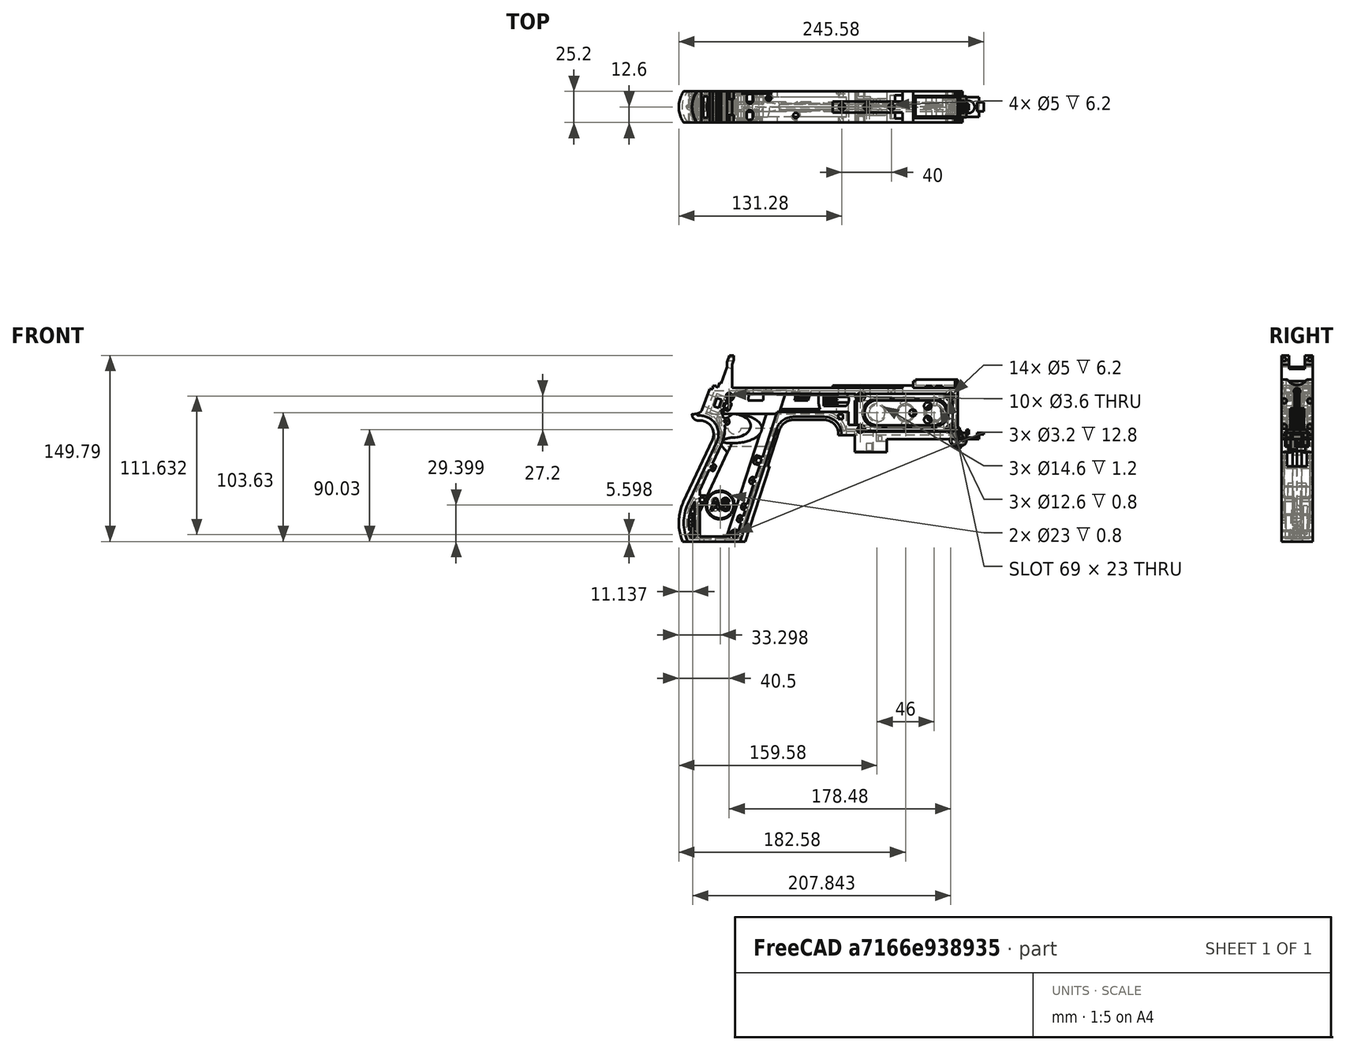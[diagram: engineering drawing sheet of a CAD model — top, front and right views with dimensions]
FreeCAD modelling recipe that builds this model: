
FCSTD DOCUMENT  (FreeCAD 1.0R39319 (Git))
Label: PICON-OF_ver_65
License: All rights reserved
LicenseURL: https://en.wikipedia.org/wiki/All_rights_reserved
objects: Sketcher::SketchObject×132, Part::Extrusion×66, Part::Cut×51, PartDesign::Pad×34, PartDesign::Pocket×21, PartDesign::Chamfer×15, PartDesign::Body×11, PartDesign::Fillet×6, Part::MultiFuse×5, Part::Part2DObjectPython×4, PartDesign::SubtractivePipe×4, PartDesign::SubtractiveLoft×4, PartDesign::Plane×3, PartDesign::SubShapeBinder×2, Part::Sweep×1, PartDesign::ShapeBinder×1, Mesh::Feature×1, PartDesign::Point×1, PartDesign::Groove×1
note: 664 computed .brp shape members not serialized (recipe doc carries the construction recipe); baked Part::Feature solids carry a one-line shape summary decoded from their .brp

FEATURE [Sketcher::SketchObject] Sketch  label="corpo principale"
  ArcFitTolerance = 1e-06
  AttacherType = Attacher::AttachEngine3D
  AttachmentSupport = -> [XZ_Plane]
  FullyConstrained = true
  MakeInternals = false
  MapMode = 5
  Placement = pos=(0,0,0) rot=(1,0,0;1.5708rad)
  sketch-geometry (65):
    g0: LineSegment StartX=0 StartY=0 StartZ=0 EndX=-57.2 EndY=0 EndZ=0
    g1: LineSegment StartX=-57.2 StartY=0 StartZ=0 EndX=-57.2 EndY=-10.4 EndZ=0
    g2: LineSegment StartX=-57.2 StartY=-10.4 StartZ=0 EndX=-82.8 EndY=-10.4 EndZ=0
    g3: LineSegment StartX=-82.8 StartY=-10.4 StartZ=0 EndX=-82.8 EndY=3.2 EndZ=0
    g4: LineSegment StartX=-82.8 StartY=3.2 StartZ=0 EndX=-93.6 EndY=3.2 EndZ=0
    g5: LineSegment StartX=-93.6 StartY=3.2 StartZ=0 EndX=-93.6 EndY=4 EndZ=0
    g6: LineSegment StartX=-107.6 StartY=18 StartZ=0 EndX=-132.428 EndY=18 EndZ=0
    g7: LineSegment StartX=-145.743 StartY=8.32624 StartZ=0 EndX=-175.232 EndY=-82.4316 EndZ=0
    g8: LineSegment StartX=-175.232 StartY=-82.4316 StartZ=0 EndX=-217.232 EndY=-82.4316 EndZ=0
    g9: LineSegment StartX=-217.232 StartY=-52.1862 StartZ=0 EndX=-193.988 EndY=-2.33927 EndZ=0
    g10: LineSegment StartX=-206.196 StartY=23.0857 StartZ=0 EndX=-199.861 EndY=40.4914 EndZ=0
    g11: LineSegment StartX=-199.861 StartY=40.4914 StartZ=0 EndX=-197.061 EndY=40.4914 EndZ=0
    g12: LineSegment StartX=-197.061 StartY=40.4914 StartZ=0 EndX=-197.061 EndY=42.8914 EndZ=0
    g13: LineSegment StartX=-197.061 StartY=42.8914 StartZ=0 EndX=-194.261 EndY=42.8914 EndZ=0
    g14: LineSegment StartX=-194.261 StartY=42.8914 StartZ=0 EndX=-194.535 EndY=42.1397 EndZ=0
    g15: LineSegment StartX=-194.535 StartY=42.1397 StartZ=0 EndX=-193.031 EndY=41.5924 EndZ=0
    g16: LineSegment StartX=-193.031 StartY=41.5924 StartZ=0 EndX=-191.663 EndY=45.3512 EndZ=0
    g17: LineSegment StartX=-191.663 StartY=45.3512 StartZ=0 EndX=-190.536 EndY=44.9408 EndZ=0
    g18: LineSegment StartX=-190.536 StartY=44.9408 StartZ=0 EndX=-185.747 EndY=58.0965 EndZ=0
    g19: LineSegment StartX=-185.747 StartY=58.0965 StartZ=0 EndX=-185.747 EndY=62.0965 EndZ=0
    g20: LineSegment StartX=-185.747 StartY=62.0965 StartZ=0 EndX=-183.832 EndY=67.3588 EndZ=0
    g21: LineSegment StartX=-183.832 StartY=67.3588 StartZ=0 EndX=-180.232 EndY=67.3588 EndZ=0
    g22: LineSegment StartX=-180.232 StartY=67.3588 StartZ=0 EndX=-180.232 EndY=63.7588 EndZ=0
    g23: LineSegment StartX=-180.232 StartY=63.7588 StartZ=0 EndX=-181.6 EndY=60 EndZ=0
    g24: LineSegment StartX=-181.6 StartY=60 StartZ=0 EndX=-181.6 EndY=41.2 EndZ=0
    g25: LineSegment StartX=-181.6 StartY=41.2 StartZ=0 EndX=-100.8 EndY=41.2 EndZ=0
    g26: LineSegment StartX=-36 StartY=43.2 StartZ=0 EndX=-36 EndY=41.2 EndZ=0
    g27: LineSegment StartX=0 StartY=48 StartZ=0 EndX=0 EndY=0 EndZ=0
    g28: LineSegment StartX=-209.901 StartY=19.85 StartZ=0 EndX=-209.901 EndY=20.1 EndZ=0
    g29: LineSegment StartX=-208.001 StartY=22 StartZ=0 EndX=-207.747 EndY=22 EndZ=0
    g30: LineSegment StartX=-207.583 StartY=19 StartZ=0 EndX=-209.051 EndY=19 EndZ=0
    g31: ArcOfCircle CenterX=-208.001 CenterY=20.1 CenterZ=0 NormalX=0 NormalY=0 NormalZ=1 AngleXU=0 Radius=1.9 StartAngle=1.5708 EndAngle=3.14159
    g32: GeomPoint [constr] X=-209.901 Y=22 Z=0
    g33: ArcOfCircle CenterX=-209.051 CenterY=19.85 CenterZ=0 NormalX=0 NormalY=0 NormalZ=1 AngleXU=0 Radius=0.85 StartAngle=3.14159 EndAngle=4.71239
    g34: GeomPoint [constr] X=-209.901 Y=19 Z=0
    g35: ArcOfCircle CenterX=-207.747 CenterY=23.65 CenterZ=0 NormalX=0 NormalY=0 NormalZ=1 AngleXU=0 Radius=1.65 StartAngle=4.71239 EndAngle=5.93412
    g36: GeomPoint [constr] X=-206.591 Y=22 Z=0
    g37: LineSegment StartX=-4 StartY=6 StartZ=0 EndX=-4 EndY=36.4 EndZ=0
    g38: LineSegment StartX=-4 StartY=36.4 StartZ=0 EndX=-185.2 EndY=36.4 EndZ=0
    g39: LineSegment StartX=-185.2 StartY=36.4 StartZ=0 EndX=-190.441 EndY=22 EndZ=0
    g40: LineSegment StartX=-214.575 StartY=-78.4316 StartZ=0 EndX=-178.142 EndY=-78.4316 EndZ=0
    g41: LineSegment StartX=-178.142 StartY=-78.4316 StartZ=0 EndX=-145.51 EndY=22 EndZ=0
    g42: LineSegment StartX=-145.51 StartY=22 StartZ=0 EndX=-87.91 EndY=22 EndZ=0
    g43: LineSegment StartX=-87.91 StartY=22 StartZ=0 EndX=-87.91 EndY=11.6 EndZ=0
    g44: LineSegment StartX=-87.91 StartY=11.6 StartZ=0 EndX=-80.11 EndY=11.6 EndZ=0
    g45: LineSegment StartX=-80.11 StartY=11.6 StartZ=0 EndX=-80.11 EndY=6 EndZ=0
    g46: LineSegment StartX=-80.11 StartY=6 StartZ=0 EndX=-4 EndY=6 EndZ=0
    g47: LineSegment StartX=-190.363 StartY=-4.02975 StartZ=0 EndX=-213.607 EndY=-53.8767 EndZ=0
    g48: ArcOfCircle CenterX=-132.428 CenterY=4 CenterZ=0 NormalX=0 NormalY=0 NormalZ=1 AngleXU=0 Radius=14 StartAngle=1.5708 EndAngle=2.82743
    g49: GeomPoint [constr] X=-142.6 Y=18 Z=0
    g50: ArcOfCircle CenterX=-107.6 CenterY=4 CenterZ=0 NormalX=0 NormalY=0 NormalZ=1 AngleXU=0 Radius=14 StartAngle=0 EndAngle=1.5708
    g51: GeomPoint [constr] X=-93.6 Y=18 Z=0
    g52: ArcOfCircle CenterX=-184.801 CenterY=-67.3089 CenterZ=0 NormalX=0 NormalY=0 NormalZ=1 AngleXU=0 Radius=35.7833 StartAngle=2.70526 EndAngle=3.57792
    g53: ArcOfCircle CenterX=-207.583 CenterY=4 CenterZ=0 NormalX=0 NormalY=0 NormalZ=1 AngleXU=0 Radius=15 StartAngle=5.84685 EndAngle=7.85398
    g54: LineSegment [constr] StartX=-213.607 StartY=-53.8767 StartZ=0 EndX=-217.232 EndY=-52.1862 EndZ=0
    g55: ArcOfCircle CenterX=-184.801 CenterY=-67.3089 CenterZ=0 NormalX=0 NormalY=0 NormalZ=1 AngleXU=0 Radius=31.7833 StartAngle=2.70526 EndAngle=3.49911
    g56: ArcOfCircle CenterX=-218.095 CenterY=8.90192 CenterZ=0 NormalX=0 NormalY=0 NormalZ=1 AngleXU=0 Radius=30.5989 StartAngle=5.84685 EndAngle=6.72553
    g57: LineSegment StartX=-44.6 StartY=43.2 StartZ=0 EndX=-36 EndY=43.2 EndZ=0
    g58: LineSegment StartX=-100.8 StartY=41.2 StartZ=0 EndX=-44.6 EndY=41.2 EndZ=0
    g59: LineSegment StartX=-44.6 StartY=41.2 StartZ=0 EndX=-44.6 EndY=43.2 EndZ=0
    g60: LineSegment StartX=-2.4 StartY=48 StartZ=0 EndX=0 EndY=48 EndZ=0
    g61: LineSegment StartX=-36 StartY=41.2 StartZ=0 EndX=-2.4 EndY=41.2 EndZ=0
    g62: LineSegment StartX=-2.4 StartY=41.2 StartZ=0 EndX=-2.4 EndY=48 EndZ=0
    g63: LineSegment [constr] StartX=-181.6 StartY=36.4 StartZ=0 EndX=-152.209 EndY=36.4 EndZ=0
    g64: LineSegment [constr] StartX=-181.6 StartY=36.4 StartZ=0 EndX=-130.41 EndY=36.4 EndZ=0
  constraints (183):
    c: Coincident(g-1,g0)
    c: PointOnObject(g0,g-1)
    c: Coincident(g0,g1)
    c: Vertical(g1)
    c: Coincident(g1,g2)
    c: Horizontal(g2)
    c: Coincident(g2,g3)
    c: Vertical(g3)
    c: Coincident(g3,g4)
    c: Coincident(g4,g5)
    c: Vertical(g5)
    c: Horizontal(g6)
    c: Coincident(g7,g8)
    c: Horizontal(g8)
    c: Coincident(g10,g11)
    c: Horizontal(g11)
    c: Coincident(g11,g12)
    c: Vertical(g12)
    c: Coincident(g12,g13)
    c: Horizontal(g13)
    c: Coincident(g13,g14)
    c: Coincident(g14,g15)
    c: Coincident(g15,g16)
    c: Coincident(g16,g17)
    c: Coincident(g17,g18)
    c: Coincident(g18,g19)
    c: Vertical(g19)
    c: Coincident(g19,g20)
    c: Coincident(g20,g21)
    c: Horizontal(g21)
    c: Coincident(g21,g22)
    c: Vertical(g22)
    c: Coincident(g22,g23)
    c: Coincident(g23,g24)
    c: Vertical(g24)
    c: Coincident(g24,g25)
    c: Horizontal(g25)
    c: Coincident(g57,g26)
    c: Vertical(g26)
    c: Coincident(g26,g61)
    c: PointOnObject(g60,g-2)
    c: Coincident(g60,g27)
    c: Coincident(g27,g0)
    c: DistanceY(g27,g27) = 48
    c: DistanceY(g1,g1) = 10.4
    c: DistanceX(g0,g0) = 57.2
    c: DistanceX(g2,g2) = 25.6
    c: Horizontal(g4)
    c: DistanceY(g3,g3) = 13.6
    c: DistanceX(g4,g4) = 10.8
    c: DistanceY(g5,g51) = 14.8
    c: DistanceX(g49,g51) = 49
    c: Distance(g7,g49) = 105.6
    c: DistanceX(g61,g60) = 36
    c: DistanceX(g25,g25) = 80.8
    c: DistanceY(g24,g24) = 18.8
    c: DistanceY(g22,g22) = 3.6
    c: Distance(g23) = 4
    c: Angle(g-1,g23) = 1.22173
    c: DistanceX(g21,g21) = 3.6
    c: Distance(g20) = 5.6
    c: Angle(g-1,g20) = 1.22173
    c: DistanceY(g19,g19) = 4
    c: Distance(g18) = 14
    c: Angle(g-1,g18) = 1.22173
    c: Distance(g17) = 1.2
    c: Distance(g16) = 4
    c: Angle(g16) = 1.22173
    c: Perpendicular(g18,g17)
    c: Distance(g15) = 1.6
    c: Perpendicular(g16,g15)
    c: Distance(g14) = 0.8
    c: DistanceX(g13,g13) = 2.8
    c: Perpendicular(g15,g14)
    c: DistanceY(g12,g12) = 2.4
    c: DistanceX(g11,g11) = 2.8
    c: Distance(g9) = 55
    c: Angle(g9,g-1) = 2.00713
    c: Horizontal(g29)
    c: Vertical(g28)
    c: Horizontal(g30)
    c: PointOnObject(g32,g29)
    c: PointOnObject(g32,g28)
    c: Tangent(g29,g31) = 1.5708
    c: Tangent(g28,g31) = 1.5708
    c: PointOnObject(g34,g28)
    c: PointOnObject(g34,g30)
    c: Tangent(g28,g33) = 1.5708
    c: Tangent(g30,g33) = 1.5708
    c: PointOnObject(g36,g29)
    c: PointOnObject(g36,g10)
    c: Tangent(g29,g35) = -1.5708
    c: Tangent(g10,g35) = -1.5708
    c: Angle(g-1,g10) = 1.22173
    c: Radius(g35) = 1.65
    c: Vertical(g37)
    c: Coincident(g37,g38)
    c: Horizontal(g38)
    c: Coincident(g38,g39)
    c: Horizontal(g40)
    c: Coincident(g40,g41)
    c: Coincident(g41,g42)
    c: Horizontal(g42)
    c: Coincident(g42,g43)
    c: Vertical(g43)
    c: Coincident(g43,g44)
    c: Horizontal(g44)
    c: Coincident(g44,g45)
    c: Vertical(g45)
    c: Coincident(g45,g46)
    c: Coincident(g46,g37)
    c: Horizontal(g46)
    c: DistanceY(g0,g37) = 6
    c: DistanceX(g37,g0) = 4
    c: DistanceY(g37,g25) = 4.8
    c: DistanceX(g38,g38) = 181.2
    c: DistanceX(g42,g42) = 57.6
    c: DistanceY(g49,g41) = 4
    c: DistanceX(g41,g49) = 2.91
    c: DistanceY(g43,g43) = 10.4
    c: DistanceX(g44,g44) = 7.8
    c: DistanceY(g7,g40) = 4
    c: Distance(g47) = 55
    c: Angle(g-1,g39) = 1.22173
    c: PointOnObject(g49,g7)
    c: PointOnObject(g49,g6)
    c: Tangent(g7,g48) = -1.5708
    c: Tangent(g6,g48) = -1.5708
    c: PointOnObject(g51,g5)
    c: PointOnObject(g51,g6)
    c: Tangent(g5,g50) = -1.5708
    c: Tangent(g6,g50) = -1.5708
    c: Radius(g50) = 14
    c: Radius(g48) = 14
    c: DistanceX(g8,g8) = 42
    c: Angle(g7,g-1) = 1.88496
    c: Parallel(g41,g7)
    c: Parallel(g47,g9)
    c: Coincident(g52,g8)
    c: Tangent(g52,g9) = 1.5708
    c: DistanceX(g9,g8) = 0
    c: Tangent(g53,g9) = -1.5708
    c: Tangent(g53,g30) = -1.5708
    c: Diameter(g53) = 30
    c: DistanceY(g53,g0) = -4
    c: Coincident(g54,g47)
    c: Distance(g54) = 4
    c: Coincident(g54,g9)
    c: Coincident(g55,g40)
    c: Tangent(g55,g47) = -1.5708
    c: Coincident(g52,g55)
    c: Coincident(g56,g39)
    c: Tangent(g56,g47) = 1.5708
    c: Horizontal(g57)
    c: DistanceX(g57,g57) = 8.6
    c: Coincident(g58,g25)
    c: Horizontal(g58)
    c: Coincident(g59,g58)
    c: Vertical(g59)
    c: DistanceY(g58,g57) = 2
    c: DistanceX(g58,g58) = 56.2
    c: Coincident(g59,g57)
    c: DistanceY(g41,g36) = 0
    c: DistanceY(g36,g39) = 0
    c: DistanceY(g28,g28) = 0.25
    c: DistanceX(g30,g36) = 2.46
    c: DistanceX(g28,g29) = 1.9
    c: Coincident(g62,g60)
    c: Horizontal(g60)
    c: DistanceX(g62,g27) = 2.4
    c: Coincident(g61,g62)
    c: DistanceY(g26,g26) = 2
    c: Vertical(g62)
    c: DistanceY(g61,g60) = 6.8
    c: Horizontal(g61)
    c: Distance(g63) = 29.391
    c: PointOnObject(g63,g38)
    c: PointOnObject(g63,g38)
    c: Distance(g64) = 51.19
    c: PointOnObject(g64,g38)
    c: PointOnObject(g64,g38)
    c: DistanceX(g24,g63) = 0
    c: DistanceX(g24,g64) = 0
FEATURE [Part::Extrusion] Extrude  label="Extrude corpo principale"
  Base = -> Sketch
  Dir = (0,-1,2e-16)
  DirMode = 2
  FaceMakerClass = Part::FaceMakerBullseye
  FaceMakerMode = 3
  LengthFwd = 25.2
  LengthRev = 12.6
  Solid = true
  Symmetric = true
FEATURE [Sketcher::SketchObject] Sketch002  label="scavo grilletto"
  ArcFitTolerance = 1e-06
  AttachmentSupport = -> [XZ_Plane]
  ExternalGeometry = -> [Sketch]
  FullyConstrained = true
  MakeInternals = false
  MapMode = 5
  Placement = pos=(0,0,0) rot=(1,0,0;1.5708rad)
  sketch-geometry (4):
    g0: LineSegment StartX=-89.51 StartY=22 StartZ=0 EndX=-152.71 EndY=22 EndZ=0
    g1: LineSegment StartX=-152.71 StartY=22 StartZ=0 EndX=-167.006 EndY=-22 EndZ=0
    g2: LineSegment StartX=-167.006 StartY=-22 StartZ=0 EndX=-89.51 EndY=-22 EndZ=0
    g3: LineSegment StartX=-89.51 StartY=-22 StartZ=0 EndX=-89.51 EndY=22 EndZ=0
  constraints (12):
    c: Horizontal(g0)
    c: Coincident(g0,g1)
    c: Coincident(g1,g2)
    c: Horizontal(g2)
    c: Coincident(g2,g3)
    c: Coincident(g3,g0)
    c: Vertical(g3)
    c: Angle(g1,g0) = 1.88496
    c: DistanceY(g3,g3) = 44
    c: DistanceX(g0,g0) = 63.2
    c: DistanceX(g0,g-3) = 1.6
    c: DistanceY(g-3,g0) = 0
FEATURE [Sketcher::SketchObject] Sketch004  label="traiettoria arrotondamento impugnatura anteriore"
  ArcFitTolerance = 1e-06
  AttachmentSupport = -> [XZ_Plane]
  ExternalGeometry = -> [Sketch]
  FullyConstrained = true
  MakeInternals = false
  MapMode = 5
  Placement = pos=(0,0,0) rot=(1,0,0;1.5708rad)
  sketch-geometry (13):
    g0: LineSegment StartX=-175.232 StartY=-82.4316 StartZ=0 EndX=-145.743 EndY=8.32624 EndZ=0
    g1: LineSegment StartX=-93.6 StartY=3.2 StartZ=0 EndX=-93.6 EndY=4 EndZ=0
    g2: LineSegment StartX=-132.428 StartY=18 StartZ=0 EndX=-107.6 EndY=18 EndZ=0
    g3: ArcOfCircle CenterX=-132.428 CenterY=4 CenterZ=0 NormalX=0 NormalY=0 NormalZ=1 AngleXU=0 Radius=14 StartAngle=1.5708 EndAngle=2.82743
    g4: ArcOfCircle CenterX=-107.6 CenterY=4 CenterZ=0 NormalX=0 NormalY=0 NormalZ=1 AngleXU=0 Radius=14 StartAngle=0 EndAngle=1.5708
    g5: LineSegment StartX=-175.232 StartY=-82.4316 StartZ=0 EndX=-217.232 EndY=-82.4316 EndZ=0
    g6: LineSegment StartX=-217.232 StartY=-52.1862 StartZ=0 EndX=-193.988 EndY=-2.33927 EndZ=0
    g7: LineSegment StartX=-209.051 StartY=19 StartZ=0 EndX=-207.583 EndY=19 EndZ=0
    g8: LineSegment StartX=-209.901 StartY=20.1 StartZ=0 EndX=-209.901 EndY=19.85 EndZ=0
    g9: ArcOfCircle CenterX=-184.801 CenterY=-67.3089 CenterZ=0 NormalX=0 NormalY=0 NormalZ=1 AngleXU=0 Radius=35.7833 StartAngle=2.70526 EndAngle=3.57792
    g10: ArcOfCircle CenterX=-207.583 CenterY=4 CenterZ=0 NormalX=0 NormalY=0 NormalZ=1 AngleXU=0 Radius=15 StartAngle=5.84685 EndAngle=7.85398
    g11: ArcOfCircle CenterX=-209.051 CenterY=19.85 CenterZ=0 NormalX=0 NormalY=0 NormalZ=1 AngleXU=0 Radius=0.85 StartAngle=3.14159 EndAngle=4.71239
    g12: ArcOfCircle CenterX=-208.001 CenterY=20.1 CenterZ=0 NormalX=0 NormalY=0 NormalZ=1 AngleXU=0 Radius=1.9 StartAngle=1.5708 EndAngle=3.14159
  constraints (26):
    c: Coincident(g0,g-3)
    c: Coincident(g0,g-6)
    c: Coincident(g1,g-8)
    c: Coincident(g1,g-7)
    c: Coincident(g2,g-5)
    c: Coincident(g2,g-4)
    c: Coincident(g3,g2)
    c: Tangent(g3,g0) = 1.5708
    c: Coincident(g4,g1)
    c: Tangent(g4,g2) = 1.5708
    c: Coincident(g5,g0)
    c: Coincident(g5,g-9)
    c: Coincident(g6,g-12)
    c: Coincident(g6,g-11)
    c: Coincident(g7,g-15)
    c: Coincident(g7,g-14)
    c: Coincident(g8,g-16)
    c: Coincident(g8,g-17)
    c: Tangent(g9,g6) = 1.5708
    c: Coincident(g9,g5)
    c: Coincident(g10,g7)
    c: Tangent(g10,g6) = -1.5708
    c: Tangent(g11,g7) = -1.5708
    c: Coincident(g11,g8)
    c: Tangent(g12,g8) = -1.5708
    c: Coincident(g12,g-17)
FEATURE [PartDesign::Plane] DatumPlane  label="Piano per disegno arrotondamento impugnatura"
  AttachmentSupport = -> [Sketch]
  Length = 73.6581
  MapMode = 7
  Placement = pos=(-145.743,1.8e-15,8.32624) rot=(0.154555,0.154555,0.97582;1.59527rad)
  ResizeMode = 0
  Width = 303.511
FEATURE [Sketcher::SketchObject] Sketch005  label="forma arrotondamento impugnatura anteriore"
  ArcFitTolerance = 1e-06
  AttachmentSupport = -> [DatumPlane]
  FullyConstrained = true
  MakeInternals = false
  MapMode = 5
  Placement = pos=(-145.743,1.8e-15,8.32624) rot=(0.154555,0.154555,0.97582;1.59527rad)
  sketch-geometry (5):
    g0: GeomPoint [constr] X=0 Y=-4 Z=0
    g1: GeomPoint [constr] X=-12.6 Y=7.1e-15 Z=0
    g2: GeomPoint [constr] X=12.6 Y=4.97e-14 Z=0
    g3: LineSegment StartX=-12.6 StartY=7.1e-15 StartZ=0 EndX=12.6 EndY=4.97e-14 EndZ=0
    g4: ArcOfCircle CenterX=-3.88e-14 CenterY=17.845 CenterZ=0 NormalX=0 NormalY=0 NormalZ=1 AngleXU=0 Radius=21.845 StartAngle=4.09759 EndAngle=5.32718
  constraints (11):
    c: DistanceY(g0,g-1) = 4
    c: DistanceX(g-1,g0) = 0
    c: DistanceX(g1,g-1) = 12.6
    c: DistanceX(g-1,g2) = 12.6
    c: DistanceY(g-1,g2) = 0
    c: DistanceY(g-1,g1) = 0
    c: Coincident(g3,g1)
    c: Coincident(g3,g2)
    c: Coincident(g4,g1)
    c: Coincident(g4,g2)
    c: PointOnObject(g0,g4)
FEATURE [Part::Sweep] Sweep  label="Sweep impugnatura"
  Frenet = true
  Sections = -> [Sketch005]
  Solid = true
  Spine = -> Sketch [Edge32,Edge33,Edge34,Edge35,Edge36,Edge37,Edge38,Edge39,Edge40,Edge41,Edge42,Edge43,Edge44]
  Transition = 1
FEATURE [Sketcher::SketchObject] Sketch008  label="buchi e pulizie varie"
  ArcFitTolerance = 1e-06
  AttachmentSupport = -> [XZ_Plane]
  ExternalGeometry = -> [Sketch]
  FullyConstrained = true
  MakeInternals = false
  MapMode = 5
  Placement = pos=(0,0,0) rot=(1,0,0;1.5708rad)
  sketch-geometry (26):
    g0: LineSegment StartX=-96.278 StartY=20.155 StartZ=0 EndX=-92.278 EndY=20.155 EndZ=0
    g1: LineSegment StartX=-92.278 StartY=20.155 StartZ=0 EndX=-92.278 EndY=16.155 EndZ=0
    g2: LineSegment StartX=-92.278 StartY=16.155 StartZ=0 EndX=-96.278 EndY=16.155 EndZ=0
    g3: LineSegment StartX=-96.278 StartY=16.155 StartZ=0 EndX=-96.278 EndY=20.155 EndZ=0
    g4: LineSegment StartX=-222.232 StartY=-82.4316 StartZ=0 EndX=-170.232 EndY=-82.4316 EndZ=0
    g5: LineSegment StartX=-170.232 StartY=-82.4316 StartZ=0 EndX=-170.232 EndY=-86.4316 EndZ=0
    g6: LineSegment StartX=-170.232 StartY=-86.4316 StartZ=0 EndX=-222.232 EndY=-86.4316 EndZ=0
    g7: LineSegment StartX=-222.232 StartY=-86.4316 StartZ=0 EndX=-222.232 EndY=-82.4316 EndZ=0
    g8: LineSegment StartX=-213.901 StartY=20.1 StartZ=0 EndX=-213.901 EndY=26 EndZ=0
    g9: LineSegment StartX=-213.901 StartY=26 StartZ=0 EndX=-206.196 EndY=26 EndZ=0
    g10: LineSegment StartX=-17.4 StartY=42.8 StartZ=0 EndX=-12.4 EndY=42.8 EndZ=0
    g11: LineSegment StartX=-12.4 StartY=42.8 StartZ=0 EndX=-12.4 EndY=41.2 EndZ=0
    g12: LineSegment StartX=-12.4 StartY=41.2 StartZ=0 EndX=-17.4 EndY=41.2 EndZ=0
    g13: LineSegment StartX=-17.4 StartY=41.2 StartZ=0 EndX=-17.4 EndY=42.8 EndZ=0
    g14: LineSegment StartX=-25.9 StartY=42.8 StartZ=0 EndX=-20.9 EndY=42.8 EndZ=0
    g15: LineSegment StartX=-20.9 StartY=42.8 StartZ=0 EndX=-20.9 EndY=41.2 EndZ=0
    g16: LineSegment StartX=-20.9 StartY=41.2 StartZ=0 EndX=-25.9 EndY=41.2 EndZ=0
    g17: LineSegment StartX=-25.9 StartY=41.2 StartZ=0 EndX=-25.9 EndY=42.8 EndZ=0
    g18: GeomPoint [constr] X=-206.196 Y=23.0857 Z=0
    g19: GeomPoint [constr] X=-213.901 Y=20.1 Z=0
    g20: BSplineCurve PolesCount=4 KnotsCount=2 Degree=3 IsPeriodic=0
    g21-g24: Circle [constr] x4 (B-spline internal-alignment scaffolding for g20; pole/knot coordinates omitted)
    g25: LineSegment StartX=-206.196 StartY=26 StartZ=0 EndX=-206.196 EndY=23.0857 EndZ=0
  constraints (73):
    c: Horizontal(g0)
    c: Coincident(g1,g0)
    c: Vertical(g1)
    c: Coincident(g2,g1)
    c: Horizontal(g2)
    c: Coincident(g3,g2)
    c: Coincident(g3,g0)
    c: Vertical(g3)
    c: DistanceX(g0,g-4) = 4.368
    c: DistanceY(g0,g-4) = 1.845
    c: DistanceY(g1,g1) = 4
    c: DistanceX(g2,g2) = 4
    c: Horizontal(g4)
    c: Coincident(g5,g4)
    c: Vertical(g5)
    c: Coincident(g6,g5)
    c: Horizontal(g6)
    c: Coincident(g7,g6)
    c: Coincident(g7,g4)
    c: Vertical(g7)
    c: DistanceY(g7,g7) = 4
    c: DistanceX(g4,g-5) = 5
    c: DistanceX(g-5,g4) = 5
    c: DistanceY(g4,g-5) = 0
    c: Coincident(g9,g8)
    c: Parallel(g9,g-6)
    c: DistanceX(g8,g-8) = 4
    c: Horizontal(g10)
    c: Coincident(g11,g10)
    c: Vertical(g11)
    c: Coincident(g12,g11)
    c: Horizontal(g12)
    c: Coincident(g13,g12)
    c: Coincident(g13,g10)
    c: Vertical(g13)
    c: Horizontal(g14)
    c: Coincident(g15,g14)
    c: Vertical(g15)
    c: Coincident(g16,g15)
    c: Horizontal(g16)
    c: Coincident(g17,g16)
    c: Coincident(g17,g14)
    c: Vertical(g17)
    c: DistanceY(g11,g10) = 1.6
    c: DistanceX(g10,g10) = 5
    c: DistanceY(g15,g14) = 1.6
    c: DistanceX(g14,g14) = 5
    c: DistanceX(g15,g12) = 3.5
    c: DistanceX(g11,g-9) = 10
    c: DistanceY(g-9,g11) = 0
    c: DistanceY(g-9,g15) = 0
    c: Perpendicular(g8,g9)
    c: DistanceY(g-7,g9) = 4
    c: DistanceY(g8,g-8) = 0
    c: InternalAlignment(g18,g20)
    c: InternalAlignment(g19,g20)
    c: InternalAlignment(g21,g20)
    c: Weight(g21) = 1
    c: InternalAlignment(g22,g20)
    c: Equal(g22,g21)
    c: InternalAlignment(g23,g20)
    c: Equal(g23,g21)
    c: InternalAlignment(g24,g20)
    c: Equal(g24,g21)
    c: Coincident(g18,g-12)
    c: Coincident(g19,g8)
    c: Coincident(g25,g9)
    c: Coincident(g25,g20)
    c: Vertical(g25)
    c: DistanceY(g20,g23) = 0
    c: DistanceY(g22,g18) = 2.26
    c: DistanceX(g22,g18) = 0.93
    c: DistanceX(g20,g23) = 2.9
FEATURE [Part::Extrusion] Extrude004  label="Extrude Buchi e pulizie varie"
  Base = -> Sketch008
  Dir = (0,-1,2e-16)
  DirMode = 2
  FaceMakerClass = Part::FaceMakerBullseye
  FaceMakerMode = 3
  LengthFwd = 25.2
  LengthRev = 0
  Solid = true
  Symmetric = true
FEATURE [Sketcher::SketchObject] Sketch009  label="rinforzi"
  ArcFitTolerance = 1e-06
  AttachmentSupport = -> [XZ_Plane]
  ExternalGeometry = -> [Sketch]
  FullyConstrained = true
  MakeInternals = false
  MapMode = 5
  Placement = pos=(0,0,0) rot=(1,0,0;1.5708rad)
  sketch-geometry (9):
    g0: LineSegment StartX=-87.91 StartY=22 StartZ=0 EndX=-87.91 EndY=36.4 EndZ=0
    g1: LineSegment StartX=-87.91 StartY=36.4 StartZ=0 EndX=-97.91 EndY=36.4 EndZ=0
    g2: LineSegment StartX=-97.91 StartY=36.4 StartZ=0 EndX=-97.91 EndY=22 EndZ=0
    g3: LineSegment StartX=-97.91 StartY=22 StartZ=0 EndX=-87.91 EndY=22 EndZ=0
    g4: LineSegment StartX=-149.713 StartY=9.06563 StartZ=0 EndX=-154.586 EndY=-5.93437 EndZ=0
    g5: LineSegment StartX=-154.586 StartY=-5.93437 StartZ=0 EndX=-191.863 EndY=-5.93437 EndZ=0
    g6: LineSegment StartX=-191.863 StartY=-5.93437 StartZ=0 EndX=-191.863 EndY=9.06563 EndZ=0
    g7: LineSegment StartX=-191.863 StartY=9.06563 StartZ=0 EndX=-149.713 EndY=9.06563 EndZ=0
    g8: LineSegment [constr] StartX=-145.51 StartY=22 StartZ=0 EndX=-149.713 EndY=9.06563 EndZ=0
  constraints (25):
    c: Vertical(g0)
    c: Coincident(g1,g0)
    c: Horizontal(g1)
    c: Coincident(g2,g1)
    c: Vertical(g2)
    c: Coincident(g3,g2)
    c: Coincident(g3,g0)
    c: Horizontal(g3)
    c: Coincident(g0,g-4)
    c: DistanceX(g3,g3) = 10
    c: DistanceY(g0,g-3) = 0
    c: Coincident(g5,g4)
    c: Horizontal(g5)
    c: Coincident(g6,g5)
    c: Vertical(g6)
    c: Coincident(g7,g6)
    c: Coincident(g7,g4)
    c: Horizontal(g7)
    c: Distance(g8) = 13.6
    c: Parallel(g-6,g8)
    c: Coincident(g-6,g8)
    c: Parallel(g4,g-6)
    c: DistanceY(g4,g4) = 15
    c: Coincident(g4,g8)
    c: DistanceX(g-5,g5) = -1.5
FEATURE [Part::Extrusion] Extrude001  label="Extrude scavo grilletto"
  Base = -> Sketch002
  Dir = (0,-1,2e-16)
  DirMode = 2
  FaceMakerClass = Part::FaceMakerBullseye
  FaceMakerMode = 3
  LengthFwd = 16
  LengthRev = 0
  Solid = true
  Symmetric = true
FEATURE [Part::Extrusion] Extrude005  label="Extrude Rinforzi"
  Base = -> Sketch009
  Dir = (0,-1,2e-16)
  DirMode = 2
  FaceMakerClass = Part::FaceMakerBullseye
  FaceMakerMode = 3
  LengthFwd = 2
  LengthRev = 0
  Placement = pos=(0,12.6,0) rot=(0,0,1;0rad)
  Solid = true
  Symmetric = false
FEATURE [PartDesign::ShapeBinder] CopyCut
  TraceSupport = false
FEATURE [PartDesign::Plane] DatumPlane001
  AttachmentSupport = -> [CopyCut]
  Length = 283.944
  MapMode = 5
  Placement = pos=(0,12.6,0) rot=(0,0.707107,0.707107;3.14159rad)
  ResizeMode = 0
  Width = 188.15
FEATURE [Sketcher::SketchObject] Sketch010  label="buco neopixel"
  ArcFitTolerance = 1e-06
  AttachmentSupport = -> [XZ_Plane]
  ExternalGeometry = -> [Sketch]
  FullyConstrained = true
  MakeInternals = false
  MapMode = 5
  Placement = pos=(0,0,0) rot=(1,0,0;1.5708rad)
  sketch-geometry (5):
    g0: LineSegment [constr] StartX=-199.861 StartY=40.4914 StartZ=0 EndX=-201.368 EndY=36.3521 EndZ=0
    g1: LineSegment StartX=-201.368 StartY=36.3521 StartZ=0 EndX=-204.932 EndY=26.5605 EndZ=0
    g2: LineSegment StartX=-201.368 StartY=36.3521 StartZ=0 EndX=-180.2 EndY=28.6477 EndZ=0
    g3: LineSegment StartX=-180.2 StartY=28.6477 StartZ=0 EndX=-183.764 EndY=18.8561 EndZ=0
    g4: LineSegment StartX=-183.764 StartY=18.8561 StartZ=0 EndX=-204.932 EndY=26.5605 EndZ=0
  constraints (14):
    c: Parallel(g0,g-3)
    c: Distance(g0) = 4.405
    c: Coincident(g0,g-3)
    c: Coincident(g2,g1)
    c: Coincident(g3,g2)
    c: Coincident(g4,g3)
    c: Coincident(g4,g1)
    c: Parallel(g1,g-3)
    c: Distance(g1) = 10.42
    c: Coincident(g1,g0)
    c: Parallel(g2,g4)
    c: Perpendicular(g1,g2)
    c: DistanceX(g-4,g2) = 5
    c: Parallel(g3,g1)
FEATURE [Part::Extrusion] Extrude006  label="Extrude buco neopixel"
  Base = -> Sketch010
  Dir = (0,-1,2e-16)
  DirMode = 2
  FaceMakerClass = Part::FaceMakerBullseye
  FaceMakerMode = 3
  LengthFwd = 17.2
  LengthRev = 0
  Solid = true
  Symmetric = true
FEATURE [Sketcher::SketchObject] Sketch011  label="fermo grilletto"
  ArcFitTolerance = 1e-06
  AttachmentSupport = -> [XZ_Plane]
  ExternalGeometry = -> [Sketch]
  FullyConstrained = true
  MakeInternals = false
  MapMode = 5
  Placement = pos=(0,0,0) rot=(1,0,0;1.5708rad)
  sketch-geometry (18):
    g0: LineSegment [constr] StartX=-145.51 StartY=22 StartZ=0 EndX=-157.347 EndY=-14.4293 EndZ=0
    g1: LineSegment [constr] StartX=-157.347 StartY=-14.4293 StartZ=0 EndX=-157.841 EndY=-15.951 EndZ=0
    g2: LineSegment StartX=-161.151 StartY=-13.1932 StartZ=0 EndX=-155.825 EndY=-14.9237 EndZ=0
    g3: LineSegment StartX=-163.167 StartY=-14.2205 StartZ=0 EndX=-164.403 EndY=-18.0247 EndZ=0
    g4: LineSegment StartX=-163.376 StartY=-20.0408 StartZ=0 EndX=-158.05 EndY=-21.7713 EndZ=0
    g5: LineSegment StartX=-158.05 StartY=-21.7713 StartZ=0 EndX=-155.825 EndY=-14.9237 EndZ=0
    g6: LineSegment StartX=-161.645 StartY=-14.7149 StartZ=0 EndX=-157.841 EndY=-15.951 EndZ=0
    g7: LineSegment StartX=-157.841 StartY=-15.951 StartZ=0 EndX=-159.077 EndY=-19.7552 EndZ=0
    g8: LineSegment StartX=-159.077 StartY=-19.7552 StartZ=0 EndX=-162.881 EndY=-18.5191 EndZ=0
    g9: LineSegment StartX=-162.881 StartY=-18.5191 StartZ=0 EndX=-161.645 EndY=-14.7149 EndZ=0
    g10: LineSegment [constr] StartX=-161.645 StartY=-14.7149 StartZ=0 EndX=-161.151 EndY=-13.1932 EndZ=0
    g11: LineSegment [constr] StartX=-159.077 StartY=-19.7552 StartZ=0 EndX=-157.555 EndY=-20.2496 EndZ=0
    g12: LineSegment [constr] StartX=-159.077 StartY=-19.7552 StartZ=0 EndX=-159.572 EndY=-21.2769 EndZ=0
    g13: LineSegment [constr] StartX=-161.645 StartY=-14.7149 StartZ=0 EndX=-163.167 EndY=-14.2205 EndZ=0
    g14: ArcOfCircle CenterX=-161.645 CenterY=-14.7149 CenterZ=0 NormalX=0 NormalY=0 NormalZ=1 AngleXU=0 Radius=1.6 StartAngle=1.25664 EndAngle=2.82743
    g15: GeomPoint [constr] X=-162.673 Y=-12.6988 Z=0
    g16: ArcOfCircle CenterX=-162.881 CenterY=-18.5191 CenterZ=0 NormalX=0 NormalY=0 NormalZ=1 AngleXU=0 Radius=1.6 StartAngle=2.82743 EndAngle=4.39823
    g17: GeomPoint [constr] X=-164.897 Y=-19.5464 Z=0
  constraints (48):
    c: Parallel(g0,g-3)
    c: Distance(g0) = 38.304
    c: Coincident(g0,g-3)
    c: Parallel(g1,g-3)
    c: Distance(g1) = 1.6
    c: Coincident(g1,g0)
    c: Coincident(g5,g4)
    c: Coincident(g5,g2)
    c: Coincident(g7,g6)
    c: Coincident(g8,g7)
    c: Coincident(g9,g8)
    c: Coincident(g9,g6)
    c: Parallel(g7,g-3)
    c: Parallel(g9,g7)
    c: Perpendicular(g6,g7)
    c: Parallel(g6,g8)
    c: Distance(g6) = 4
    c: Distance(g9) = 4
    c: Parallel(g5,g7)
    c: Parallel(g9,g3)
    c: Parallel(g2,g6)
    c: Parallel(g4,g8)
    c: Parallel(g13,g6)
    c: Parallel(g10,g9)
    c: Parallel(g11,g8)
    c: Parallel(g12,g7)
    c: Distance(g10) = 1.6
    c: Distance(g13) = 1.6
    c: Distance(g12) = 1.6
    c: Distance(g11) = 1.6
    c: Coincident(g10,g6)
    c: Coincident(g13,g6)
    c: Coincident(g12,g7)
    c: Coincident(g11,g7)
    c: Distance(g10,g15) = 1.6
    c: Distance(g15,g13) = 1.6
    c: Distance(g4,g12) = 1.6
    c: Distance(g4,g11) = 1.6
    c: PointOnObject(g15,g2)
    c: Tangent(g3,g14) = -1.5708
    c: Tangent(g2,g14) = 1.5708
    c: PointOnObject(g17,g4)
    c: PointOnObject(g17,g3)
    c: Tangent(g4,g16) = -1.5708
    c: Tangent(g3,g16) = -1.5708
    c: Equal(g16,g14)
    c: Coincident(g16,g8)
    c: Coincident(g6,g1)
FEATURE [Part::Extrusion] Extrude007  label="Extrude fermo grilletto"
  Base = -> Sketch011
  Dir = (0,-1,2e-16)
  DirMode = 2
  FaceMakerClass = Part::FaceMakerBullseye
  FaceMakerMode = 3
  LengthFwd = 25.2
  LengthRev = 0
  Solid = true
  Symmetric = true
FEATURE [Sketcher::SketchObject] Sketch012  label="buco oled"
  ArcFitTolerance = 1e-06
  AttachmentSupport = -> [XZ_Plane]
  ExternalGeometry = -> [Sketch]
  FullyConstrained = true
  MakeInternals = false
  MapMode = 5
  Placement = pos=(0,0,0) rot=(1,0,0;1.5708rad)
  sketch-geometry (4):
    g0: LineSegment StartX=-185.747 StartY=58.0965 StartZ=0 EndX=-180.232 EndY=56.0891 EndZ=0
    g1: LineSegment StartX=-185.747 StartY=58.0965 StartZ=0 EndX=-185.747 EndY=67.3588 EndZ=0
    g2: LineSegment StartX=-185.747 StartY=67.3588 StartZ=0 EndX=-180.232 EndY=67.3588 EndZ=0
    g3: LineSegment StartX=-180.232 StartY=67.3588 StartZ=0 EndX=-180.232 EndY=56.0891 EndZ=0
  constraints (10):
    c: Coincident(g1,g0)
    c: Coincident(g2,g1)
    c: Coincident(g3,g2)
    c: Coincident(g3,g0)
    c: Parallel(g1,g-5)
    c: Perpendicular(g-3,g0)
    c: Parallel(g2,g-6)
    c: Parallel(g3,g-4)
    c: Coincident(g0,g-5)
    c: Coincident(g2,g-6)
FEATURE [Part::Extrusion] Extrude008  label="Extrude buco oled"
  Base = -> Sketch012
  Dir = (0,-1,2e-16)
  DirMode = 2
  FaceMakerClass = Part::FaceMakerBullseye
  FaceMakerMode = 3
  LengthFwd = 12.8
  LengthRev = 0
  Solid = true
  Symmetric = true
FEATURE [Sketcher::SketchObject] Sketch013  label="buco pompa"
  ArcFitTolerance = 1e-06
  AttachmentSupport = -> [XZ_Plane]
  ExternalGeometry = -> [Sketch]
  FullyConstrained = true
  MakeInternals = false
  MapMode = 5
  Placement = pos=(0,0,0) rot=(1,0,0;1.5708rad)
  sketch-geometry (8):
    g0: LineSegment StartX=-82.8 StartY=-10.4 StartZ=0 EndX=-82.8 EndY=-9.6 EndZ=0
    g1: LineSegment StartX=-82.8 StartY=-9.6 StartZ=0 EndX=-67.9 EndY=-9.6 EndZ=0
    g2: LineSegment StartX=-67.9 StartY=-9.6 StartZ=0 EndX=-67.9 EndY=6 EndZ=0
    g3: LineSegment StartX=-67.9 StartY=6 StartZ=0 EndX=-65.9 EndY=6 EndZ=0
    g4: LineSegment StartX=-65.9 StartY=6 StartZ=0 EndX=-65.9 EndY=-1.7 EndZ=0
    g5: LineSegment StartX=-65.9 StartY=-1.7 StartZ=0 EndX=-57.2 EndY=-1.7 EndZ=0
    g6: LineSegment StartX=-57.2 StartY=-1.7 StartZ=0 EndX=-57.2 EndY=-10.4 EndZ=0
    g7: LineSegment StartX=-57.2 StartY=-10.4 StartZ=0 EndX=-82.8 EndY=-10.4 EndZ=0
  constraints (22):
    c: Vertical(g0)
    c: Coincident(g1,g0)
    c: Horizontal(g1)
    c: Coincident(g2,g1)
    c: Vertical(g2)
    c: Coincident(g3,g2)
    c: Horizontal(g3)
    c: Coincident(g4,g3)
    c: Vertical(g4)
    c: Coincident(g5,g4)
    c: Horizontal(g5)
    c: Coincident(g6,g5)
    c: Vertical(g6)
    c: Coincident(g7,g6)
    c: Coincident(g7,g0)
    c: DistanceY(g0,g0) = 0.8
    c: DistanceY(g6,g6) = 8.7
    c: DistanceX(g1,g1) = 14.9
    c: DistanceX(g3,g3) = 2
    c: Coincident(g0,g-4)
    c: DistanceY(g2,g-6) = 0
    c: Coincident(g6,g-5)
FEATURE [Part::Extrusion] Extrude009  label="Extrude buco pompa"
  Base = -> Sketch013
  Dir = (0,-1,2e-16)
  DirMode = 2
  FaceMakerClass = Part::FaceMakerBullseye
  FaceMakerMode = 3
  LengthFwd = 13.2
  LengthRev = 0
  Solid = true
  Symmetric = true
FEATURE [Sketcher::SketchObject] Sketch014  label="buco frontale"
  ArcFitTolerance = 1e-06
  AttachmentSupport = -> [XZ_Plane]
  ExternalGeometry = -> [Sketch]
  FullyConstrained = true
  MakeInternals = false
  MapMode = 5
  Placement = pos=(0,0,0) rot=(1,0,0;1.5708rad)
  sketch-geometry (10):
    g0: LineSegment StartX=0 StartY=0 StartZ=0 EndX=0 EndY=24.671 EndZ=0
    g1: LineSegment StartX=0 StartY=24.671 StartZ=0 EndX=-4 EndY=24.671 EndZ=0
    g2: LineSegment StartX=-4 StartY=24.671 StartZ=0 EndX=-4 EndY=16 EndZ=0
    g3: LineSegment StartX=-4 StartY=16 StartZ=0 EndX=-2.4 EndY=16 EndZ=0
    g4: LineSegment StartX=-2.4 StartY=16 StartZ=0 EndX=-2.4 EndY=10 EndZ=0
    g5: LineSegment StartX=-2.4 StartY=10 StartZ=0 EndX=-12 EndY=10 EndZ=0
    g6: LineSegment StartX=-12 StartY=10 StartZ=0 EndX=-12 EndY=6 EndZ=0
    g7: LineSegment StartX=-12 StartY=6 StartZ=0 EndX=-2.4 EndY=6 EndZ=0
    g8: LineSegment StartX=-2.4 StartY=6 StartZ=0 EndX=-2.4 EndY=0 EndZ=0
    g9: LineSegment StartX=-2.4 StartY=0 StartZ=0 EndX=0 EndY=0 EndZ=0
  constraints (29):
    c: Vertical(g0)
    c: Coincident(g1,g0)
    c: Horizontal(g1)
    c: Coincident(g2,g1)
    c: Vertical(g2)
    c: Coincident(g3,g2)
    c: Horizontal(g3)
    c: Coincident(g4,g3)
    c: Vertical(g4)
    c: Coincident(g5,g4)
    c: Horizontal(g5)
    c: Coincident(g6,g5)
    c: Vertical(g6)
    c: Coincident(g7,g6)
    c: Coincident(g8,g7)
    c: Vertical(g8)
    c: Coincident(g9,g8)
    c: Coincident(g9,g0)
    c: Horizontal(g9)
    c: DistanceY(g0,g0) = 24.671
    c: Horizontal(g7)
    c: DistanceY(g6,g6) = 4
    c: DistanceY(g4,g4) = 6
    c: DistanceX(g9,g9) = 2.4
    c: Coincident(g0,g-1)
    c: DistanceY(g-3,g7) = 0
    c: DistanceX(g8,g4) = 0
    c: DistanceX(g-3,g1) = 0
    c: DistanceX(g6,g-3) = 8
FEATURE [Part::Extrusion] Extrude010  label="Extrude buco frontale"
  Base = -> Sketch014
  Dir = (0,-1,2e-16)
  DirMode = 2
  FaceMakerClass = Part::FaceMakerBullseye
  FaceMakerMode = 3
  LengthFwd = 11.2
  LengthRev = 0
  Solid = true
  Symmetric = true
FEATURE [Sketcher::SketchObject] Sketch015  label="guida rail"
  ArcFitTolerance = 1e-06
  AttachmentSupport = -> [XZ_Plane]
  ExternalGeometry = -> [Sketch]
  FullyConstrained = true
  MakeInternals = false
  MapMode = 5
  Placement = pos=(0,0,0) rot=(1,0,0;1.5708rad)
  sketch-geometry (4):
    g0: LineSegment StartX=-100.8 StartY=43.2 StartZ=0 EndX=-44.6 EndY=43.2 EndZ=0
    g1: LineSegment StartX=-44.6 StartY=43.2 StartZ=0 EndX=-44.6 EndY=41.2 EndZ=0
    g2: LineSegment StartX=-44.6 StartY=41.2 StartZ=0 EndX=-100.8 EndY=41.2 EndZ=0
    g3: LineSegment StartX=-100.8 StartY=41.2 StartZ=0 EndX=-100.8 EndY=43.2 EndZ=0
  constraints (9):
    c: Horizontal(g0)
    c: Coincident(g1,g0)
    c: Coincident(g2,g1)
    c: Coincident(g3,g2)
    c: Coincident(g3,g0)
    c: Vertical(g3)
    c: Coincident(g2,g-3)
    c: Coincident(g1,g-3)
    c: Coincident(g0,g-4)
FEATURE [Part::Extrusion] Extrude011  label="Extrude guida rail"
  Base = -> Sketch015
  Dir = (0,-1,2e-16)
  DirMode = 2
  FaceMakerClass = Part::FaceMakerBullseye
  FaceMakerMode = 3
  LengthFwd = 9
  LengthRev = 0
  Solid = true
  Symmetric = true
FEATURE [Sketcher::SketchObject] Sketch016  label="guide per coperture laterali"
  ArcFitTolerance = 1e-06
  AttachmentSupport = -> [XZ_Plane]
  ExternalGeometry = -> [Sketch]
  FullyConstrained = true
  MakeInternals = false
  MapMode = 5
  Placement = pos=(0,0,0) rot=(1,0,0;1.5708rad)
  sketch-geometry (14):
    g0: Circle CenterX=-5.6 CenterY=7.6 CenterZ=0 NormalX=0 NormalY=0 NormalZ=1 AngleXU=0 Radius=1.6
    g1: Circle CenterX=-5.6 CenterY=7.6 CenterZ=0 NormalX=0 NormalY=0 NormalZ=1 AngleXU=0 Radius=4
    g2: Circle CenterX=-5.6 CenterY=34.8 CenterZ=0 NormalX=0 NormalY=0 NormalZ=1 AngleXU=0 Radius=1.6
    g3: Circle CenterX=-5.6 CenterY=34.8 CenterZ=0 NormalX=0 NormalY=0 NormalZ=1 AngleXU=0 Radius=4
    g4: Circle CenterX=-184.08 CenterY=34.8 CenterZ=0 NormalX=0 NormalY=0 NormalZ=1 AngleXU=0 Radius=1.6
    g5: Circle CenterX=-184.08 CenterY=34.8 CenterZ=0 NormalX=0 NormalY=0 NormalZ=1 AngleXU=0 Radius=4
    g6: Circle CenterX=-179.305 CenterY=-76.8316 CenterZ=0 NormalX=0 NormalY=0 NormalZ=1 AngleXU=0 Radius=1.6
    g7: Circle CenterX=-179.305 CenterY=-76.8316 CenterZ=0 NormalX=0 NormalY=0 NormalZ=1 AngleXU=0 Radius=4
    g8: Circle CenterX=-213.443 CenterY=-76.8316 CenterZ=0 NormalX=0 NormalY=0 NormalZ=1 AngleXU=0 Radius=1.6
    g9: Circle CenterX=-213.443 CenterY=-76.8316 CenterZ=0 NormalX=0 NormalY=0 NormalZ=1 AngleXU=0 Radius=4
    g10: Circle CenterX=-78.51 CenterY=7.6 CenterZ=0 NormalX=0 NormalY=0 NormalZ=1 AngleXU=0 Radius=1.6
    g11: Circle CenterX=-78.51 CenterY=7.6 CenterZ=0 NormalX=0 NormalY=0 NormalZ=1 AngleXU=0 Radius=4
    g12: Circle CenterX=-78.51 CenterY=34.8 CenterZ=0 NormalX=0 NormalY=0 NormalZ=1 AngleXU=0 Radius=1.6
    g13: Circle CenterX=-78.51 CenterY=34.8 CenterZ=0 NormalX=0 NormalY=0 NormalZ=1 AngleXU=0 Radius=4
  constraints (35):
    c: Diameter(g0) = 3.2
    c: Diameter(g1) = 8
    c: Coincident(g0,g1)
    c: Diameter(g2) = 3.2
    c: Diameter(g3) = 8
    c: Coincident(g3,g2)
    c: Tangent(g2,g-7)
    c: Diameter(g4) = 3.2
    c: Diameter(g5) = 8
    c: Coincident(g5,g4)
    c: Tangent(g4,g-7)
    c: Tangent(g4,g-8)
    c: Diameter(g6) = 3.2
    c: Diameter(g7) = 8
    c: Coincident(g7,g6)
    c: Tangent(g6,g-9)
    c: Tangent(g6,g-10)
    c: Diameter(g8) = 3.2
    c: Diameter(g9) = 8
    c: Coincident(g9,g8)
    c: Tangent(g8,g-10)
    c: Tangent(g8,g-11)
    c: Diameter(g10) = 3.2
    c: Diameter(g11) = 8
    c: Diameter(g12) = 3.2
    c: Diameter(g13) = 8
    c: Coincident(g12,g13)
    c: Coincident(g10,g11)
    c: Tangent(g12,g-7)
    c: DistanceX(g12,g10) = 0
    c: Tangent(g2,g-6)
    c: Tangent(g0,g-6)
    c: Tangent(g0,g-3)
    c: Tangent(g10,g-3)
    c: Tangent(g10,g-4)
FEATURE [Part::Extrusion] Extrude012  label="extrude guide per coperture laterali"
  Base = -> Sketch016
  Dir = (0,-1,2e-16)
  DirMode = 2
  FaceMakerClass = Part::FaceMakerBullseye
  FaceMakerMode = 3
  LengthFwd = 25.2
  LengthRev = 0
  Solid = true
  Symmetric = true
FEATURE [Sketcher::SketchObject] Sketch017  label="supporto CAM"
  ArcFitTolerance = 1e-06
  AttachmentSupport = -> [XZ_Plane]
  ExternalGeometry = -> [Sketch]
  FullyConstrained = true
  MakeInternals = false
  MapMode = 5
  Placement = pos=(0,0,0) rot=(1,0,0;1.5708rad)
  sketch-geometry (6):
    g0: LineSegment StartX=-2.4 StartY=48 StartZ=0 EndX=-2.4 EndY=41.2 EndZ=0
    g1: LineSegment StartX=-2.4 StartY=48 StartZ=0 EndX=-34 EndY=48 EndZ=0
    g2: LineSegment StartX=-34 StartY=48 StartZ=0 EndX=-34 EndY=46.72 EndZ=0
    g3: LineSegment StartX=-34 StartY=46.72 StartZ=0 EndX=-36 EndY=46.72 EndZ=0
    g4: LineSegment StartX=-36 StartY=46.72 StartZ=0 EndX=-36 EndY=41.2 EndZ=0
    g5: LineSegment StartX=-36 StartY=41.2 StartZ=0 EndX=-2.4 EndY=41.2 EndZ=0
  constraints (15):
    c: Coincident(g1,g0)
    c: Horizontal(g1)
    c: Coincident(g2,g1)
    c: Vertical(g2)
    c: Coincident(g3,g2)
    c: Horizontal(g3)
    c: Coincident(g4,g3)
    c: Coincident(g5,g4)
    c: DistanceX(g1,g0) = 31.6
    c: Coincident(g5,g0)
    c: Vertical(g4)
    c: DistanceY(g2,g1) = 1.28
    c: Coincident(g0,g-3)
    c: Coincident(g0,g-3)
    c: Coincident(g4,g-4)
FEATURE [Part::Extrusion] Extrude013  label="Extrude supporto CAM"
  Base = -> Sketch017
  Dir = (0,-1,2e-16)
  DirMode = 2
  FaceMakerClass = Part::FaceMakerBullseye
  FaceMakerMode = 3
  LengthFwd = 17.8
  LengthRev = 0
  Solid = true
  Symmetric = true
FEATURE [Sketcher::SketchObject] Sketch018  label="Scavo CAM"
  ArcFitTolerance = 1e-06
  AttachmentSupport = -> [YZ_Plane]
  ExternalGeometry = -> [Sketch]
  FullyConstrained = true
  MakeInternals = false
  MapMode = 5
  Placement = pos=(0,0,0) rot=(0.57735,0.57735,0.57735;2.0944rad)
  sketch-geometry (4):
    g0: LineSegment StartX=-7.73 StartY=48 StartZ=0 EndX=7.73 EndY=48 EndZ=0
    g1: LineSegment [constr] StartX=1.07e-14 StartY=48 StartZ=0 EndX=0 EndY=43.5155 EndZ=0
    g2: ArcOfCircle CenterX=9e-15 CenterY=52.42 CenterZ=0 NormalX=0 NormalY=0 NormalZ=1 AngleXU=0 Radius=8.90445 StartAngle=3.66102 EndAngle=5.76376
    g3: Circle [constr] CenterX=9e-15 CenterY=52.42 CenterZ=0 NormalX=0 NormalY=0 NormalZ=1 AngleXU=0 Radius=8.9
  constraints (13):
    c: Horizontal(g0)
    c: DistanceY(g-3,g0) = 0
    c: DistanceX(g0,g0) = 15.46
    c: DistanceX(g0,g-3) = 7.73
    c: DistanceX(g-3) = 0
    c: Coincident(g1,g-3)
    c: PointOnObject(g1,g-2)
    c: Coincident(g2,g0)
    c: Coincident(g2,g0)
    c: PointOnObject(g1,g2)
    c: Diameter(g3) = 17.8
    c: DistanceY(g1,g3) = 4.42
    c: Coincident(g2,g3)
FEATURE [Part::Extrusion] Extrude014  label="Extrude Scavo CAM"
  Base = -> Sketch018
  Dir = (1,0,0)
  DirMode = 2
  FaceMakerClass = Part::FaceMakerBullseye
  FaceMakerMode = 3
  LengthFwd = -34
  LengthRev = 0
  Solid = true
  Symmetric = false
FEATURE [Sketcher::SketchObject] Sketch019  label="scavo rumble"
  ArcFitTolerance = 1e-06
  AttachmentSupport = -> [XZ_Plane]
  ExternalGeometry = -> [Sketch]
  FullyConstrained = true
  MakeInternals = false
  MapMode = 5
  Placement = pos=(0,0,0) rot=(1,0,0;1.5708rad)
  sketch-geometry (6):
    g0: LineSegment StartX=-168.716 StartY=-37.1227 StartZ=0 EndX=-163.58 EndY=-38.7914 EndZ=0
    g1: LineSegment StartX=-163.58 StartY=-38.7914 StartZ=0 EndX=-170.687 EndY=-60.6657 EndZ=0
    g2: LineSegment StartX=-170.687 StartY=-60.6657 StartZ=0 EndX=-175.823 EndY=-58.997 EndZ=0
    g3: LineSegment StartX=-175.823 StartY=-58.997 StartZ=0 EndX=-168.716 EndY=-37.1227 EndZ=0
    g4: LineSegment [constr] StartX=-145.51 StartY=22 StartZ=0 EndX=-165.102 EndY=-38.297 EndZ=0
    g5: LineSegment [constr] StartX=-163.58 StartY=-38.7914 StartZ=0 EndX=-165.102 EndY=-38.297 EndZ=0
  constraints (17):
    c: Coincident(g1,g0)
    c: Coincident(g2,g1)
    c: Coincident(g3,g2)
    c: Coincident(g3,g0)
    c: Parallel(g3,g-3)
    c: Parallel(g3,g1)
    c: Perpendicular(g3,g0)
    c: Perpendicular(g2,g3)
    c: Distance(g2,g0) = 23
    c: Parallel(g4,g-3)
    c: Distance(g4) = 63.4
    c: Coincident(g4,g-3)
    c: Parallel(g5,g0)
    c: Coincident(g5,g0)
    c: Coincident(g5,g4)
    c: Distance(g4,g0) = 3.8
    c: Distance(g4,g0) = 1.6
FEATURE [Part::Extrusion] Extrude015  label="scavo rumble001"
  Base = -> Sketch019
  Dir = (0,-1,2e-16)
  DirMode = 2
  FaceMakerClass = Part::FaceMakerBullseye
  FaceMakerMode = 3
  LengthFwd = 21
  LengthRev = 0
  Solid = true
  Symmetric = true
FEATURE [Sketcher::SketchObject] Sketch020  label="fermo rumble"
  ArcFitTolerance = 1e-06
  AttachmentSupport = -> [XZ_Plane]
  ExternalGeometry = -> [Sketch019,Sketch]
  FullyConstrained = true
  MakeInternals = false
  MapMode = 5
  Placement = pos=(0,0,0) rot=(1,0,0;1.5708rad)
  sketch-geometry (16):
    g0: LineSegment [constr] StartX=-170.849 StartY=-55.9866 StartZ=0 EndX=-172.209 EndY=-60.1713 EndZ=0
    g1: LineSegment [constr] StartX=-172.209 StartY=-60.1713 StartZ=0 EndX=-170.687 EndY=-60.6657 EndZ=0
    g2: LineSegment StartX=-172.262 StartY=-53.2145 StartZ=0 EndX=-170.17 EndY=-53.8943 EndZ=0
    g3: LineSegment StartX=-170.17 StartY=-53.8943 StartZ=0 EndX=-170.849 EndY=-55.9866 EndZ=0
    g4: LineSegment StartX=-170.849 StartY=-55.9866 StartZ=0 EndX=-172.942 EndY=-55.3068 EndZ=0
    g5: LineSegment StartX=-172.942 StartY=-55.3068 StartZ=0 EndX=-172.262 EndY=-53.2145 EndZ=0
    g6: LineSegment StartX=-171.767 StartY=-51.6928 StartZ=0 EndX=-168.344 EndY=-52.8052 EndZ=0
    g7: LineSegment StartX=-168.344 StartY=-52.8052 StartZ=0 EndX=-169.951 EndY=-57.7507 EndZ=0
    g8: LineSegment StartX=-169.951 StartY=-57.7507 StartZ=0 EndX=-173.374 EndY=-56.6383 EndZ=0
    g9: LineSegment StartX=-174.402 StartY=-54.6222 StartZ=0 EndX=-173.784 EndY=-52.72 EndZ=0
    g10: LineSegment [constr] StartX=-173.784 StartY=-52.72 StartZ=0 EndX=-173.289 EndY=-51.1984 EndZ=0
    g11: LineSegment [constr] StartX=-173.289 StartY=-51.1984 StartZ=0 EndX=-171.767 EndY=-51.6928 EndZ=0
    g12: ArcOfCircle CenterX=-172.88 CenterY=-55.1166 CenterZ=0 NormalX=0 NormalY=0 NormalZ=1 AngleXU=0 Radius=1.6 StartAngle=2.82743 EndAngle=4.39823
    g13: GeomPoint [constr] X=-174.896 Y=-56.1438 Z=0
    g14: ArcOfCircle CenterX=-172.262 CenterY=-53.2145 CenterZ=0 NormalX=0 NormalY=0 NormalZ=1 AngleXU=0 Radius=1.6 StartAngle=1.25664 EndAngle=2.82743
    g15: GeomPoint [constr] X=-173.289 Y=-51.1984 Z=0
  constraints (42):
    c: Parallel(g0,g-4)
    c: Distance(g0) = 4.4
    c: Coincident(g1,g0)
    c: Perpendicular(g0,g1)
    c: Distance(g1) = 1.6
    c: Coincident(g1,g-5)
    c: Coincident(g3,g2)
    c: Coincident(g4,g3)
    c: Coincident(g5,g4)
    c: Coincident(g5,g2)
    c: Parallel(g3,g-4)
    c: Parallel(g3,g5)
    c: Perpendicular(g2,g3)
    c: Parallel(g4,g2)
    c: Distance(g2) = 2.2
    c: Distance(g3) = 2.2
    c: Coincident(g7,g6)
    c: Coincident(g8,g7)
    c: Parallel(g7,g-4)
    c: Parallel(g7,g9)
    c: Perpendicular(g6,g7)
    c: Parallel(g6,g8)
    c: Distance(g6,g15) = 5.2
    c: Distance(g7) = 5.2
    c: Coincident(g11,g10)
    c: Parallel(g10,g9)
    c: Parallel(g11,g6)
    c: Distance(g10) = 1.6
    c: Distance(g11) = 1.6
    c: Coincident(g10,g15)
    c: Distance(g11,g2) = 1.6
    c: Distance(g2,g10) = 1.6
    c: PointOnObject(g13,g8)
    c: PointOnObject(g13,g9)
    c: Tangent(g8,g12) = 1.5708
    c: Tangent(g9,g12) = 1.5708
    c: PointOnObject(g15,g9)
    c: Tangent(g6,g14) = 1.5708
    c: Tangent(g9,g14) = 1.5708
    c: Equal(g12,g14)
    c: Coincident(g6,g11)
    c: Coincident(g3,g0)
FEATURE [Part::Extrusion] Extrude016  label="Extrude fermo rumble"
  Base = -> Sketch020
  Dir = (0,-1,2e-16)
  DirMode = 2
  FaceMakerClass = Part::FaceMakerBullseye
  FaceMakerMode = 3
  LengthFwd = 25.2
  LengthRev = 0
  Solid = true
  Symmetric = true
FEATURE [Sketcher::SketchObject] Sketch021  label="perno fermo rumble001"
  ArcFitTolerance = 1e-06
  AttachmentSupport = -> [XZ_Plane001]
  FullyConstrained = true
  MakeInternals = false
  MapMode = 5
  Placement = pos=(0,0,0) rot=(1,0,0;1.5708rad)
  sketch-geometry (16):
    g0: LineSegment StartX=0 StartY=0.45 StartZ=0 EndX=0 EndY=1.55 EndZ=0
    g1: LineSegment StartX=0.45 StartY=2 StartZ=0 EndX=1.55 EndY=2 EndZ=0
    g2: LineSegment StartX=2 StartY=1.55 StartZ=0 EndX=2 EndY=0.45 EndZ=0
    g3: LineSegment StartX=1.55 StartY=0 StartZ=0 EndX=0.45 EndY=0 EndZ=0
    g4: ArcOfCircle [constr] CenterX=0.45 CenterY=1.55 CenterZ=0 NormalX=0 NormalY=0 NormalZ=1 AngleXU=0 Radius=0.45 StartAngle=1.5708 EndAngle=3.14159
    g5: GeomPoint [constr] X=0 Y=2 Z=0
    g6: LineSegment StartX=0.45 StartY=2 StartZ=0 EndX=0 EndY=1.55 EndZ=0
    g7: ArcOfCircle [constr] CenterX=1.55 CenterY=1.55 CenterZ=0 NormalX=0 NormalY=0 NormalZ=1 AngleXU=0 Radius=0.45 StartAngle=0 EndAngle=1.5708
    g8: GeomPoint [constr] X=2 Y=2 Z=0
    g9: LineSegment StartX=2 StartY=1.55 StartZ=0 EndX=1.55 EndY=2 EndZ=0
    g10: ArcOfCircle [constr] CenterX=1.55 CenterY=0.45 CenterZ=0 NormalX=0 NormalY=0 NormalZ=1 AngleXU=0 Radius=0.45 StartAngle=4.71239 EndAngle=6.28319
    g11: GeomPoint [constr] X=2 Y=0 Z=0
    g12: LineSegment StartX=1.55 StartY=0 StartZ=0 EndX=2 EndY=0.45 EndZ=0
    g13: ArcOfCircle [constr] CenterX=0.45 CenterY=0.45 CenterZ=0 NormalX=0 NormalY=0 NormalZ=1 AngleXU=0 Radius=0.45 StartAngle=3.14159 EndAngle=4.71239
    g14: GeomPoint [constr] X=0 Y=0 Z=0
    g15: LineSegment StartX=0 StartY=0.45 StartZ=0 EndX=0.45 EndY=0 EndZ=0
  constraints (35):
    c: Coincident(g14,g-1)
    c: PointOnObject(g5,g-2)
    c: Horizontal(g1)
    c: Vertical(g2)
    c: Horizontal(g3)
    c: DistanceX(g5,g8) = 2
    c: DistanceY(g11,g8) = 2
    c: PointOnObject(g5,g0)
    c: PointOnObject(g5,g1)
    c: Tangent(g0,g4) = 1.5708
    c: Tangent(g1,g4) = 1.5708
    c: Coincident(g6,g0)
    c: Coincident(g6,g1)
    c: PointOnObject(g8,g2)
    c: PointOnObject(g8,g1)
    c: Tangent(g2,g7) = 1.5708
    c: Tangent(g1,g7) = 1.5708
    c: Coincident(g9,g2)
    c: Coincident(g9,g1)
    c: PointOnObject(g11,g2)
    c: PointOnObject(g11,g3)
    c: Tangent(g2,g10) = 1.5708
    c: Tangent(g3,g10) = 1.5708
    c: Coincident(g12,g2)
    c: Coincident(g12,g3)
    c: PointOnObject(g14,g0)
    c: PointOnObject(g14,g3)
    c: Tangent(g0,g13) = 1.5708
    c: Tangent(g3,g13) = 1.5708
    c: Coincident(g15,g0)
    c: Coincident(g15,g3)
    c: Equal(g6,g9)
    c: Equal(g9,g12)
    c: Equal(g12,g15)
    c: DistanceX(g14,g3) = 0.45
FEATURE [Sketcher::SketchObject] Sketch022  label="fori per M3x5(OD)x6(L)"
  ArcFitTolerance = 1e-06
  AttachmentSupport = -> [XZ_Plane]
  ExternalGeometry = -> [Sketch016]
  FullyConstrained = true
  MakeInternals = false
  MapMode = 5
  Placement = pos=(0,0,0) rot=(1,0,0;1.5708rad)
  sketch-geometry (7):
    g0: Circle CenterX=-5.6 CenterY=34.8 CenterZ=0 NormalX=0 NormalY=0 NormalZ=1 AngleXU=0 Radius=2.5
    g1: Circle CenterX=-5.6 CenterY=7.6 CenterZ=0 NormalX=0 NormalY=0 NormalZ=1 AngleXU=0 Radius=2.5
    g2: Circle CenterX=-78.51 CenterY=34.8 CenterZ=0 NormalX=0 NormalY=0 NormalZ=1 AngleXU=0 Radius=2.5
    g3: Circle CenterX=-78.51 CenterY=7.6 CenterZ=0 NormalX=0 NormalY=0 NormalZ=1 AngleXU=0 Radius=2.5
    g4: Circle CenterX=-184.08 CenterY=34.8 CenterZ=0 NormalX=0 NormalY=0 NormalZ=1 AngleXU=0 Radius=2.5
    g5: Circle CenterX=-179.305 CenterY=-76.8316 CenterZ=0 NormalX=0 NormalY=0 NormalZ=1 AngleXU=0 Radius=2.5
    g6: Circle CenterX=-213.443 CenterY=-76.8316 CenterZ=0 NormalX=0 NormalY=0 NormalZ=1 AngleXU=0 Radius=2.5
  constraints (14):
    c: Diameter(g0) = 5
    c: Diameter(g1) = 5
    c: Diameter(g2) = 5
    c: Diameter(g3) = 5
    c: Diameter(g4) = 5
    c: Diameter(g5) = 5
    c: Diameter(g6) = 5
    c: Coincident(g0,g-8)
    c: Coincident(g1,g-9)
    c: Coincident(g2,g-6)
    c: Coincident(g3,g-7)
    c: Coincident(g4,g-5)
    c: Coincident(g5,g-4)
    c: Coincident(g6,g-3)
FEATURE [Part::Extrusion] Extrude018  label="Extrude fori M3x5x6 - dx"
  Base = -> Sketch022
  Dir = (0,-1,2e-16)
  DirMode = 2
  FaceMakerClass = Part::FaceMakerBullseye
  FaceMakerMode = 3
  LengthFwd = 6.2
  LengthRev = 0
  Placement = pos=(0,-9.5,0) rot=(0,0,1;0rad)
  Solid = true
  Symmetric = true
FEATURE [Part::Extrusion] Extrude019  label="Extrude fori M3x5x6 - sx"
  Base = -> Sketch022
  Dir = (0,-1,2e-16)
  DirMode = 2
  FaceMakerClass = Part::FaceMakerBullseye
  FaceMakerMode = 3
  LengthFwd = 6.2
  LengthRev = 0
  Placement = pos=(0,9.5,0) rot=(0,0,1;0rad)
  Solid = true
  Symmetric = true
FEATURE [Sketcher::SketchObject] Sketch023  label="foro anteriore M3x5x6"
  ArcFitTolerance = 1e-06
  AttachmentSupport = -> [YZ_Plane]
  FullyConstrained = true
  MakeInternals = false
  MapMode = 5
  Placement = pos=(0,0,0) rot=(0.57735,0.57735,0.57735;2.0944rad)
  sketch-geometry (2):
    g0: LineSegment [constr] StartX=0 StartY=0 StartZ=0 EndX=0 EndY=38.6 EndZ=0
    g1: Circle CenterX=0 CenterY=38.6 CenterZ=0 NormalX=0 NormalY=0 NormalZ=1 AngleXU=0 Radius=2.5
  constraints (5):
    c: Coincident(g0,g-1)
    c: PointOnObject(g0,g-2)
    c: DistanceY(g0,g0) = 38.6
    c: Diameter(g1) = 5
    c: Coincident(g1,g0)
FEATURE [Part::Extrusion] Extrude020  label="Extrude foro anteriore M3x5x6"
  Base = -> Sketch023
  Dir = (1,0,0)
  DirMode = 2
  FaceMakerClass = Part::FaceMakerBullseye
  FaceMakerMode = 3
  LengthFwd = -6.2
  LengthRev = 0
  Solid = true
  Symmetric = false
FEATURE [Sketcher::SketchObject] Sketch024  label="fori per viti frontale"
  ArcFitTolerance = 1e-06
  AttachmentSupport = -> [YZ_Plane]
  FullyConstrained = true
  MakeInternals = false
  MapMode = 5
  Placement = pos=(0,0,0) rot=(0.57735,0.57735,0.57735;2.0944rad)
  sketch-geometry (9):
    g0: LineSegment [constr] StartX=-10.3 StartY=30.721 StartZ=0 EndX=10.3 EndY=30.721 EndZ=0
    g1: LineSegment [constr] StartX=10.3 StartY=30.721 StartZ=0 EndX=10.3 EndY=10.121 EndZ=0
    g2: LineSegment [constr] StartX=10.3 StartY=10.121 StartZ=0 EndX=-10.3 EndY=10.121 EndZ=0
    g3: LineSegment [constr] StartX=-10.3 StartY=10.121 StartZ=0 EndX=-10.3 EndY=30.721 EndZ=0
    g4: LineSegment [constr] StartX=0 StartY=0 StartZ=0 EndX=0 EndY=10.121 EndZ=0
    g5: Circle CenterX=-10.3 CenterY=30.721 CenterZ=0 NormalX=0 NormalY=0 NormalZ=1 AngleXU=0 Radius=2
    g6: Circle CenterX=10.3 CenterY=30.721 CenterZ=0 NormalX=0 NormalY=0 NormalZ=1 AngleXU=0 Radius=2
    g7: Circle CenterX=-10.3 CenterY=10.121 CenterZ=0 NormalX=0 NormalY=0 NormalZ=1 AngleXU=0 Radius=2
    g8: Circle CenterX=10.3 CenterY=10.121 CenterZ=0 NormalX=0 NormalY=0 NormalZ=1 AngleXU=0 Radius=2
  constraints (22):
    c: Horizontal(g0)
    c: Coincident(g1,g0)
    c: Vertical(g1)
    c: Coincident(g2,g1)
    c: Horizontal(g2)
    c: Coincident(g3,g2)
    c: Coincident(g3,g0)
    c: Vertical(g3)
    c: DistanceX(g0,g0) = 20.6
    c: DistanceY(g3,g3) = 20.6
    c: Coincident(g4,g-1)
    c: PointOnObject(g4,g-2)
    c: DistanceY(g4,g4) = 10.121
    c: Symmetric(g2,g2,g4)
    c: Diameter(g5) = 4
    c: Diameter(g6) = 4
    c: Diameter(g7) = 4
    c: Diameter(g8) = 4
    c: Coincident(g5,g0)
    c: Coincident(g6,g0)
    c: Coincident(g7,g2)
    c: Coincident(g8,g1)
FEATURE [Part::Extrusion] Extrude021  label="Extrude fori per viti frontale"
  Base = -> Sketch024
  Dir = (1,0,0)
  DirMode = 2
  FaceMakerClass = Part::FaceMakerBullseye
  FaceMakerMode = 3
  LengthFwd = -2.4
  LengthRev = 0
  Solid = true
  Symmetric = false
FEATURE [Sketcher::SketchObject] Sketch025  label="foro per filo CAM"
  ArcFitTolerance = 1e-06
  AttachmentSupport = -> [XZ_Plane]
  ExternalGeometry = -> [Sketch]
  FullyConstrained = true
  MakeInternals = false
  MapMode = 5
  Placement = pos=(0,0,0) rot=(1,0,0;1.5708rad)
  sketch-geometry (4):
    g0: LineSegment StartX=-44.6 StartY=41.2 StartZ=0 EndX=-44.6 EndY=36.4 EndZ=0
    g1: LineSegment StartX=-44.6 StartY=36.4 StartZ=0 EndX=-54.6 EndY=36.4 EndZ=0
    g2: LineSegment StartX=-54.6 StartY=36.4 StartZ=0 EndX=-50.4 EndY=41.2 EndZ=0
    g3: LineSegment StartX=-50.4 StartY=41.2 StartZ=0 EndX=-44.6 EndY=41.2 EndZ=0
  constraints (11):
    c: Vertical(g0)
    c: Coincident(g1,g0)
    c: Horizontal(g1)
    c: Coincident(g2,g1)
    c: Coincident(g3,g2)
    c: Coincident(g3,g0)
    c: Horizontal(g3)
    c: Coincident(g0,g-3)
    c: DistanceY(g0,g-4) = 0
    c: DistanceX(g3,g3) = 5.8
    c: DistanceX(g1,g1) = 10
FEATURE [Part::Extrusion] Extrude022  label="Extrude foro per filo CAM dx"
  Base = -> Sketch025
  Dir = (0,-1,2e-16)
  DirMode = 2
  FaceMakerClass = Part::FaceMakerBullseye
  FaceMakerMode = 3
  LengthFwd = 4.9
  LengthRev = 0
  Placement = pos=(0,6.95,0) rot=(0,0,1;0rad)
  Solid = true
  Symmetric = true
FEATURE [Part::Extrusion] Extrude023  label="Extrude foro per filo CAM sx"
  Base = -> Sketch025
  Dir = (0,-1,2e-16)
  DirMode = 2
  FaceMakerClass = Part::FaceMakerBullseye
  FaceMakerMode = 3
  LengthFwd = 4.9
  LengthRev = 0
  Placement = pos=(0,-6.95,0) rot=(0,0,1;0rad)
  Solid = true
  Symmetric = true
FEATURE [Sketcher::SketchObject] Sketch026  label="foro sotto anteriore M3x5x6"
  ArcFitTolerance = 1e-06
  AttachmentSupport = -> [XY_Plane]
  FullyConstrained = true
  MakeInternals = false
  MapMode = 5
  sketch-geometry (2):
    g0: LineSegment [constr] StartX=0 StartY=0 StartZ=0 EndX=-16.5 EndY=0 EndZ=0
    g1: Circle CenterX=-16.5 CenterY=0 CenterZ=0 NormalX=0 NormalY=0 NormalZ=1 AngleXU=0 Radius=2.5
  constraints (5):
    c: Distance(g0) = 16.5
    c: Coincident(g0,g-1)
    c: PointOnObject(g0,g-1)
    c: Diameter(g1) = 5
    c: Coincident(g0,g1)
FEATURE [Sketcher::SketchObject] Sketch027  label="foro sotto posteriore M3x5x6"
  ArcFitTolerance = 1e-06
  AttachmentSupport = -> [XY_Plane]
  ExternalGeometry = -> [Sketch]
  FullyConstrained = true
  MakeInternals = false
  MapMode = 5
  sketch-geometry (2):
    g0: LineSegment [constr] StartX=-82.8 StartY=2e-16 StartZ=0 EndX=-71.3 EndY=2e-16 EndZ=0
    g1: Circle CenterX=-71.3 CenterY=2e-16 CenterZ=0 NormalX=0 NormalY=0 NormalZ=1 AngleXU=0 Radius=2.5
  constraints (5):
    c: Distance(g0) = 11.5
    c: Coincident(g0,g-3)
    c: PointOnObject(g0,g-3)
    c: Diameter(g1) = 5
    c: Coincident(g1,g0)
FEATURE [Sketcher::SketchObject] Sketch029  label="fori sotto impugnatura"
  ArcFitTolerance = 1e-06
  AttachmentSupport = -> [XY_Plane]
  ExternalGeometry = -> [Sketch]
  FullyConstrained = true
  MakeInternals = false
  MapMode = 5
  sketch-geometry (15):
    g0: LineSegment [constr] StartX=-175.232 StartY=-1.83e-14 StartZ=0 EndX=-191.232 EndY=0 EndZ=0
    g1: Circle CenterX=-191.232 CenterY=0 CenterZ=0 NormalX=0 NormalY=0 NormalZ=1 AngleXU=0 Radius=3.95
    g2: LineSegment [constr] StartX=-175.232 StartY=-1.83e-14 StartZ=0 EndX=-204.275 EndY=0 EndZ=0
    g3: LineSegment StartX=-204.275 StartY=3.525 StartZ=0 EndX=-204.275 EndY=-3.525 EndZ=0
    g4: LineSegment StartX=-205.4 StartY=-4.65 StartZ=0 EndX=-206.65 EndY=-4.65 EndZ=0
    g5: LineSegment StartX=-207.775 StartY=-3.525 StartZ=0 EndX=-207.775 EndY=3.525 EndZ=0
    g6: LineSegment StartX=-206.65 StartY=4.65 StartZ=0 EndX=-205.4 EndY=4.65 EndZ=0
    g7: ArcOfCircle CenterX=-206.65 CenterY=3.525 CenterZ=0 NormalX=0 NormalY=0 NormalZ=1 AngleXU=0 Radius=1.125 StartAngle=1.5708 EndAngle=3.14159
    g8: GeomPoint [constr] X=-207.775 Y=4.65 Z=0
    g9: ArcOfCircle CenterX=-205.4 CenterY=3.525 CenterZ=0 NormalX=0 NormalY=0 NormalZ=1 AngleXU=0 Radius=1.125 StartAngle=0 EndAngle=1.5708
    g10: GeomPoint [constr] X=-204.275 Y=4.65 Z=0
    g11: ArcOfCircle CenterX=-205.4 CenterY=-3.525 CenterZ=0 NormalX=0 NormalY=0 NormalZ=1 AngleXU=0 Radius=1.125 StartAngle=4.71239 EndAngle=6.28319
    g12: GeomPoint [constr] X=-204.275 Y=-4.65 Z=0
    g13: ArcOfCircle CenterX=-206.65 CenterY=-3.525 CenterZ=0 NormalX=0 NormalY=0 NormalZ=1 AngleXU=0 Radius=1.125 StartAngle=3.14159 EndAngle=4.71239
    g14: GeomPoint [constr] X=-207.775 Y=-4.65 Z=0
  constraints (35):
    c: Distance(g0) = 16
    c: Coincident(g0,g-3)
    c: PointOnObject(g0,g-1)
    c: Diameter(g1) = 7.9
    c: Coincident(g1,g0)
    c: Coincident(g2,g0)
    c: PointOnObject(g2,g-1)
    c: Vertical(g3)
    c: Horizontal(g4)
    c: Vertical(g5)
    c: Horizontal(g6)
    c: DistanceY(g12,g10) = 9.3
    c: DistanceX(g8,g10) = 3.5
    c: Symmetric(g10,g12,g2)
    c: PointOnObject(g8,g5)
    c: PointOnObject(g8,g6)
    c: Tangent(g5,g7) = 1.5708
    c: Tangent(g6,g7) = 1.5708
    c: PointOnObject(g10,g3)
    c: PointOnObject(g10,g6)
    c: Tangent(g3,g9) = 1.5708
    c: Tangent(g6,g9) = 1.5708
    c: PointOnObject(g12,g3)
    c: PointOnObject(g12,g4)
    c: Tangent(g3,g11) = 1.5708
    c: Tangent(g4,g11) = 1.5708
    c: PointOnObject(g14,g4)
    c: PointOnObject(g14,g5)
    c: Tangent(g4,g13) = 1.5708
    c: Tangent(g5,g13) = 1.5708
    c: Equal(g7,g9)
    c: Equal(g9,g11)
    c: Equal(g11,g13)
    c: DistanceX(g6,g6) = 1.25
    c: DistanceX(g-5,g5) = 6.8
FEATURE [Sketcher::SketchObject] Sketch030  label="fori superiori per solenoide e oled"
  ArcFitTolerance = 1e-06
  AttachmentSupport = -> [XY_Plane]
  ExternalGeometry = -> [Sketch]
  FullyConstrained = true
  MakeInternals = false
  MapMode = 5
  sketch-geometry (33):
    g0: LineSegment [constr] StartX=-181.6 StartY=1.12e-14 StartZ=0 EndX=-169.91 EndY=0 EndZ=0
    g1: LineSegment [constr] StartX=-169.91 StartY=0 StartZ=0 EndX=-169.91 EndY=-2.6 EndZ=0
    g2: LineSegment [constr] StartX=-169.91 StartY=0 StartZ=0 EndX=-169.91 EndY=2.6 EndZ=0
    g3: LineSegment StartX=-169.91 StartY=4.975 StartZ=0 EndX=-169.91 EndY=8.225 EndZ=0
    g4: LineSegment StartX=-167.535 StartY=10.6 StartZ=0 EndX=-167.285 EndY=10.6 EndZ=0
    g5: LineSegment StartX=-164.91 StartY=8.225 StartZ=0 EndX=-164.91 EndY=4.975 EndZ=0
    g6: LineSegment StartX=-167.285 StartY=2.6 StartZ=0 EndX=-167.535 EndY=2.6 EndZ=0
    g7: LineSegment StartX=-169.91 StartY=-4.975 StartZ=0 EndX=-169.91 EndY=-8.225 EndZ=0
    g8: LineSegment StartX=-167.535 StartY=-10.6 StartZ=0 EndX=-167.285 EndY=-10.6 EndZ=0
    g9: LineSegment StartX=-164.91 StartY=-8.225 StartZ=0 EndX=-164.91 EndY=-4.975 EndZ=0
    g10: LineSegment StartX=-167.285 StartY=-2.6 StartZ=0 EndX=-167.535 EndY=-2.6 EndZ=0
    g11: ArcOfCircle CenterX=-167.535 CenterY=8.225 CenterZ=0 NormalX=0 NormalY=0 NormalZ=1 AngleXU=0 Radius=2.375 StartAngle=1.5708 EndAngle=3.14159
    g12: GeomPoint [constr] X=-169.91 Y=10.6 Z=0
    g13: ArcOfCircle CenterX=-167.285 CenterY=8.225 CenterZ=0 NormalX=0 NormalY=0 NormalZ=1 AngleXU=0 Radius=2.375 StartAngle=0 EndAngle=1.5708
    g14: GeomPoint [constr] X=-164.91 Y=10.6 Z=0
    g15: ArcOfCircle CenterX=-167.285 CenterY=4.975 CenterZ=0 NormalX=0 NormalY=0 NormalZ=1 AngleXU=0 Radius=2.375 StartAngle=4.71239 EndAngle=6.28319
    g16: GeomPoint [constr] X=-164.91 Y=2.6 Z=0
    g17: ArcOfCircle CenterX=-167.535 CenterY=4.975 CenterZ=0 NormalX=0 NormalY=0 NormalZ=1 AngleXU=0 Radius=2.375 StartAngle=3.14159 EndAngle=4.71239
    g18: GeomPoint [constr] X=-169.91 Y=2.6 Z=0
    g19: ArcOfCircle CenterX=-167.535 CenterY=-4.975 CenterZ=0 NormalX=0 NormalY=0 NormalZ=1 AngleXU=0 Radius=2.375 StartAngle=1.5708 EndAngle=3.14159
    g20: GeomPoint [constr] X=-169.91 Y=-2.6 Z=0
    g21: ArcOfCircle CenterX=-167.285 CenterY=-4.975 CenterZ=0 NormalX=0 NormalY=0 NormalZ=1 AngleXU=0 Radius=2.375 StartAngle=0 EndAngle=1.5708
    g22: GeomPoint [constr] X=-164.91 Y=-2.6 Z=0
    g23: ArcOfCircle CenterX=-167.285 CenterY=-8.225 CenterZ=0 NormalX=0 NormalY=0 NormalZ=1 AngleXU=0 Radius=2.375 StartAngle=4.71239 EndAngle=6.28319
    g24: GeomPoint [constr] X=-164.91 Y=-10.6 Z=0
    g25: ArcOfCircle CenterX=-167.535 CenterY=-8.225 CenterZ=0 NormalX=0 NormalY=0 NormalZ=1 AngleXU=0 Radius=2.375 StartAngle=3.14159 EndAngle=4.71239
    g26: GeomPoint [constr] X=-169.91 Y=-10.6 Z=0
    g27: LineSegment [constr] StartX=-181.6 StartY=1.12e-14 StartZ=0 EndX=-152.209 EndY=0 EndZ=0
    g28: LineSegment [constr] StartX=-181.6 StartY=1.12e-14 StartZ=0 EndX=-130.41 EndY=0 EndZ=0
    g29: LineSegment [constr] StartX=-152.209 StartY=0 StartZ=0 EndX=-152.209 EndY=6.95 EndZ=0
    g30: LineSegment [constr] StartX=-130.41 StartY=0 StartZ=0 EndX=-130.41 EndY=-6.95 EndZ=0
    g31: Circle CenterX=-152.209 CenterY=6.95 CenterZ=0 NormalX=0 NormalY=0 NormalZ=1 AngleXU=0 Radius=2.1
    g32: Circle CenterX=-130.41 CenterY=-6.95 CenterZ=0 NormalX=0 NormalY=0 NormalZ=1 AngleXU=0 Radius=2.1
  constraints (79):
    c: Distance(g0) = 11.69
    c: PointOnObject(g0,g-1)
    c: Coincident(g-4,g0)
    c: Distance(g1) = 2.6
    c: Coincident(g1,g0)
    c: Vertical(g1)
    c: Distance(g2) = 2.6
    c: Coincident(g2,g0)
    c: Vertical(g2)
    c: Distance(g18,g12) = 8
    c: Coincident(g18,g2)
    c: Vertical(g3)
    c: Distance(g14,g12) = 5
    c: Horizontal(g4)
    c: Distance(g16,g14) = 8
    c: Vertical(g5)
    c: Distance(g26,g20) = 8
    c: Coincident(g20,g1)
    c: Vertical(g7)
    c: Distance(g26,g24) = 5
    c: Horizontal(g8)
    c: Distance(g24,g22) = 8
    c: Vertical(g9)
    c: PointOnObject(g12,g3)
    c: PointOnObject(g12,g4)
    c: Tangent(g3,g11) = 1.5708
    c: Tangent(g4,g11) = 1.5708
    c: PointOnObject(g14,g5)
    c: PointOnObject(g14,g4)
    c: Tangent(g5,g13) = 1.5708
    c: Tangent(g4,g13) = 1.5708
    c: PointOnObject(g16,g5)
    c: PointOnObject(g16,g6)
    c: Tangent(g5,g15) = 1.5708
    c: Tangent(g6,g15) = 1.5708
    c: PointOnObject(g18,g3)
    c: PointOnObject(g18,g6)
    c: Tangent(g3,g17) = 1.5708
    c: Tangent(g6,g17) = 1.5708
    c: Equal(g11,g13)
    c: Equal(g13,g15)
    c: Equal(g15,g17)
    c: DistanceX(g4,g4) = 0.25
    c: PointOnObject(g20,g7)
    c: PointOnObject(g20,g10)
    c: Tangent(g7,g19) = -1.5708
    c: Tangent(g10,g19) = -1.5708
    c: PointOnObject(g22,g9)
    c: PointOnObject(g22,g10)
    c: Tangent(g9,g21) = -1.5708
    c: Tangent(g10,g21) = -1.5708
    c: PointOnObject(g24,g9)
    c: PointOnObject(g24,g8)
    c: Tangent(g9,g23) = -1.5708
    c: Tangent(g8,g23) = -1.5708
    c: PointOnObject(g26,g8)
    c: PointOnObject(g26,g7)
    c: Tangent(g8,g25) = -1.5708
    c: Tangent(g7,g25) = -1.5708
    c: Equal(g19,g21)
    c: Equal(g21,g23)
    c: Equal(g23,g25)
    c: DistanceX(g10,g10) = 0.25
    c: Distance(g27) = 29.391
    c: Coincident(g27,g0)
    c: PointOnObject(g27,g-1)
    c: Distance(g28) = 51.19
    c: Coincident(g28,g0)
    c: PointOnObject(g28,g-1)
    c: Distance(g29) = 6.95
    c: Coincident(g29,g27)
    c: Vertical(g29)
    c: Distance(g30) = 6.95
    c: Coincident(g30,g28)
    c: Vertical(g30)
    c: Diameter(g31) = 4.2
    c: Diameter(g32) = 4.2
    c: Coincident(g32,g30)
    c: Coincident(g31,g29)
FEATURE [Sketcher::SketchObject] Sketch031  label="fori inferiori switch pompa"
  ArcFitTolerance = 1e-06
  AttachmentSupport = -> [XY_Plane]
  ExternalGeometry = -> [Sketch]
  FullyConstrained = true
  MakeInternals = false
  MapMode = 5
  sketch-geometry (4):
    g0: LineSegment [constr] StartX=-57.2 StartY=1.9e-15 StartZ=0 EndX=-62.45 EndY=1.9e-15 EndZ=0
    g1: LineSegment [constr] StartX=-62.45 StartY=3.25 StartZ=0 EndX=-62.45 EndY=-3.25 EndZ=0
    g2: Circle CenterX=-62.45 CenterY=3.25 CenterZ=0 NormalX=0 NormalY=0 NormalZ=1 AngleXU=0 Radius=1.6
    g3: Circle CenterX=-62.45 CenterY=-3.25 CenterZ=0 NormalX=0 NormalY=0 NormalZ=1 AngleXU=0 Radius=1.6
  constraints (10):
    c: Distance(g0) = 5.25
    c: Coincident(g0,g-3)
    c: PointOnObject(g0,g-3)
    c: Vertical(g1)
    c: DistanceY(g1,g1) = 6.5
    c: Symmetric(g1,g1,g0)
    c: Diameter(g2) = 3.2
    c: Diameter(g3) = 3.2
    c: Coincident(g2,g1)
    c: Coincident(g3,g1)
FEATURE [Sketcher::SketchObject] Sketch032  label="spazio per PILA 18650"
  ArcFitTolerance = 1e-06
  AttachmentSupport = -> [XY_Plane]
  ExternalGeometry = -> [Sketch]
  FullyConstrained = true
  MakeInternals = false
  MapMode = 5
  sketch-geometry (2):
    g0: LineSegment [constr] StartX=-178.142 StartY=-1.74e-14 StartZ=0 EndX=-191.142 EndY=-1.83e-14 EndZ=0
    g1: Circle CenterX=-191.142 CenterY=-1.83e-14 CenterZ=0 NormalX=0 NormalY=0 NormalZ=1 AngleXU=0 Radius=10.5
  constraints (5):
    c: Distance(g0) = 13
    c: Coincident(g0,g-3)
    c: PointOnObject(g0,g-4)
    c: Diameter(g1) = 21
    c: Coincident(g1,g0)
FEATURE [Part::Extrusion] Extrude030  label="Extrude spazio per PILA 18650"
  Base = -> Sketch032
  Dir = (0,0,1)
  DirLink = -> Sketch [Edge45]
  DirMode = 2
  FaceMakerClass = Part::FaceMakerBullseye
  FaceMakerMode = 3
  LengthFwd = 76
  LengthRev = 0
  Placement = pos=(6,0,-72) rot=(0,0,1;0rad)
  Solid = true
  Symmetric = false
FEATURE [Sketcher::SketchObject] Sketch033  label="fermo per scheda micro"
  ArcFitTolerance = 1e-06
  AttachmentSupport = -> [XZ_Plane]
  ExternalGeometry = -> [Sketch]
  FullyConstrained = true
  MakeInternals = false
  MapMode = 5
  Placement = pos=(0,0,0) rot=(1,0,0;1.5708rad)
  sketch-geometry (12):
    g0: LineSegment StartX=-11.6 StartY=6 StartZ=0 EndX=-4 EndY=6 EndZ=0
    g1: LineSegment StartX=-4 StartY=6 StartZ=0 EndX=-4 EndY=36.4 EndZ=0
    g2: LineSegment StartX=-4 StartY=36.4 StartZ=0 EndX=-11.6 EndY=36.4 EndZ=0
    g3: LineSegment StartX=-11.6 StartY=36.4 StartZ=0 EndX=-11.6 EndY=6 EndZ=0
    g4: LineSegment StartX=-80.11 StartY=11.6 StartZ=0 EndX=-70.51 EndY=11.6 EndZ=0
    g5: LineSegment StartX=-70.51 StartY=11.6 StartZ=0 EndX=-70.51 EndY=6 EndZ=0
    g6: LineSegment StartX=-70.51 StartY=6 StartZ=0 EndX=-80.11 EndY=6 EndZ=0
    g7: LineSegment StartX=-80.11 StartY=6 StartZ=0 EndX=-80.11 EndY=11.6 EndZ=0
    g8: LineSegment StartX=-78.51 StartY=36.4 StartZ=0 EndX=-70.51 EndY=36.4 EndZ=0
    g9: LineSegment StartX=-70.51 StartY=36.4 StartZ=0 EndX=-70.51 EndY=30.8 EndZ=0
    g10: LineSegment StartX=-70.51 StartY=30.8 StartZ=0 EndX=-78.51 EndY=30.8 EndZ=0
    g11: LineSegment StartX=-78.51 StartY=30.8 StartZ=0 EndX=-78.51 EndY=36.4 EndZ=0
  constraints (33):
    c: Horizontal(g0)
    c: Coincident(g1,g0)
    c: Coincident(g2,g1)
    c: Horizontal(g2)
    c: Coincident(g3,g2)
    c: Coincident(g3,g0)
    c: Vertical(g3)
    c: DistanceX(g2,g2) = 7.6
    c: Coincident(g1,g-3)
    c: Coincident(g0,g-3)
    c: Horizontal(g4)
    c: Coincident(g5,g4)
    c: Vertical(g5)
    c: Coincident(g6,g5)
    c: Horizontal(g6)
    c: Coincident(g7,g6)
    c: Coincident(g7,g4)
    c: Vertical(g7)
    c: DistanceY(g5,g5) = 5.6
    c: DistanceX(g4,g4) = 9.6
    c: Coincident(g9,g8)
    c: Vertical(g9)
    c: Coincident(g10,g9)
    c: Horizontal(g10)
    c: Coincident(g11,g10)
    c: Coincident(g11,g8)
    c: Vertical(g11)
    c: DistanceY(g9,g9) = 5.6
    c: DistanceX(g10,g10) = 8
    c: Coincident(g4,g-4)
    c: DistanceX(g4,g10) = 1.6
    c: Horizontal(g8)
    c: DistanceY(g8,g1) = 0
FEATURE [Sketcher::SketchObject] Sketch034  label="buchi guida rail"
  ArcFitTolerance = 1e-06
  AttachmentSupport = -> [XY_Plane]
  ExternalGeometry = -> [Sketch]
  FullyConstrained = true
  MakeInternals = false
  MapMode = 5
  sketch-geometry (6):
    g0: LineSegment [constr] StartX=-100.8 StartY=9.1e-15 StartZ=0 EndX=-93.3 EndY=0 EndZ=0
    g1: LineSegment [constr] StartX=-93.3 StartY=0 StartZ=0 EndX=-73.3 EndY=0 EndZ=0
    g2: LineSegment [constr] StartX=-73.3 StartY=0 StartZ=0 EndX=-53.3 EndY=0 EndZ=0
    g3: Circle CenterX=-93.3 CenterY=0 CenterZ=0 NormalX=0 NormalY=0 NormalZ=1 AngleXU=0 Radius=2.5
    g4: Circle CenterX=-73.3 CenterY=0 CenterZ=0 NormalX=0 NormalY=0 NormalZ=1 AngleXU=0 Radius=2.5
    g5: Circle CenterX=-53.3 CenterY=0 CenterZ=0 NormalX=0 NormalY=0 NormalZ=1 AngleXU=0 Radius=2.5
  constraints (15):
    c: Distance(g0) = 7.5
    c: Coincident(g0,g-3)
    c: PointOnObject(g0,g-1)
    c: Distance(g1) = 20
    c: Coincident(g1,g0)
    c: PointOnObject(g1,g-1)
    c: Distance(g2) = 20
    c: Coincident(g2,g1)
    c: PointOnObject(g2,g-1)
    c: Diameter(g3) = 5
    c: Diameter(g4) = 5
    c: Diameter(g5) = 5
    c: Coincident(g3,g0)
    c: Coincident(g4,g1)
    c: Coincident(g5,g2)
FEATURE [Part::Extrusion] Extrude032  label="Extrude buchi guida rail"
  Base = -> Sketch034
  Dir = (0,0,1)
  DirMode = 2
  FaceMakerClass = Part::FaceMakerBullseye
  FaceMakerMode = 3
  LengthFwd = -6.2
  LengthRev = 0
  Placement = pos=(0,0,43.2) rot=(0,0,1;0rad)
  Solid = true
  Symmetric = false
FEATURE [Part::Extrusion] Extrude033  label="Extrude fori superiori per solenoide e oled001"
  Base = -> Sketch030
  Dir = (0,0,1)
  DirMode = 2
  FaceMakerClass = Part::FaceMakerBullseye
  FaceMakerMode = 3
  LengthFwd = -4.8
  LengthRev = 0
  Placement = pos=(0,0,41.2) rot=(0,0,1;0rad)
  Solid = true
  Symmetric = false
FEATURE [Part::Extrusion] Extrude034  label="Extrude fori sotto impugnatura001"
  Base = -> Sketch029
  Dir = (0,0,1)
  DirMode = 2
  FaceMakerClass = Part::FaceMakerBullseye
  FaceMakerMode = 3
  LengthFwd = 5
  LengthRev = 0
  Placement = pos=(0,0,-83) rot=(0,0,1;0rad)
  Solid = true
  Symmetric = false
FEATURE [Part::Extrusion] Extrude035  label="Extrude fori inferiori switch pompa001"
  Base = -> Sketch031
  Dir = (0,0,1)
  DirMode = 2
  FaceMakerClass = Part::FaceMakerBullseye
  FaceMakerMode = 3
  LengthFwd = 4
  LengthRev = 0
  Placement = pos=(0,0,-1.7) rot=(0,0,1;0rad)
  Solid = true
  Symmetric = false
FEATURE [Part::Extrusion] Extrude036  label="Extrude foro sotto posteriore M3x5x007"
  Base = -> Sketch027
  Dir = (0,0,1)
  DirMode = 2
  FaceMakerClass = Part::FaceMakerBullseye
  FaceMakerMode = 3
  LengthFwd = 6.2
  LengthRev = 0
  Placement = pos=(0,0,-9.6) rot=(0,0,1;0rad)
  Solid = true
  Symmetric = false
FEATURE [Part::Extrusion] Extrude037  label="Extrude foro sotto anteriore M3x5x007"
  Base = -> Sketch026
  Dir = (0,0,1)
  DirMode = 2
  FaceMakerClass = Part::FaceMakerBullseye
  FaceMakerMode = 3
  LengthFwd = 6.2
  LengthRev = 0
  Solid = true
  Symmetric = false
FEATURE [Sketcher::SketchObject] Sketch035  label="foro per fissaggio micro"
  ArcFitTolerance = 1e-06
  AttachmentSupport = -> [XZ_Plane]
  ExternalGeometry = -> [Sketch,Sketch033]
  FullyConstrained = true
  MakeInternals = false
  MapMode = 5
  Placement = pos=(0,0,0) rot=(1,0,0;1.5708rad)
  sketch-geometry (3):
    g0: Circle CenterX=-7.8 CenterY=21.2 CenterZ=0 NormalX=0 NormalY=0 NormalZ=1 AngleXU=0 Radius=1.6
    g1: GeomPoint [constr] X=-4 Y=21.2 Z=0
    g2: LineSegment [constr] StartX=-4 StartY=21.2 StartZ=0 EndX=-11.6 EndY=21.2 EndZ=0
  constraints (6):
    c: Diameter(g0) = 3.2
    c: Symmetric(g-3,g-3,g1)
    c: Coincident(g2,g1)
    c: Horizontal(g2)
    c: DistanceX(g-4,g2) = 0
    c: Symmetric(g2,g1,g0)
FEATURE [Part::Extrusion] Extrude038  label="Extrude foro per fissaggio micro"
  Base = -> Sketch035
  Dir = (0,-1,2e-16)
  DirMode = 2
  FaceMakerClass = Part::FaceMakerBullseye
  FaceMakerMode = 3
  LengthFwd = 3
  LengthRev = 0
  Placement = pos=(0,8.6,0) rot=(0,0,1;0rad)
  Solid = true
  Symmetric = false
FEATURE [Sketcher::SketchObject] Sketch036  label="supporto per alimentatore"
  ArcFitTolerance = 1e-06
  AttachmentSupport = -> [XZ_Plane]
  ExternalGeometry = -> [Sketch,Sketch016,Sketch022]
  FullyConstrained = true
  MakeInternals = false
  MapMode = 5
  Placement = pos=(0,0,0) rot=(1,0,0;1.5708rad)
  sketch-geometry (5):
    g0: LineSegment StartX=-211.843 StartY=-50.0944 StartZ=0 EndX=-211.843 EndY=-80.4316 EndZ=0
    g1: LineSegment StartX=-211.843 StartY=-50.0944 StartZ=0 EndX=-207.775 EndY=-41.3701 EndZ=0
    g2: LineSegment [constr] StartX=-209.443 StartY=-50.0944 StartZ=0 EndX=-209.443 EndY=-80.4316 EndZ=0
    g3: LineSegment StartX=-207.775 StartY=-41.3701 StartZ=0 EndX=-207.775 EndY=-80.4316 EndZ=0
    g4: LineSegment StartX=-211.843 StartY=-80.4316 StartZ=0 EndX=-207.775 EndY=-80.4316 EndZ=0
  constraints (15):
    c: Vertical(g0)
    c: Coincident(g1,g0)
    c: Vertical(g2)
    c: Tangent(g2,g-5)
    c: Coincident(g3,g1)
    c: Vertical(g3)
    c: DistanceY(g-3,g3) = -2
    c: Tangent(g1,g-8)
    c: DistanceY(g-3,g0) = -2
    c: Coincident(g4,g0)
    c: Coincident(g4,g3)
    c: Tangent(g0,g-6)
    c: DistanceY(g-3,g2) = -2
    c: DistanceY(g2,g0) = 0
    c: DistanceX(g-3,g3) = 6.8
FEATURE [Part::Extrusion] Extrude039  label="Extrude039 supporto alimentatore"
  Base = -> Sketch036
  Dir = (0,-1,2e-16)
  DirMode = 2
  FaceMakerClass = Part::FaceMakerBullseye
  FaceMakerMode = 3
  LengthFwd = 25.2
  LengthRev = 0
  Solid = true
  Symmetric = true
FEATURE [Sketcher::SketchObject] Sketch037  label="scavo per alimentatore"
  ArcFitTolerance = 1e-06
  AttachmentSupport = -> [XZ_Plane]
  ExternalGeometry = -> [Sketch036]
  FullyConstrained = true
  MakeInternals = false
  MapMode = 5
  Placement = pos=(0,0,0) rot=(1,0,0;1.5708rad)
  sketch-geometry (4):
    g0: LineSegment StartX=-209.575 StartY=-50.4316 StartZ=0 EndX=-209.575 EndY=-80.4316 EndZ=0
    g1: LineSegment StartX=-209.575 StartY=-50.4316 StartZ=0 EndX=-207.775 EndY=-50.4316 EndZ=0
    g2: LineSegment StartX=-207.775 StartY=-50.4316 StartZ=0 EndX=-207.775 EndY=-80.4316 EndZ=0
    g3: LineSegment StartX=-207.775 StartY=-80.4316 StartZ=0 EndX=-209.575 EndY=-80.4316 EndZ=0
  constraints (11):
    c: Vertical(g0)
    c: Coincident(g1,g0)
    c: Horizontal(g1)
    c: Coincident(g2,g1)
    c: Vertical(g2)
    c: Coincident(g3,g2)
    c: Coincident(g3,g0)
    c: Horizontal(g3)
    c: DistanceX(g1,g1) = 1.8
    c: Coincident(g2,g-3)
    c: DistanceY(g2,g2) = 30
FEATURE [Part::Extrusion] Extrude040  label="Extrude040 scavo alimentatore"
  Base = -> Sketch037
  Dir = (0,-1,2e-16)
  DirMode = 2
  FaceMakerClass = Part::FaceMakerBullseye
  FaceMakerMode = 3
  LengthFwd = 19.5
  LengthRev = 0
  Solid = true
  Symmetric = true
FEATURE [Part::Extrusion] Extrude031  label="Extrude fermo per scheda micro"
  Base = -> Sketch033
  Dir = (0,-1,2e-16)
  DirMode = 2
  FaceMakerClass = Part::FaceMakerBullseye
  FaceMakerMode = 3
  LengthFwd = 3
  LengthRev = 0
  Placement = pos=(0,8.6,0) rot=(0,0,1;0rad)
  Solid = true
  Symmetric = false
FEATURE [Sketcher::SketchObject] Sketch038  label="scavo driver solenoide"
  ArcFitTolerance = 1e-06
  AttachmentSupport = -> [XZ_Plane]
  ExternalGeometry = -> [Sketch,Sketch036]
  FullyConstrained = true
  MakeInternals = false
  MapMode = 5
  Placement = pos=(0,0,0) rot=(1,0,0;1.5708rad)
  sketch-geometry (8):
    g0: LineSegment StartX=-193.575 StartY=-10.9177 StartZ=0 EndX=-196.838 EndY=-9.39626 EndZ=0
    g1: LineSegment StartX=-196.838 StartY=-9.39626 StartZ=0 EndX=-214.165 EndY=-46.5549 EndZ=0
    g2: LineSegment StartX=-193.575 StartY=-10.9177 StartZ=0 EndX=-190.131 EndY=-12.5236 EndZ=0
    g3: LineSegment StartX=-190.131 StartY=-12.5236 StartZ=0 EndX=-206.38 EndY=-47.3701 EndZ=0
    g4: LineSegment [constr] StartX=-214.165 StartY=-46.5549 StartZ=0 EndX=-210.902 EndY=-48.0763 EndZ=0
    g5: LineSegment StartX=-214.165 StartY=-46.5549 StartZ=0 EndX=-210.902 EndY=-48.0763 EndZ=0
    g6: LineSegment StartX=-206.38 StartY=-47.3701 StartZ=0 EndX=-207.775 EndY=-47.3701 EndZ=0
    g7: LineSegment StartX=-207.775 StartY=-47.3701 StartZ=0 EndX=-210.902 EndY=-48.0763 EndZ=0
  constraints (23):
    c: Coincident(g1,g0)
    c: Coincident(g3,g2)
    c: Distance(g2) = 3.8
    c: Distance(g1) = 41
    c: Coincident(g4,g1)
    c: Distance(g4) = 3.6
    c: Perpendicular(g4,g-3)
    c: Parallel(g1,g-3)
    c: Perpendicular(g1,g0)
    c: Distance(g0) = 3.6
    c: Coincident(g5,g1)
    c: Parallel(g3,g-3)
    c: Perpendicular(g2,g3)
    c: Coincident(g2,g0)
    c: PointOnObject(g4,g-3)
    c: Distance(g-3,g4) = 6.4
    c: Coincident(g6,g3)
    c: Horizontal(g6)
    c: PointOnObject(g6,g-4)
    c: Coincident(g7,g6)
    c: Coincident(g7,g5)
    c: DistanceY(g6,g-4) = 6
    c: Coincident(g5,g4)
FEATURE [Part::Extrusion] Extrude041  label="Extrude scavo driver solenoide"
  Base = -> Sketch038
  Dir = (0,-1,2e-16)
  DirMode = 2
  FaceMakerClass = Part::FaceMakerBullseye
  FaceMakerMode = 3
  LengthFwd = 20.6
  LengthRev = 0
  Solid = true
  Symmetric = true
FEATURE [Sketcher::SketchObject] Sketch039  label="scavo per cavo usb per micro"
  ArcFitTolerance = 1e-06
  AttachmentSupport = -> [XZ_Plane]
  ExternalGeometry = -> [Sketch,Sketch016]
  FullyConstrained = true
  MakeInternals = false
  MapMode = 5
  Placement = pos=(0,0,0) rot=(1,0,0;1.5708rad)
  sketch-geometry (4):
    g0: LineSegment StartX=-82.51 StartY=36.4 StartZ=0 EndX=-74.51 EndY=36.4 EndZ=0
    g1: LineSegment StartX=-74.51 StartY=36.4 StartZ=0 EndX=-74.51 EndY=30.8 EndZ=0
    g2: LineSegment StartX=-74.51 StartY=30.8 StartZ=0 EndX=-82.51 EndY=30.8 EndZ=0
    g3: LineSegment StartX=-82.51 StartY=30.8 StartZ=0 EndX=-82.51 EndY=36.4 EndZ=0
  constraints (11):
    c: Coincident(g1,g0)
    c: Vertical(g1)
    c: Coincident(g2,g1)
    c: Horizontal(g2)
    c: Coincident(g3,g2)
    c: Coincident(g3,g0)
    c: Vertical(g3)
    c: Tangent(g0,g-3)
    c: Tangent(g2,g-4)
    c: Tangent(g3,g-4)
    c: Tangent(g1,g-4)
FEATURE [Part::Extrusion] Extrude042  label="Extrude scavo per cavo usb per micro"
  Base = -> Sketch039
  Dir = (0,-1,2e-16)
  DirMode = 2
  FaceMakerClass = Part::FaceMakerBullseye
  FaceMakerMode = 3
  LengthFwd = 13.2
  LengthRev = 0
  Placement = pos=(0,5.6,0) rot=(0,0,1;0rad)
  Solid = true
  Symmetric = false
FEATURE [Sketcher::SketchObject] Sketch040  label="scavo saldature alimentatore connettore 5v"
  ArcFitTolerance = 1e-06
  AttachmentSupport = -> [XZ_Plane]
  ExternalGeometry = -> [Sketch037]
  FullyConstrained = true
  MakeInternals = false
  MapMode = 5
  Placement = pos=(0,0,0) rot=(1,0,0;1.5708rad)
  sketch-geometry (4):
    g0: LineSegment StartX=-211.175 StartY=-52.4316 StartZ=0 EndX=-211.175 EndY=-56.4316 EndZ=0
    g1: LineSegment StartX=-211.175 StartY=-52.4316 StartZ=0 EndX=-209.575 EndY=-52.4316 EndZ=0
    g2: LineSegment StartX=-209.575 StartY=-52.4316 StartZ=0 EndX=-209.575 EndY=-56.4316 EndZ=0
    g3: LineSegment StartX=-209.575 StartY=-56.4316 StartZ=0 EndX=-211.175 EndY=-56.4316 EndZ=0
  constraints (11):
    c: Vertical(g0)
    c: Coincident(g1,g0)
    c: Horizontal(g1)
    c: Coincident(g2,g1)
    c: Coincident(g3,g2)
    c: Coincident(g3,g0)
    c: Horizontal(g3)
    c: DistanceX(g1,g1) = 1.6
    c: DistanceY(g2,g2) = 4
    c: Tangent(g2,g-3)
    c: DistanceY(g1,g-3) = 2
FEATURE [Part::Extrusion] Extrude043  label="Extrude scavo saldature alimentatore connettore 5v"
  Base = -> Sketch040
  Dir = (0,-1,2e-16)
  DirMode = 2
  FaceMakerClass = Part::FaceMakerBullseye
  FaceMakerMode = 3
  LengthFwd = 8
  LengthRev = 0
  Solid = true
  Symmetric = true
FEATURE [Sketcher::SketchObject] Sketch041  label="scavo saldature alimentatore connettore 5v verticali"
  ArcFitTolerance = 1e-06
  AttachmentSupport = -> [XZ_Plane]
  ExternalGeometry = -> [Sketch037]
  FullyConstrained = true
  MakeInternals = false
  MapMode = 5
  Placement = pos=(0,0,0) rot=(1,0,0;1.5708rad)
  sketch-geometry (4):
    g0: LineSegment StartX=-211.175 StartY=-53.6316 StartZ=0 EndX=-209.575 EndY=-53.6316 EndZ=0
    g1: LineSegment StartX=-209.575 StartY=-53.6316 StartZ=0 EndX=-209.575 EndY=-76.6316 EndZ=0
    g2: LineSegment StartX=-209.575 StartY=-76.6316 StartZ=0 EndX=-211.175 EndY=-76.6316 EndZ=0
    g3: LineSegment StartX=-211.175 StartY=-76.6316 StartZ=0 EndX=-211.175 EndY=-53.6316 EndZ=0
  constraints (11):
    c: Horizontal(g0)
    c: Coincident(g1,g0)
    c: Coincident(g2,g1)
    c: Horizontal(g2)
    c: Coincident(g3,g2)
    c: Coincident(g3,g0)
    c: Vertical(g3)
    c: DistanceY(g3,g3) = 23
    c: DistanceX(g0,g0) = 1.6
    c: Tangent(g1,g-3)
    c: DistanceY(g0,g-3) = 3.2
FEATURE [Part::Extrusion] Extrude044  label="Extrude scavo saldature alimentatore connettore 5v verticali"
  Base = -> Sketch041
  Dir = (0,-1,2e-16)
  DirMode = 2
  FaceMakerClass = Part::FaceMakerBullseye
  FaceMakerMode = 3
  LengthFwd = 3.2
  LengthRev = 0
  Placement = pos=(0,8.3,0) rot=(0,0,1;0rad)
  Solid = true
  Symmetric = false
FEATURE [Sketcher::SketchObject] Sketch042  label="fermi per driver solenoide e alimentatore"
  ArcFitTolerance = 1e-06
  AttachmentSupport = -> [XZ_Plane]
  ExternalGeometry = -> [Sketch036,Sketch037,Sketch,Sketch038]
  FullyConstrained = true
  MakeInternals = false
  MapMode = 5
  Placement = pos=(0,0,0) rot=(1,0,0;1.5708rad)
  sketch-geometry (27):
    g0: LineSegment StartX=-198.308 StartY=-21.0683 StartZ=0 EndX=-199.238 EndY=-23.0622 EndZ=0
    g1: LineSegment StartX=-199.238 StartY=-23.0622 StartZ=0 EndX=-197.244 EndY=-23.992 EndZ=0
    g2: LineSegment StartX=-197.244 StartY=-23.992 StartZ=0 EndX=-196.314 EndY=-21.9981 EndZ=0
    g3: LineSegment StartX=-196.314 StartY=-21.9981 StartZ=0 EndX=-198.308 EndY=-21.0683 EndZ=0
    g4: LineSegment StartX=-199.082 StartY=-18.9421 StartZ=0 EndX=-201.364 EndY=-23.8361 EndZ=0
    g5: LineSegment StartX=-201.364 StartY=-23.8361 StartZ=0 EndX=-197.92 EndY=-25.4421 EndZ=0
    g6: LineSegment StartX=-195.794 StartY=-24.6682 StartZ=0 EndX=-194.864 EndY=-22.6743 EndZ=0
    g7: LineSegment StartX=-195.638 StartY=-20.548 StartZ=0 EndX=-199.082 EndY=-18.9421 EndZ=0
    g8: LineSegment [constr] StartX=-196.47 StartY=-26.1183 StartZ=0 EndX=-195.794 EndY=-24.6682 EndZ=0
    g9: LineSegment [constr] StartX=-196.47 StartY=-26.1183 StartZ=0 EndX=-197.92 EndY=-25.4421 EndZ=0
    g10: ArcOfCircle CenterX=-196.314 CenterY=-21.9981 CenterZ=0 NormalX=0 NormalY=0 NormalZ=1 AngleXU=0 Radius=1.6 StartAngle=5.84685 EndAngle=7.41765
    g11: GeomPoint [constr] X=-194.188 Y=-21.2242 Z=0
    g12: ArcOfCircle CenterX=-197.244 CenterY=-23.992 CenterZ=0 NormalX=0 NormalY=0 NormalZ=1 AngleXU=0 Radius=1.6 StartAngle=4.27606 EndAngle=5.84685
    g13: GeomPoint [constr] X=-196.47 Y=-26.1183 Z=0
    g14: LineSegment StartX=-207.775 StartY=-46.8316 StartZ=0 EndX=-207.775 EndY=-50.8316 EndZ=0
    g15: LineSegment StartX=-207.775 StartY=-46.8316 StartZ=0 EndX=-203.775 EndY=-46.8316 EndZ=0
    g16: LineSegment StartX=-203.775 StartY=-46.8316 StartZ=0 EndX=-203.775 EndY=-50.8316 EndZ=0
    g17: LineSegment StartX=-207.775 StartY=-50.8316 StartZ=0 EndX=-203.775 EndY=-50.8316 EndZ=0
    g18: LineSegment StartX=-209.375 StartY=-52.4316 StartZ=0 EndX=-203.775 EndY=-52.4316 EndZ=0
    g19: LineSegment StartX=-202.175 StartY=-50.8316 StartZ=0 EndX=-202.175 EndY=-46.8316 EndZ=0
    g20: LineSegment StartX=-203.775 StartY=-45.2316 StartZ=0 EndX=-209.375 EndY=-45.2316 EndZ=0
    g21: LineSegment StartX=-209.375 StartY=-45.2316 StartZ=0 EndX=-209.375 EndY=-52.4316 EndZ=0
    g22: ArcOfCircle CenterX=-203.775 CenterY=-46.8316 CenterZ=0 NormalX=0 NormalY=0 NormalZ=1 AngleXU=0 Radius=1.6 StartAngle=1.8e-15 EndAngle=1.5708
    g23: GeomPoint [constr] X=-202.175 Y=-45.2316 Z=0
    g24: ArcOfCircle CenterX=-203.775 CenterY=-50.8316 CenterZ=0 NormalX=0 NormalY=0 NormalZ=1 AngleXU=0 Radius=1.6 StartAngle=4.71239 EndAngle=6.28319
    g25: GeomPoint [constr] X=-202.175 Y=-52.4316 Z=0
    g26: LineSegment [constr] StartX=-207.775 StartY=-50.4316 StartZ=0 EndX=-207.775 EndY=-50.8316 EndZ=0
  constraints (69):
    c: Coincident(g1,g0)
    c: Coincident(g2,g1)
    c: Coincident(g3,g2)
    c: Coincident(g3,g0)
    c: Parallel(g0,g2)
    c: Perpendicular(g3,g0)
    c: Perpendicular(g1,g0)
    c: Coincident(g5,g4)
    c: Coincident(g7,g4)
    c: Distance(g3) = 2.2
    c: Distance(g2) = 2.2
    c: Parallel(g6,g2)
    c: Parallel(g6,g4)
    c: Perpendicular(g5,g6)
    c: Perpendicular(g7,g6)
    c: Distance(g13,g11) = 5.4
    c: Distance(g5,g13) = 5.4
    c: Coincident(g9,g8)
    c: Distance(g8) = 1.6
    c: Distance(g9) = 1.6
    c: Perpendicular(g9,g8)
    c: Parallel(g8,g6)
    c: Coincident(g8,g13)
    c: Distance(g8,g1) = 1.6
    c: Distance(g9,g1) = 1.6
    c: Tangent(g0,g-5)
    c: Distance(g0,g-6) = 27.6
    c: PointOnObject(g11,g7)
    c: PointOnObject(g11,g6)
    c: Tangent(g7,g10) = -1.5708
    c: Tangent(g6,g10) = -1.5708
    c: PointOnObject(g13,g5)
    c: Tangent(g5,g12) = -1.5708
    c: Tangent(g6,g12) = -1.5708
    c: Equal(g10,g12)
    c: Coincident(g10,g2)
    c: Vertical(g14)
    c: Coincident(g15,g14)
    c: Horizontal(g15)
    c: Coincident(g16,g15)
    c: Vertical(g16)
    c: Coincident(g17,g14)
    c: Coincident(g17,g16)
    c: Horizontal(g17)
    c: Distance(g16) = 4
    c: Distance(g15) = 4
    c: Horizontal(g18)
    c: Vertical(g19)
    c: Horizontal(g20)
    c: Coincident(g21,g20)
    c: Coincident(g21,g18)
    c: Vertical(g21)
    c: Distance(g20,g23) = 7.2
    c: Distance(g25,g23) = 7.2
    c: DistanceY(g18,g14) = 1.6
    c: DistanceX(g18,g14) = 1.6
    c: PointOnObject(g23,g20)
    c: PointOnObject(g23,g19)
    c: Tangent(g20,g22) = -1.5708
    c: Tangent(g19,g22) = -1.5708
    c: PointOnObject(g25,g19)
    c: Tangent(g18,g24) = -1.5708
    c: Tangent(g19,g24) = -1.5708
    c: Equal(g22,g24)
    c: Coincident(g22,g15)
    c: Vertical(g26)
    c: Distance(g26) = 0.4
    c: Coincident(g26,g-4)
    c: Coincident(g14,g26)
FEATURE [Part::Extrusion] Extrude045  label="Extrude fermi per driver solenoide e alimentatore"
  Base = -> Sketch042
  Dir = (0,-1,2e-16)
  DirMode = 2
  FaceMakerClass = Part::FaceMakerBullseye
  FaceMakerMode = 3
  LengthFwd = 25.2
  LengthRev = 0
  Solid = true
  Symmetric = true
FEATURE [Sketcher::SketchObject] Sketch043  label="scavo pulizia fermo alimentatore"
  ArcFitTolerance = 1e-06
  AttachmentSupport = -> [XZ_Plane]
  ExternalGeometry = -> [Sketch042,Sketch036,Sketch037]
  FullyConstrained = true
  MakeInternals = false
  MapMode = 5
  Placement = pos=(0,0,0) rot=(1,0,0;1.5708rad)
  sketch-geometry (6):
    g0: LineSegment StartX=-209.375 StartY=-52.4316 StartZ=0 EndX=-209.375 EndY=-50.4316 EndZ=0
    g1: LineSegment StartX=-209.375 StartY=-50.4316 StartZ=0 EndX=-207.775 EndY=-50.4316 EndZ=0
    g2: LineSegment StartX=-207.775 StartY=-50.4316 StartZ=0 EndX=-207.775 EndY=-45.2316 EndZ=0
    g3: LineSegment StartX=-207.775 StartY=-45.2316 StartZ=0 EndX=-202.175 EndY=-45.2316 EndZ=0
    g4: LineSegment StartX=-202.175 StartY=-45.2316 StartZ=0 EndX=-202.175 EndY=-52.4316 EndZ=0
    g5: LineSegment StartX=-202.175 StartY=-52.4316 StartZ=0 EndX=-209.375 EndY=-52.4316 EndZ=0
  constraints (13):
    c: Vertical(g0)
    c: Coincident(g1,g0)
    c: Coincident(g2,g1)
    c: Coincident(g3,g2)
    c: Coincident(g4,g3)
    c: Coincident(g5,g4)
    c: Coincident(g5,g0)
    c: Horizontal(g5)
    c: Coincident(g0,g-6)
    c: Tangent(g1,g-8)
    c: Tangent(g2,g-4)
    c: Tangent(g3,g-7)
    c: Tangent(g4,g-3)
FEATURE [Part::Extrusion] Extrude046  label="Extrude scavo pulizia fermo alimentatore"
  Base = -> Sketch043
  Dir = (0,-1,2e-16)
  DirMode = 2
  FaceMakerClass = Part::FaceMakerBullseye
  FaceMakerMode = 3
  LengthFwd = 19.5
  LengthRev = 0
  Solid = true
  Symmetric = true
FEATURE [Sketcher::SketchObject] Sketch044  label="buchini per fissaggio oled"
  ArcFitTolerance = 1e-06
  AttachmentSupport = -> [YZ_Plane]
  ExternalGeometry = -> [Sketch]
  FullyConstrained = true
  MakeInternals = false
  MapMode = 5
  Placement = pos=(0,0,0) rot=(0.57735,0.57735,0.57735;2.0944rad)
  sketch-geometry (5):
    g0: LineSegment [constr] StartX=1.5e-14 StartY=67.3588 StartZ=0 EndX=0 EndY=64.3588 EndZ=0
    g1: LineSegment [constr] StartX=0 StartY=64.3588 StartZ=0 EndX=10.4 EndY=64.3588 EndZ=0
    g2: LineSegment [constr] StartX=0 StartY=64.3588 StartZ=0 EndX=-10.4 EndY=64.3588 EndZ=0
    g3: Circle CenterX=10.4 CenterY=64.3588 CenterZ=0 NormalX=0 NormalY=0 NormalZ=1 AngleXU=0 Radius=1.5
    g4: Circle CenterX=-10.4 CenterY=64.3588 CenterZ=0 NormalX=0 NormalY=0 NormalZ=1 AngleXU=0 Radius=1.5
  constraints (13):
    c: Distance(g0) = 3
    c: PointOnObject(g0,g-2)
    c: Coincident(g1,g0)
    c: Horizontal(g1)
    c: Coincident(g2,g0)
    c: Horizontal(g2)
    c: DistanceX(g1,g1) = 10.4
    c: Coincident(g3,g1)
    c: Diameter(g4) = 3
    c: Coincident(g4,g2)
    c: Coincident(g0,g-7)
    c: Equal(g1,g2)
    c: Equal(g4,g3)
FEATURE [Part::Extrusion] Extrude047  label="Extrude buchini per fissaggio oled"
  Base = -> Sketch044
  Dir = (1,0,0)
  DirMode = 2
  FaceMakerClass = Part::FaceMakerBullseye
  FaceMakerMode = 3
  LengthFwd = 10
  LengthRev = 0
  Placement = pos=(-186,0,0) rot=(0,0,1;0rad)
  Solid = true
  Symmetric = false
FEATURE [Sketcher::SketchObject] Sketch046  label="scavo 5x5 neopixel"
  ArcFitTolerance = 1e-06
  AttachmentSupport = -> [YZ_Plane002]
  FullyConstrained = true
  MakeInternals = false
  MapMode = 5
  Placement = pos=(0,0,0) rot=(0.57735,0.57735,0.57735;2.0944rad)
  sketch-geometry (4):
    g0: LineSegment StartX=-2.7 StartY=2.7 StartZ=0 EndX=2.7 EndY=2.7 EndZ=0
    g1: LineSegment StartX=2.7 StartY=2.7 StartZ=0 EndX=2.7 EndY=-2.7 EndZ=0
    g2: LineSegment StartX=2.7 StartY=-2.7 StartZ=0 EndX=-2.7 EndY=-2.7 EndZ=0
    g3: LineSegment StartX=-2.7 StartY=-2.7 StartZ=0 EndX=-2.7 EndY=2.7 EndZ=0
  constraints (11):
    c: Horizontal(g0)
    c: Coincident(g1,g0)
    c: Vertical(g1)
    c: Coincident(g2,g1)
    c: Horizontal(g2)
    c: Coincident(g3,g2)
    c: Coincident(g3,g0)
    c: Vertical(g3)
    c: DistanceX(g0,g0) = 5.4
    c: DistanceY(g1,g1) = 5.4
    c: Symmetric(g0,g1,g-1)
FEATURE [Sketcher::SketchObject] Sketch047  label="scavo 10x10 neopixel corpo"
  ArcFitTolerance = 1e-06
  AttachmentOffset = pos=(0,0,1) rot=(0,0,1;0rad)
  AttachmentSupport = -> [YZ_Plane002]
  FullyConstrained = true
  MakeInternals = false
  MapMode = 5
  Placement = pos=(1,0,0) rot=(0.57735,0.57735,0.57735;2.0944rad)
  sketch-geometry (4):
    g0: LineSegment StartX=-5 StartY=5.1 StartZ=0 EndX=5 EndY=5.1 EndZ=0
    g1: LineSegment StartX=5 StartY=5.1 StartZ=0 EndX=5 EndY=-5.1 EndZ=0
    g2: LineSegment StartX=5 StartY=-5.1 StartZ=0 EndX=-5 EndY=-5.1 EndZ=0
    g3: LineSegment StartX=-5 StartY=-5.1 StartZ=0 EndX=-5 EndY=5.1 EndZ=0
  constraints (11):
    c: Horizontal(g0)
    c: Coincident(g1,g0)
    c: Vertical(g1)
    c: Coincident(g2,g1)
    c: Horizontal(g2)
    c: Coincident(g3,g2)
    c: Coincident(g3,g0)
    c: Vertical(g3)
    c: DistanceX(g0,g0) = 10
    c: DistanceY(g1,g1) = 10.2
    c: Symmetric(g0,g2,g-1)
FEATURE [Sketcher::SketchObject] Sketch048  label="buco per perno blocco neopixel"
  ArcFitTolerance = 1e-06
  AttachmentSupport = -> [XZ_Plane002]
  FullyConstrained = true
  MakeInternals = false
  MapMode = 5
  Placement = pos=(0,0,0) rot=(1,0,0;1.5708rad)
  sketch-geometry (4):
    g0: LineSegment StartX=3 StartY=1.2 StartZ=0 EndX=3 EndY=-1.2 EndZ=0
    g1: LineSegment StartX=3 StartY=-1.2 StartZ=0 EndX=5.4 EndY=-1.2 EndZ=0
    g2: LineSegment StartX=5.4 StartY=-1.2 StartZ=0 EndX=5.4 EndY=1.2 EndZ=0
    g3: LineSegment StartX=5.4 StartY=1.2 StartZ=0 EndX=3 EndY=1.2 EndZ=0
  constraints (11):
    c: Coincident(g1,g0)
    c: Horizontal(g1)
    c: Coincident(g2,g1)
    c: Vertical(g2)
    c: Coincident(g3,g2)
    c: Coincident(g3,g0)
    c: Horizontal(g3)
    c: DistanceX(g1,g1) = 2.4
    c: DistanceY(g2,g2) = 2.4
    c: Symmetric(g0,g0,g-1)
    c: DistanceX(g-1,g0) = 3
FEATURE [Sketcher::SketchObject] Sketch045  label="blocco principale per neopixel"
  ArcFitTolerance = 1e-06
  AttachmentSupport = -> [XZ_Plane002]
  ExternalGeometry = -> [Sketch048]
  FullyConstrained = true
  MakeInternals = false
  MapMode = 5
  Placement = pos=(0,0,0) rot=(1,0,0;1.5708rad)
  sketch-geometry (6):
    g0: LineSegment StartX=0 StartY=5.1 StartZ=0 EndX=0 EndY=-5.1 EndZ=0
    g1: LineSegment StartX=0 StartY=-5.1 StartZ=0 EndX=3 EndY=-5.1 EndZ=0
    g2: LineSegment StartX=7 StartY=-1.1 StartZ=0 EndX=7 EndY=5.1 EndZ=0
    g3: LineSegment StartX=7 StartY=5.1 StartZ=0 EndX=0 EndY=5.1 EndZ=0
    g4: ArcOfCircle CenterX=3 CenterY=-1.1 CenterZ=0 NormalX=0 NormalY=0 NormalZ=1 AngleXU=0 Radius=4 StartAngle=4.71239 EndAngle=6.28319
    g5: GeomPoint [constr] X=7 Y=-5.1 Z=0
  constraints (15):
    c: Vertical(g0)
    c: Coincident(g1,g0)
    c: Horizontal(g1)
    c: Vertical(g2)
    c: Coincident(g3,g2)
    c: Coincident(g3,g0)
    c: Horizontal(g3)
    c: DistanceY(g0,g0) = 10.2
    c: Symmetric(g0,g0,g-1)
    c: DistanceX(g3,g3) = 7
    c: PointOnObject(g5,g2)
    c: PointOnObject(g5,g1)
    c: Tangent(g2,g4) = -1.5708
    c: Tangent(g1,g4) = -1.5708
    c: DistanceX(g-3,g1) = 0
FEATURE [Sketcher::SketchObject] Sketch049  label="rinforzi esterni per corpo neopoixel"
  ArcFitTolerance = 1e-06
  AttachmentSupport = -> [XZ_Plane002]
  ExternalGeometry = -> [Sketch045]
  FullyConstrained = true
  MakeInternals = false
  MapMode = 5
  Placement = pos=(0,0,0) rot=(1,0,0;1.5708rad)
  sketch-geometry (8):
    g0: LineSegment StartX=1 StartY=-4.1 StartZ=0 EndX=2 EndY=-4.1 EndZ=0
    g1: LineSegment StartX=2 StartY=-4.1 StartZ=0 EndX=2 EndY=-5.1 EndZ=0
    g2: LineSegment StartX=2 StartY=-5.1 StartZ=0 EndX=1 EndY=-5.1 EndZ=0
    g3: LineSegment StartX=1 StartY=-5.1 StartZ=0 EndX=1 EndY=-4.1 EndZ=0
    g4: LineSegment StartX=1 StartY=5.1 StartZ=0 EndX=2 EndY=5.1 EndZ=0
    g5: LineSegment StartX=2 StartY=5.1 StartZ=0 EndX=2 EndY=4.1 EndZ=0
    g6: LineSegment StartX=2 StartY=4.1 StartZ=0 EndX=1 EndY=4.1 EndZ=0
    g7: LineSegment StartX=1 StartY=4.1 StartZ=0 EndX=1 EndY=5.1 EndZ=0
  constraints (24):
    c: Horizontal(g0)
    c: Coincident(g1,g0)
    c: Vertical(g1)
    c: Coincident(g2,g1)
    c: Horizontal(g2)
    c: Coincident(g3,g2)
    c: Coincident(g3,g0)
    c: Vertical(g3)
    c: Horizontal(g4)
    c: Coincident(g5,g4)
    c: Vertical(g5)
    c: Coincident(g6,g5)
    c: Horizontal(g6)
    c: Coincident(g7,g6)
    c: Coincident(g7,g4)
    c: Vertical(g7)
    c: DistanceX(g4,g4) = 1
    c: DistanceY(g5,g5) = 1
    c: DistanceX(g0,g0) = 1
    c: DistanceY(g1,g1) = 1
    c: DistanceX(g-3,g4) = 1
    c: DistanceY(g-3,g4) = 0
    c: DistanceX(g-4,g2) = 1
    c: DistanceY(g2,g-4) = 0
FEATURE [Sketcher::SketchObject] Sketch052  label="scavo saldature driver solenoide"
  ArcFitTolerance = 1e-06
  AttachmentSupport = -> [XZ_Plane]
  ExternalGeometry = -> [Sketch038]
  FullyConstrained = true
  MakeInternals = false
  MapMode = 5
  Placement = pos=(0,0,0) rot=(1,0,0;1.5708rad)
  sketch-geometry (4):
    g0: LineSegment StartX=-197.2 StartY=-9.22721 StartZ=0 EndX=-198.891 EndY=-12.8524 EndZ=0
    g1: LineSegment StartX=-198.891 StartY=-12.8524 StartZ=0 EndX=-198.528 EndY=-13.0215 EndZ=0
    g2: LineSegment StartX=-198.528 StartY=-13.0215 StartZ=0 EndX=-196.838 EndY=-9.39626 EndZ=0
    g3: LineSegment StartX=-196.838 StartY=-9.39626 StartZ=0 EndX=-197.2 EndY=-9.22721 EndZ=0
  constraints (11):
    c: Coincident(g1,g0)
    c: Coincident(g2,g1)
    c: Coincident(g3,g2)
    c: Coincident(g3,g0)
    c: Parallel(g2,g0)
    c: Perpendicular(g2,g3)
    c: Perpendicular(g1,g2,g1) = 1.5708
    c: Parallel(g2,g-3)
    c: Distance(g2) = 4
    c: Distance(g3) = 0.4
    c: Coincident(g2,g-3)
FEATURE [Part::Extrusion] Extrude055  label="Extrude scavo saldature driver solenoide"
  Base = -> Sketch052
  Dir = (0,-1,2e-16)
  DirMode = 2
  FaceMakerClass = Part::FaceMakerBullseye
  FaceMakerMode = 3
  LengthFwd = 6
  LengthRev = 0
  Solid = true
  Symmetric = true
FEATURE [Sketcher::SketchObject] Sketch053  label="scavo saldature rumble"
  ArcFitTolerance = 1e-06
  AttachmentSupport = -> [XZ_Plane]
  ExternalGeometry = -> [Sketch019]
  FullyConstrained = true
  MakeInternals = false
  MapMode = 5
  Placement = pos=(0,0,0) rot=(1,0,0;1.5708rad)
  sketch-geometry (4):
    g0: LineSegment StartX=-169.451 StartY=-56.8615 StartZ=0 EndX=-170.687 EndY=-60.6657 EndZ=0
    g1: LineSegment StartX=-170.687 StartY=-60.6657 StartZ=0 EndX=-169.546 EndY=-61.0365 EndZ=0
    g2: LineSegment StartX=-169.546 StartY=-61.0365 StartZ=0 EndX=-168.31 EndY=-57.2323 EndZ=0
    g3: LineSegment StartX=-168.31 StartY=-57.2323 StartZ=0 EndX=-169.451 EndY=-56.8615 EndZ=0
  constraints (11):
    c: Coincident(g1,g0)
    c: Coincident(g2,g1)
    c: Coincident(g3,g2)
    c: Coincident(g3,g0)
    c: Parallel(g0,g2)
    c: Perpendicular(g3,g0)
    c: Perpendicular(g1,g0)
    c: Parallel(g0,g-3)
    c: Distance(g0) = 4
    c: Coincident(g0,g-3)
    c: Distance(g1) = 1.2
FEATURE [Part::Extrusion] Extrude056  label="Extrude scavo saldature rumble"
  Base = -> Sketch053
  Dir = (0,-1,2e-16)
  DirMode = 2
  FaceMakerClass = Part::FaceMakerBullseye
  FaceMakerMode = 3
  LengthFwd = 8.4
  LengthRev = 0
  Solid = true
  Symmetric = true
FEATURE [Sketcher::SketchObject] Sketch054  label="scavo saldature alimentatore connettore USB"
  ArcFitTolerance = 1e-06
  AttachmentSupport = -> [XZ_Plane]
  ExternalGeometry = -> [Sketch037]
  FullyConstrained = true
  MakeInternals = false
  MapMode = 5
  Placement = pos=(0,0,0) rot=(1,0,0;1.5708rad)
  sketch-geometry (4):
    g0: LineSegment StartX=-209.575 StartY=-80.4316 StartZ=0 EndX=-210.375 EndY=-80.4316 EndZ=0
    g1: LineSegment StartX=-210.375 StartY=-80.4316 StartZ=0 EndX=-210.375 EndY=-72.4316 EndZ=0
    g2: LineSegment StartX=-210.375 StartY=-72.4316 StartZ=0 EndX=-209.575 EndY=-72.4316 EndZ=0
    g3: LineSegment StartX=-209.575 StartY=-72.4316 StartZ=0 EndX=-209.575 EndY=-80.4316 EndZ=0
  constraints (11):
    c: Horizontal(g0)
    c: Coincident(g1,g0)
    c: Vertical(g1)
    c: Coincident(g2,g1)
    c: Horizontal(g2)
    c: Coincident(g3,g2)
    c: Coincident(g3,g0)
    c: Vertical(g3)
    c: DistanceX(g0,g0) = 0.8
    c: DistanceY(g3,g3) = 8
    c: Coincident(g0,g-4)
FEATURE [Part::Extrusion] Extrude057  label="Extrude scavo saldature alimentatore connettore USB"
  Base = -> Sketch054
  Dir = (0,-1,2e-16)
  DirMode = 2
  FaceMakerClass = Part::FaceMakerBullseye
  FaceMakerMode = 3
  LengthFwd = 11
  LengthRev = 0
  Solid = true
  Symmetric = true
FEATURE [Sketcher::SketchObject] Sketch055  label="buco interno per micro switch"
  ArcFitTolerance = 1e-06
  AttachmentSupport = -> [XZ_Plane]
  ExternalGeometry = -> [Sketch]
  FullyConstrained = true
  MakeInternals = false
  MapMode = 5
  Placement = pos=(0,0,0) rot=(1,0,0;1.5708rad)
  sketch-geometry (11):
    g0: LineSegment [constr] StartX=-194.483 StartY=34.2854 StartZ=0 EndX=-196.022 EndY=30.0568 EndZ=0
    g1: LineSegment [constr] StartX=-196.022 StartY=30.0568 StartZ=0 EndX=-197.561 EndY=25.8282 EndZ=0
    g2: LineSegment [constr] StartX=-196.022 StartY=30.0568 StartZ=0 EndX=-194.143 EndY=29.3727 EndZ=0
    g3: LineSegment [constr] StartX=-196.022 StartY=30.0568 StartZ=0 EndX=-197.902 EndY=30.7408 EndZ=0
    g4: LineSegment StartX=-196.362 StartY=34.9694 StartZ=0 EndX=-192.604 EndY=33.6014 EndZ=0
    g5: LineSegment StartX=-199.441 StartY=26.5122 StartZ=0 EndX=-195.682 EndY=25.1441 EndZ=0
    g6: LineSegment StartX=-192.604 StartY=33.6014 StartZ=0 EndX=-195.682 EndY=25.1441 EndZ=0
    g7: LineSegment StartX=-196.362 StartY=34.9694 StartZ=0 EndX=-199.441 EndY=26.5122 EndZ=0
    g8: GeomPoint [constr] X=-187.821 Y=29.2 Z=0
    g9: LineSegment [constr] StartX=-188.505 StartY=27.3206 StartZ=0 EndX=-196.022 EndY=30.0568 EndZ=0
    g10: LineSegment [constr] StartX=-187.821 StartY=29.2 StartZ=0 EndX=-188.505 EndY=27.3206 EndZ=0
  constraints (27):
    c: Coincident(g2,g0)
    c: Parallel(g0,g-3)
    c: Tangent(g1,g0) = -1.5708
    c: Perpendicular(g0,g2)
    c: Tangent(g2,g3)
    c: Distance(g0,g1) = 9
    c: Equal(g0,g1)
    c: Distance(g3,g2) = 4
    c: Equal(g2,g3)
    c: Parallel(g3,g4)
    c: Symmetric(g4,g4,g0)
    c: Parallel(g6,g1)
    c: Parallel(g7,g1)
    c: Symmetric(g6,g6,g2)
    c: Symmetric(g5,g5,g1)
    c: Symmetric(g7,g7,g3)
    c: Coincident(g7,g4)
    c: Coincident(g6,g4)
    c: Coincident(g5,g6)
    c: Symmetric(g-3,g-3,g8)
    c: Perpendicular(g-3,g9)
    c: Distance(g9) = 8
    c: Coincident(g3,g9)
    c: Coincident(g10,g8)
    c: Parallel(g10,g-3)
    c: Distance(g10) = 2
    c: Coincident(g10,g9)
FEATURE [Sketcher::SketchObject] Sketch056  label="buco esterno per micro switch"
  ArcFitTolerance = 1e-06
  AttachmentSupport = -> [XZ_Plane]
  ExternalGeometry = -> [Sketch055]
  FullyConstrained = true
  MakeInternals = false
  MapMode = 5
  Placement = pos=(0,0,0) rot=(1,0,0;1.5708rad)
  sketch-geometry (17):
    g0: GeomPoint [constr] X=-194.143 Y=29.3727 Z=0
    g1: GeomPoint [constr] X=-194.483 Y=34.2854 Z=0
    g2: GeomPoint [constr] X=-197.902 Y=30.7408 Z=0
    g3: GeomPoint [constr] X=-197.561 Y=25.8282 Z=0
    g4: GeomPoint [constr] X=-196.022 Y=30.0568 Z=0
    g5: LineSegment [constr] StartX=-194.483 StartY=34.2854 StartZ=0 EndX=-196.022 EndY=30.0568 EndZ=0
    g6: LineSegment [constr] StartX=-196.022 StartY=30.0568 StartZ=0 EndX=-197.561 EndY=25.8282 EndZ=0
    g7: LineSegment [constr] StartX=-197.902 StartY=30.7408 StartZ=0 EndX=-196.022 EndY=30.0568 EndZ=0
    g8: LineSegment [constr] StartX=-196.022 StartY=30.0568 StartZ=0 EndX=-194.143 EndY=29.3727 EndZ=0
    g9: LineSegment [constr] StartX=-195.338 StartY=31.9362 StartZ=0 EndX=-196.022 EndY=30.0568 EndZ=0
    g10: LineSegment [constr] StartX=-196.022 StartY=30.0568 StartZ=0 EndX=-196.706 EndY=28.1774 EndZ=0
    g11: LineSegment [constr] StartX=-196.022 StartY=30.0568 StartZ=0 EndX=-196.821 EndY=30.3475 EndZ=0
    g12: LineSegment [constr] StartX=-196.022 StartY=30.0568 StartZ=0 EndX=-195.223 EndY=29.7661 EndZ=0
    g13: LineSegment StartX=-194.539 StartY=31.6454 StartZ=0 EndX=-195.907 EndY=27.8867 EndZ=0
    g14: LineSegment StartX=-196.137 StartY=32.2269 StartZ=0 EndX=-197.505 EndY=28.4681 EndZ=0
    g15: LineSegment StartX=-196.137 StartY=32.2269 StartZ=0 EndX=-194.539 EndY=31.6454 EndZ=0
    g16: LineSegment StartX=-197.505 StartY=28.4681 StartZ=0 EndX=-195.907 EndY=27.8867 EndZ=0
  constraints (34):
    c: Symmetric(g-5,g-5,g1)
    c: Symmetric(g-5,g-6,g0)
    c: Symmetric(g-6,g-6,g3)
    c: Symmetric(g-5,g-6,g2)
    c: Coincident(g5,g1)
    c: Coincident(g5,g4)
    c: Coincident(g6,g4)
    c: Coincident(g6,g3)
    c: Equal(g5,g6)
    c: Coincident(g7,g2)
    c: Coincident(g7,g4)
    c: Coincident(g8,g4)
    c: Coincident(g8,g0)
    c: Equal(g7,g8)
    c: Coincident(g11,g9)
    c: Coincident(g12,g9)
    c: Tangent(g10,g9) = -1.5708
    c: Perpendicular(g11,g9)
    c: Parallel(g9,g-4)
    c: Equal(g9,g10)
    c: Parallel(g12,g11)
    c: Equal(g11,g12)
    c: Distance(g11,g12) = 1.7
    c: Distance(g9,g10) = 4
    c: Symmetric(g13,g13,g12)
    c: Parallel(g13,g9)
    c: Symmetric(g14,g14,g11)
    c: Symmetric(g15,g15,g9)
    c: Parallel(g15,g11)
    c: Symmetric(g16,g16,g10)
    c: Coincident(g16,g14)
    c: Coincident(g15,g14)
    c: Coincident(g13,g15)
    c: Coincident(g9,g4)
FEATURE [Sketcher::SketchObject] Sketch057  label="buco interno per SWITCH"
  ArcFitTolerance = 1e-06
  AttachmentSupport = -> [XZ_Plane]
  ExternalGeometry = -> [Sketch]
  FullyConstrained = true
  MakeInternals = false
  MapMode = 5
  Placement = pos=(0,0,0) rot=(1,0,0;1.5708rad)
  sketch-geometry (10):
    g0: GeomPoint [constr] X=-187.821 Y=29.2 Z=0
    g1: LineSegment [constr] StartX=-188.505 StartY=27.3206 StartZ=0 EndX=-193.203 EndY=29.0307 EndZ=0
    g2: LineSegment [constr] StartX=-190.809 StartY=35.6086 StartZ=0 EndX=-195.597 EndY=22.4529 EndZ=0
    g3: GeomPoint [constr] X=-193.203 Y=29.0307 Z=0
    g4: LineSegment [constr] StartX=-196.492 StartY=30.2278 StartZ=0 EndX=-189.914 EndY=27.8336 EndZ=0
    g5: LineSegment StartX=-194.098 StartY=36.8056 StartZ=0 EndX=-187.52 EndY=34.4115 EndZ=0
    g6: LineSegment StartX=-194.098 StartY=36.8056 StartZ=0 EndX=-198.886 EndY=23.6499 EndZ=0
    g7: LineSegment StartX=-187.52 StartY=34.4115 StartZ=0 EndX=-192.308 EndY=21.2558 EndZ=0
    g8: LineSegment StartX=-198.886 StartY=23.6499 StartZ=0 EndX=-192.308 EndY=21.2558 EndZ=0
    g9: LineSegment [constr] StartX=-187.821 StartY=29.2 StartZ=0 EndX=-188.505 EndY=27.3206 EndZ=0
  constraints (23):
    c: Symmetric(g-3,g-3,g0)
    c: Perpendicular(g1,g-3)
    c: Parallel(g2,g-3)
    c: Symmetric(g2,g2,g3)
    c: Perpendicular(g2,g4)
    c: Symmetric(g4,g4,g3)
    c: Distance(g2) = 14
    c: Distance(g4) = 7
    c: Distance(g1) = 5
    c: Parallel(g5,g4)
    c: Parallel(g7,g2)
    c: Symmetric(g5,g5,g2)
    c: Symmetric(g6,g6,g4)
    c: Symmetric(g7,g7,g4)
    c: Symmetric(g8,g8,g2)
    c: Coincident(g6,g5)
    c: Coincident(g7,g5)
    c: Coincident(g8,g7)
    c: Coincident(g3,g1)
    c: Coincident(g9,g0)
    c: Parallel(g9,g-3)
    c: Distance(g9) = 2
    c: Coincident(g1,g9)
FEATURE [Sketcher::SketchObject] Sketch058  label="buco esterno per SWITCH"
  ArcFitTolerance = 1e-06
  AttachmentSupport = -> [XZ_Plane]
  ExternalGeometry = -> [Sketch057]
  FullyConstrained = true
  MakeInternals = false
  MapMode = 5
  Placement = pos=(0,0,0) rot=(1,0,0;1.5708rad)
  sketch-geometry (12):
    g0: GeomPoint [constr] X=-190.809 Y=35.6086 Z=0
    g1: GeomPoint [constr] X=-196.492 Y=30.2278 Z=0
    g2: GeomPoint [constr] X=-189.914 Y=27.8336 Z=0
    g3: GeomPoint [constr] X=-195.597 Y=22.4529 Z=0
    g4: GeomPoint [constr] X=-193.203 Y=29.0307 Z=0
    g5: LineSegment [constr] StartX=-192.006 StartY=32.3196 StartZ=0 EndX=-194.4 EndY=25.7418 EndZ=0
    g6: GeomPoint [constr] X=-193.203 Y=29.0307 Z=0
    g7: LineSegment [constr] StartX=-195.082 StartY=29.7148 StartZ=0 EndX=-191.324 EndY=28.3467 EndZ=0
    g8: LineSegment StartX=-193.885 StartY=33.0037 StartZ=0 EndX=-190.127 EndY=31.6356 EndZ=0
    g9: LineSegment StartX=-190.127 StartY=31.6356 StartZ=0 EndX=-192.521 EndY=25.0578 EndZ=0
    g10: LineSegment StartX=-196.28 StartY=26.4258 StartZ=0 EndX=-192.521 EndY=25.0578 EndZ=0
    g11: LineSegment StartX=-193.885 StartY=33.0037 StartZ=0 EndX=-196.28 EndY=26.4258 EndZ=0
  constraints (21):
    c: Symmetric(g-6,g-6,g3)
    c: Symmetric(g-4,g-6,g2)
    c: Symmetric(g-5,g-4,g0)
    c: Symmetric(g-5,g-6,g1)
    c: Symmetric(g1,g2,g4)
    c: Parallel(g5,g-4)
    c: Symmetric(g5,g5,g6)
    c: Perpendicular(g7,g5)
    c: Symmetric(g7,g7,g6)
    c: Distance(g5) = 7
    c: Distance(g7) = 4
    c: Parallel(g8,g7)
    c: Parallel(g11,g5)
    c: Symmetric(g8,g8,g5)
    c: Symmetric(g9,g9,g7)
    c: Symmetric(g10,g10,g5)
    c: Symmetric(g11,g11,g7)
    c: Coincident(g11,g8)
    c: Coincident(g9,g8)
    c: Coincident(g9,g10)
    c: Coincident(g6,g4)
FEATURE [Part::Extrusion] Extrude060  label="Extrude buco interno per SWITCH destro"
  Base = -> Sketch057
  Dir = (0,-1,2e-16)
  DirMode = 2
  FaceMakerClass = Part::FaceMakerBullseye
  FaceMakerMode = 3
  LengthFwd = 13.2
  LengthRev = 0
  Placement = pos=(0,2.6,0) rot=(0,0,1;0rad)
  Solid = true
  Symmetric = false
FEATURE [Part::Extrusion] Extrude061  label="Extrude buco esterno per SWITCH destro"
  Base = -> Sketch058
  Dir = (0,-1,2e-16)
  DirMode = 2
  FaceMakerClass = Part::FaceMakerBullseye
  FaceMakerMode = 3
  LengthFwd = 2
  LengthRev = 0
  Placement = pos=(0,-10.6,0) rot=(0,0,1;0rad)
  Solid = true
  Symmetric = false
FEATURE [Sketcher::SketchObject] Sketch059  label="buco per spazio introduzione SWITCH"
  ArcFitTolerance = 1e-06
  AttachmentSupport = -> [XZ_Plane]
  ExternalGeometry = -> [Sketch057,Sketch010]
  FullyConstrained = true
  MakeInternals = false
  MapMode = 5
  Placement = pos=(0,0,0) rot=(1,0,0;1.5708rad)
  sketch-geometry (8):
    g0: LineSegment [constr] StartX=-201.368 StartY=36.3521 StartZ=0 EndX=-195.094 EndY=34.0687 EndZ=0
    g1: LineSegment [constr] StartX=-194.098 StartY=36.8056 StartZ=0 EndX=-195.094 EndY=34.0687 EndZ=0
    g2: LineSegment StartX=-198.658 StartY=24.2771 StartZ=0 EndX=-199.654 EndY=21.5401 EndZ=0
    g3: LineSegment StartX=-199.654 StartY=21.5401 StartZ=0 EndX=-181.196 EndY=14.822 EndZ=0
    g4: LineSegment StartX=-181.196 StartY=14.822 StartZ=0 EndX=-180.2 EndY=17.559 EndZ=0
    g5: LineSegment StartX=-180.2 StartY=17.559 StartZ=0 EndX=-198.658 EndY=24.2771 EndZ=0
    g6: LineSegment [constr] StartX=-204.932 StartY=26.5605 StartZ=0 EndX=-198.658 EndY=24.2771 EndZ=0
    g7: LineSegment [constr] StartX=-198.658 StartY=24.2771 StartZ=0 EndX=-199.654 EndY=21.5401 EndZ=0
  constraints (20):
    c: Parallel(g1,g-3)
    c: Parallel(g0,g-4)
    c: Coincident(g0,g-4)
    c: Coincident(g1,g-3)
    c: Coincident(g0,g1)
    c: Coincident(g3,g2)
    c: Coincident(g4,g3)
    c: Coincident(g5,g4)
    c: Coincident(g5,g2)
    c: Parallel(g5,g-5)
    c: Parallel(g3,g-5)
    c: Parallel(g4,g-6)
    c: DistanceX(g-6,g4) = 0
    c: Coincident(g6,g-5)
    c: Equal(g6,g0)
    c: Coincident(g7,g6)
    c: Equal(g7,g1)
    c: Tangent(g7,g-3)
    c: Coincident(g2,g6)
    c: Coincident(g2,g7)
FEATURE [Part::Extrusion] Extrude062  label="Extrude buco per spazio introduzione SWITCH"
  Base = -> Sketch059
  Dir = (0,-1,2e-16)
  DirMode = 2
  FaceMakerClass = Part::FaceMakerBullseye
  FaceMakerMode = 3
  LengthFwd = 13.2
  LengthRev = 0
  Solid = true
  Symmetric = true
FEATURE [Part::Extrusion] Extrude063  label="Extrude buco interno per SWITCH sinistro"
  Base = -> Sketch057
  Dir = (0,-1,2e-16)
  DirMode = 2
  FaceMakerClass = Part::FaceMakerBullseye
  FaceMakerMode = 3
  LengthFwd = 13.2
  LengthRev = 0
  Placement = pos=(0,10.6,0) rot=(0,0,1;0rad)
  Solid = true
  Symmetric = false
FEATURE [Part::Extrusion] Extrude064  label="Extrude buco esterno per SWITCH sinistro"
  Base = -> Sketch058
  Dir = (0,-1,2e-16)
  DirMode = 2
  FaceMakerClass = Part::FaceMakerBullseye
  FaceMakerMode = 3
  LengthFwd = 2
  LengthRev = 0
  Placement = pos=(0,12.6,0) rot=(0,0,1;0rad)
  Solid = true
  Symmetric = false
FEATURE [Sketcher::SketchObject] Sketch061  label="struttura esterna blocco switch"
  ArcFitTolerance = 1e-06
  AttachmentSupport = -> [XZ_Plane003]
  FullyConstrained = true
  MakeInternals = false
  MapMode = 5
  Placement = pos=(0,0,0) rot=(1,0,0;1.5708rad)
  sketch-geometry (5):
    g0: LineSegment StartX=-1 StartY=-5.1 StartZ=0 EndX=1 EndY=-5.1 EndZ=0
    g1: LineSegment StartX=1 StartY=-5.1 StartZ=0 EndX=1 EndY=5.1 EndZ=0
    g2: LineSegment StartX=1 StartY=5.1 StartZ=0 EndX=-1 EndY=5.1 EndZ=0
    g3: LineSegment StartX=-1 StartY=5.1 StartZ=0 EndX=-1 EndY=-5.1 EndZ=0
    g4: GeomPoint [constr] X=0 Y=0 Z=0
  constraints (12):
    c: Coincident(g0,g1)
    c: Coincident(g1,g2)
    c: Coincident(g2,g3)
    c: Coincident(g3,g0)
    c: Horizontal(g0)
    c: Horizontal(g2)
    c: Vertical(g1)
    c: Vertical(g3)
    c: Symmetric(g2,g0,g4)
    c: Distance(g1,g3) = 2
    c: Distance(g0,g2) = 10.2
    c: Coincident(g4,g-1)
FEATURE [Sketcher::SketchObject] Sketch062  label="struttura interna blocco switch"
  ArcFitTolerance = 1e-06
  AttachmentSupport = -> [XZ_Plane003]
  ExternalGeometry = -> [Sketch061]
  FullyConstrained = true
  MakeInternals = false
  MapMode = 5
  Placement = pos=(0,0,0) rot=(1,0,0;1.5708rad)
  sketch-geometry (5):
    g0: LineSegment StartX=-1 StartY=3.1 StartZ=0 EndX=-1 EndY=-3.1 EndZ=0
    g1: LineSegment StartX=-1 StartY=-3.1 StartZ=0 EndX=1 EndY=-3.1 EndZ=0
    g2: LineSegment StartX=1 StartY=-3.1 StartZ=0 EndX=1 EndY=3.1 EndZ=0
    g3: LineSegment StartX=1 StartY=3.1 StartZ=0 EndX=-1 EndY=3.1 EndZ=0
    g4: GeomPoint [constr] X=0 Y=0 Z=0
  constraints (12):
    c: Coincident(g0,g1)
    c: Coincident(g1,g2)
    c: Coincident(g2,g3)
    c: Coincident(g3,g0)
    c: Vertical(g0)
    c: Vertical(g2)
    c: Horizontal(g1)
    c: Horizontal(g3)
    c: Symmetric(g2,g0,g4)
    c: Coincident(g4,g-1)
    c: Distance(g0) = 6.2
    c: Equal(g3,g-3)
FEATURE [Sketcher::SketchObject] Sketch063  label="blocchi tra switch"
  ArcFitTolerance = 1e-06
  AttachmentSupport = -> [XZ_Plane003]
  ExternalGeometry = -> [Sketch061,Sketch062]
  FullyConstrained = true
  MakeInternals = false
  MapMode = 5
  Placement = pos=(0,0,0) rot=(1,0,0;1.5708rad)
  sketch-geometry (8):
    g0: LineSegment StartX=-3 StartY=5.1 StartZ=0 EndX=-1 EndY=5.1 EndZ=0
    g1: LineSegment StartX=-1 StartY=5.1 StartZ=0 EndX=-1 EndY=3.1 EndZ=0
    g2: LineSegment StartX=-1 StartY=3.1 StartZ=0 EndX=-3 EndY=3.1 EndZ=0
    g3: LineSegment StartX=-3 StartY=3.1 StartZ=0 EndX=-3 EndY=5.1 EndZ=0
    g4: LineSegment StartX=-3 StartY=-3.1 StartZ=0 EndX=-1 EndY=-3.1 EndZ=0
    g5: LineSegment StartX=-1 StartY=-3.1 StartZ=0 EndX=-1 EndY=-5.1 EndZ=0
    g6: LineSegment StartX=-1 StartY=-5.1 StartZ=0 EndX=-3 EndY=-5.1 EndZ=0
    g7: LineSegment StartX=-3 StartY=-5.1 StartZ=0 EndX=-3 EndY=-3.1 EndZ=0
  constraints (20):
    c: Horizontal(g0)
    c: Coincident(g1,g0)
    c: Coincident(g2,g1)
    c: Horizontal(g2)
    c: Coincident(g3,g2)
    c: Coincident(g3,g0)
    c: Vertical(g3)
    c: Horizontal(g4)
    c: Coincident(g5,g4)
    c: Coincident(g6,g5)
    c: Horizontal(g6)
    c: Coincident(g7,g6)
    c: Coincident(g7,g4)
    c: Vertical(g7)
    c: Coincident(g0,g-4)
    c: Coincident(g1,g-5)
    c: Coincident(g4,g-6)
    c: Coincident(g5,g-7)
    c: Distance(g0) = 2
    c: Distance(g4) = 2
FEATURE [Sketcher::SketchObject] Sketch066  label="piano per rampino"
  ArcFitTolerance = 1e-06
  AttachmentSupport = -> [XZ_Plane002]
  ExternalGeometry = -> [Sketch045]
  FullyConstrained = true
  MakeInternals = false
  MapMode = 5
  Placement = pos=(0,0,0) rot=(1,0,0;1.5708rad)
  sketch-geometry (4):
    g0: LineSegment StartX=5.4 StartY=5.1 StartZ=0 EndX=5.4 EndY=3.9 EndZ=0
    g1: LineSegment StartX=5.4 StartY=3.9 StartZ=0 EndX=7 EndY=3.9 EndZ=0
    g2: LineSegment StartX=7 StartY=3.9 StartZ=0 EndX=7 EndY=5.1 EndZ=0
    g3: LineSegment StartX=7 StartY=5.1 StartZ=0 EndX=5.4 EndY=5.1 EndZ=0
  constraints (11):
    c: Coincident(g0,g1)
    c: Coincident(g1,g2)
    c: Coincident(g2,g3)
    c: Coincident(g3,g0)
    c: Vertical(g0)
    c: Vertical(g2)
    c: Horizontal(g1)
    c: Horizontal(g3)
    c: Distance(g0,g2) = 1.6
    c: Distance(g1,g3) = 1.2
    c: Coincident(g2,g-3)
FEATURE [Sketcher::SketchObject] Sketch064  label="rampini_per_serraggio_struttura"
  ArcFitTolerance = 1e-06
  AttachmentSupport = -> [XZ_Plane002]
  ExternalGeometry = -> [Sketch066,Sketch045]
  FullyConstrained = true
  MakeInternals = false
  MapMode = 5
  Placement = pos=(0,0,0) rot=(1,0,0;1.5708rad)
  sketch-geometry (7):
    g0: LineSegment StartX=7 StartY=5.1 StartZ=0 EndX=7 EndY=3.9 EndZ=0
    g1: LineSegment StartX=7 StartY=3.9 StartZ=0 EndX=9 EndY=3.9 EndZ=0
    g2: LineSegment StartX=7 StartY=5.1 StartZ=0 EndX=7 EndY=5.1 EndZ=0
    g3: LineSegment StartX=7 StartY=5.1 StartZ=0 EndX=7 EndY=7.5 EndZ=0
    g4: LineSegment StartX=9 StartY=5.1 StartZ=0 EndX=9 EndY=3.9 EndZ=0
    g5: LineSegment StartX=7 StartY=7.5 StartZ=0 EndX=9 EndY=7.5 EndZ=0
    g6: LineSegment StartX=9 StartY=7.5 StartZ=0 EndX=9 EndY=5.1 EndZ=0
  constraints (20):
    c: Vertical(g0)
    c: Coincident(g1,g0)
    c: Horizontal(g1)
    c: Coincident(g2,g0)
    c: Horizontal(g2)
    c: Coincident(g3,g2)
    c: Vertical(g3)
    c: Coincident(g5,g3)
    c: Coincident(g4,g6)
    c: Coincident(g4,g1)
    c: Vertical(g4)
    c: Coincident(g0,g-3)
    c: DistanceY(g-4,g3) = 2.4
    c: DistanceX(g1,g1) = 2
    c: DistanceY(g2,g6) = 0
    c: DistanceX(g2,g2) = 0
    c: DistanceY(g0,g0) = 1.2
    c: Coincident(g5,g6)
    c: Horizontal(g5)
    c: Vertical(g6)
FEATURE [Sketcher::SketchObject] Sketch067  label="perno per blocco switch"
  ArcFitTolerance = 1e-06
  AttachmentSupport = -> [XZ_Plane]
  ExternalGeometry = -> [Sketch,Sketch010]
  FullyConstrained = true
  MakeInternals = false
  MapMode = 5
  Placement = pos=(0,0,0) rot=(1,0,0;1.5708rad)
  sketch-geometry (14):
    g0: LineSegment StartX=-191.073 StartY=24.9429 StartZ=0 EndX=-185.81 EndY=23.0276 EndZ=0
    g1: LineSegment StartX=-183.76 StartY=23.9839 StartZ=0 EndX=-182.392 EndY=27.7427 EndZ=0
    g2: LineSegment StartX=-183.348 StartY=29.7934 StartZ=0 EndX=-188.61 EndY=31.7087 EndZ=0
    g3: LineSegment StartX=-188.61 StartY=31.7087 StartZ=0 EndX=-191.073 EndY=24.9429 EndZ=0
    g4: GeomPoint [constr] X=-186.459 Y=27.0946 Z=0
    g5: LineSegment StartX=-189.022 StartY=25.8992 StartZ=0 EndX=-185.263 EndY=24.5311 EndZ=0
    g6: LineSegment StartX=-185.263 StartY=24.5311 StartZ=0 EndX=-183.895 EndY=28.2899 EndZ=0
    g7: LineSegment StartX=-183.895 StartY=28.2899 StartZ=0 EndX=-187.654 EndY=29.658 EndZ=0
    g8: LineSegment StartX=-187.654 StartY=29.658 StartZ=0 EndX=-189.022 EndY=25.8992 EndZ=0
    g9: GeomPoint [constr] X=-186.459 Y=27.0946 Z=0
    g10: ArcOfCircle CenterX=-185.263 CenterY=24.5311 CenterZ=0 NormalX=0 NormalY=0 NormalZ=1 AngleXU=0 Radius=1.6 StartAngle=4.36332 EndAngle=5.93412
    g11: GeomPoint [constr] X=-184.307 Y=22.4804 Z=0
    g12: ArcOfCircle CenterX=-183.895 CenterY=28.2899 CenterZ=0 NormalX=0 NormalY=0 NormalZ=1 AngleXU=0 Radius=1.6 StartAngle=5.93412 EndAngle=7.50492
    g13: GeomPoint [constr] X=-181.844 Y=29.2462 Z=0
  constraints (30):
    c: Coincident(g2,g3)
    c: Coincident(g3,g0)
    c: Symmetric(g13,g0,g4)
    c: Distance(g11,g3) = 7.2
    c: Distance(g0,g2) = 7.2
    c: Parallel(g3,g1)
    c: Parallel(g2,g0)
    c: Perpendicular(g2,g3)
    c: Coincident(g5,g6)
    c: Coincident(g6,g7)
    c: Coincident(g7,g8)
    c: Coincident(g8,g5)
    c: Symmetric(g7,g5,g9)
    c: Distance(g6,g8) = 4
    c: Distance(g5,g7) = 4
    c: Coincident(g9,g4)
    c: Parallel(g8,g6)
    c: Parallel(g7,g5)
    c: Perpendicular(g7,g8)
    c: Tangent(g8,g-3)
    c: Tangent(g2,g-4)
    c: PointOnObject(g11,g1)
    c: PointOnObject(g11,g0)
    c: Tangent(g1,g10) = -1.5708
    c: Tangent(g0,g10) = -1.5708
    c: PointOnObject(g13,g1)
    c: Tangent(g1,g12) = -1.5708
    c: Tangent(g2,g12) = -1.5708
    c: Equal(g10,g12)
    c: Coincident(g10,g5)
FEATURE [Part::Extrusion] Extrude072  label="Extrude perno per blocco switch"
  Base = -> Sketch067
  Dir = (0,-1,2e-16)
  DirMode = 2
  FaceMakerClass = Part::FaceMakerBullseye
  FaceMakerMode = 3
  LengthFwd = 25.2
  LengthRev = 0
  Solid = true
  Symmetric = true
FEATURE [Part::MultiFuse] Fusion
  Refine = true
  Shapes = -> [Extrude,Sweep,Extrude007,Extrude011,Extrude005,Extrude012,Extrude013,Extrude016,Extrude031,Extrude039,Extrude045,Extrude072]
FEATURE [Part::Cut] Cut
  Base = -> Fusion
  Refine = true
  Tool = -> Extrude001
FEATURE [Part::Cut] Cut001
  Base = -> Cut
  Refine = true
  Tool = -> Extrude004
FEATURE [Part::Cut] Cut002
  Base = -> Cut001
  Refine = true
  Tool = -> Extrude006
FEATURE [Part::Cut] Cut003
  Base = -> Cut002
  Refine = true
  Tool = -> Extrude008
FEATURE [Part::Cut] Cut004
  Base = -> Cut003
  Refine = true
  Tool = -> Extrude009
FEATURE [Part::Cut] Cut005
  Base = -> Cut004
  Refine = true
  Tool = -> Extrude010
FEATURE [Part::Cut] Cut006
  Base = -> Cut005
  Refine = true
  Tool = -> Extrude014
FEATURE [Part::Cut] Cut007
  Base = -> Cut006
  Refine = true
  Tool = -> Extrude015
FEATURE [Part::Cut] Cut008
  Base = -> Cut007
  Refine = true
  Tool = -> Extrude018
FEATURE [Part::Cut] Cut009
  Base = -> Cut008
  Refine = true
  Tool = -> Extrude019
FEATURE [Part::Cut] Cut010
  Base = -> Cut009
  Refine = true
  Tool = -> Extrude020
FEATURE [Part::Cut] Cut011
  Base = -> Cut010
  Refine = true
  Tool = -> Extrude021
FEATURE [Part::Cut] Cut012
  Base = -> Cut011
  Refine = true
  Tool = -> Extrude022
FEATURE [Part::Cut] Cut013
  Base = -> Cut012
  Refine = true
  Tool = -> Extrude023
FEATURE [Part::Cut] Cut014
  Base = -> Cut013
  Refine = true
  Tool = -> Extrude032
FEATURE [Part::Cut] Cut015
  Base = -> Cut014
  Refine = true
  Tool = -> Extrude033
FEATURE [Part::Cut] Cut016
  Base = -> Cut015
  Refine = true
  Tool = -> Extrude034
FEATURE [Part::Cut] Cut017
  Base = -> Cut016
  Refine = true
  Tool = -> Extrude035
FEATURE [Part::Cut] Cut018
  Base = -> Cut017
  Refine = true
  Tool = -> Extrude036
FEATURE [Part::Cut] Cut019
  Base = -> Cut018
  Refine = true
  Tool = -> Extrude037
FEATURE [Part::Cut] Cut020
  Base = -> Cut019
  Refine = true
  Tool = -> Extrude030
FEATURE [Part::Cut] Cut022
  Base = -> Cut020
  Refine = true
  Tool = -> Extrude038
FEATURE [Part::Cut] Cut023
  Base = -> Cut022
  Refine = true
  Tool = -> Extrude041
FEATURE [Part::Cut] Cut024
  Base = -> Cut023
  Refine = true
  Tool = -> Extrude040
FEATURE [Part::Cut] Cut025
  Base = -> Cut024
  Refine = true
  Tool = -> Extrude042
FEATURE [Part::Cut] Cut026
  Base = -> Cut025
  Refine = true
  Tool = -> Extrude043
FEATURE [Part::Cut] Cut027
  Base = -> Cut026
  Refine = true
  Tool = -> Extrude044
FEATURE [Part::Cut] Cut028
  Base = -> Cut027
  Refine = true
  Tool = -> Extrude046
FEATURE [Part::Cut] Cut029
  Base = -> Cut028
  Refine = true
  Tool = -> Extrude047
FEATURE [Part::Cut] Cut033
  Base = -> Cut029
  Refine = true
  Tool = -> Extrude055
FEATURE [Part::Cut] Cut034
  Base = -> Cut033
  Refine = true
  Tool = -> Extrude056
FEATURE [Part::Cut] Cut035
  Base = -> Cut034
  Refine = true
  Tool = -> Extrude057
FEATURE [Part::Cut] Cut037
  Base = -> Cut035
  Refine = true
  Tool = -> Extrude060
FEATURE [Part::Cut] Cut038
  Base = -> Cut037
  Refine = true
  Tool = -> Extrude061
FEATURE [Part::Cut] Cut039
  Base = -> Cut038
  Refine = true
  Tool = -> Extrude063
FEATURE [Part::Cut] Cut040
  Base = -> Cut039
  Refine = true
  Tool = -> Extrude064
FEATURE [Part::Cut] Cut041
  Base = -> Cut040
  Refine = true
  Tool = -> Extrude062
FEATURE [Sketcher::SketchObject] Sketch068  label="base con smusso sopra neopixel"
  ArcFitTolerance = 1e-06
  AttachmentSupport = -> [YZ_Plane002]
  FullyConstrained = true
  MakeInternals = false
  MapMode = 5
  Placement = pos=(0,0,0) rot=(0.57735,0.57735,0.57735;2.0944rad)
  sketch-geometry (5):
    g0: LineSegment StartX=-9.5 StartY=-6.1 StartZ=0 EndX=9.5 EndY=-6.1 EndZ=0
    g1: LineSegment StartX=9.5 StartY=-6.1 StartZ=0 EndX=9.5 EndY=6.1 EndZ=0
    g2: LineSegment StartX=9.5 StartY=6.1 StartZ=0 EndX=-9.5 EndY=6.1 EndZ=0
    g3: LineSegment StartX=-9.5 StartY=6.1 StartZ=0 EndX=-9.5 EndY=-6.1 EndZ=0
    g4: GeomPoint [constr] X=0 Y=0 Z=0
  constraints (12):
    c: Coincident(g0,g1)
    c: Coincident(g1,g2)
    c: Coincident(g2,g3)
    c: Coincident(g3,g0)
    c: Horizontal(g0)
    c: Horizontal(g2)
    c: Vertical(g1)
    c: Vertical(g3)
    c: Symmetric(g2,g0,g4)
    c: Distance(g1,g3) = 19
    c: Distance(g0,g2) = 12.2
    c: Coincident(g4,g-1)
FEATURE [Sketcher::SketchObject] Sketch069  label="cilindro minore"
  ArcFitTolerance = 1e-06
  AttachmentSupport = -> [XZ_Plane004]
  FullyConstrained = true
  MakeInternals = false
  MapMode = 5
  Placement = pos=(0,0,0) rot=(1,0,0;1.5708rad)
  sketch-geometry (1):
    g0: Circle CenterX=0 CenterY=0 CenterZ=0 NormalX=0 NormalY=0 NormalZ=1 AngleXU=0 Radius=5.8
  constraints (2):
    c: Diameter(g0) = 11.6
    c: Coincident(g0,g-1)
FEATURE [Sketcher::SketchObject] Sketch070  label="cilindro maggiore"
  ArcFitTolerance = 1e-06
  AttachmentSupport = -> [XZ_Plane004]
  ExternalGeometry = -> [Sketch069]
  FullyConstrained = true
  MakeInternals = false
  MapMode = 5
  Placement = pos=(0,0,0) rot=(1,0,0;1.5708rad)
  sketch-geometry (1):
    g0: Circle CenterX=0 CenterY=0 CenterZ=0 NormalX=0 NormalY=0 NormalZ=1 AngleXU=0 Radius=6.5
  constraints (2):
    c: Coincident(g0,g-1)
    c: Diameter(g0) = 13
FEATURE [Sketcher::SketchObject] Sketch071  label="buco interno"
  ArcFitTolerance = 1e-06
  AttachmentSupport = -> [XZ_Plane004]
  ExternalGeometry = -> [Sketch069]
  FullyConstrained = true
  MakeInternals = false
  MapMode = 5
  Placement = pos=(0,0,0) rot=(1,0,0;1.5708rad)
  sketch-geometry (1):
    g0: Circle CenterX=0 CenterY=0 CenterZ=0 NormalX=0 NormalY=0 NormalZ=1 AngleXU=0 Radius=5
  constraints (2):
    c: Coincident(g0,g-1)
    c: Diameter(g0) = 10
FEATURE [PartDesign::Pad] Pad
  Direction = (0,-1,2e-16)
  Length = 1.2
  Length2 = 10
  Placement = pos=(0,0,0) rot=(1,0,0;1.5708rad)
  Profile = -> Sketch070
  ReferenceAxis = -> Sketch070 [N_Axis]
  Refine = true
  Suppressed = false
  Type = 0
FEATURE [PartDesign::Pad] Pad001
  BaseFeature = -> Pad
  Direction = (0,-1,2e-16)
  Length = 5.6
  Length2 = 10
  Placement = pos=(0,0,0) rot=(1,0,0;1.5708rad)
  Profile = -> Sketch069
  ReferenceAxis = -> Sketch069 [N_Axis]
  Refine = true
  Suppressed = false
  Type = 0
FEATURE [PartDesign::Pocket] Pocket
  BaseFeature = -> Pad001
  Direction = (0,1,-2e-16)
  Length = 7
  Length2 = 5
  Midplane = true
  Placement = pos=(0,0,0) rot=(1,0,0;1.5708rad)
  Profile = -> Sketch071
  ReferenceAxis = -> Sketch071 [N_Axis]
  Refine = true
  Suppressed = false
  Type = 0
FEATURE [PartDesign::Fillet] Fillet
  Base = -> Pocket [Face7]
  BaseFeature = -> Pocket
  Placement = pos=(0,0,0) rot=(1,0,0;1.5708rad)
  Radius = 1
  Refine = true
  SupportTransform = false
  Suppressed = false
  UseAllEdges = false
FEATURE [PartDesign::Body] Body004  label="pulsanti lato sinistro"
  AllowCompound = false
  Group = -> [Sketch069,Sketch070,Sketch071,Pad,Pad001,Pocket,Fillet]
  Origin = -> Origin004
  Tip = -> Fillet
FEATURE [Sketcher::SketchObject] Sketch072  label="buco per saldature e diodo driver solenoide"
  ArcFitTolerance = 1e-06
  AttachmentSupport = -> [XZ_Plane]
  ExternalGeometry = -> [Sketch038]
  FullyConstrained = true
  MakeInternals = false
  MapMode = 5
  Placement = pos=(0,0,0) rot=(1,0,0;1.5708rad)
  sketch-geometry (4):
    g0: LineSegment StartX=-214.165 StartY=-46.5549 StartZ=0 EndX=-209.093 EndY=-35.6792 EndZ=0
    g1: LineSegment StartX=-209.093 StartY=-35.6792 StartZ=0 EndX=-209.456 EndY=-35.5101 EndZ=0
    g2: LineSegment StartX=-209.456 StartY=-35.5101 StartZ=0 EndX=-214.527 EndY=-46.3858 EndZ=0
    g3: LineSegment StartX=-214.527 StartY=-46.3858 StartZ=0 EndX=-214.165 EndY=-46.5549 EndZ=0
  constraints (11):
    c: Coincident(g1,g0)
    c: Coincident(g2,g1)
    c: Coincident(g3,g2)
    c: Coincident(g3,g0)
    c: Parallel(g-3,g0)
    c: Parallel(g0,g2)
    c: Perpendicular(g0,g3)
    c: Perpendicular(g1,g0)
    c: Distance(g3) = 0.4
    c: Distance(g2) = 12
    c: Coincident(g0,g-3)
FEATURE [Part::Extrusion] Extrude074  label="Extrude buco per saldature e diodo driver solenoide"
  Base = -> Sketch072
  Dir = (0,-1,2e-16)
  DirMode = 2
  FaceMakerClass = Part::FaceMakerBullseye
  FaceMakerMode = 3
  LengthFwd = 14.6
  LengthRev = 0
  Solid = true
  Symmetric = true
FEATURE [Part::Cut] Cut042
  Base = -> Cut041
  Refine = true
  Tool = -> Extrude074
FEATURE [Sketcher::SketchObject] Sketch073  label="fori slargati blocco solenoide"
  ArcFitTolerance = 1e-06
  AttachmentSupport = -> [XY_Plane]
  ExternalGeometry = -> [Sketch030]
  FullyConstrained = true
  MakeInternals = false
  MapMode = 5
  sketch-geometry (2):
    g0: Circle CenterX=-152.209 CenterY=6.95 CenterZ=0 NormalX=0 NormalY=0 NormalZ=1 AngleXU=0 Radius=3.7
    g1: Circle CenterX=-130.41 CenterY=-6.95 CenterZ=0 NormalX=0 NormalY=0 NormalZ=1 AngleXU=0 Radius=3.7
  constraints (4):
    c: Diameter(g0) = 7.4
    c: Coincident(g0,g-3)
    c: Diameter(g1) = 7.4
    c: Coincident(g1,g-4)
FEATURE [Part::Extrusion] Extrude075  label="Extrude fori slargati blocco solenoide"
  Base = -> Sketch073
  Dir = (0,0,1)
  DirMode = 2
  FaceMakerClass = Part::FaceMakerBullseye
  FaceMakerMode = 3
  LengthFwd = 1.5
  LengthRev = 0
  Placement = pos=(0,0,36.4) rot=(0,0,1;0rad)
  Solid = true
  Symmetric = false
FEATURE [Part::Cut] Cut043
  Base = -> Cut042
  Refine = true
  Tool = -> Extrude075
FEATURE [Sketcher::SketchObject] Sketch074  label="lato sx pistola"
  ArcFitTolerance = 1e-06
  AttachmentSupport = -> [XZ_Plane]
  ExternalGeometry = -> [Sketch016,Sketch,Sketch058]
  FullyConstrained = true
  MakeInternals = false
  MapMode = 5
  Placement = pos=(0,0,0) rot=(1,0,0;1.5708rad)
  sketch-geometry (37):
    g0: LineSegment StartX=-82.8 StartY=3.2 StartZ=0 EndX=0 EndY=3.2 EndZ=0
    g1: LineSegment StartX=-82.8 StartY=3.2 StartZ=0 EndX=-82.8 EndY=6.2 EndZ=0
    g2: LineSegment [constr] StartX=-107.6 StartY=18 StartZ=0 EndX=-107.6 EndY=20 EndZ=0
    g3: LineSegment [constr] StartX=-132.428 StartY=18 StartZ=0 EndX=-132.428 EndY=20 EndZ=0
    g4: LineSegment StartX=-132.428 StartY=20 StartZ=0 EndX=-107.6 EndY=20 EndZ=0
    g5: ArcOfCircle CenterX=-107.6 CenterY=4 CenterZ=0 NormalX=0 NormalY=0 NormalZ=1 AngleXU=0 Radius=16 StartAngle=0.137937 EndAngle=1.5708
    g6: LineSegment StartX=-82.8 StartY=6.2 StartZ=0 EndX=-91.752 EndY=6.2 EndZ=0
    g7: LineSegment [constr] StartX=-145.743 StartY=8.32624 StartZ=0 EndX=-147.645 EndY=8.94427 EndZ=0
    g8: ArcOfCircle CenterX=-132.428 CenterY=4 CenterZ=0 NormalX=0 NormalY=0 NormalZ=1 AngleXU=0 Radius=16 StartAngle=1.5708 EndAngle=2.82743
    g9: LineSegment StartX=-215.932 StartY=-80.4316 StartZ=0 EndX=-176.685 EndY=-80.4316 EndZ=0
    g10: LineSegment StartX=-147.645 StartY=8.94427 StartZ=0 EndX=-176.685 EndY=-80.4316 EndZ=0
    g11: LineSegment [constr] StartX=-193.988 StartY=-2.33927 StartZ=0 EndX=-192.176 EndY=-3.18451 EndZ=0
    g12: LineSegment [constr] StartX=-217.232 StartY=-52.1862 StartZ=0 EndX=-215.42 EndY=-53.0314 EndZ=0
    g13: LineSegment StartX=-192.176 StartY=-3.18451 StartZ=0 EndX=-215.42 EndY=-53.0314 EndZ=0
    g14: ArcOfCircle CenterX=-184.801 CenterY=-67.3089 CenterZ=0 NormalX=0 NormalY=0 NormalZ=1 AngleXU=0 Radius=33.7833 StartAngle=2.70526 EndAngle=3.54053
    g15: ArcOfCircle CenterX=-207.583 CenterY=4 CenterZ=0 NormalX=0 NormalY=0 NormalZ=1 AngleXU=0 Radius=17 StartAngle=5.84685 EndAngle=7.56663
    g16: LineSegment StartX=-202.765 StartY=20.303 StartZ=0 EndX=-195.887 EndY=39.2 EndZ=0
    g17: LineSegment [constr] StartX=-193.885 StartY=33.0037 StartZ=0 EndX=-197.644 EndY=34.3718 EndZ=0
    g18: LineSegment StartX=-195.887 StartY=39.2 StartZ=0 EndX=0 EndY=39.2 EndZ=0
    g19: LineSegment StartX=0 StartY=3.2 StartZ=0 EndX=0 EndY=39.2 EndZ=0
    g20: LineSegment StartX=-189.939 StartY=31.5672 StartZ=0 EndX=-192.333 EndY=24.9893 EndZ=0
    g21: LineSegment StartX=-196.467 StartY=26.4942 StartZ=0 EndX=-194.073 EndY=33.0721 EndZ=0
    g22: Circle CenterX=-213.443 CenterY=-76.8316 CenterZ=0 NormalX=0 NormalY=0 NormalZ=1 AngleXU=0 Radius=1.8
    g23: Circle CenterX=-179.305 CenterY=-76.8316 CenterZ=0 NormalX=0 NormalY=0 NormalZ=1 AngleXU=0 Radius=1.8
    g24: Circle CenterX=-184.08 CenterY=34.8 CenterZ=0 NormalX=0 NormalY=0 NormalZ=1 AngleXU=0 Radius=1.8
    g25: Circle CenterX=-78.51 CenterY=34.8 CenterZ=0 NormalX=0 NormalY=0 NormalZ=1 AngleXU=0 Radius=1.8
    g26: Circle CenterX=-78.51 CenterY=7.6 CenterZ=0 NormalX=0 NormalY=0 NormalZ=1 AngleXU=0 Radius=1.8
    g27: Circle CenterX=-5.6 CenterY=34.8 CenterZ=0 NormalX=0 NormalY=0 NormalZ=1 AngleXU=0 Radius=1.8
    g28: Circle CenterX=-5.6 CenterY=7.6 CenterZ=0 NormalX=0 NormalY=0 NormalZ=1 AngleXU=0 Radius=1.8
    g29: LineSegment StartX=-190.127 StartY=31.6356 StartZ=0 EndX=-189.939 EndY=31.5672 EndZ=0
    g30: LineSegment StartX=-194.073 StartY=33.0721 StartZ=0 EndX=-193.885 EndY=33.0037 EndZ=0
    g31: LineSegment StartX=-193.885 StartY=33.0037 StartZ=0 EndX=-190.127 EndY=31.6356 EndZ=0
    g32: LineSegment StartX=-196.467 StartY=26.4942 StartZ=0 EndX=-192.333 EndY=24.9893 EndZ=0
    g33: Circle CenterX=-19 CenterY=21.2 CenterZ=0 NormalX=0 NormalY=0 NormalZ=1 AngleXU=0 Radius=6.3
    g34: Circle CenterX=-42 CenterY=21.2 CenterZ=0 NormalX=0 NormalY=0 NormalZ=1 AngleXU=0 Radius=6.3
    g35: Circle CenterX=-65 CenterY=21.2 CenterZ=0 NormalX=0 NormalY=0 NormalZ=1 AngleXU=0 Radius=6.3
    g36: LineSegment [constr] StartX=-4 StartY=21.2 StartZ=0 EndX=-65 EndY=21.2 EndZ=0
  constraints (96):
    c: Coincident(g0,g-41)
    c: Horizontal(g0)
    c: PointOnObject(g0,g-39)
    c: Coincident(g1,g0)
    c: Vertical(g1)
    c: DistanceY(g1,g1) = 3
    c: Coincident(g2,g-17)
    c: Vertical(g2)
    c: Coincident(g3,g-16)
    c: Vertical(g3)
    c: DistanceY(g2,g2) = 2
    c: DistanceY(g3,g3) = 2
    c: Coincident(g4,g3)
    c: Coincident(g4,g2)
    c: Coincident(g5,g-17)
    c: Coincident(g5,g2)
    c: Coincident(g6,g1)
    c: Horizontal(g6)
    c: Coincident(g6,g5)
    c: Coincident(g7,g-15)
    c: Coincident(g8,g7)
    c: Coincident(g8,g3)
    c: Coincident(g8,g-15)
    c: Horizontal(g9)
    c: DistanceY(g-13,g9) = 2
    c: Coincident(g10,g7)
    c: Parallel(g10,g-14)
    c: Coincident(g9,g10)
    c: Distance(g11) = 2
    c: Coincident(g11,g-11)
    c: Perpendicular(g-11,g11)
    c: Distance(g12) = 2
    c: Coincident(g12,g-12)
    c: Perpendicular(g-11,g12)
    c: Coincident(g13,g11)
    c: Coincident(g13,g12)
    c: Coincident(g14,g-32)
    c: Coincident(g14,g12)
    c: Coincident(g14,g9)
    c: Coincident(g15,g-10)
    c: Coincident(g15,g11)
    c: Parallel(g16,g-22)
    c: Distance(g17) = 4
    c: PointOnObject(g17,g16)
    c: Coincident(g15,g16)
    c: Horizontal(g18)
    c: Coincident(g18,g16)
    c: Coincident(g19,g0)
    c: PointOnObject(g19,g-39)
    c: DistanceY(g19,g-36) = 2
    c: Coincident(g18,g19)
    c: Diameter(g22) = 3.6
    c: Coincident(g22,g-9)
    c: Diameter(g23) = 3.6
    c: Coincident(g23,g-8)
    c: Diameter(g24) = 3.6
    c: Diameter(g25) = 3.6
    c: Diameter(g26) = 3.6
    c: Diameter(g27) = 3.6
    c: Diameter(g28) = 3.6
    c: Coincident(g27,g-4)
    c: Coincident(g28,g-3)
    c: Coincident(g25,g-6)
    c: Coincident(g26,g-5)
    c: Coincident(g24,g-7)
    c: Parallel(g20,g-21)
    c: Equal(g20,g-21)
    c: Parallel(g21,g-19)
    c: Equal(g21,g-19)
    c: Distance(g29) = 0.2
    c: Distance(g30) = 0.2
    c: Parallel(g29,g-20)
    c: Parallel(g31,g-20)
    c: Equal(g31,g-20)
    c: Coincident(g30,g31)
    c: Coincident(g31,g29)
    c: Coincident(g29,g-21)
    c: Parallel(g30,g31)
    c: Coincident(g17,g30)
    c: Coincident(g20,g29)
    c: Coincident(g21,g30)
    c: Perpendicular(g16,g17)
    c: Coincident(g32,g21)
    c: Coincident(g32,g20)
    c: Perpendicular(g10,g7)
    c: Diameter(g33) = 12.6
    c: Diameter(g34) = 12.6
    c: Diameter(g35) = 12.6
    c: Horizontal(g36)
    c: PointOnObject(g33,g36)
    c: PointOnObject(g34,g36)
    c: DistanceX(g34,g33) = 23
    c: DistanceX(g35,g34) = 23
    c: DistanceX(g33,g36) = 15
    c: Symmetric(g-24,g-24,g36)
    c: Coincident(g36,g35)
FEATURE [Sketcher::SketchObject] Sketch075  label="lato dx pistola"
  ArcFitTolerance = 1e-06
  AttachmentSupport = -> [XZ_Plane]
  ExternalGeometry = -> [Sketch016,Sketch,Sketch058,Sketch074]
  FullyConstrained = true
  MakeInternals = false
  MapMode = 5
  Placement = pos=(0,0,0) rot=(1,0,0;1.5708rad)
  sketch-geometry (61):
    g0: LineSegment StartX=-82.8 StartY=3.2 StartZ=0 EndX=0 EndY=3.2 EndZ=0
    g1: LineSegment StartX=-82.8 StartY=3.2 StartZ=0 EndX=-82.8 EndY=6.2 EndZ=0
    g2: LineSegment [constr] StartX=-107.6 StartY=18 StartZ=0 EndX=-107.6 EndY=20 EndZ=0
    g3: LineSegment [constr] StartX=-132.428 StartY=18 StartZ=0 EndX=-132.428 EndY=20 EndZ=0
    g4: LineSegment StartX=-132.428 StartY=20 StartZ=0 EndX=-107.6 EndY=20 EndZ=0
    g5: ArcOfCircle CenterX=-107.6 CenterY=4 CenterZ=0 NormalX=0 NormalY=0 NormalZ=1 AngleXU=0 Radius=16 StartAngle=0.137937 EndAngle=1.5708
    g6: LineSegment StartX=-82.8 StartY=6.2 StartZ=0 EndX=-91.752 EndY=6.2 EndZ=0
    g7: LineSegment [constr] StartX=-145.743 StartY=8.32624 StartZ=0 EndX=-147.645 EndY=8.94427 EndZ=0
    g8: ArcOfCircle CenterX=-132.428 CenterY=4 CenterZ=0 NormalX=0 NormalY=0 NormalZ=1 AngleXU=0 Radius=16 StartAngle=1.5708 EndAngle=2.82743
    g9: LineSegment StartX=-215.932 StartY=-80.4316 StartZ=0 EndX=-176.685 EndY=-80.4316 EndZ=0
    g10: LineSegment StartX=-147.645 StartY=8.94427 StartZ=0 EndX=-176.685 EndY=-80.4316 EndZ=0
    g11: LineSegment [constr] StartX=-193.988 StartY=-2.33927 StartZ=0 EndX=-192.176 EndY=-3.18451 EndZ=0
    g12: LineSegment [constr] StartX=-217.232 StartY=-52.1862 StartZ=0 EndX=-215.42 EndY=-53.0314 EndZ=0
    g13: LineSegment StartX=-192.176 StartY=-3.18451 StartZ=0 EndX=-215.42 EndY=-53.0314 EndZ=0
    g14: ArcOfCircle CenterX=-184.801 CenterY=-67.3089 CenterZ=0 NormalX=0 NormalY=0 NormalZ=1 AngleXU=0 Radius=33.7833 StartAngle=2.70526 EndAngle=3.54053
    g15: ArcOfCircle CenterX=-207.583 CenterY=4 CenterZ=0 NormalX=0 NormalY=0 NormalZ=1 AngleXU=0 Radius=17 StartAngle=5.84685 EndAngle=7.56663
    g16: LineSegment StartX=-202.765 StartY=20.303 StartZ=0 EndX=-195.887 EndY=39.2 EndZ=0
    g17: LineSegment [constr] StartX=-193.885 StartY=33.0037 StartZ=0 EndX=-197.644 EndY=34.3718 EndZ=0
    g18: LineSegment StartX=-195.887 StartY=39.2 StartZ=0 EndX=0 EndY=39.2 EndZ=0
    g19: LineSegment StartX=0 StartY=3.2 StartZ=0 EndX=0 EndY=39.2 EndZ=0
    g20: LineSegment StartX=-189.939 StartY=31.5672 StartZ=0 EndX=-192.333 EndY=24.9893 EndZ=0
    g21: LineSegment StartX=-196.467 StartY=26.4942 StartZ=0 EndX=-194.073 EndY=33.0721 EndZ=0
    g22: Circle CenterX=-213.443 CenterY=-76.8316 CenterZ=0 NormalX=0 NormalY=0 NormalZ=1 AngleXU=0 Radius=1.8
    g23: Circle CenterX=-179.305 CenterY=-76.8316 CenterZ=0 NormalX=0 NormalY=0 NormalZ=1 AngleXU=0 Radius=1.8
    g24: Circle CenterX=-184.08 CenterY=34.8 CenterZ=0 NormalX=0 NormalY=0 NormalZ=1 AngleXU=0 Radius=1.8
    g25: Circle CenterX=-78.51 CenterY=34.8 CenterZ=0 NormalX=0 NormalY=0 NormalZ=1 AngleXU=0 Radius=1.8
    g26: Circle CenterX=-78.51 CenterY=7.6 CenterZ=0 NormalX=0 NormalY=0 NormalZ=1 AngleXU=0 Radius=1.8
    g27: Circle CenterX=-5.6 CenterY=34.8 CenterZ=0 NormalX=0 NormalY=0 NormalZ=1 AngleXU=0 Radius=1.8
    g28: Circle CenterX=-5.6 CenterY=7.6 CenterZ=0 NormalX=0 NormalY=0 NormalZ=1 AngleXU=0 Radius=1.8
    g29: LineSegment StartX=-190.127 StartY=31.6356 StartZ=0 EndX=-189.939 EndY=31.5672 EndZ=0
    g30: LineSegment StartX=-194.073 StartY=33.0721 StartZ=0 EndX=-193.885 EndY=33.0037 EndZ=0
    g31: LineSegment StartX=-193.885 StartY=33.0037 StartZ=0 EndX=-190.127 EndY=31.6356 EndZ=0
    g32: LineSegment StartX=-196.467 StartY=26.4942 StartZ=0 EndX=-192.333 EndY=24.9893 EndZ=0
    g33: LineSegment [constr] StartX=-4 StartY=21.2 StartZ=0 EndX=-87.91 EndY=21.2 EndZ=0
    g34: GeomPoint [constr] X=-4 Y=21.2 Z=0
    g35: LineSegment [constr] StartX=-15.2 StartY=33.7 StartZ=0 EndX=-15.2 EndY=8.7 EndZ=0
    g36: LineSegment [constr] StartX=-15.2 StartY=33.7 StartZ=0 EndX=-56.2 EndY=33.7 EndZ=0
    g37: LineSegment [constr] StartX=-15.2 StartY=8.7 StartZ=0 EndX=-56.2 EndY=8.7 EndZ=0
    g38: LineSegment [constr] StartX=-56.2 StartY=33.7 StartZ=0 EndX=-56.2 EndY=8.7 EndZ=0
    g39: Circle CenterX=-18.6 CenterY=30.3 CenterZ=0 NormalX=0 NormalY=0 NormalZ=1 AngleXU=0 Radius=3.4
    g40: Circle CenterX=-18.6 CenterY=12.1 CenterZ=0 NormalX=0 NormalY=0 NormalZ=1 AngleXU=0 Radius=3.4
    g41: Circle CenterX=-43.2 CenterY=30.3 CenterZ=0 NormalX=0 NormalY=0 NormalZ=1 AngleXU=0 Radius=3.4
    g42: Circle CenterX=-43.2 CenterY=12.1 CenterZ=0 NormalX=0 NormalY=0 NormalZ=1 AngleXU=0 Radius=3.4
    g43: LineSegment [constr] StartX=-4 StartY=21.2 StartZ=0 EndX=-15.2 EndY=21.2 EndZ=0
    g44: LineSegment [constr] StartX=-15.2 StartY=21.2 StartZ=0 EndX=-36.2 EndY=21.2 EndZ=0
    g45: LineSegment [constr] StartX=-41.5 StartY=16.2 StartZ=0 EndX=-30.9 EndY=16.2 EndZ=0
    g46: LineSegment [constr] StartX=-30.9 StartY=16.2 StartZ=0 EndX=-30.9 EndY=26.2 EndZ=0
    g47: LineSegment [constr] StartX=-30.9 StartY=26.2 StartZ=0 EndX=-41.5 EndY=26.2 EndZ=0
    g48: LineSegment [constr] StartX=-41.5 StartY=26.2 StartZ=0 EndX=-41.5 EndY=16.2 EndZ=0
    g49: GeomPoint [constr] X=-36.2 Y=21.2 Z=0
    g50: Circle CenterX=-36.2 CenterY=21.2 CenterZ=0 NormalX=0 NormalY=0 NormalZ=1 AngleXU=0 Radius=2.8
    g51: LineSegment [constr] StartX=-24.2 StartY=26.7 StartZ=0 EndX=-24.2 EndY=15.7 EndZ=0
    g52: Circle CenterX=-24.2 CenterY=26.7 CenterZ=0 NormalX=0 NormalY=0 NormalZ=1 AngleXU=0 Radius=3
    g53: Circle CenterX=-24.2 CenterY=15.7 CenterZ=0 NormalX=0 NormalY=0 NormalZ=1 AngleXU=0 Radius=3
    g54: GeomPoint X=-18.6 Y=30.3 Z=0
    g55: GeomPoint X=-18.6 Y=12.1 Z=0
    g56: GeomPoint X=-43.2 Y=12.1 Z=0
    g57: GeomPoint X=-43.2 Y=30.3 Z=0
    g58: Circle CenterX=-65 CenterY=21.2 CenterZ=0 NormalX=0 NormalY=0 NormalZ=1 AngleXU=0 Radius=1.5
    g59: Circle CenterX=-42 CenterY=21.2 CenterZ=0 NormalX=0 NormalY=0 NormalZ=1 AngleXU=0 Radius=1.5
    g60: Circle CenterX=-19 CenterY=21.2 CenterZ=0 NormalX=0 NormalY=0 NormalZ=1 AngleXU=0 Radius=1.5
  constraints (149):
    c: Coincident(g0,g-41)
    c: Horizontal(g0)
    c: PointOnObject(g0,g-39)
    c: Coincident(g1,g0)
    c: Vertical(g1)
    c: DistanceY(g1,g1) = 3
    c: Coincident(g2,g-17)
    c: Vertical(g2)
    c: Coincident(g3,g-16)
    c: Vertical(g3)
    c: DistanceY(g2,g2) = 2
    c: DistanceY(g3,g3) = 2
    c: Coincident(g4,g3)
    c: Coincident(g4,g2)
    c: Coincident(g5,g-17)
    c: Coincident(g5,g2)
    c: Coincident(g6,g1)
    c: Horizontal(g6)
    c: Coincident(g6,g5)
    c: Coincident(g7,g-15)
    c: Coincident(g8,g7)
    c: Coincident(g8,g3)
    c: Coincident(g8,g-15)
    c: Horizontal(g9)
    c: DistanceY(g-13,g9) = 2
    c: Coincident(g10,g7)
    c: Parallel(g10,g-14)
    c: Coincident(g9,g10)
    c: Distance(g11) = 2
    c: Coincident(g11,g-11)
    c: Perpendicular(g-11,g11)
    c: Distance(g12) = 2
    c: Coincident(g12,g-12)
    c: Perpendicular(g-11,g12)
    c: Coincident(g13,g11)
    c: Coincident(g13,g12)
    c: Coincident(g14,g-32)
    c: Coincident(g14,g12)
    c: Coincident(g14,g9)
    c: Coincident(g15,g-10)
    c: Coincident(g15,g11)
    c: Parallel(g16,g-22)
    c: Distance(g17) = 4
    c: PointOnObject(g17,g16)
    c: Coincident(g15,g16)
    c: Horizontal(g18)
    c: Coincident(g18,g16)
    c: Coincident(g19,g0)
    c: PointOnObject(g19,g-39)
    c: DistanceY(g19,g-36) = 2
    c: Coincident(g18,g19)
    c: Diameter(g22) = 3.6
    c: Coincident(g22,g-9)
    c: Diameter(g23) = 3.6
    c: Coincident(g23,g-8)
    c: Diameter(g24) = 3.6
    c: Diameter(g25) = 3.6
    c: Diameter(g26) = 3.6
    c: Diameter(g27) = 3.6
    c: Diameter(g28) = 3.6
    c: Coincident(g27,g-4)
    c: Coincident(g28,g-3)
    c: Coincident(g25,g-6)
    c: Coincident(g26,g-5)
    c: Coincident(g24,g-7)
    c: Parallel(g20,g-21)
    c: Equal(g20,g-21)
    c: Parallel(g21,g-19)
    c: Equal(g21,g-19)
    c: Distance(g29) = 0.2
    c: Distance(g30) = 0.2
    c: Parallel(g29,g-20)
    c: Parallel(g31,g-20)
    c: Equal(g31,g-20)
    c: Coincident(g30,g31)
    c: Coincident(g31,g29)
    c: Coincident(g29,g-21)
    c: Parallel(g30,g31)
    c: Coincident(g17,g30)
    c: Coincident(g20,g29)
    c: Coincident(g21,g30)
    c: Perpendicular(g16,g17)
    c: Coincident(g32,g21)
    c: Coincident(g32,g20)
    c: Perpendicular(g10,g7)
    c: Horizontal(g33)
    c: Symmetric(g-24,g-24,g33)
    c: PointOnObject(g33,g-28)
    c: Symmetric(g-24,g-24,g34)
    c: DistanceY(g35,g35) = 25
    c: Symmetric(g35,g35,g33)
    c: Distance(g36) = 41
    c: Coincident(g36,g35)
    c: Horizontal(g36)
    c: Coincident(g37,g35)
    c: Horizontal(g37)
    c: Coincident(g38,g36)
    c: Vertical(g38)
    c: Coincident(g37,g38)
    c: Diameter(g39) = 6.8
    c: Diameter(g40) = 6.8
    c: Tangent(g39,g36)
    c: Tangent(g40,g37)
    c: Tangent(g39,g35)
    c: Tangent(g40,g35)
    c: Diameter(g41) = 6.8
    c: Diameter(g42) = 6.8
    c: Tangent(g41,g36)
    c: Tangent(g42,g37)
    c: DistanceX(g41,g39) = 24.6
    c: DistanceX(g42,g40) = 24.6
    c: Distance(g43) = 11.2
    c: Coincident(g43,g33)
    c: PointOnObject(g43,g33)
    c: PointOnObject(g43,g35)
    c: Distance(g44) = 21
    c: Coincident(g44,g43)
    c: PointOnObject(g44,g33)
    c: Coincident(g45,g46)
    c: Coincident(g46,g47)
    c: Coincident(g47,g48)
    c: Coincident(g48,g45)
    c: Horizontal(g45)
    c: Horizontal(g47)
    c: Vertical(g46)
    c: Vertical(g48)
    c: Symmetric(g47,g45,g49)
    c: Distance(g46,g48) = 10.6
    c: Distance(g45,g47) = 10
    c: Coincident(g49,g44)
    c: Diameter(g50) = 5.6
    c: Coincident(g50,g44)
    c: Distance(g51) = 11
    c: Symmetric(g51,g51,g33)
    c: DistanceX(g51,g43) = 9
    c: Diameter(g52) = 6
    c: Coincident(g52,g51)
    c: Diameter(g53) = 6
    c: Coincident(g53,g51)
    c: Coincident(g40,g55)
    c: Coincident(g39,g54)
    c: Coincident(g41,g57)
    c: Coincident(g42,g56)
    c: Diameter(g58) = 3
    c: Diameter(g59) = 3
    c: Diameter(g60) = 3
    c: Coincident(g58,g-44)
    c: Coincident(g59,g-46)
    c: Coincident(g60,g-45)
FEATURE [Sketcher::SketchObject] Sketch078
  ArcFitTolerance = 1e-06
  AttachmentSupport = -> [XZ_Plane005]
  FullyConstrained = true
  MakeInternals = false
  MapMode = 5
  Placement = pos=(0,0,0) rot=(1,0,0;1.5708rad)
  sketch-geometry (5):
    g0: LineSegment [constr] StartX=0 StartY=5.5 StartZ=0 EndX=0 EndY=-5.5 EndZ=0
    g1: ArcOfCircle CenterX=0 CenterY=5.5 CenterZ=0 NormalX=0 NormalY=0 NormalZ=1 AngleXU=0 Radius=2.7 StartAngle=0 EndAngle=3.14159
    g2: ArcOfCircle CenterX=0 CenterY=-5.5 CenterZ=0 NormalX=0 NormalY=0 NormalZ=1 AngleXU=0 Radius=2.7 StartAngle=3.1416 EndAngle=6.28318
    g3: LineSegment StartX=-2.7 StartY=5.5 StartZ=0 EndX=-2.7 EndY=-5.50001 EndZ=0
    g4: LineSegment StartX=2.7 StartY=5.5 StartZ=0 EndX=2.7 EndY=-5.50001 EndZ=0
  constraints (13):
    c: Distance(g0) = 11
    c: Vertical(g0)
    c: Symmetric(g0,g0,g-1)
    c: Radius(g1) = 2.7
    c: Coincident(g1,g0)
    c: Radius(g2) = 2.7
    c: Coincident(g2,g0)
    c: Vertical(g3)
    c: Vertical(g4)
    c: Coincident(g2,g4)
    c: Coincident(g2,g3)
    c: Tangent(g3,g1) = -1.5708
    c: Tangent(g4,g1) = 1.5708
FEATURE [PartDesign::Pad] Pad002
  Direction = (0,-1,2e-16)
  Length = 0.8
  Length2 = 10
  Placement = pos=(0,0,0) rot=(1,0,0;1.5708rad)
  Profile = -> Sketch078
  ReferenceAxis = -> Sketch078 [N_Axis]
  Refine = true
  Suppressed = false
  Type = 0
FEATURE [Sketcher::SketchObject] Sketch079
  ArcFitTolerance = 1e-06
  AttachmentSupport = -> [XZ_Plane005]
  ExternalGeometry = -> [Sketch078]
  FullyConstrained = true
  MakeInternals = false
  MapMode = 5
  Placement = pos=(0,0,0) rot=(1,0,0;1.5708rad)
  sketch-geometry (2):
    g0: Circle CenterX=-1e-16 CenterY=5.5 CenterZ=0 NormalX=0 NormalY=0 NormalZ=1 AngleXU=0 Radius=2.7
    g1: Circle CenterX=0 CenterY=-5.5 CenterZ=0 NormalX=0 NormalY=0 NormalZ=1 AngleXU=0 Radius=2.7
  constraints (4):
    c: Coincident(g0,g-3)
    c: PointOnObject(g-3,g0)
    c: Coincident(g1,g-4)
    c: Equal(g1,g-4)
FEATURE [PartDesign::Pad] Pad003
  BaseFeature = -> Pad002
  Direction = (0,-1,2e-16)
  Length = 5
  Length2 = 10
  Placement = pos=(0,0,0) rot=(1,0,0;1.5708rad)
  Profile = -> Sketch079
  ReferenceAxis = -> Sketch079 [N_Axis]
  Refine = true
  Suppressed = false
  Type = 0
FEATURE [PartDesign::Fillet] Fillet001
  Base = -> Pad003 [Edge16,Edge14]
  BaseFeature = -> Pad003
  Placement = pos=(0,0,0) rot=(1,0,0;1.5708rad)
  Radius = 0.4
  Refine = true
  SupportTransform = false
  Suppressed = false
  UseAllEdges = false
FEATURE [PartDesign::Body] Body005  label="pulsanti lato destro"
  AllowCompound = false
  Group = -> [Sketch078,Pad002,Sketch079,Pad003,Fillet001]
  Origin = -> Origin005
  Tip = -> Fillet001
FEATURE [PartDesign::SubShapeBinder] Binder
  BindCopyOnChange = 0
  BindMode = 0
  ClaimChildren = false
  Context = -> Body006 [Binder.]
  Fuse = false
  MakeFace = true
  OffsetFill = false
  OffsetIntersection = false
  OffsetJoinType = 0
  OffsetOpenResult = false
  PartialLoad = false
  Refine = true
  Relative = true
  Support = -> [Body[Sketch074.]]
  _Version = 2
FEATURE [PartDesign::SubShapeBinder] Binder001
  BindCopyOnChange = 0
  BindMode = 0
  ClaimChildren = false
  Context = -> Body007 [Binder001.]
  Fuse = false
  MakeFace = true
  OffsetFill = false
  OffsetIntersection = false
  OffsetJoinType = 0
  OffsetOpenResult = false
  PartialLoad = false
  Refine = true
  Relative = true
  Support = -> [Body[Sketch075.]]
  _Version = 2
FEATURE [Mesh::Feature] logo_per_PCB_definitivo_positivo
  Placement = pos=(-191,17,-66) rot=(0,1,1;0rad)
FEATURE [Sketcher::SketchObject] Sketch114  label="Sketch114 - base lato DX"
  ArcFitTolerance = 1e-06
  AttachmentSupport = -> [Binder001]
  ExternalGeometry = -> [Binder001]
  FullyConstrained = true
  MakeInternals = false
  MapMode = 5
  Placement = pos=(0,1e-15,0) rot=(0,0.707107,0.707107;3.14159rad)
  sketch-geometry (30):
    g0: Circle CenterX=5.6 CenterY=34.8 CenterZ=0 NormalX=0 NormalY=0 NormalZ=1 AngleXU=0 Radius=1.8
    g1: Circle CenterX=5.6 CenterY=7.6 CenterZ=0 NormalX=0 NormalY=0 NormalZ=1 AngleXU=0 Radius=1.8
    g2: Circle CenterX=24.2 CenterY=26.7 CenterZ=0 NormalX=0 NormalY=0 NormalZ=1 AngleXU=0 Radius=3
    g3: Circle CenterX=24.2 CenterY=15.7 CenterZ=0 NormalX=0 NormalY=0 NormalZ=1 AngleXU=0 Radius=3
    g4: Circle CenterX=36.2 CenterY=21.2 CenterZ=0 NormalX=0 NormalY=0 NormalZ=1 AngleXU=0 Radius=2.8
    g5: Circle CenterX=78.51 CenterY=34.8 CenterZ=0 NormalX=0 NormalY=0 NormalZ=1 AngleXU=0 Radius=1.8
    g6: Circle CenterX=78.51 CenterY=7.6 CenterZ=0 NormalX=0 NormalY=0 NormalZ=1 AngleXU=0 Radius=1.8
    g7: Circle CenterX=184.08 CenterY=34.8 CenterZ=0 NormalX=0 NormalY=0 NormalZ=1 AngleXU=0 Radius=1.8
    g8: Circle CenterX=213.443 CenterY=-76.8316 CenterZ=0 NormalX=0 NormalY=0 NormalZ=1 AngleXU=0 Radius=1.8
    g9: Circle CenterX=179.305 CenterY=-76.8316 CenterZ=0 NormalX=0 NormalY=0 NormalZ=1 AngleXU=0 Radius=1.8
    g10: ArcOfCircle [constr] CenterX=132.428 CenterY=4 CenterZ=0 NormalX=0 NormalY=0 NormalZ=1 AngleXU=0 Radius=16 StartAngle=0.314159 EndAngle=1.5708
    g11: ArcOfCircle CenterX=107.6 CenterY=4 CenterZ=0 NormalX=0 NormalY=0 NormalZ=1 AngleXU=0 Radius=16 StartAngle=1.5708 EndAngle=3.00366
    g12: ArcOfCircle CenterX=207.583 CenterY=4 CenterZ=0 NormalX=0 NormalY=0 NormalZ=1 AngleXU=0 Radius=17 StartAngle=1.85815 EndAngle=3.57792
    g13: ArcOfCircle CenterX=184.801 CenterY=-67.3089 CenterZ=0 NormalX=0 NormalY=0 NormalZ=1 AngleXU=0 Radius=33.7833 StartAngle=5.88425 EndAngle=6.71952
    g14: LineSegment StartX=0 StartY=39.2 StartZ=0 EndX=0 EndY=3.2 EndZ=0
    g15: LineSegment StartX=0 StartY=3.2 StartZ=0 EndX=82.8 EndY=3.2 EndZ=0
    g16: LineSegment StartX=82.8 StartY=3.2 StartZ=0 EndX=82.8 EndY=6.2 EndZ=0
    g17: LineSegment StartX=82.8 StartY=6.2 StartZ=0 EndX=91.752 EndY=6.2 EndZ=0
    g18: LineSegment StartX=107.6 StartY=20 StartZ=0 EndX=132.428 EndY=20 EndZ=0
    g19: LineSegment StartX=147.645 StartY=8.94427 StartZ=0 EndX=176.685 EndY=-80.4316 EndZ=0
    g20: LineSegment StartX=176.685 StartY=-80.4316 StartZ=0 EndX=215.932 EndY=-80.4316 EndZ=0
    g21: LineSegment StartX=215.42 StartY=-53.0314 StartZ=0 EndX=192.176 EndY=-3.18451 EndZ=0
    g22: LineSegment StartX=202.765 StartY=20.303 StartZ=0 EndX=195.887 EndY=39.2 EndZ=0
    g23: LineSegment StartX=195.887 StartY=39.2 StartZ=0 EndX=0 EndY=39.2 EndZ=0
    g24: LineSegment StartX=196.467 StartY=26.4942 StartZ=0 EndX=194.073 EndY=33.0721 EndZ=0
    g25: LineSegment StartX=194.073 StartY=33.0721 StartZ=0 EndX=189.939 EndY=31.5672 EndZ=0
    g26: LineSegment StartX=189.939 StartY=31.5672 StartZ=0 EndX=192.333 EndY=24.9893 EndZ=0
    g27: LineSegment StartX=192.333 StartY=24.9893 StartZ=0 EndX=196.467 EndY=26.4942 EndZ=0
    g28: LineSegment StartX=132.428 StartY=20 StartZ=0 EndX=144.053 EndY=20 EndZ=0
    g29: LineSegment StartX=144.053 StartY=20 StartZ=0 EndX=147.645 EndY=8.94427 EndZ=0
  constraints (65):
    c: Equal(g0,g-25)
    c: Equal(g2,g-29)
    c: Equal(g3,g-30)
    c: Equal(g4,g-28)
    c: Equal(g1,g-26)
    c: Coincident(g0,g-25)
    c: Coincident(g1,g-26)
    c: Coincident(g2,g-29)
    c: Coincident(g3,g-30)
    c: Coincident(g4,g-28)
    c: Equal(g5,g-23)
    c: Equal(g6,g-24)
    c: Coincident(g5,g-23)
    c: Coincident(g6,g-24)
    c: Equal(g7,g-20)
    c: Coincident(g7,g-20)
    c: Equal(g9,g-22)
    c: Coincident(g9,g-22)
    c: Equal(g8,g-21)
    c: Coincident(g8,g-21)
    c: Equal(g13,g-12)
    c: Equal(g12,g-14)
    c: Equal(g10,g-9)
    c: Equal(g11,g-7)
    c: Coincident(g14,g-27)
    c: Coincident(g14,g-27)
    c: Coincident(g15,g14)
    c: Coincident(g15,g-5)
    c: Coincident(g16,g15)
    c: Coincident(g16,g-6)
    c: Coincident(g17,g16)
    c: Coincident(g17,g-7)
    c: Coincident(g11,g17)
    c: Coincident(g11,g-8)
    c: Coincident(g18,g11)
    c: Coincident(g18,g-9)
    c: Coincident(g10,g18)
    c: Coincident(g10,g-10)
    c: Coincident(g19,g10)
    c: Coincident(g19,g-11)
    c: Coincident(g20,g19)
    c: Coincident(g20,g-12)
    c: Coincident(g13,g20)
    c: Coincident(g13,g-13)
    c: Coincident(g21,g13)
    c: Coincident(g21,g-14)
    c: Coincident(g12,g21)
    c: Coincident(g12,g-15)
    c: Coincident(g22,g12)
    c: Coincident(g22,g-15)
    c: Coincident(g23,g22)
    c: Coincident(g23,g14)
    c: Coincident(g24,g-18)
    c: Coincident(g24,g-16)
    c: Coincident(g25,g24)
    c: Coincident(g25,g-19)
    c: Coincident(g26,g25)
    c: Coincident(g26,g-19)
    c: Coincident(g27,g26)
    c: Coincident(g27,g24)
    c: Coincident(g29,g10)
    c: Coincident(g28,g10)
    c: Coincident(g29,g28)
    c: Parallel(g28,g18)
    c: Parallel(g29,g19)
FEATURE [PartDesign::Pad] Pad011
  Direction = (0,1,-2e-16)
  Length = 2
  Length2 = 10
  Profile = -> Sketch114
  ReferenceAxis = -> Sketch114 [N_Axis]
  Refine = true
  Reversed = true
  Suppressed = false
  Type = 0
FEATURE [Sketcher::SketchObject] Sketch115
  ArcFitTolerance = 1e-06
  AttachmentSupport = -> [Pad011]
  ExternalGeometry = -> [Binder001]
  FullyConstrained = true
  MakeInternals = false
  MapMode = 5
  Placement = pos=(0,1.7e-15,0) rot=(0,0.707107,0.707107;3.14159rad)
  sketch-geometry (4):
    g0: ArcOfCircle CenterX=24.2 CenterY=26.7 CenterZ=0 NormalX=0 NormalY=0 NormalZ=1 AngleXU=0 Radius=3 StartAngle=4.48384e-08 EndAngle=3.14159
    g1: ArcOfCircle CenterX=24.2 CenterY=15.7 CenterZ=0 NormalX=0 NormalY=0 NormalZ=1 AngleXU=0 Radius=3 StartAngle=3.14159 EndAngle=6.28318
    g2: LineSegment StartX=21.2 StartY=26.7 StartZ=0 EndX=21.2 EndY=15.7 EndZ=0
    g3: LineSegment StartX=27.2 StartY=26.7 StartZ=0 EndX=27.2 EndY=15.7 EndZ=0
  constraints (12):
    c: Equal(g1,g-4)
    c: Equal(g0,g-3)
    c: Coincident(g0,g-3)
    c: Coincident(g1,g-4)
    c: Vertical(g2)
    c: Vertical(g3)
    c: Tangent(g3,g-3)
    c: Tangent(g2,g-3)
    c: Coincident(g0,g2)
    c: Coincident(g0,g3)
    c: Coincident(g1,g2)
    c: Coincident(g3,g1)
FEATURE [Sketcher::SketchObject] Sketch117  label="Sketch117 - fori per inserto M3 x 3 x 4.5"
  ArcFitTolerance = 1e-06
  AttachmentSupport = -> [Pad011]
  ExternalGeometry = -> [Binder001]
  FullyConstrained = true
  MakeInternals = false
  MapMode = 5
  Placement = pos=(0,1.7e-15,0) rot=(0,0.707107,0.707107;3.14159rad)
  sketch-geometry (4):
    g0: Circle CenterX=43.2 CenterY=30.3 CenterZ=0 NormalX=0 NormalY=0 NormalZ=1 AngleXU=0 Radius=2.25
    g1: Circle CenterX=43.2 CenterY=12.1 CenterZ=0 NormalX=0 NormalY=0 NormalZ=1 AngleXU=0 Radius=2.25
    g2: Circle CenterX=18.6 CenterY=30.3 CenterZ=0 NormalX=0 NormalY=0 NormalZ=1 AngleXU=0 Radius=2.25
    g3: Circle CenterX=18.6 CenterY=12.1 CenterZ=0 NormalX=0 NormalY=0 NormalZ=1 AngleXU=0 Radius=2.25
  constraints (8):
    c: Diameter(g0) = 4.5
    c: Diameter(g1) = 4.5
    c: Diameter(g2) = 4.5
    c: Diameter(g3) = 4.5
    c: Coincident(g2,g-3)
    c: Coincident(g3,g-6)
    c: Coincident(g0,g-4)
    c: Coincident(g1,g-5)
FEATURE [Sketcher::SketchObject] Sketch118
  ArcFitTolerance = 1e-06
  AttachmentSupport = -> [Pad011]
  ExternalGeometry = -> [Binder001]
  FullyConstrained = true
  MakeInternals = false
  MapMode = 5
  Placement = pos=(0,-2,0) rot=(1,0,0;1.5708rad)
  sketch-geometry (12):
    g0: Circle CenterX=-78.51 CenterY=34.8 CenterZ=0 NormalX=0 NormalY=0 NormalZ=1 AngleXU=0 Radius=1.8
    g1: Circle CenterX=-78.51 CenterY=7.6 CenterZ=0 NormalX=0 NormalY=0 NormalZ=1 AngleXU=0 Radius=1.8
    g2: Circle CenterX=-5.6 CenterY=34.8 CenterZ=0 NormalX=0 NormalY=0 NormalZ=1 AngleXU=0 Radius=1.8
    g3: Circle CenterX=-5.6 CenterY=7.6 CenterZ=0 NormalX=0 NormalY=0 NormalZ=1 AngleXU=0 Radius=1.8
    g4: LineSegment StartX=0 StartY=39.2 StartZ=0 EndX=0 EndY=3.2 EndZ=0
    g5: LineSegment StartX=0 StartY=3.2 StartZ=0 EndX=-82.8 EndY=3.2 EndZ=0
    g6: LineSegment StartX=-82.8 StartY=3.2 StartZ=0 EndX=-82.8 EndY=39.2 EndZ=0
    g7: LineSegment StartX=-82.8 StartY=39.2 StartZ=0 EndX=0 EndY=39.2 EndZ=0
    g8: ArcOfCircle CenterX=-65 CenterY=21.2 CenterZ=0 NormalX=0 NormalY=0 NormalZ=1 AngleXU=0 Radius=10 StartAngle=1.5708 EndAngle=4.71239
    g9: ArcOfCircle CenterX=-19 CenterY=21.2 CenterZ=0 NormalX=0 NormalY=0 NormalZ=1 AngleXU=0 Radius=10 StartAngle=4.71239 EndAngle=7.85398
    g10: LineSegment StartX=-65 StartY=31.2 StartZ=0 EndX=-19 EndY=31.2 EndZ=0
    g11: LineSegment StartX=-65 StartY=11.2 StartZ=0 EndX=-19 EndY=11.2 EndZ=0
  constraints (25):
    c: Equal(g2,g-5)
    c: Equal(g3,g-7)
    c: Equal(g1,g-6)
    c: Equal(g0,g-4)
    c: Coincident(g0,g-4)
    c: Coincident(g1,g-6)
    c: Coincident(g3,g-7)
    c: Coincident(g2,g-5)
    c: Coincident(g4,g-8)
    c: Coincident(g4,g-9)
    c: Coincident(g5,g4)
    c: Coincident(g5,g-10)
    c: Coincident(g6,g5)
    c: PointOnObject(g6,g-3)
    c: Vertical(g6)
    c: Coincident(g7,g6)
    c: Coincident(g7,g4)
    c: Tangent(g8,g10) = 1.5708
    c: Tangent(g8,g11) = -1.5708
    c: Tangent(g9,g10) = 1.5708
    c: Tangent(g9,g11) = -1.5708
    c: Equal(g8,g9)
    c: Radius(g8) = 10
    c: Coincident(g8,g-11)
    c: Coincident(g9,g-12)
FEATURE [Sketcher::SketchObject] Sketch120
  ArcFitTolerance = 1e-06
  AttachmentSupport = -> [Pad011]
  ExternalGeometry = -> [Binder001]
  FullyConstrained = true
  MakeInternals = false
  MapMode = 5
  Placement = pos=(0,-2,0) rot=(1,0,0;1.5708rad)
  sketch-geometry (4):
    g0: LineSegment StartX=-137.815 StartY=39.2 StartZ=0 EndX=-142.655 EndY=24.303 EndZ=0
    g1: LineSegment StartX=-137.815 StartY=39.2 StartZ=0 EndX=-110.815 EndY=39.2 EndZ=0
    g2: LineSegment StartX=-142.655 StartY=24.303 StartZ=0 EndX=-110.815 EndY=24.303 EndZ=0
    g3: ArcOfCircle CenterX=-92.2534 CenterY=31.7515 CenterZ=0 NormalX=0 NormalY=0 NormalZ=1 AngleXU=0 Radius=20 StartAngle=2.75997 EndAngle=3.52321
  constraints (12):
    c: PointOnObject(g0,g-3)
    c: Coincident(g1,g0)
    c: PointOnObject(g1,g-3)
    c: Coincident(g2,g0)
    c: Horizontal(g2)
    c: Tangent(g0,g-4)
    c: Vertical(g2,g1)
    c: DistanceX(g1,g1) = 27
    c: DistanceY(g-6,g0) = 4
    c: Radius(g3) = 20
    c: Coincident(g3,g1)
    c: Coincident(g3,g2)
FEATURE [Sketcher::SketchObject] Sketch121
  ArcFitTolerance = 1e-06
  AttachmentSupport = -> [Pad011]
  ExternalGeometry = -> [Binder001]
  FullyConstrained = true
  MakeInternals = false
  MapMode = 5
  Placement = pos=(0,-2,0) rot=(1,0,0;1.5708rad)
  sketch-geometry (15):
    g0: LineSegment StartX=-137.815 StartY=39.2 StartZ=0 EndX=-143.955 EndY=20.303 EndZ=0
    g1: LineSegment StartX=-143.955 StartY=20.303 StartZ=0 EndX=-190.141 EndY=20.303 EndZ=0
    g2: LineSegment StartX=-190.141 StartY=20.303 StartZ=0 EndX=-186.139 EndY=31.3 EndZ=0
    g3: LineSegment StartX=-178.754 StartY=39.2 StartZ=0 EndX=-180.791 EndY=33.6029 EndZ=0
    g4: ArcOfCircle CenterX=-184.08 CenterY=34.8 CenterZ=0 NormalX=0 NormalY=0 NormalZ=1 AngleXU=0 Radius=3.5 StartAngle=4.71239 EndAngle=5.93412
    g5: LineSegment StartX=-184.08 StartY=31.3 StartZ=0 EndX=-186.139 EndY=31.3 EndZ=0
    g6: LineSegment StartX=-137.815 StartY=39.2 StartZ=0 EndX=-156.815 EndY=39.2 EndZ=0
    g7: LineSegment StartX=-168.815 StartY=39.2 StartZ=0 EndX=-178.754 EndY=39.2 EndZ=0
    g8: LineSegment StartX=-157.815 StartY=39.2 StartZ=0 EndX=-167.815 EndY=39.2 EndZ=0
    g9: LineSegment StartX=-168.815 StartY=31.2 StartZ=0 EndX=-156.815 EndY=31.2 EndZ=0
    g10: LineSegment StartX=-167.436 StartY=36.2 StartZ=0 EndX=-157.436 EndY=36.2 EndZ=0
    g11: ArcOfCircle CenterX=-176.411 CenterY=35.2 CenterZ=0 NormalX=0 NormalY=0 NormalZ=1 AngleXU=0 Radius=20 StartAngle=6.08183 EndAngle=6.48454
    g12: ArcOfCircle CenterX=-188.411 CenterY=35.2 CenterZ=0 NormalX=0 NormalY=0 NormalZ=1 AngleXU=0 Radius=20 StartAngle=6.08183 EndAngle=6.48454
    g13: ArcOfCircle CenterX=-177.411 CenterY=35.2 CenterZ=0 NormalX=0 NormalY=0 NormalZ=1 AngleXU=0 Radius=20 StartAngle=0.0500209 EndAngle=0.201358
    g14: ArcOfCircle CenterX=-187.411 CenterY=35.2 CenterZ=0 NormalX=0 NormalY=0 NormalZ=1 AngleXU=0 Radius=20 StartAngle=0.0500209 EndAngle=0.201358
  constraints (46):
    c: PointOnObject(g0,g-3)
    c: Tangent(g0,g-5)
    c: Coincident(g1,g0)
    c: Horizontal(g1)
    c: Coincident(g2,g1)
    c: PointOnObject(g3,g-3)
    c: Parallel(g3,g-6)
    c: Parallel(g2,g-6)
    c: Radius(g4) = 3.5
    c: Coincident(g4,g-7)
    c: Tangent(g3,g4) = 1.5708
    c: Horizontal(g5)
    c: Tangent(g5,g4) = 1.5708
    c: DistanceX(g-8,g5) = 3.8
    c: Coincident(g2,g5)
    c: Coincident(g6,g0)
    c: PointOnObject(g6,g-3)
    c: DistanceX(g6,g6) = 19
    c: PointOnObject(g7,g-3)
    c: DistanceX(g7,g6) = 12
    c: Coincident(g7,g3)
    c: PointOnObject(g8,g-3)
    c: PointOnObject(g8,g-3)
    c: DistanceX(g8,g8) = 10
    c: DistanceX(g8,g6) = 1
    c: Horizontal(g9)
    c: Vertical(g7,g9)
    c: Vertical(g6,g9)
    c: DistanceY(g9,g7) = 8
    c: Horizontal(g10)
    c: Equal(g8,g10)
    c: DistanceY(g10,g8) = 3
    c: Radius(g11) = 20
    c: Coincident(g11,g6)
    c: Coincident(g11,g9)
    c: Radius(g12) = 20
    c: Coincident(g12,g7)
    c: Coincident(g12,g9)
    c: Equal(g13,g11)
    c: Coincident(g13,g8)
    c: Coincident(g13,g10)
    c: Horizontal(g13,g11)
    c: Equal(g14,g12)
    c: Coincident(g14,g8)
    c: Coincident(g14,g10)
    c: Horizontal(g1,g-6)
FEATURE [Sketcher::SketchObject] Sketch122
  ArcFitTolerance = 1e-06
  AttachmentSupport = -> [Pad011]
  ExternalGeometry = -> [Binder001]
  FullyConstrained = true
  MakeInternals = false
  MapMode = 5
  Placement = pos=(0,-2,0) rot=(1,0,0;1.5708rad)
  sketch-geometry (8):
    g0: ArcOfCircle CenterX=-184.801 CenterY=-67.3089 CenterZ=0 NormalX=0 NormalY=0 NormalZ=1 AngleXU=0 Radius=33.7833 StartAngle=2.70526 EndAngle=3.54053
    g1: LineSegment StartX=-176.685 StartY=-80.4316 StartZ=0 EndX=-215.932 EndY=-80.4316 EndZ=0
    g2: LineSegment StartX=-215.42 StartY=-53.0314 StartZ=0 EndX=-192.176 EndY=-3.18454 EndZ=0
    g3: ArcOfCircle CenterX=-207.583 CenterY=4 CenterZ=0 NormalX=0 NormalY=0 NormalZ=1 AngleXU=0 Radius=17 StartAngle=5.84685 EndAngle=7.56663
    g4: Circle CenterX=-213.443 CenterY=-76.8316 CenterZ=0 NormalX=0 NormalY=0 NormalZ=1 AngleXU=0 Radius=3
    g5: Circle CenterX=-179.305 CenterY=-76.8316 CenterZ=0 NormalX=0 NormalY=0 NormalZ=1 AngleXU=0 Radius=3
    g6: LineSegment StartX=-143.955 StartY=20.303 StartZ=0 EndX=-176.685 EndY=-80.4316 EndZ=0
    g7: LineSegment StartX=-202.765 StartY=20.303 StartZ=0 EndX=-143.955 EndY=20.303 EndZ=0
  constraints (18):
    c: Coincident(g0,g-7)
    c: Coincident(g0,g-8)
    c: Coincident(g1,g0)
    c: Tangent(g2,g-5)
    c: Coincident(g3,g-6)
    c: Coincident(g2,g3)
    c: Coincident(g0,g2)
    c: Diameter(g4) = 6
    c: Diameter(g5) = 6
    c: Coincident(g4,g-9)
    c: Coincident(g5,g-10)
    c: Horizontal(g1)
    c: Coincident(g6,g1)
    c: Tangent(g6,g-4)
    c: Coincident(g3,g-6)
    c: Coincident(g7,g3)
    c: Horizontal(g7)
    c: Coincident(g7,g6)
FEATURE [Sketcher::SketchObject] Sketch123
  ArcFitTolerance = 1e-06
  AttachmentSupport = -> [Pad011]
  ExternalGeometry = -> [Binder001]
  FullyConstrained = true
  MakeInternals = false
  MapMode = 5
  Placement = pos=(0,-2,0) rot=(1,0,0;1.5708rad)
  sketch-geometry (4):
    g0: LineSegment StartX=-108 StartY=36.8 StartZ=0 EndX=-90 EndY=36.8 EndZ=0
    g1: LineSegment StartX=-108 StartY=36.8 StartZ=0 EndX=-108 EndY=26.8 EndZ=0
    g2: LineSegment StartX=-108 StartY=26.8 StartZ=0 EndX=-90 EndY=26.8 EndZ=0
    g3: ArcOfCircle CenterX=-94 CenterY=31.8 CenterZ=0 NormalX=0 NormalY=0 NormalZ=1 AngleXU=0 Radius=6.40312 StartAngle=5.38713 EndAngle=7.17924
  constraints (13):
    c: Horizontal(g0)
    c: Coincident(g1,g0)
    c: Vertical(g1)
    c: Coincident(g2,g1)
    c: Horizontal(g2)
    c: DistanceX(g0,g0) = 18
    c: DistanceY(g1,g1) = 10
    c: Equal(g0,g2)
    c: DistanceX(g0,g-3) = 90
    c: DistanceY(g0,g-3) = 2.4
    c: Coincident(g3,g0)
    c: Coincident(g3,g2)
    c: DistanceX(g3,g0) = 4
FEATURE [PartDesign::Chamfer] Chamfer014
  Angle = 45
  Base = -> Pad011 [Edge80,Edge4,Edge7]
  BaseFeature = -> Pad011
  ChamferType = 0
  FlipDirection = false
  Refine = true
  Size = 1.9
  Size2 = 1
  SupportTransform = false
  Suppressed = false
  UseAllEdges = false
FEATURE [PartDesign::Pocket] Pocket006
  BaseFeature = -> Chamfer014
  Direction = (0,-1,2e-16)
  Length = 1.2
  Length2 = 5
  Profile = -> Sketch115
  ReferenceAxis = -> Sketch115 [N_Axis]
  Refine = true
  Suppressed = false
  Type = 0
FEATURE [Sketcher::SketchObject] Sketch116  label="Sketch116 - pieno per inserto M3 x 3 x 4,5"
  ArcFitTolerance = 1e-06
  AttachmentSupport = -> [Pocket006]
  ExternalGeometry = -> [Binder001]
  FullyConstrained = true
  MakeInternals = false
  MapMode = 5
  Placement = pos=(0,1.7e-15,0) rot=(0,0.707107,0.707107;3.14159rad)
  sketch-geometry (4):
    g0: Circle CenterX=43.2 CenterY=30.3 CenterZ=0 NormalX=0 NormalY=0 NormalZ=1 AngleXU=0 Radius=3.4
    g1: Circle CenterX=43.2 CenterY=12.1 CenterZ=0 NormalX=0 NormalY=0 NormalZ=1 AngleXU=0 Radius=3.4
    g2: Circle CenterX=18.6 CenterY=30.3 CenterZ=0 NormalX=0 NormalY=0 NormalZ=1 AngleXU=0 Radius=3.4
    g3: Circle CenterX=18.6 CenterY=12.1 CenterZ=0 NormalX=0 NormalY=0 NormalZ=1 AngleXU=0 Radius=3.4
  constraints (8):
    c: Diameter(g0) = 6.8
    c: Diameter(g1) = 6.8
    c: Diameter(g2) = 6.8
    c: Diameter(g3) = 6.8
    c: Coincident(g2,g-3)
    c: Coincident(g0,g-4)
    c: Coincident(g3,g-6)
    c: Coincident(g1,g-5)
FEATURE [PartDesign::Pad] Pad012
  BaseFeature = -> Pocket006
  Direction = (0,1,-2e-16)
  Length = 2.4
  Length2 = 10
  Profile = -> Sketch116
  ReferenceAxis = -> Sketch116 [N_Axis]
  Refine = true
  Suppressed = false
  Type = 0
FEATURE [PartDesign::Pocket] Pocket007
  BaseFeature = -> Pad012
  Direction = (0,-1,2e-16)
  Length = 0.6
  Length2 = 2.4
  Profile = -> Sketch117
  ReferenceAxis = -> Sketch117 [N_Axis]
  Refine = true
  Suppressed = false
  Type = 4
FEATURE [PartDesign::Pad] Pad013
  BaseFeature = -> Pocket007
  Direction = (0,-1,2e-16)
  Length = 1.6
  Length2 = 10
  Profile = -> Sketch118
  ReferenceAxis = -> Sketch118 [N_Axis]
  Refine = true
  Suppressed = false
  Type = 0
FEATURE [Sketcher::SketchObject] Sketch119
  ArcFitTolerance = 1e-06
  AttachmentSupport = -> [Pad013]
  ExternalGeometry = -> [Binder001]
  FullyConstrained = true
  MakeInternals = false
  MapMode = 5
  Placement = pos=(0,-3.6,0) rot=(1,0,0;1.5708rad)
  sketch-geometry (21):
    g0: LineSegment [constr] StartX=-82.8 StartY=3.2 StartZ=0 EndX=-82.8 EndY=39.2 EndZ=0
    g1: ArcOfCircle CenterX=-78.51 CenterY=34.8 CenterZ=0 NormalX=0 NormalY=0 NormalZ=1 AngleXU=0 Radius=3.5 StartAngle=4.71239 EndAngle=6.28319
    g2: ArcOfCircle CenterX=-78.51 CenterY=7.6 CenterZ=0 NormalX=0 NormalY=0 NormalZ=1 AngleXU=0 Radius=3.5 StartAngle=0 EndAngle=1.5708
    g3: ArcOfCircle CenterX=-5.6 CenterY=34.8 CenterZ=0 NormalX=0 NormalY=0 NormalZ=1 AngleXU=0 Radius=3.5 StartAngle=3.14159 EndAngle=4.71239
    g4: ArcOfCircle CenterX=-5.6 CenterY=7.6 CenterZ=0 NormalX=0 NormalY=0 NormalZ=1 AngleXU=0 Radius=3.5 StartAngle=1.5708 EndAngle=3.14159
    g5: LineSegment StartX=0 StartY=39.2 StartZ=0 EndX=0 EndY=31.3 EndZ=0
    g6: LineSegment StartX=0 StartY=39.2 StartZ=0 EndX=-9.1 EndY=39.2 EndZ=0
    g7: LineSegment StartX=0 StartY=3.2 StartZ=0 EndX=0 EndY=11.1 EndZ=0
    g8: LineSegment StartX=0 StartY=3.2 StartZ=0 EndX=-9.1 EndY=3.2 EndZ=0
    g9: LineSegment StartX=-82.8 StartY=3.2 StartZ=0 EndX=-75.01 EndY=3.2 EndZ=0
    g10: LineSegment StartX=-82.8 StartY=3.2 StartZ=0 EndX=-82.8 EndY=11.1 EndZ=0
    g11: LineSegment StartX=-82.8 StartY=39.2 StartZ=0 EndX=-82.8 EndY=31.3 EndZ=0
    g12: LineSegment StartX=-82.8 StartY=39.2 StartZ=0 EndX=-75.01 EndY=39.2 EndZ=0
    g13: LineSegment StartX=-82.8 StartY=31.3 StartZ=0 EndX=-78.51 EndY=31.3 EndZ=0
    g14: LineSegment StartX=-75.01 StartY=39.2 StartZ=0 EndX=-75.01 EndY=34.8 EndZ=0
    g15: LineSegment StartX=-82.8 StartY=11.1 StartZ=0 EndX=-78.51 EndY=11.1 EndZ=0
    g16: LineSegment StartX=-75.01 StartY=3.2 StartZ=0 EndX=-75.01 EndY=7.6 EndZ=0
    g17: LineSegment StartX=-9.1 StartY=39.2 StartZ=0 EndX=-9.1 EndY=34.8 EndZ=0
    g18: LineSegment StartX=0 StartY=31.3 StartZ=0 EndX=-5.6 EndY=31.3 EndZ=0
    g19: LineSegment StartX=0 StartY=11.1 StartZ=0 EndX=-5.6 EndY=11.1 EndZ=0
    g20: LineSegment StartX=-9.1 StartY=3.2 StartZ=0 EndX=-9.1 EndY=7.6 EndZ=0
  constraints (51):
    c: Coincident(g0,g-10)
    c: PointOnObject(g0,g-8)
    c: Vertical(g0)
    c: Coincident(g1,g-3)
    c: Coincident(g2,g-4)
    c: Coincident(g3,g-5)
    c: Coincident(g4,g-6)
    c: Radius(g4) = 3.5
    c: Radius(g3) = 3.5
    c: Radius(g1) = 3.5
    c: Radius(g2) = 3.5
    c: Coincident(g5,g-9)
    c: PointOnObject(g5,g-9)
    c: Coincident(g6,g5)
    c: PointOnObject(g6,g-8)
    c: Coincident(g7,g-9)
    c: PointOnObject(g7,g-9)
    c: Coincident(g8,g7)
    c: PointOnObject(g8,g-7)
    c: Coincident(g9,g0)
    c: PointOnObject(g9,g-7)
    c: Coincident(g10,g0)
    c: PointOnObject(g10,g0)
    c: Coincident(g11,g0)
    c: PointOnObject(g11,g0)
    c: Coincident(g12,g0)
    c: PointOnObject(g12,g-8)
    c: Coincident(g13,g11)
    c: Horizontal(g13)
    c: Coincident(g14,g12)
    c: Vertical(g14)
    c: Coincident(g15,g10)
    c: Horizontal(g15)
    c: Coincident(g16,g9)
    c: Vertical(g16)
    c: Coincident(g17,g6)
    c: Vertical(g17)
    c: Coincident(g18,g5)
    c: Horizontal(g18)
    c: Coincident(g19,g7)
    c: Horizontal(g19)
    c: Coincident(g20,g8)
    c: Vertical(g20)
    c: Tangent(g20,g4) = 1.5708
    c: Tangent(g4,g19) = -1.5708
    c: Tangent(g18,g3) = 1.5708
    c: Tangent(g3,g17) = -1.5708
    c: Tangent(g13,g1) = -1.5708
    c: Tangent(g1,g14) = 1.5708
    c: Tangent(g16,g2) = -1.5708
    c: Tangent(g2,g15) = 1.5708
FEATURE [PartDesign::Pocket] Pocket008
  BaseFeature = -> Pad013
  Direction = (0,1,-2e-16)
  Length = 1.6
  Length2 = 5
  Profile = -> Sketch119
  ReferenceAxis = -> Sketch119 [N_Axis]
  Refine = true
  Suppressed = false
  Type = 0
FEATURE [PartDesign::Pad] Pad017
  BaseFeature = -> Pocket008
  Direction = (0,-1,2e-16)
  Length = 1.6
  Length2 = 10
  Profile = -> Sketch123
  ReferenceAxis = -> Sketch123 [N_Axis]
  Refine = true
  Suppressed = false
  Type = 0
FEATURE [Sketcher::SketchObject] Sketch125
  ArcFitTolerance = 1e-06
  AttachmentSupport = -> [Pad017]
  ExternalGeometry = -> [Pad017]
  FullyConstrained = true
  MakeInternals = false
  MapMode = 5
  Placement = pos=(0,-3.6,8e-16) rot=(1,0,0;1.5708rad)
  sketch-geometry (20):
    g0: LineSegment StartX=-108 StartY=35.8 StartZ=0 EndX=-108 EndY=35 EndZ=0
    g1: LineSegment StartX=-108 StartY=35 StartZ=0 EndX=-97 EndY=35 EndZ=0
    g2: LineSegment StartX=-97 StartY=35 StartZ=0 EndX=-97 EndY=35.8 EndZ=0
    g3: LineSegment StartX=-97 StartY=35.8 StartZ=0 EndX=-108 EndY=35.8 EndZ=0
    g4: LineSegment StartX=-108 StartY=28.6 StartZ=0 EndX=-108 EndY=27.8 EndZ=0
    g5: LineSegment StartX=-108 StartY=27.8 StartZ=0 EndX=-97 EndY=27.8 EndZ=0
    g6: LineSegment StartX=-97 StartY=27.8 StartZ=0 EndX=-97 EndY=28.6 EndZ=0
    g7: LineSegment StartX=-97 StartY=28.6 StartZ=0 EndX=-108 EndY=28.6 EndZ=0
    g8: LineSegment StartX=-108 StartY=30.4 StartZ=0 EndX=-108 EndY=29.6 EndZ=0
    g9: LineSegment StartX=-108 StartY=29.6 StartZ=0 EndX=-97 EndY=29.6 EndZ=0
    g10: LineSegment StartX=-97 StartY=29.6 StartZ=0 EndX=-97 EndY=30.4 EndZ=0
    g11: LineSegment StartX=-97 StartY=30.4 StartZ=0 EndX=-108 EndY=30.4 EndZ=0
    g12: LineSegment StartX=-108 StartY=32.2 StartZ=0 EndX=-108 EndY=31.4 EndZ=0
    g13: LineSegment StartX=-108 StartY=31.4 StartZ=0 EndX=-97 EndY=31.4 EndZ=0
    g14: LineSegment StartX=-97 StartY=31.4 StartZ=0 EndX=-97 EndY=32.2 EndZ=0
    g15: LineSegment StartX=-97 StartY=32.2 StartZ=0 EndX=-108 EndY=32.2 EndZ=0
    g16: LineSegment StartX=-108 StartY=34 StartZ=0 EndX=-108 EndY=33.2 EndZ=0
    g17: LineSegment StartX=-108 StartY=33.2 StartZ=0 EndX=-97 EndY=33.2 EndZ=0
    g18: LineSegment StartX=-97 StartY=33.2 StartZ=0 EndX=-97 EndY=34 EndZ=0
    g19: LineSegment StartX=-97 StartY=34 StartZ=0 EndX=-108 EndY=34 EndZ=0
  constraints (55):
    c: Coincident(g1,g0)
    c: Horizontal(g1)
    c: Coincident(g2,g1)
    c: Vertical(g2)
    c: Coincident(g3,g2)
    c: Horizontal(g3)
    c: Coincident(g3,g0)
    c: DistanceX(g1,g1) = 11
    c: DistanceY(g2,g2) = 0.8
    c: Coincident(g5,g4)
    c: Horizontal(g5)
    c: Coincident(g6,g5)
    c: Vertical(g6)
    c: Coincident(g7,g6)
    c: Horizontal(g7)
    c: Coincident(g7,g4)
    c: Coincident(g9,g8)
    c: Horizontal(g9)
    c: Coincident(g10,g9)
    c: Vertical(g10)
    c: Coincident(g11,g10)
    c: Horizontal(g11)
    c: Coincident(g11,g8)
    c: Coincident(g13,g12)
    c: Horizontal(g13)
    c: Coincident(g14,g13)
    c: Vertical(g14)
    c: Coincident(g15,g14)
    c: Horizontal(g15)
    c: Coincident(g15,g12)
    c: Coincident(g17,g16)
    c: Horizontal(g17)
    c: Coincident(g18,g17)
    c: Vertical(g18)
    c: Coincident(g19,g18)
    c: Horizontal(g19)
    c: Coincident(g19,g16)
    c: Equal(g3,g19)
    c: Equal(g3,g15)
    c: Equal(g3,g11)
    c: Equal(g3,g7)
    c: Equal(g2,g18)
    c: Equal(g2,g14)
    c: Equal(g2,g10)
    c: Equal(g2,g6)
    c: DistanceY(g-4,g4) = 1
    c: DistanceY(g4,g8) = 1
    c: DistanceY(g8,g12) = 1
    c: DistanceY(g12,g16) = 1
    c: DistanceY(g16,g0) = 1
    c: Tangent(g0,g-5)
    c: Tangent(g16,g-5)
    c: Tangent(g12,g-5)
    c: Tangent(g8,g-5)
    c: Tangent(g4,g-5)
FEATURE [PartDesign::Chamfer] Chamfer009
  Angle = 45
  Base = -> Pad017 [Edge151,Edge154]
  BaseFeature = -> Pad017
  ChamferType = 1
  FlipDirection = false
  Refine = true
  Size = 1.5
  Size2 = 2.8
  SupportTransform = false
  Suppressed = false
  UseAllEdges = false
FEATURE [PartDesign::Pocket] Pocket009
  BaseFeature = -> Chamfer009
  Direction = (0,1,-2e-16)
  Length = 1
  Length2 = 5
  Profile = -> Sketch125
  ReferenceAxis = -> Sketch125 [N_Axis]
  Refine = true
  Suppressed = false
  Type = 0
FEATURE [PartDesign::Pad] Pad014
  BaseFeature = -> Pocket009
  Direction = (0,-1,2e-16)
  Length = 0.8
  Length2 = 10
  Profile = -> Sketch120
  ReferenceAxis = -> Sketch120 [N_Axis]
  Refine = true
  Suppressed = false
  Type = 0
FEATURE [Sketcher::SketchObject] Sketch124
  ArcFitTolerance = 1e-06
  AttachmentSupport = -> [Pad014]
  ExternalGeometry = -> [Binder001]
  FullyConstrained = true
  MakeInternals = false
  MapMode = 5
  Placement = pos=(0,-2.8,6e-16) rot=(1,0,0;1.5708rad)
  sketch-geometry (4):
    g0: LineSegment StartX=-129 StartY=39.2 StartZ=0 EndX=-131.599 EndY=31.2 EndZ=0
    g1: LineSegment StartX=-118 StartY=39.2 StartZ=0 EndX=-120.599 EndY=31.2 EndZ=0
    g2: LineSegment StartX=-129 StartY=39.2 StartZ=0 EndX=-118 EndY=39.2 EndZ=0
    g3: LineSegment StartX=-120.599 StartY=31.2 StartZ=0 EndX=-131.599 EndY=31.2 EndZ=0
  constraints (12):
    c: PointOnObject(g0,g-3)
    c: PointOnObject(g1,g-3)
    c: Parallel(g-4,g0)
    c: Parallel(g-4,g1)
    c: Coincident(g2,g0)
    c: Coincident(g2,g1)
    c: DistanceX(g2,g2) = 11
    c: DistanceY(g1,g1) = 8
    c: Coincident(g3,g1)
    c: Horizontal(g3)
    c: Coincident(g3,g0)
    c: DistanceX(g1,g-3) = 118
FEATURE [PartDesign::Pad] Pad018
  BaseFeature = -> Pad014
  Direction = (0,-1,2e-16)
  Length = 1.2
  Length2 = 10
  Profile = -> Sketch124
  ReferenceAxis = -> Sketch124 [N_Axis]
  Refine = true
  Suppressed = false
  Type = 0
FEATURE [Sketcher::SketchObject] Sketch126
  ArcFitTolerance = 1e-06
  AttachmentSupport = -> [Pad018]
  ExternalGeometry = -> [Pad018]
  FullyConstrained = true
  MakeInternals = false
  MapMode = 5
  Placement = pos=(0,-4,0) rot=(1,0,0;1.5708rad)
  sketch-geometry (8):
    g0: LineSegment StartX=-129.877 StartY=36.5 StartZ=0 EndX=-130.137 EndY=35.7 EndZ=0
    g1: LineSegment StartX=-130.69 StartY=34 StartZ=0 EndX=-130.95 EndY=33.2 EndZ=0
    g2: LineSegment StartX=-129.877 StartY=36.5 StartZ=0 EndX=-118.877 EndY=36.5 EndZ=0
    g3: LineSegment StartX=-130.137 StartY=35.7 StartZ=0 EndX=-119.137 EndY=35.7 EndZ=0
    g4: LineSegment StartX=-130.69 StartY=34 StartZ=0 EndX=-119.69 EndY=34 EndZ=0
    g5: LineSegment StartX=-130.95 StartY=33.2 StartZ=0 EndX=-119.95 EndY=33.2 EndZ=0
    g6: LineSegment StartX=-118.877 StartY=36.5 StartZ=0 EndX=-119.137 EndY=35.7 EndZ=0
    g7: LineSegment StartX=-119.69 StartY=34 StartZ=0 EndX=-119.95 EndY=33.2 EndZ=0
  constraints (20):
    c: Coincident(g2,g0)
    c: Horizontal(g2)
    c: Coincident(g3,g0)
    c: Horizontal(g3)
    c: Coincident(g4,g1)
    c: Horizontal(g4)
    c: Coincident(g5,g1)
    c: Horizontal(g5)
    c: Coincident(g6,g2)
    c: Coincident(g6,g3)
    c: Coincident(g7,g4)
    c: Coincident(g7,g5)
    c: Tangent(g0,g-4)
    c: Tangent(g6,g-5)
    c: Tangent(g1,g-4)
    c: Tangent(g7,g-5)
    c: DistanceY(g3,g2) = 0.8
    c: DistanceY(g5,g4) = 0.8
    c: DistanceY(g-6,g1) = 2
    c: DistanceY(g-6,g0) = 4.5
FEATURE [PartDesign::Chamfer] Chamfer008
  Angle = 45
  Base = -> Pad018 [Edge257]
  BaseFeature = -> Pad018
  ChamferType = 1
  FlipDirection = false
  Refine = true
  Size = 1
  Size2 = 6
  SupportTransform = false
  Suppressed = false
  UseAllEdges = false
FEATURE [PartDesign::Pocket] Pocket010
  BaseFeature = -> Chamfer008
  Direction = (0,1,-2e-16)
  Length = 1
  Length2 = 5
  Profile = -> Sketch126
  ReferenceAxis = -> Sketch126 [N_Axis]
  Refine = true
  Suppressed = false
  Type = 0
FEATURE [PartDesign::Pad] Pad015
  BaseFeature = -> Pocket010
  Direction = (0,-1,2e-16)
  Length = 2
  Length2 = 10
  Profile = -> Sketch121
  ReferenceAxis = -> Sketch121 [N_Axis]
  Refine = true
  Suppressed = false
  Type = 0
FEATURE [PartDesign::Pad] Pad016
  BaseFeature = -> Pad015
  Direction = (0,-1,2e-16)
  Length = 1.6
  Length2 = 10
  Profile = -> Sketch122
  ReferenceAxis = -> Sketch122 [N_Axis]
  Refine = true
  Suppressed = false
  Type = 0
FEATURE [Sketcher::SketchObject] Sketch129
  ArcFitTolerance = 1e-06
  AttachmentSupport = -> [Pad016]
  ExternalGeometry = -> [Binder001]
  FullyConstrained = true
  MakeInternals = false
  MapMode = 5
  Placement = pos=(0,-3.6,0) rot=(1,0,0;1.5708rad)
  sketch-geometry (12):
    g0: LineSegment [constr] StartX=-192.176 StartY=-3.18451 StartZ=0 EndX=-181.223 EndY=20.303 EndZ=0
    g1: LineSegment [constr] StartX=-202.765 StartY=20.303 StartZ=0 EndX=-181.223 EndY=20.303 EndZ=0
    g2: LineSegment StartX=-202.765 StartY=20.303 StartZ=0 EndX=-181.223 EndY=20.303 EndZ=0
    g3: LineSegment StartX=-192.176 StartY=-3.18451 StartZ=0 EndX=-196.804 EndY=-13.1107 EndZ=0
    g4: ArcOfCircle CenterX=-207.583 CenterY=4 CenterZ=0 NormalX=0 NormalY=0 NormalZ=1 AngleXU=0 Radius=17 StartAngle=5.84685 EndAngle=7.56663
    g5: ArcOfEllipse CenterX=-181.223 CenterY=8.55923 CenterZ=0 NormalX=0 NormalY=0 NormalZ=1 MajorRadius=23.4779 MinorRadius=11.7437 AngleXU=2e-16 StartAngle=4.71239 EndAngle=7.85398
    g6: LineSegment [constr] StartX=-157.745 StartY=8.55923 StartZ=0 EndX=-204.701 EndY=8.55923 EndZ=0
    g7: LineSegment [constr] StartX=-181.223 StartY=20.303 StartZ=0 EndX=-181.223 EndY=-3.18451 EndZ=0
    g8: GeomPoint [constr] X=-160.894 Y=8.55923 Z=0
    g9: GeomPoint [constr] X=-201.553 Y=8.55923 Z=0
    g10: ArcOfCircle CenterX=-181.223 CenterY=-20.3763 CenterZ=0 NormalX=0 NormalY=0 NormalZ=1 AngleXU=0 Radius=17.1918 StartAngle=1.57079 EndAngle=2.70526
    g11: GeomPoint [constr] X=-181.223 Y=-3.18451 Z=0
  constraints (23):
    c: Coincident(g0,g-5)
    c: Coincident(g1,g-6)
    c: Horizontal(g1)
    c: Coincident(g1,g0)
    c: Parallel(g0,g-4)
    c: Coincident(g2,g1)
    c: Coincident(g2,g0)
    c: Coincident(g3,g0)
    c: Equal(g4,g-5)
    c: Coincident(g4,g1)
    c: Coincident(g4,g0)
    c: InternalAlignment(g6-g9 -> g5) x4
    c: Vertical(g5,g0)
    c: Horizontal(g6)
    c: Coincident(g5,g0)
    c: DistanceX(g6,g-3) = 10.1
    c: Tangent(g10,g3) = -1.5708
    c: PointOnObject(g11,g10)
    c: Tangent(g5,g10,g11) = 1.5708
    c: Coincident(g10,g5)
    c: Coincident(g11,g7)
    c: Parallel(g3,g-4)
    c: Horizontal(g5,g0)
FEATURE [Sketcher::SketchObject] Sketch130
  ArcFitTolerance = 1e-06
  AttachmentOffset = pos=(0,0,-1.6) rot=(0,0,1;0rad)
  AttachmentSupport = -> [Pad016]
  ExternalGeometry = -> [Binder001]
  FullyConstrained = true
  MakeInternals = false
  MapMode = 5
  Placement = pos=(0,-2,-4e-16) rot=(1,0,0;1.5708rad)
  sketch-geometry (12):
    g0: LineSegment [constr] StartX=-192.176 StartY=-3.18451 StartZ=0 EndX=-181.223 EndY=20.303 EndZ=0
    g1: LineSegment [constr] StartX=-202.765 StartY=20.303 StartZ=0 EndX=-181.223 EndY=20.303 EndZ=0
    g2: LineSegment StartX=-202.765 StartY=20.303 StartZ=0 EndX=-181.223 EndY=20.303 EndZ=0
    g3: LineSegment StartX=-192.176 StartY=-3.18451 StartZ=0 EndX=-193.827 EndY=-6.72678 EndZ=0
    g4: ArcOfCircle CenterX=-207.583 CenterY=4 CenterZ=0 NormalX=0 NormalY=0 NormalZ=1 AngleXU=0 Radius=17 StartAngle=5.84685 EndAngle=7.56663
    g5: ArcOfEllipse CenterX=-181.223 CenterY=10.803 CenterZ=0 NormalX=0 NormalY=0 NormalZ=1 MajorRadius=14.4779 MinorRadius=9.5 AngleXU=0 StartAngle=4.71239 EndAngle=7.85398
    g6: LineSegment [constr] StartX=-166.745 StartY=10.803 StartZ=0 EndX=-195.701 EndY=10.803 EndZ=0
    g7: LineSegment [constr] StartX=-181.223 StartY=20.303 StartZ=0 EndX=-181.223 EndY=1.30297 EndZ=0
    g8: GeomPoint [constr] X=-170.298 Y=10.803 Z=0
    g9: GeomPoint [constr] X=-192.148 Y=10.803 Z=0
    g10: ArcOfCircle CenterX=-181.223 CenterY=-12.6042 CenterZ=0 NormalX=0 NormalY=0 NormalZ=1 AngleXU=0 Radius=13.9072 StartAngle=1.5708 EndAngle=2.70526
    g11: GeomPoint [constr] X=-181.223 Y=1.30297 Z=0
  constraints (23):
    c: Coincident(g0,g-5)
    c: Coincident(g1,g-6)
    c: Horizontal(g1)
    c: Coincident(g1,g0)
    c: Parallel(g0,g-4)
    c: Coincident(g2,g1)
    c: Coincident(g2,g0)
    c: Coincident(g3,g0)
    c: Equal(g4,g-5)
    c: Coincident(g4,g1)
    c: Coincident(g4,g0)
    c: InternalAlignment(g6-g9 -> g5) x4
    c: Vertical(g5,g0)
    c: Horizontal(g6)
    c: Coincident(g5,g0)
    c: DistanceX(g6,g-3) = 19.1
    c: Tangent(g10,g3) = -1.5708
    c: PointOnObject(g11,g10)
    c: Tangent(g5,g10,g11) = 1.5708
    c: Coincident(g10,g5)
    c: Coincident(g11,g7)
    c: Parallel(g3,g-4)
    c: DistanceY(g5,g0) = 19
FEATURE [Part::Part2DObjectPython] Clone2D001  label="Sketch130 (2D)"  # Draft 2D object (typed FeaturePython)
  Fuse = false
  Objects = -> [Sketch130]
  Placement = pos=(0,-2,-4e-16) rot=(1,0,0;1.5708rad)
  Scale = (1,1,1)
FEATURE [Sketcher::SketchObject] Sketch131
  ArcFitTolerance = 1e-06
  AttachmentOffset = pos=(0,0,-3.5) rot=(0,0,1;0rad)
  AttachmentSupport = -> [Pad016]
  ExternalGeometry = -> [Binder001]
  FullyConstrained = true
  MakeInternals = false
  MapMode = 5
  Placement = pos=(0,-0.1,-8e-16) rot=(1,0,0;1.5708rad)
  sketch-geometry (1):
    g0: GeomPoint X=-197.47 Y=8.55923 Z=0
  constraints (1):
    c: Symmetric(g-6,g-4,g0)
FEATURE [Sketcher::SketchObject] Sketch132
  ArcFitTolerance = 1e-06
  AttachmentSupport = -> [Pad016]
  ExternalGeometry = -> [Binder001]
  FullyConstrained = true
  MakeInternals = false
  MapMode = 5
  Placement = pos=(0,-3.6,0) rot=(1,0,0;1.5708rad)
  sketch-geometry (3):
    g0: LineSegment [constr] StartX=-215.42 StartY=-53.0314 StartZ=0 EndX=-167.782 EndY=-53.0314 EndZ=0
    g1: Circle CenterX=-191.282 CenterY=-53.0314 CenterZ=0 NormalX=0 NormalY=0 NormalZ=1 AngleXU=0 Radius=11.5
    g2: Circle CenterX=-191.282 CenterY=-53.0314 CenterZ=0 NormalX=0 NormalY=0 NormalZ=1 AngleXU=0 Radius=10.7
  constraints (8):
    c: Coincident(g0,g-3)
    c: PointOnObject(g0,g-4)
    c: Horizontal(g0)
    c: Diameter(g1) = 23
    c: PointOnObject(g1,g0)
    c: DistanceX(g1,g0) = 23.5
    c: Diameter(g2) = 21.4
    c: Coincident(g2,g1)
FEATURE [Part::Part2DObjectPython] ShapeString  # Draft 2D object (typed FeaturePython)
  FontFile = <path>
  Fuse = false
  Justification = 6
  JustificationReference = 0
  KeepLeftMargin = false
  MakeFace = true
  ObliqueAngle = 0
  Placement = pos=(-199,-3.6,-57.5) rot=(1,0,0;1.5708rad)
  ScaleToSize = true
  Size = 10
  String = AS
  Tracking = 0
FEATURE [Sketcher::SketchObject] Sketch133
  ArcFitTolerance = 1e-06
  AttachmentSupport = -> [Binder]
  ExternalGeometry = -> [Binder]
  FullyConstrained = true
  MakeInternals = false
  MapMode = 5
  Placement = pos=(0,9e-16,0) rot=(0,0.707107,0.707107;3.14159rad)
  sketch-geometry (30):
    g0: LineSegment StartX=0 StartY=39.2 StartZ=0 EndX=0 EndY=3.2 EndZ=0
    g1: LineSegment StartX=0 StartY=3.2 StartZ=0 EndX=82.8 EndY=3.2 EndZ=0
    g2: LineSegment StartX=82.8 StartY=3.2 StartZ=0 EndX=82.8 EndY=6.2 EndZ=0
    g3: LineSegment StartX=82.8 StartY=6.2 StartZ=0 EndX=91.752 EndY=6.2 EndZ=0
    g4: LineSegment StartX=0 StartY=39.2 StartZ=0 EndX=195.887 EndY=39.2 EndZ=0
    g5: LineSegment StartX=195.887 StartY=39.2 StartZ=0 EndX=202.765 EndY=20.303 EndZ=0
    g6: LineSegment StartX=192.333 StartY=24.9893 StartZ=0 EndX=196.467 EndY=26.4942 EndZ=0
    g7: LineSegment StartX=196.467 StartY=26.4942 StartZ=0 EndX=194.073 EndY=33.0721 EndZ=0
    g8: LineSegment StartX=194.073 StartY=33.0721 StartZ=0 EndX=189.939 EndY=31.5672 EndZ=0
    g9: LineSegment StartX=189.939 StartY=31.5672 StartZ=0 EndX=192.333 EndY=24.9893 EndZ=0
    g10: ArcOfCircle CenterX=107.6 CenterY=4 CenterZ=0 NormalX=0 NormalY=0 NormalZ=1 AngleXU=0 Radius=16 StartAngle=1.5708 EndAngle=3.00366
    g11: LineSegment StartX=107.6 StartY=20 StartZ=0 EndX=132.428 EndY=20 EndZ=0
    g12: ArcOfCircle [constr] CenterX=132.428 CenterY=4 CenterZ=0 NormalX=0 NormalY=0 NormalZ=1 AngleXU=0 Radius=16 StartAngle=0.314159 EndAngle=1.5708
    g13: LineSegment StartX=147.645 StartY=8.94427 StartZ=0 EndX=176.685 EndY=-80.4316 EndZ=0
    g14: LineSegment StartX=176.685 StartY=-80.4316 StartZ=0 EndX=215.932 EndY=-80.4316 EndZ=0
    g15: ArcOfCircle CenterX=207.583 CenterY=4 CenterZ=0 NormalX=0 NormalY=0 NormalZ=1 AngleXU=0 Radius=17 StartAngle=1.85815 EndAngle=3.57792
    g16: ArcOfCircle CenterX=184.801 CenterY=-67.3089 CenterZ=0 NormalX=0 NormalY=0 NormalZ=1 AngleXU=0 Radius=33.7833 StartAngle=5.88425 EndAngle=6.71952
    g17: LineSegment StartX=192.176 StartY=-3.18451 StartZ=0 EndX=215.42 EndY=-53.0314 EndZ=0
    g18: Circle CenterX=5.6 CenterY=34.8 CenterZ=0 NormalX=0 NormalY=0 NormalZ=1 AngleXU=0 Radius=1.8
    g19: Circle CenterX=5.6 CenterY=7.6 CenterZ=0 NormalX=0 NormalY=0 NormalZ=1 AngleXU=0 Radius=1.8
    g20: Circle CenterX=78.51 CenterY=34.8 CenterZ=0 NormalX=0 NormalY=0 NormalZ=1 AngleXU=0 Radius=1.8
    g21: Circle CenterX=78.51 CenterY=7.6 CenterZ=0 NormalX=0 NormalY=0 NormalZ=1 AngleXU=0 Radius=1.8
    g22: Circle CenterX=184.08 CenterY=34.8 CenterZ=0 NormalX=0 NormalY=0 NormalZ=1 AngleXU=0 Radius=1.8
    g23: Circle CenterX=179.305 CenterY=-76.8316 CenterZ=0 NormalX=0 NormalY=0 NormalZ=1 AngleXU=0 Radius=1.8
    g24: Circle CenterX=213.443 CenterY=-76.8316 CenterZ=0 NormalX=0 NormalY=0 NormalZ=1 AngleXU=0 Radius=1.8
    g25: Circle CenterX=19 CenterY=21.2 CenterZ=0 NormalX=0 NormalY=0 NormalZ=1 AngleXU=0 Radius=6.3
    g26: Circle CenterX=42 CenterY=21.2 CenterZ=0 NormalX=0 NormalY=0 NormalZ=1 AngleXU=0 Radius=6.3
    g27: Circle CenterX=65 CenterY=21.2 CenterZ=0 NormalX=0 NormalY=0 NormalZ=1 AngleXU=0 Radius=6.3
    g28: LineSegment StartX=132.428 StartY=20 StartZ=0 EndX=144.053 EndY=20 EndZ=0
    g29: LineSegment StartX=147.645 StartY=8.94427 StartZ=0 EndX=144.053 EndY=20 EndZ=0
  constraints (65):
    c: Coincident(g0,g-4)
    c: Coincident(g0,g-5)
    c: Coincident(g1,g0)
    c: Coincident(g1,g-6)
    c: Coincident(g2,g1)
    c: Coincident(g2,g-7)
    c: Coincident(g3,g2)
    c: Coincident(g3,g-8)
    c: Coincident(g4,g0)
    c: Coincident(g4,g-16)
    c: Coincident(g5,g4)
    c: Coincident(g5,g-16)
    c: Coincident(g6,g-20)
    c: Coincident(g6,g-21)
    c: Coincident(g7,g6)
    c: Coincident(g7,g-23)
    c: Coincident(g8,g7)
    c: Coincident(g8,g-22)
    c: Coincident(g9,g8)
    c: Coincident(g9,g6)
    c: Equal(g10,g-8)
    c: Coincident(g10,g3)
    c: Coincident(g10,g-9)
    c: Coincident(g11,g10)
    c: Coincident(g11,g-10)
    c: Equal(g12,g-10)
    c: Coincident(g12,g11)
    c: Coincident(g12,g-11)
    c: Coincident(g13,g12)
    c: Coincident(g13,g-12)
    c: Coincident(g14,g13)
    c: Coincident(g14,g-13)
    c: Equal(g15,g-15)
    c: Coincident(g15,g5)
    c: Coincident(g15,g-15)
    c: Equal(g16,g-13)
    c: Coincident(g16,g14)
    c: Coincident(g16,g-14)
    c: Coincident(g17,g15)
    c: Coincident(g17,g16)
    c: Equal(g18,g-28)
    c: Equal(g19,g-29)
    c: Equal(g20,g-26)
    c: Equal(g21,g-27)
    c: Equal(g22,g-17)
    c: Equal(g24,g-25)
    c: Equal(g23,g-24)
    c: Coincident(g23,g-24)
    c: Coincident(g24,g-25)
    c: Coincident(g22,g-17)
    c: Coincident(g20,g-26)
    c: Coincident(g21,g-27)
    c: Coincident(g18,g-28)
    c: Coincident(g19,g-29)
    c: Equal(g25,g-30)
    c: Equal(g26,g-31)
    c: Equal(g27,g-32)
    c: Coincident(g25,g-30)
    c: Coincident(g26,g-31)
    c: Coincident(g27,g-32)
    c: Parallel(g28,g11)
    c: Parallel(g29,g13)
    c: Coincident(g28,g11)
    c: Coincident(g29,g12)
    c: Coincident(g29,g28)
FEATURE [PartDesign::Pad] Pad019
  Direction = (0,1,-2e-16)
  Length = 2
  Length2 = 10
  Profile = -> Sketch133
  ReferenceAxis = -> Sketch133 [N_Axis]
  Refine = true
  Suppressed = false
  Type = 0
FEATURE [Sketcher::SketchObject] Sketch091  label="Sketch091 - forma anteriore"
  ArcFitTolerance = 1e-06
  AttachmentSupport = -> [Pad019]
  ExternalGeometry = -> [Binder]
  FullyConstrained = true
  MakeInternals = false
  MapMode = 5
  Placement = pos=(0,2,0) rot=(0,0.707107,0.707107;3.14159rad)
  sketch-geometry (12):
    g0: Circle CenterX=5.6 CenterY=34.8 CenterZ=0 NormalX=0 NormalY=0 NormalZ=1 AngleXU=0 Radius=1.8
    g1: Circle CenterX=5.6 CenterY=7.6 CenterZ=0 NormalX=0 NormalY=0 NormalZ=1 AngleXU=0 Radius=1.8
    g2: Circle CenterX=78.51 CenterY=34.8 CenterZ=0 NormalX=0 NormalY=0 NormalZ=1 AngleXU=0 Radius=1.8
    g3: Circle CenterX=78.51 CenterY=7.6 CenterZ=0 NormalX=0 NormalY=0 NormalZ=1 AngleXU=0 Radius=1.8
    g4: LineSegment StartX=0 StartY=39.2 StartZ=0 EndX=0 EndY=3.2 EndZ=0
    g5: LineSegment StartX=0 StartY=3.2 StartZ=0 EndX=82.8 EndY=3.2 EndZ=0
    g6: LineSegment StartX=82.8 StartY=3.2 StartZ=0 EndX=82.8 EndY=39.2 EndZ=0
    g7: LineSegment StartX=82.8 StartY=39.2 StartZ=0 EndX=0 EndY=39.2 EndZ=0
    g8: ArcOfCircle CenterX=19 CenterY=21.2 CenterZ=0 NormalX=0 NormalY=0 NormalZ=1 AngleXU=0 Radius=10 StartAngle=1.5708 EndAngle=4.71239
    g9: ArcOfCircle CenterX=65 CenterY=21.2 CenterZ=0 NormalX=0 NormalY=0 NormalZ=1 AngleXU=0 Radius=10 StartAngle=4.71239 EndAngle=7.85398
    g10: LineSegment StartX=19 StartY=31.2 StartZ=0 EndX=65 EndY=31.2 EndZ=0
    g11: LineSegment StartX=19 StartY=11.2 StartZ=0 EndX=65 EndY=11.2 EndZ=0
  constraints (25):
    c: Equal(g2,g-7)
    c: Equal(g3,g-8)
    c: Equal(g1,g-13)
    c: Equal(g0,g-12)
    c: Coincident(g0,g-12)
    c: Coincident(g1,g-13)
    c: Coincident(g3,g-8)
    c: Coincident(g2,g-7)
    c: Coincident(g4,g-4)
    c: Coincident(g4,g-5)
    c: Coincident(g5,g4)
    c: Coincident(g5,g-6)
    c: Coincident(g6,g5)
    c: PointOnObject(g6,g-3)
    c: Vertical(g6)
    c: Coincident(g7,g6)
    c: Coincident(g7,g4)
    c: Tangent(g8,g10) = 1.5708
    c: Tangent(g8,g11) = -1.5708
    c: Tangent(g9,g10) = 1.5708
    c: Tangent(g9,g11) = -1.5708
    c: Equal(g8,g9)
    c: Radius(g8) = 10
    c: Coincident(g8,g-11)
    c: Coincident(g9,g-9)
FEATURE [Sketcher::SketchObject] Sketch093  label="Sketch093 - scavi interni pulsanti"
  ArcFitTolerance = 1e-06
  AttachmentSupport = -> [Pad019]
  ExternalGeometry = -> [Binder]
  FullyConstrained = true
  MakeInternals = false
  MapMode = 5
  Placement = pos=(0,1.8e-15,0) rot=(1,0,0;1.5708rad)
  sketch-geometry (3):
    g0: Circle CenterX=-65 CenterY=21.2 CenterZ=0 NormalX=0 NormalY=0 NormalZ=1 AngleXU=0 Radius=7.3
    g1: Circle CenterX=-42 CenterY=21.2 CenterZ=0 NormalX=0 NormalY=0 NormalZ=1 AngleXU=0 Radius=7.3
    g2: Circle CenterX=-19 CenterY=21.2 CenterZ=0 NormalX=0 NormalY=0 NormalZ=1 AngleXU=0 Radius=7.3
  constraints (6):
    c: Coincident(g0,g-3)
    c: Coincident(g1,g-4)
    c: Coincident(g2,g-5)
    c: Diameter(g0) = 14.6
    c: Diameter(g1) = 14.6
    c: Diameter(g2) = 14.6
FEATURE [Sketcher::SketchObject] Sketch094  label="Sketch094 - forma centrale"
  ArcFitTolerance = 1e-06
  AttachmentSupport = -> [Pad019]
  ExternalGeometry = -> [Binder]
  FullyConstrained = true
  MakeInternals = false
  MapMode = 5
  Placement = pos=(0,2,0) rot=(0,0.707107,0.707107;3.14159rad)
  sketch-geometry (4):
    g0: LineSegment StartX=137.815 StartY=39.2 StartZ=0 EndX=142.655 EndY=24.303 EndZ=0
    g1: LineSegment StartX=110.815 StartY=24.303 StartZ=0 EndX=142.655 EndY=24.303 EndZ=0
    g2: LineSegment StartX=137.815 StartY=39.2 StartZ=0 EndX=110.815 EndY=39.2 EndZ=0
    g3: ArcOfCircle CenterX=92.2534 CenterY=31.7515 CenterZ=0 NormalX=0 NormalY=0 NormalZ=1 AngleXU=0 Radius=20 StartAngle=5.90156 EndAngle=6.66481
  constraints (12):
    c: PointOnObject(g0,g-3)
    c: Tangent(g0,g-5)
    c: Horizontal(g1)
    c: Coincident(g1,g0)
    c: Coincident(g2,g0)
    c: PointOnObject(g2,g-3)
    c: DistanceX(g2,g2) = 27
    c: Vertical(g1,g2)
    c: Coincident(g3,g2)
    c: Radius(g3) = 20
    c: Coincident(g3,g1)
    c: DistanceY(g-6,g0) = 4
FEATURE [Sketcher::SketchObject] Sketch095  label="Sketch095 - forma posteriore"
  ArcFitTolerance = 1e-06
  AttachmentSupport = -> [Pad019]
  ExternalGeometry = -> [Binder]
  FullyConstrained = true
  MakeInternals = false
  MapMode = 5
  Placement = pos=(0,2,0) rot=(0,0.707107,0.707107;3.14159rad)
  sketch-geometry (15):
    g0: LineSegment StartX=137.815 StartY=39.2 StartZ=0 EndX=143.955 EndY=20.303 EndZ=0
    g1: LineSegment StartX=143.955 StartY=20.303 StartZ=0 EndX=190.141 EndY=20.303 EndZ=0
    g2: ArcOfCircle CenterX=184.08 CenterY=34.8 CenterZ=0 NormalX=0 NormalY=0 NormalZ=1 AngleXU=0 Radius=3.5 StartAngle=3.49066 EndAngle=4.71239
    g3: LineSegment StartX=180.791 StartY=33.6029 StartZ=0 EndX=178.754 EndY=39.2 EndZ=0
    g4: LineSegment StartX=184.08 StartY=31.3 StartZ=0 EndX=186.139 EndY=31.3 EndZ=0
    g5: LineSegment StartX=190.141 StartY=20.303 StartZ=0 EndX=186.139 EndY=31.3 EndZ=0
    g6: LineSegment StartX=137.815 StartY=39.2 StartZ=0 EndX=156.815 EndY=39.2 EndZ=0
    g7: LineSegment StartX=178.754 StartY=39.2 StartZ=0 EndX=168.815 EndY=39.2 EndZ=0
    g8: LineSegment StartX=156.815 StartY=31.2 StartZ=0 EndX=168.815 EndY=31.2 EndZ=0
    g9: ArcOfCircle CenterX=176.411 CenterY=35.2 CenterZ=0 NormalX=0 NormalY=0 NormalZ=1 AngleXU=0 Radius=20 StartAngle=2.94023 EndAngle=3.34295
    g10: ArcOfCircle CenterX=188.411 CenterY=35.2 CenterZ=0 NormalX=0 NormalY=0 NormalZ=1 AngleXU=0 Radius=20 StartAngle=2.94023 EndAngle=3.34295
    g11: LineSegment StartX=157.815 StartY=39.2 StartZ=0 EndX=167.815 EndY=39.2 EndZ=0
    g12: LineSegment StartX=157.436 StartY=36.2 StartZ=0 EndX=167.436 EndY=36.2 EndZ=0
    g13: ArcOfCircle CenterX=177.411 CenterY=35.2 CenterZ=0 NormalX=0 NormalY=0 NormalZ=1 AngleXU=0 Radius=20 StartAngle=2.94023 EndAngle=3.09157
    g14: ArcOfCircle CenterX=187.411 CenterY=35.2 CenterZ=0 NormalX=0 NormalY=0 NormalZ=1 AngleXU=0 Radius=20 StartAngle=2.94023 EndAngle=3.09157
  constraints (46):
    c: PointOnObject(g0,g-3)
    c: Tangent(g0,g-6)
    c: Coincident(g1,g0)
    c: Horizontal(g1)
    c: Radius(g2) = 3.5
    c: Coincident(g2,g-5)
    c: PointOnObject(g3,g-3)
    c: Parallel(g3,g-4)
    c: Tangent(g3,g2) = 1.5708
    c: Horizontal(g4)
    c: Tangent(g4,g2) = -1.5708
    c: Coincident(g5,g1)
    c: Parallel(g5,g-4)
    c: Coincident(g5,g4)
    c: DistanceX(g4,g-8) = 3.8
    c: Coincident(g6,g0)
    c: PointOnObject(g6,g-3)
    c: Coincident(g7,g3)
    c: PointOnObject(g7,g-3)
    c: Horizontal(g8)
    c: DistanceX(g6,g7) = 12
    c: Vertical(g8,g6)
    c: Vertical(g7,g8)
    c: DistanceY(g8,g6) = 8
    c: Coincident(g9,g8)
    c: Coincident(g9,g6)
    c: Coincident(g10,g7)
    c: Coincident(g10,g8)
    c: Radius(g9) = 20
    c: Radius(g10) = 20
    c: PointOnObject(g11,g-3)
    c: PointOnObject(g11,g-3)
    c: DistanceX(g11,g11) = 10
    c: DistanceX(g6,g11) = 1
    c: Horizontal(g12)
    c: Equal(g12,g11)
    c: DistanceY(g12,g11) = 3
    c: Coincident(g13,g11)
    c: Coincident(g13,g12)
    c: Radius(g13) = 20
    c: Coincident(g14,g11)
    c: Coincident(g14,g12)
    c: Radius(g14) = 20
    c: DistanceX(g0,g6) = 19
    c: Horizontal(g9,g13)
    c: Horizontal(g0,g-4)
FEATURE [Sketcher::SketchObject] Sketch096  label="Sketch096 - forma impugnatura"
  ArcFitTolerance = 1e-06
  AttachmentSupport = -> [Pad019]
  ExternalGeometry = -> [Binder]
  FullyConstrained = true
  MakeInternals = false
  MapMode = 5
  Placement = pos=(0,2,0) rot=(0,0.707107,0.707107;3.14159rad)
  sketch-geometry (8):
    g0: LineSegment StartX=176.685 StartY=-80.4316 StartZ=0 EndX=143.955 EndY=20.303 EndZ=0
    g1: LineSegment StartX=176.685 StartY=-80.4316 StartZ=0 EndX=215.932 EndY=-80.4316 EndZ=0
    g2: Circle CenterX=179.305 CenterY=-76.8316 CenterZ=0 NormalX=0 NormalY=0 NormalZ=1 AngleXU=0 Radius=3
    g3: Circle CenterX=213.443 CenterY=-76.8316 CenterZ=0 NormalX=0 NormalY=0 NormalZ=1 AngleXU=0 Radius=3
    g4: LineSegment StartX=143.955 StartY=20.303 StartZ=0 EndX=202.765 EndY=20.303 EndZ=0
    g5: LineSegment StartX=215.42 StartY=-53.0314 StartZ=0 EndX=192.176 EndY=-3.18451 EndZ=0
    g6: ArcOfCircle CenterX=184.801 CenterY=-67.3089 CenterZ=0 NormalX=0 NormalY=0 NormalZ=1 AngleXU=0 Radius=33.7833 StartAngle=5.88425 EndAngle=6.71952
    g7: ArcOfCircle CenterX=207.583 CenterY=4 CenterZ=0 NormalX=0 NormalY=0 NormalZ=1 AngleXU=0 Radius=17 StartAngle=1.85815 EndAngle=3.57792
  constraints (19):
    c: Coincident(g0,g-4)
    c: PointOnObject(g0,g-3)
    c: Horizontal(g0,g-7)
    c: Coincident(g1,g0)
    c: Coincident(g1,g-5)
    c: Diameter(g2) = 6
    c: Diameter(g3) = 6
    c: Coincident(g2,g-9)
    c: Coincident(g3,g-10)
    c: Coincident(g4,g0)
    c: Coincident(g5,g-6)
    c: Coincident(g6,g1)
    c: Coincident(g6,g5)
    c: Equal(g-5,g6)
    c: Coincident(g5,g-7)
    c: Coincident(g4,g-7)
    c: Tangent(g7,g-7)
    c: Coincident(g7,g4)
    c: Coincident(g7,g5)
FEATURE [Sketcher::SketchObject] Sketch097
  ArcFitTolerance = 1e-06
  AttachmentSupport = -> [Pad019]
  ExternalGeometry = -> [Binder]
  FullyConstrained = true
  MakeInternals = false
  MapMode = 5
  Placement = pos=(0,2,0) rot=(0,0.707107,0.707107;3.14159rad)
  sketch-geometry (4):
    g0: LineSegment StartX=90 StartY=36.8 StartZ=0 EndX=108 EndY=36.8 EndZ=0
    g1: LineSegment StartX=108 StartY=36.8 StartZ=0 EndX=108 EndY=26.8 EndZ=0
    g2: LineSegment StartX=108 StartY=26.8 StartZ=0 EndX=90 EndY=26.8 EndZ=0
    g3: ArcOfCircle CenterX=94 CenterY=31.8 CenterZ=0 NormalX=0 NormalY=0 NormalZ=1 AngleXU=0 Radius=6.40312 StartAngle=2.24554 EndAngle=4.03765
  constraints (13):
    c: Horizontal(g0)
    c: Coincident(g1,g0)
    c: Vertical(g1)
    c: DistanceX(g0,g0) = 18
    c: DistanceY(g1,g1) = 10
    c: Coincident(g2,g1)
    c: Horizontal(g2)
    c: Equal(g2,g0)
    c: DistanceY(g0,g-3) = 2.4
    c: Coincident(g3,g0)
    c: Coincident(g3,g2)
    c: DistanceX(g2,g3) = 4
    c: DistanceX(g-3,g0) = 90
FEATURE [PartDesign::Chamfer] Chamfer015
  Angle = 45
  Base = -> Pad019 [Edge19,Edge22,Edge79]
  BaseFeature = -> Pad019
  ChamferType = 0
  FlipDirection = false
  Refine = true
  Size = 1.9
  Size2 = 1
  SupportTransform = false
  Suppressed = false
  UseAllEdges = false
FEATURE [PartDesign::Pocket] Pocket002
  BaseFeature = -> Chamfer015
  Direction = (0,1,-2e-16)
  Length = 1.2
  Length2 = 5
  Profile = -> Sketch093
  ReferenceAxis = -> Sketch093 [N_Axis]
  Refine = true
  Suppressed = false
  Type = 0
FEATURE [PartDesign::Pad] Pad005
  BaseFeature = -> Pocket002
  Direction = (0,1,-2e-16)
  Length = 1.6
  Length2 = 10
  Profile = -> Sketch091
  ReferenceAxis = -> Sketch091 [N_Axis]
  Refine = true
  Suppressed = false
  Type = 0
FEATURE [Sketcher::SketchObject] Sketch092  label="Sketch092 - scavi per viti anteriori"
  ArcFitTolerance = 1e-06
  AttachmentSupport = -> [Pad005]
  ExternalGeometry = -> [Binder]
  FullyConstrained = true
  MakeInternals = false
  MapMode = 5
  Placement = pos=(0,3.6,0) rot=(0,0.707107,0.707107;3.14159rad)
  sketch-geometry (20):
    g0: ArcOfCircle CenterX=5.6 CenterY=7.6 CenterZ=0 NormalX=0 NormalY=0 NormalZ=1 AngleXU=0 Radius=3.5 StartAngle=0 EndAngle=1.5708
    g1: ArcOfCircle CenterX=5.6 CenterY=34.8 CenterZ=0 NormalX=0 NormalY=0 NormalZ=1 AngleXU=0 Radius=3.5 StartAngle=4.71239 EndAngle=6.28319
    g2: ArcOfCircle CenterX=78.51 CenterY=34.8 CenterZ=0 NormalX=0 NormalY=0 NormalZ=1 AngleXU=0 Radius=3.5 StartAngle=3.14159 EndAngle=4.71239
    g3: ArcOfCircle CenterX=78.51 CenterY=7.6 CenterZ=0 NormalX=0 NormalY=0 NormalZ=1 AngleXU=0 Radius=3.5 StartAngle=1.5708 EndAngle=3.14159
    g4: LineSegment StartX=0 StartY=3.2 StartZ=0 EndX=0 EndY=11.1 EndZ=0
    g5: LineSegment StartX=0 StartY=11.1 StartZ=0 EndX=5.6 EndY=11.1 EndZ=0
    g6: LineSegment StartX=0 StartY=3.2 StartZ=0 EndX=9.1 EndY=3.2 EndZ=0
    g7: LineSegment StartX=9.1 StartY=3.2 StartZ=0 EndX=9.1 EndY=7.6 EndZ=0
    g8: LineSegment StartX=0 StartY=39.2 StartZ=0 EndX=0 EndY=31.3 EndZ=0
    g9: LineSegment StartX=0 StartY=31.3 StartZ=0 EndX=5.6 EndY=31.3 EndZ=0
    g10: LineSegment StartX=0 StartY=39.2 StartZ=0 EndX=9.1 EndY=39.2 EndZ=0
    g11: LineSegment StartX=9.1 StartY=39.2 StartZ=0 EndX=9.1 EndY=34.8 EndZ=0
    g12: LineSegment StartX=82.8 StartY=39.2 StartZ=0 EndX=75.01 EndY=39.2 EndZ=0
    g13: LineSegment StartX=82.8 StartY=39.2 StartZ=0 EndX=82.8 EndY=31.3 EndZ=0
    g14: LineSegment StartX=82.8 StartY=31.3 StartZ=0 EndX=78.51 EndY=31.3 EndZ=0
    g15: LineSegment StartX=82.8 StartY=3.2 StartZ=0 EndX=75.01 EndY=3.2 EndZ=0
    g16: LineSegment StartX=75.01 StartY=3.2 StartZ=0 EndX=75.01 EndY=7.6 EndZ=0
    g17: LineSegment StartX=82.8 StartY=3.2 StartZ=0 EndX=82.8 EndY=11.1 EndZ=0
    g18: LineSegment StartX=82.8 StartY=11.1 StartZ=0 EndX=78.51 EndY=11.1 EndZ=0
    g19: LineSegment StartX=75.01 StartY=39.2 StartZ=0 EndX=75.01 EndY=34.8 EndZ=0
  constraints (48):
    c: Radius(g0) = 3.5
    c: Coincident(g0,g-10)
    c: Radius(g1) = 3.5
    c: Coincident(g1,g-9)
    c: Radius(g2) = 3.5
    c: Coincident(g2,g-8)
    c: Radius(g3) = 3.5
    c: Coincident(g3,g-7)
    c: Coincident(g4,g-5)
    c: PointOnObject(g4,g-4)
    c: Coincident(g5,g4)
    c: Horizontal(g5)
    c: Coincident(g6,g4)
    c: PointOnObject(g6,g-5)
    c: Coincident(g7,g6)
    c: Vertical(g7)
    c: Coincident(g8,g-4)
    c: PointOnObject(g8,g-4)
    c: Coincident(g9,g8)
    c: Horizontal(g9)
    c: Coincident(g10,g8)
    c: PointOnObject(g10,g-3)
    c: Coincident(g11,g10)
    c: Vertical(g11)
    c: PointOnObject(g12,g-3)
    c: PointOnObject(g12,g-3)
    c: Coincident(g13,g12)
    c: Vertical(g13)
    c: Coincident(g14,g13)
    c: Horizontal(g14)
    c: Coincident(g15,g-6)
    c: PointOnObject(g15,g-5)
    c: Coincident(g16,g15)
    c: Vertical(g16)
    c: Coincident(g17,g15)
    c: Coincident(g18,g17)
    c: Horizontal(g18)
    c: Tangent(g3,g18) = -1.5708
    c: Tangent(g16,g3) = 1.5708
    c: Coincident(g19,g12)
    c: Vertical(g19)
    c: Tangent(g2,g19) = -1.5708
    c: Tangent(g2,g14) = 1.5708
    c: Tangent(g0,g7) = -1.5708
    c: Tangent(g0,g5) = 1.5708
    c: Tangent(g9,g1) = -1.5708
    c: Tangent(g1,g11) = 1.5708
    c: Tangent(g17,g13)
FEATURE [PartDesign::Pocket] Pocket001
  BaseFeature = -> Pad005
  Direction = (0,-1,2e-16)
  Length = 1.6
  Length2 = 5
  Profile = -> Sketch092
  ReferenceAxis = -> Sketch092 [N_Axis]
  Refine = true
  Suppressed = false
  Type = 0
FEATURE [PartDesign::Pad] Pad006
  BaseFeature = -> Pocket001
  Direction = (0,1,-2e-16)
  Length = 0.8
  Length2 = 10
  Profile = -> Sketch094
  ReferenceAxis = -> Sketch094 [N_Axis]
  Refine = true
  Suppressed = false
  Type = 0
FEATURE [PartDesign::Pad] Pad007
  BaseFeature = -> Pad006
  Direction = (0,1,-2e-16)
  Length = 2
  Length2 = 10
  Profile = -> Sketch095
  ReferenceAxis = -> Sketch095 [N_Axis]
  Refine = true
  Suppressed = false
  Type = 0
FEATURE [PartDesign::Pad] Pad008  label="Pad008 - forma impugnatura"
  BaseFeature = -> Pad007
  Direction = (0,1,-2e-16)
  Length = 1.6
  Length2 = 10
  Profile = -> Sketch096
  ReferenceAxis = -> Sketch096 [N_Axis]
  Refine = true
  Suppressed = false
  Type = 0
FEATURE [PartDesign::Pad] Pad009
  BaseFeature = -> Pad008
  Direction = (0,1,-2e-16)
  Length = 1.6
  Length2 = 10
  Profile = -> Sketch097
  ReferenceAxis = -> Sketch097 [N_Axis]
  Refine = true
  Suppressed = false
  Type = 0
FEATURE [Sketcher::SketchObject] Sketch098
  ArcFitTolerance = 1e-06
  AttachmentSupport = -> [Pad006]
  ExternalGeometry = -> [Binder]
  FullyConstrained = true
  MakeInternals = false
  MapMode = 5
  Placement = pos=(0,2.8,-7e-16) rot=(0,0.707107,0.707107;3.14159rad)
  sketch-geometry (4):
    g0: LineSegment StartX=118 StartY=39.2 StartZ=0 EndX=129 EndY=39.2 EndZ=0
    g1: LineSegment StartX=120.599 StartY=31.2 StartZ=0 EndX=131.599 EndY=31.2 EndZ=0
    g2: LineSegment StartX=129 StartY=39.2 StartZ=0 EndX=131.599 EndY=31.2 EndZ=0
    g3: LineSegment StartX=118 StartY=39.2 StartZ=0 EndX=120.599 EndY=31.2 EndZ=0
  constraints (12):
    c: PointOnObject(g0,g-3)
    c: PointOnObject(g0,g-3)
    c: DistanceX(g0,g0) = 11
    c: Horizontal(g1)
    c: Equal(g1,g0)
    c: Coincident(g2,g0)
    c: Coincident(g3,g0)
    c: Parallel(g-4,g2)
    c: Coincident(g1,g2)
    c: Coincident(g1,g3)
    c: DistanceY(g1,g0) = 8
    c: DistanceX(g-3,g0) = 118
FEATURE [Sketcher::SketchObject] Sketch099
  ArcFitTolerance = 1e-06
  AttachmentSupport = -> [Pad008]
  ExternalGeometry = -> [Binder]
  FullyConstrained = true
  MakeInternals = false
  MapMode = 5
  Placement = pos=(0,3.6,0) rot=(0,0.707107,0.707107;3.14159rad)
  sketch-geometry (13):
    g0: LineSegment StartX=192.176 StartY=-3.18451 StartZ=0 EndX=196.804 EndY=-13.1108 EndZ=0
    g1: LineSegment [constr] StartX=202.765 StartY=20.303 StartZ=0 EndX=181.223 EndY=20.303 EndZ=0
    g2: LineSegment [constr] StartX=181.223 StartY=20.303 StartZ=0 EndX=181.223 EndY=-3.18451 EndZ=0
    g3: ArcOfCircle CenterX=181.223 CenterY=-20.3764 CenterZ=0 NormalX=0 NormalY=0 NormalZ=1 AngleXU=0 Radius=17.1918 StartAngle=0.436332 EndAngle=1.57079
    g4: ArcOfEllipse CenterX=181.223 CenterY=8.55923 CenterZ=0 NormalX=0 NormalY=0 NormalZ=1 MajorRadius=23.4779 MinorRadius=11.7437 AngleXU=0 StartAngle=1.5708 EndAngle=4.71239
    g5: LineSegment [constr] StartX=204.701 StartY=8.55923 StartZ=0 EndX=157.745 EndY=8.55923 EndZ=0
    g6: LineSegment [constr] StartX=181.223 StartY=20.303 StartZ=0 EndX=181.223 EndY=-3.18451 EndZ=0
    g7: GeomPoint [constr] X=201.553 Y=8.55923 Z=0
    g8: GeomPoint [constr] X=160.894 Y=8.55923 Z=0
    g9: GeomPoint [constr] X=181.223 Y=-3.18451 Z=0
    g10: LineSegment StartX=181.223 StartY=20.303 StartZ=0 EndX=202.765 EndY=20.303 EndZ=0
    g11: ArcOfCircle CenterX=207.583 CenterY=4 CenterZ=0 NormalX=0 NormalY=0 NormalZ=1 AngleXU=0 Radius=17 StartAngle=1.85815 EndAngle=3.57792
    g12: LineSegment [constr] StartX=172.411 StartY=39.2 StartZ=0 EndX=192.176 EndY=-3.18451 EndZ=0
  constraints (27):
    c: Coincident(g1,g-7)
    c: Horizontal(g1)
    c: Coincident(g2,g1)
    c: Vertical(g2)
    c: Horizontal(g2,g0)
    c: Coincident(g3,g0)
    c: Coincident(g3,g2)
    c: InternalAlignment(g5-g8 -> g4) x4
    c: Horizontal(g5)
    c: PointOnObject(g4,g2)
    c: Coincident(g4,g1)
    c: DistanceX(g-3,g5) = 10.1
    c: Coincident(g4,g2)
    c: Tangent(g3,g-5)
    c: PointOnObject(g9,g4)
    c: PointOnObject(g9,g3)
    c: Tangent(g4,g3,g9) = 1.5708
    c: Coincident(g10,g1)
    c: Coincident(g10,g1)
    c: Equal(g11,g-4)
    c: Coincident(g11,g1)
    c: Coincident(g11,g0)
    c: PointOnObject(g12,g-6)
    c: PointOnObject(g1,g12)
    c: Tangent(g12,g-5) = -1.5708
    c: Tangent(g0,g-5) = -1.5708
    c: Horizontal(g9,g12)
FEATURE [Sketcher::SketchObject] Sketch106  label="Sketch106 - smusso impuniatura interno"
  ArcFitTolerance = 1e-06
  AttachmentSupport = -> [Pad008]
  ExternalGeometry = -> [Pad008]
  FullyConstrained = true
  MakeInternals = false
  MapMode = 5
  Placement = pos=(0,-1.585e-13,-80.4316) rot=(1,0,0;3.14159rad)
  sketch-geometry (9):
    g0: LineSegment StartX=-176.685 StartY=-3.6 StartZ=0 EndX=-176.685 EndY=-2.14526e-11 EndZ=0
    g1: LineSegment [constr] StartX=-176.685 StartY=-1.416e-13 StartZ=0 EndX=-176.685 EndY=-2.14524e-11 EndZ=0
    g2: LineSegment [constr] StartX=-186.685 StartY=-3.6 StartZ=0 EndX=-186.685 EndY=-2.14526e-11 EndZ=0
    g3: ArcOfEllipse CenterX=-186.685 CenterY=-2.14524e-11 CenterZ=0 NormalX=0 NormalY=0 NormalZ=1 MajorRadius=10 MinorRadius=3.6 AngleXU=3.14159 StartAngle=1.5708 EndAngle=3.14159
    g4: LineSegment [constr] StartX=-196.685 StartY=-1.416e-13 StartZ=0 EndX=-176.685 EndY=-1.416e-13 EndZ=0
    g5: LineSegment [constr] StartX=-186.685 StartY=-3.6 StartZ=0 EndX=-186.685 EndY=3.6 EndZ=0
    g6: GeomPoint [constr] X=-196.015 Y=-1.389e-13 Z=0
    g7: GeomPoint [constr] X=-177.356 Y=-1.416e-13 Z=0
    g8: LineSegment StartX=-176.685 StartY=-3.6 StartZ=0 EndX=-186.685 EndY=-3.6 EndZ=0
  constraints (15):
    c: PointOnObject(g2,g-3)
    c: Coincident(g1,g-5)
    c: DistanceY(g1,g1) = 0
    c: Coincident(g0,g1)
    c: DistanceX(g2,g-5) = 10
    c: Vertical(g2)
    c: Horizontal(g2,g0)
    c: InternalAlignment(g4-g7 -> g3) x4
    c: Coincident(g3,g2)
    c: Horizontal(g4)
    c: Coincident(g3,g0)
    c: Tangent(g0,g-5) = 1.5708
    c: Coincident(g3,g2)
    c: Coincident(g8,g0)
    c: Coincident(g8,g2)
FEATURE [Sketcher::SketchObject] Sketch107  label="Sketch107 - smusso impugnatura esterno"
  ArcFitTolerance = 1e-06
  AttachmentSupport = -> [Pad008]
  ExternalGeometry = -> [Pad008]
  FullyConstrained = true
  MakeInternals = false
  MapMode = 5
  Placement = pos=(0,-1.585e-13,-80.4316) rot=(1,0,0;3.14159rad)
  sketch-geometry (9):
    g0: LineSegment [constr] StartX=-215.932 StartY=-1.416e-13 StartZ=0 EndX=-215.932 EndY=-6.75e-14 EndZ=0
    g1: LineSegment StartX=-215.932 StartY=-3.6 StartZ=0 EndX=-215.932 EndY=-6.75e-14 EndZ=0
    g2: LineSegment StartX=-215.932 StartY=-3.6 StartZ=0 EndX=-205.932 EndY=-3.6 EndZ=0
    g3: LineSegment [constr] StartX=-205.932 StartY=-3.6 StartZ=0 EndX=-205.932 EndY=-6.75e-14 EndZ=0
    g4: ArcOfEllipse CenterX=-205.932 CenterY=-6.75e-14 CenterZ=0 NormalX=0 NormalY=0 NormalZ=1 MajorRadius=10 MinorRadius=3.6 AngleXU=-3.14159 StartAngle=-2.66e-14 EndAngle=1.5708
    g5: LineSegment [constr] StartX=-215.932 StartY=-1.416e-13 StartZ=0 EndX=-195.932 EndY=-1.416e-13 EndZ=0
    g6: LineSegment [constr] StartX=-205.932 StartY=-3.6 StartZ=0 EndX=-205.932 EndY=3.6 EndZ=0
    g7: GeomPoint [constr] X=-215.262 Y=-1.568e-13 Z=0
    g8: GeomPoint [constr] X=-196.602 Y=-1.551e-13 Z=0
  constraints (16):
    c: Coincident(g0,g-6)
    c: PointOnObject(g0,g-6)
    c: DistanceY(g0,g0) = 0
    c: Coincident(g1,g-6)
    c: Coincident(g1,g0)
    c: Tangent(g2,g-3)
    c: DistanceX(g2,g2) = 10
    c: Coincident(g3,g2)
    c: Vertical(g3)
    c: Horizontal(g3,g0)
    c: InternalAlignment(g5-g8 -> g4) x4
    c: Coincident(g4,g3)
    c: Horizontal(g5)
    c: Coincident(g4,g0)
    c: Coincident(g4,g2)
    c: PointOnObject(g2,g1)
FEATURE [Sketcher::SketchObject] Sketch108
  ArcFitTolerance = 1e-06
  AttachmentOffset = pos=(0,0,-1.6) rot=(0,0,1;0rad)
  AttachmentSupport = -> [Pad008]
  ExternalGeometry = -> [Binder]
  FullyConstrained = true
  MakeInternals = false
  MapMode = 5
  Placement = pos=(0,2,4e-16) rot=(0,0.707107,0.707107;3.14159rad)
  sketch-geometry (14):
    g0: LineSegment StartX=192.176 StartY=-3.18451 StartZ=0 EndX=193.827 EndY=-6.72678 EndZ=0
    g1: LineSegment [constr] StartX=202.765 StartY=20.303 StartZ=0 EndX=181.223 EndY=20.303 EndZ=0
    g2: LineSegment [constr] StartX=181.223 StartY=20.303 StartZ=0 EndX=181.223 EndY=1.30297 EndZ=0
    g3: ArcOfCircle CenterX=181.223 CenterY=-12.6042 CenterZ=0 NormalX=0 NormalY=0 NormalZ=1 AngleXU=0 Radius=13.9072 StartAngle=0.436332 EndAngle=1.5708
    g4: ArcOfEllipse CenterX=181.223 CenterY=10.803 CenterZ=0 NormalX=0 NormalY=0 NormalZ=1 MajorRadius=14.4779 MinorRadius=9.5 AngleXU=0 StartAngle=1.5708 EndAngle=4.71239
    g5: LineSegment [constr] StartX=195.701 StartY=10.803 StartZ=0 EndX=166.745 EndY=10.803 EndZ=0
    g6: LineSegment [constr] StartX=181.223 StartY=20.303 StartZ=0 EndX=181.223 EndY=1.30297 EndZ=0
    g7: GeomPoint [constr] X=192.148 Y=10.803 Z=0
    g8: GeomPoint [constr] X=170.298 Y=10.803 Z=0
    g9: LineSegment StartX=181.223 StartY=20.303 StartZ=0 EndX=202.765 EndY=20.303 EndZ=0
    g10: ArcOfCircle CenterX=207.583 CenterY=4 CenterZ=0 NormalX=0 NormalY=0 NormalZ=1 AngleXU=0 Radius=17 StartAngle=1.85815 EndAngle=3.57792
    g11: LineSegment [constr] StartX=172.411 StartY=39.2 StartZ=0 EndX=192.176 EndY=-3.18451 EndZ=0
    g12: GeomPoint [constr] X=181.223 Y=1.30297 Z=0
    g13: GeomPoint [constr] X=181.223 Y=1.30297 Z=0
  constraints (28):
    c: Coincident(g1,g-7)
    c: Horizontal(g1)
    c: Coincident(g2,g1)
    c: Vertical(g2)
    c: Coincident(g3,g2)
    c: InternalAlignment(g5-g8 -> g4) x4
    c: Horizontal(g5)
    c: PointOnObject(g4,g2)
    c: Coincident(g4,g1)
    c: DistanceX(g-3,g5) = 19.1
    c: Coincident(g4,g2)
    c: Coincident(g9,g1)
    c: Coincident(g9,g1)
    c: Coincident(g10,g1)
    c: Coincident(g10,g0)
    c: PointOnObject(g11,g-6)
    c: PointOnObject(g1,g11)
    c: DistanceY(g2,g1) = 19
    c: Coincident(g10,g-4)
    c: PointOnObject(g12,g4)
    c: PointOnObject(g12,g3)
    c: Tangent(g11,g-5) = -1.5708
    c: Tangent(g0,g-5) = -1.5708
    c: Tangent(g3,g0) = 1.5708
    c: PointOnObject(g13,g4)
    c: PointOnObject(g13,g3)
    c: Tangent(g4,g3,g13) = 1.5708
    c: Horizontal(g11,g0)
FEATURE [Part::Part2DObjectPython] Clone2D  label="Sketch108 (2D)"  # Draft 2D object (typed FeaturePython)
  Fuse = false
  Objects = -> [Sketch108]
  Placement = pos=(0,2,4e-16) rot=(0,0.707107,0.707107;3.14159rad)
  Scale = (1,1,1)
FEATURE [Sketcher::SketchObject] Sketch109
  ArcFitTolerance = 1e-06
  AttachmentOffset = pos=(0,0,-3.5) rot=(0,0,1;0rad)
  AttachmentSupport = -> [Pad008]
  ExternalGeometry = -> [Binder]
  FullyConstrained = true
  MakeInternals = false
  MapMode = 5
  Placement = pos=(0,0.1,8e-16) rot=(0,0.707107,0.707107;3.14159rad)
  sketch-geometry (1):
    g0: GeomPoint X=197.47 Y=8.55923 Z=0
  constraints (1):
    c: Symmetric(g-7,g-5,g0)
FEATURE [PartDesign::Chamfer] Chamfer005
  Angle = 45
  Base = -> Pad009 [Edge215,Edge212]
  BaseFeature = -> Pad009
  ChamferType = 1
  FlipDirection = false
  Refine = true
  Size = 1.5
  Size2 = 2.8
  SupportTransform = false
  Suppressed = false
  UseAllEdges = false
FEATURE [Sketcher::SketchObject] Sketch111
  ArcFitTolerance = 1e-06
  AttachmentSupport = -> [Pad009]
  ExternalGeometry = -> [Pad009]
  FullyConstrained = true
  MakeInternals = false
  MapMode = 5
  Placement = pos=(0,3.6,-8e-16) rot=(0,0.707107,0.707107;3.14159rad)
  sketch-geometry (21):
    g0: LineSegment [constr] StartX=97 StartY=36.8 StartZ=0 EndX=97 EndY=26.8 EndZ=0
    g1: LineSegment StartX=97 StartY=28.6 StartZ=0 EndX=97 EndY=27.8 EndZ=0
    g2: LineSegment StartX=97 StartY=27.8 StartZ=0 EndX=108 EndY=27.8 EndZ=0
    g3: LineSegment StartX=108 StartY=27.8 StartZ=0 EndX=108 EndY=28.6 EndZ=0
    g4: LineSegment StartX=108 StartY=28.6 StartZ=0 EndX=97 EndY=28.6 EndZ=0
    g5: LineSegment StartX=97 StartY=35.8 StartZ=0 EndX=97 EndY=35 EndZ=0
    g6: LineSegment StartX=97 StartY=35 StartZ=0 EndX=108 EndY=35 EndZ=0
    g7: LineSegment StartX=108 StartY=35 StartZ=0 EndX=108 EndY=35.8 EndZ=0
    g8: LineSegment StartX=108 StartY=35.8 StartZ=0 EndX=97 EndY=35.8 EndZ=0
    g9: LineSegment StartX=97 StartY=30.4 StartZ=0 EndX=97 EndY=29.6 EndZ=0
    g10: LineSegment StartX=97 StartY=29.6 StartZ=0 EndX=108 EndY=29.6 EndZ=0
    g11: LineSegment StartX=108 StartY=29.6 StartZ=0 EndX=108 EndY=30.4 EndZ=0
    g12: LineSegment StartX=108 StartY=30.4 StartZ=0 EndX=97 EndY=30.4 EndZ=0
    g13: LineSegment StartX=97 StartY=34 StartZ=0 EndX=97 EndY=33.2 EndZ=0
    g14: LineSegment StartX=97 StartY=33.2 StartZ=0 EndX=108 EndY=33.2 EndZ=0
    g15: LineSegment StartX=108 StartY=33.2 StartZ=0 EndX=108 EndY=34 EndZ=0
    g16: LineSegment StartX=108 StartY=34 StartZ=0 EndX=97 EndY=34 EndZ=0
    g17: LineSegment StartX=97 StartY=32.2 StartZ=0 EndX=97 EndY=31.4 EndZ=0
    g18: LineSegment StartX=97 StartY=31.4 StartZ=0 EndX=108 EndY=31.4 EndZ=0
    g19: LineSegment StartX=108 StartY=31.4 StartZ=0 EndX=108 EndY=32.2 EndZ=0
    g20: LineSegment StartX=108 StartY=32.2 StartZ=0 EndX=97 EndY=32.2 EndZ=0
  constraints (54):
    c: Vertical(g0)
    c: PointOnObject(g0,g-3)
    c: PointOnObject(g0,g-4)
    c: DistanceX(g0,g-5) = 11
    c: Coincident(g1,g2)
    c: Coincident(g2,g3)
    c: Coincident(g3,g4)
    c: Coincident(g4,g1)
    c: Horizontal(g2)
    c: Horizontal(g4)
    c: Tangent(g1,g0)
    c: Tangent(g3,g-5)
    c: DistanceY(g2,g3) = 0.8
    c: Coincident(g5,g6)
    c: Coincident(g6,g7)
    c: Coincident(g7,g8)
    c: Coincident(g8,g5)
    c: Horizontal(g6)
    c: Horizontal(g8)
    c: DistanceY(g6,g7) = 0.8
    c: Coincident(g9,g10)
    c: Coincident(g10,g11)
    c: Coincident(g11,g12)
    c: Coincident(g12,g9)
    c: Horizontal(g10)
    c: Horizontal(g12)
    c: DistanceY(g10,g11) = 0.8
    c: Tangent(g5,g0)
    c: Tangent(g7,g-5)
    c: Tangent(g9,g0)
    c: Tangent(g11,g-5)
    c: Coincident(g13,g14)
    c: Coincident(g14,g15)
    c: Coincident(g15,g16)
    c: Coincident(g16,g13)
    c: Horizontal(g14)
    c: Horizontal(g16)
    c: DistanceY(g14,g15) = 0.8
    c: Tangent(g13,g0)
    c: Tangent(g15,g-5)
    c: Coincident(g17,g18)
    c: Coincident(g18,g19)
    c: Coincident(g19,g20)
    c: Coincident(g20,g17)
    c: Horizontal(g18)
    c: Horizontal(g20)
    c: DistanceY(g18,g19) = 0.8
    c: Tangent(g17,g0)
    c: Tangent(g19,g-5)
    c: DistanceY(g1,g9) = 1
    c: DistanceY(g9,g17) = 1
    c: DistanceY(g17,g13) = 1
    c: DistanceY(g13,g5) = 1
    c: DistanceY(g0,g1) = 1
FEATURE [PartDesign::Pocket] Pocket004
  BaseFeature = -> Chamfer005
  Direction = (0,-1,2e-16)
  Length = 1
  Length2 = 5
  Profile = -> Sketch111
  ReferenceAxis = -> Sketch111 [N_Axis]
  Refine = true
  Suppressed = false
  Type = 0
FEATURE [PartDesign::Pad] Pad010
  BaseFeature = -> Pocket004
  Direction = (0,1,-2e-16)
  Length = 1.2
  Length2 = 10
  Profile = -> Sketch098
  ReferenceAxis = -> Sketch098 [N_Axis]
  Refine = true
  Suppressed = false
  Type = 0
FEATURE [PartDesign::Chamfer] Chamfer006
  Angle = 45
  Base = -> Pad010 [Edge291]
  BaseFeature = -> Pad010
  ChamferType = 1
  FlipDirection = false
  Refine = true
  Size = 1
  Size2 = 6
  SupportTransform = false
  Suppressed = false
  UseAllEdges = false
FEATURE [Sketcher::SketchObject] Sketch110
  ArcFitTolerance = 1e-06
  AttachmentSupport = -> [Pad010]
  ExternalGeometry = -> [Sketch098]
  FullyConstrained = true
  MakeInternals = false
  MapMode = 5
  Placement = pos=(0,4,-9e-16) rot=(0,0.707107,0.707107;3.14159rad)
  sketch-geometry (8):
    g0: LineSegment StartX=119.69 StartY=34 StartZ=0 EndX=130.69 EndY=34 EndZ=0
    g1: LineSegment StartX=119.95 StartY=33.2 StartZ=0 EndX=130.95 EndY=33.2 EndZ=0
    g2: LineSegment StartX=119.137 StartY=35.7 StartZ=0 EndX=130.137 EndY=35.7 EndZ=0
    g3: LineSegment StartX=118.877 StartY=36.5 StartZ=0 EndX=129.877 EndY=36.5 EndZ=0
    g4: LineSegment StartX=118.877 StartY=36.5 StartZ=0 EndX=119.137 EndY=35.7 EndZ=0
    g5: LineSegment StartX=129.877 StartY=36.5 StartZ=0 EndX=130.137 EndY=35.7 EndZ=0
    g6: LineSegment StartX=119.69 StartY=34 StartZ=0 EndX=119.95 EndY=33.2 EndZ=0
    g7: LineSegment StartX=130.69 StartY=34 StartZ=0 EndX=130.95 EndY=33.2 EndZ=0
  constraints (24):
    c: Horizontal(g0)
    c: Horizontal(g1)
    c: Horizontal(g2)
    c: Horizontal(g3)
    c: Equal(g1,g-5)
    c: Equal(g0,g-5)
    c: Equal(g2,g-5)
    c: Equal(g3,g-5)
    c: PointOnObject(g0,g-3)
    c: PointOnObject(g1,g-3)
    c: PointOnObject(g2,g-3)
    c: PointOnObject(g3,g-3)
    c: Coincident(g4,g3)
    c: Coincident(g4,g2)
    c: Coincident(g5,g3)
    c: Coincident(g5,g2)
    c: Coincident(g6,g0)
    c: Coincident(g6,g1)
    c: Coincident(g7,g0)
    c: Coincident(g7,g1)
    c: DistanceY(g1,g0) = 0.8
    c: DistanceY(g2,g3) = 0.8
    c: DistanceY(g-5,g1) = 2
    c: DistanceY(g-5,g2) = 4.5
FEATURE [PartDesign::Pocket] Pocket003
  BaseFeature = -> Chamfer006
  Direction = (0,-1,2e-16)
  Length = 1
  Length2 = 5
  Profile = -> Sketch110
  ReferenceAxis = -> Sketch110 [N_Axis]
  Refine = true
  Suppressed = false
  Type = 0
FEATURE [PartDesign::SubtractivePipe] SubtractivePipe
  AuxilleryCurvelinear = true
  AuxillerySpineTangent = false
  BaseFeature = -> Pocket003
  Binormal = (0,0,0)
  Mode = 0
  Profile = -> Sketch106
  Refine = true
  Spine = -> Pad008 [Edge215]
  SpineTangent = false
  Suppressed = false
  Transformation = 0
  Transition = 0
FEATURE [PartDesign::SubtractivePipe] SubtractivePipe001
  AuxilleryCurvelinear = true
  AuxillerySpineTangent = false
  BaseFeature = -> SubtractivePipe
  Binormal = (0,0,0)
  Mode = 0
  Profile = -> Sketch107
  Refine = true
  Spine = -> Pad008 [Edge213,Edge216,Edge210]
  SpineTangent = false
  Suppressed = false
  Transformation = 0
  Transition = 0
FEATURE [PartDesign::SubtractiveLoft] SubtractiveLoft
  BaseFeature = -> SubtractivePipe001
  Closed = false
  Profile = -> Sketch099
  Refine = true
  Ruled = false
  Sections = -> [Sketch108]
  Suppressed = false
FEATURE [PartDesign::SubtractiveLoft] SubtractiveLoft001
  BaseFeature = -> SubtractiveLoft
  Closed = false
  Profile = -> Clone2D
  Refine = true
  Ruled = false
  Sections = -> [Sketch109]
  Suppressed = false
FEATURE [Sketcher::SketchObject] Sketch112
  ArcFitTolerance = 1e-06
  AttachmentSupport = -> [Pad008]
  ExternalGeometry = -> [Binder]
  FullyConstrained = true
  MakeInternals = false
  MapMode = 5
  Placement = pos=(0,3.6,0) rot=(0,0.707107,0.707107;3.14159rad)
  sketch-geometry (4):
    g0: LineSegment [constr] StartX=167.782 StartY=-53.0314 StartZ=0 EndX=215.42 EndY=-53.0314 EndZ=0
    g1: GeomPoint [constr] X=191.282 Y=-53.0314 Z=0
    g2: Circle CenterX=191.282 CenterY=-53.0314 CenterZ=0 NormalX=0 NormalY=0 NormalZ=1 AngleXU=0 Radius=11.5
    g3: Circle CenterX=191.282 CenterY=-53.0314 CenterZ=0 NormalX=0 NormalY=0 NormalZ=1 AngleXU=0 Radius=10.7
  constraints (9):
    c: Horizontal(g0)
    c: PointOnObject(g0,g-3)
    c: Diameter(g2) = 23
    c: Coincident(g2,g1)
    c: Diameter(g3) = 21.4
    c: Coincident(g3,g1)
    c: DistanceX(g0,g1) = 23.5
    c: PointOnObject(g1,g0)
    c: Coincident(g0,g-4)
FEATURE [PartDesign::Chamfer] Chamfer016
  Angle = 45
  Base = -> SubtractiveLoft001 [Edge118,Edge117,Edge119,Edge120,Edge109]
  BaseFeature = -> SubtractiveLoft001
  ChamferType = 0
  FlipDirection = false
  Refine = true
  Size = 1.5
  Size2 = 1
  SupportTransform = false
  Suppressed = false
  UseAllEdges = false
FEATURE [PartDesign::Chamfer] Chamfer017
  Angle = 45
  Base = -> Chamfer016 [Edge15]
  BaseFeature = -> Chamfer016
  ChamferType = 0
  FlipDirection = false
  Refine = true
  Size = 1.6
  Size2 = 1
  SupportTransform = false
  Suppressed = false
  UseAllEdges = false
FEATURE [PartDesign::Chamfer] Chamfer018
  Angle = 45
  Base = -> Chamfer017 [Edge10]
  BaseFeature = -> Chamfer017
  ChamferType = 0
  FlipDirection = false
  Refine = true
  Size = 3.5
  Size2 = 1
  SupportTransform = false
  Suppressed = false
  UseAllEdges = false
FEATURE [PartDesign::Chamfer] Chamfer019
  Angle = 45
  Base = -> Chamfer018 [Edge94]
  BaseFeature = -> Chamfer018
  ChamferType = 0
  FlipDirection = false
  Refine = true
  Size = 1.9
  Size2 = 1
  SupportTransform = false
  Suppressed = false
  UseAllEdges = false
FEATURE [PartDesign::Fillet] Fillet009
  Base = -> Chamfer019 [Edge83]
  BaseFeature = -> Chamfer019
  Radius = 1.1
  Refine = true
  SupportTransform = false
  Suppressed = false
  UseAllEdges = false
FEATURE [PartDesign::Fillet] Fillet010
  Base = -> Fillet009 [Edge74]
  BaseFeature = -> Fillet009
  Radius = 1.9
  Refine = true
  SupportTransform = false
  Suppressed = false
  UseAllEdges = false
FEATURE [PartDesign::Pocket] Pocket005
  BaseFeature = -> Fillet010
  Direction = (0,-1,2e-16)
  Length = 0.8
  Length2 = 5
  Profile = -> Sketch112
  ReferenceAxis = -> Sketch112 [N_Axis]
  Refine = true
  Suppressed = false
  Type = 0
FEATURE [Part::Part2DObjectPython] ShapeString001  # Draft 2D object (typed FeaturePython)
  FontFile = <path>
  Fuse = false
  Justification = 6
  JustificationReference = 0
  KeepLeftMargin = false
  MakeFace = true
  ObliqueAngle = 0
  Placement = pos=(-183.5,3.6,-57.5) rot=(0,0.707107,0.707107;3.14159rad)
  ScaleToSize = true
  Size = 10
  String = AS
  Tracking = 0
FEATURE [PartDesign::Pocket] Pocket013
  BaseFeature = -> Pocket005
  Direction = (-1e-16,-1,2e-16)
  Length = 1
  Length2 = 5
  Profile = -> ShapeString001
  ReferenceAxis = -> ShapeString001 [N_Axis]
  Refine = true
  Suppressed = false
  Type = 0
FEATURE [PartDesign::Pad] Pad020
  Direction = (0,-1,2e-16)
  Length = 25.2
  Length2 = 10
  Midplane = true
  Placement = pos=(0,0,0) rot=(1,0,0;1.5708rad)
  Profile = -> Sketch021
  ReferenceAxis = -> Sketch021 [N_Axis]
  Refine = true
  Suppressed = false
  Type = 0
FEATURE [PartDesign::Body] Body001  label="perno fermo rumble e driver solenoide"
  AllowCompound = false
  Group = -> [Sketch021,Pad020]
  Origin = -> Origin001
  Tip = -> Pad020
FEATURE [PartDesign::Pad] Pad021
  Direction = (0,-1,2e-16)
  Length = 16.8
  Length2 = 10
  Midplane = true
  Placement = pos=(0,0,0) rot=(1,0,0;1.5708rad)
  Profile = -> Sketch061
  ReferenceAxis = -> Sketch061 [N_Axis]
  Refine = true
  Suppressed = false
  Type = 0
FEATURE [PartDesign::Pocket] Pocket014
  BaseFeature = -> Pad021
  Direction = (0,1,-2e-16)
  Length = 12.8
  Length2 = 5
  Midplane = true
  Placement = pos=(0,0,0) rot=(1,0,0;1.5708rad)
  Profile = -> Sketch062
  ReferenceAxis = -> Sketch062 [N_Axis]
  Refine = true
  Suppressed = false
  Type = 0
FEATURE [PartDesign::Pad] Pad022
  BaseFeature = -> Pocket014
  Direction = (0,-1,2e-16)
  Length = 7.6
  Length2 = 10
  Midplane = true
  Placement = pos=(0,0,0) rot=(1,0,0;1.5708rad)
  Profile = -> Sketch063
  ReferenceAxis = -> Sketch063 [N_Axis]
  Refine = true
  Suppressed = false
  Type = 0
FEATURE [PartDesign::Body] Body003  label="blocco switch"
  AllowCompound = false
  Group = -> [Sketch061,Sketch062,Sketch063,Pad021,Pocket014,Pad022]
  Origin = -> Origin003
  Tip = -> Pad022
FEATURE [PartDesign::Pad] Pad024
  Direction = (0,-1,2e-16)
  Length = 17
  Length2 = 10
  Midplane = true
  Placement = pos=(0,0,0) rot=(1,0,0;1.5708rad)
  Profile = -> Sketch045
  ReferenceAxis = -> Sketch045 [N_Axis]
  Refine = true
  Suppressed = false
  Type = 0
FEATURE [PartDesign::Pocket] Pocket015
  BaseFeature = -> Pad024
  Direction = (-1,0,0)
  Length = 8
  Length2 = 5
  Placement = pos=(0,0,0) rot=(1,0,0;1.5708rad)
  Profile = -> Sketch047
  ReferenceAxis = -> Sketch047 [N_Axis]
  Refine = true
  Reversed = true
  Suppressed = false
  Type = 0
FEATURE [PartDesign::Pocket] Pocket016
  BaseFeature = -> Pocket015
  Direction = (-1,0,0)
  Length = 1
  Length2 = 5
  Placement = pos=(0,0,0) rot=(1,0,0;1.5708rad)
  Profile = -> Sketch046
  ReferenceAxis = -> Sketch046 [N_Axis]
  Refine = true
  Reversed = true
  Suppressed = false
  Type = 0
FEATURE [PartDesign::Pocket] Pocket017
  BaseFeature = -> Pocket016
  Direction = (0,1,-2e-16)
  Length = 17
  Length2 = 5
  Midplane = true
  Placement = pos=(0,0,0) rot=(1,0,0;1.5708rad)
  Profile = -> Sketch048
  ReferenceAxis = -> Sketch048 [N_Axis]
  Refine = true
  Suppressed = false
  Type = 0
FEATURE [PartDesign::Pad] Pad025
  BaseFeature = -> Pocket017
  Direction = (0,-1,2e-16)
  Length = 17
  Length2 = 10
  Midplane = true
  Placement = pos=(0,0,0) rot=(1,0,0;1.5708rad)
  Profile = -> Sketch049
  ReferenceAxis = -> Sketch049 [N_Axis]
  Refine = true
  Suppressed = false
  Type = 0
FEATURE [PartDesign::Pad] Pad026
  BaseFeature = -> Pad025
  Direction = (0,-1,2e-16)
  Length = 17
  Length2 = 10
  Midplane = true
  Placement = pos=(0,0,0) rot=(1,0,0;1.5708rad)
  Profile = -> Sketch066
  ReferenceAxis = -> Sketch066 [N_Axis]
  Refine = true
  Suppressed = false
  Type = 0
FEATURE [PartDesign::Pad] Pad027
  BaseFeature = -> Pad026
  Direction = (0,-1,2e-16)
  Length = 5
  Length2 = 10
  Midplane = true
  Placement = pos=(0,0,0) rot=(1,0,0;1.5708rad)
  Profile = -> Sketch064
  ReferenceAxis = -> Sketch064 [N_Axis]
  Refine = true
  Suppressed = false
  Type = 0
FEATURE [PartDesign::Pad] Pad028
  BaseFeature = -> Pad027
  Direction = (1,0,0)
  Length = 1
  Length2 = 10
  Placement = pos=(0,0,0) rot=(1,0,0;1.5708rad)
  Profile = -> Sketch068
  ReferenceAxis = -> Sketch068 [N_Axis]
  Refine = true
  Reversed = true
  Suppressed = false
  Type = 0
FEATURE [PartDesign::Chamfer] Chamfer020
  Angle = 45
  Base = -> Pad028 [Edge73,Edge75,Edge78,Edge77]
  BaseFeature = -> Pad028
  ChamferType = 0
  FlipDirection = false
  Placement = pos=(0,0,0) rot=(1,0,0;1.5708rad)
  Refine = true
  Size = 0.5
  Size2 = 1
  SupportTransform = false
  Suppressed = false
  UseAllEdges = false
FEATURE [PartDesign::Body] Body002  label="supporto per neopixel"
  AllowCompound = false
  Group = -> [Sketch045,Sketch047,Sketch046,Sketch048,Sketch049,Sketch066,Sketch064,Sketch068,Pad024,Pocket015,Pocket016,Pocket017,Pad025,Pad026,Pad027,Pad028,Chamfer020]
  Origin = -> Origin002
  Tip = -> Chamfer020
FEATURE [Sketcher::SketchObject] Sketch134  label="perno fermo rumble002"
  ArcFitTolerance = 1e-06
  AttachmentSupport = -> [XZ_Plane008]
  FullyConstrained = true
  MakeInternals = false
  MapMode = 5
  Placement = pos=(0,0,0) rot=(1,0,0;1.5708rad)
  sketch-geometry (16):
    g0: LineSegment StartX=0 StartY=0.45 StartZ=0 EndX=0 EndY=1.55 EndZ=0
    g1: LineSegment StartX=0.45 StartY=2 StartZ=0 EndX=1.55 EndY=2 EndZ=0
    g2: LineSegment StartX=2 StartY=1.55 StartZ=0 EndX=2 EndY=0.45 EndZ=0
    g3: LineSegment StartX=1.55 StartY=0 StartZ=0 EndX=0.45 EndY=0 EndZ=0
    g4: ArcOfCircle [constr] CenterX=0.45 CenterY=1.55 CenterZ=0 NormalX=0 NormalY=0 NormalZ=1 AngleXU=0 Radius=0.45 StartAngle=1.5708 EndAngle=3.14159
    g5: GeomPoint [constr] X=0 Y=2 Z=0
    g6: LineSegment StartX=0.45 StartY=2 StartZ=0 EndX=0 EndY=1.55 EndZ=0
    g7: ArcOfCircle [constr] CenterX=1.55 CenterY=1.55 CenterZ=0 NormalX=0 NormalY=0 NormalZ=1 AngleXU=0 Radius=0.45 StartAngle=0 EndAngle=1.5708
    g8: GeomPoint [constr] X=2 Y=2 Z=0
    g9: LineSegment StartX=2 StartY=1.55 StartZ=0 EndX=1.55 EndY=2 EndZ=0
    g10: ArcOfCircle [constr] CenterX=1.55 CenterY=0.45 CenterZ=0 NormalX=0 NormalY=0 NormalZ=1 AngleXU=0 Radius=0.45 StartAngle=4.71239 EndAngle=6.28319
    g11: GeomPoint [constr] X=2 Y=0 Z=0
    g12: LineSegment StartX=1.55 StartY=0 StartZ=0 EndX=2 EndY=0.45 EndZ=0
    g13: ArcOfCircle [constr] CenterX=0.45 CenterY=0.45 CenterZ=0 NormalX=0 NormalY=0 NormalZ=1 AngleXU=0 Radius=0.45 StartAngle=3.14159 EndAngle=4.71239
    g14: GeomPoint [constr] X=0 Y=0 Z=0
    g15: LineSegment StartX=0 StartY=0.45 StartZ=0 EndX=0.45 EndY=0 EndZ=0
  constraints (35):
    c: Coincident(g14,g-1)
    c: PointOnObject(g5,g-2)
    c: Horizontal(g1)
    c: Vertical(g2)
    c: Horizontal(g3)
    c: DistanceX(g5,g8) = 2
    c: DistanceY(g11,g8) = 2
    c: PointOnObject(g5,g0)
    c: PointOnObject(g5,g1)
    c: Tangent(g0,g4) = 1.5708
    c: Tangent(g1,g4) = 1.5708
    c: Coincident(g6,g0)
    c: Coincident(g6,g1)
    c: PointOnObject(g8,g2)
    c: PointOnObject(g8,g1)
    c: Tangent(g2,g7) = 1.5708
    c: Tangent(g1,g7) = 1.5708
    c: Coincident(g9,g2)
    c: Coincident(g9,g1)
    c: PointOnObject(g11,g2)
    c: PointOnObject(g11,g3)
    c: Tangent(g2,g10) = 1.5708
    c: Tangent(g3,g10) = 1.5708
    c: Coincident(g12,g2)
    c: Coincident(g12,g3)
    c: PointOnObject(g14,g0)
    c: PointOnObject(g14,g3)
    c: Tangent(g0,g13) = 1.5708
    c: Tangent(g3,g13) = 1.5708
    c: Coincident(g15,g0)
    c: Coincident(g15,g3)
    c: Equal(g6,g9)
    c: Equal(g9,g12)
    c: Equal(g12,g15)
    c: DistanceX(g14,g3) = 0.45
FEATURE [PartDesign::Pad] Pad029
  Direction = (0,-1,2e-16)
  Length = 17
  Length2 = 10
  Midplane = true
  Placement = pos=(0,0,0) rot=(1,0,0;1.5708rad)
  Profile = -> Sketch134
  ReferenceAxis = -> Sketch134 [N_Axis]
  Refine = true
  Suppressed = false
  Type = 0
FEATURE [PartDesign::Body] Body008  label="perno fermo neopixel"
  AllowCompound = false
  Group = -> [Sketch134,Pad029]
  Origin = -> Origin008
  Tip = -> Pad029
FEATURE [Sketcher::SketchObject] Sketch135  label="perno fermo rumble003"
  ArcFitTolerance = 1e-06
  AttachmentSupport = -> [XZ_Plane009]
  FullyConstrained = true
  MakeInternals = false
  MapMode = 5
  Placement = pos=(0,0,0) rot=(1,0,0;1.5708rad)
  sketch-geometry (16):
    g0: LineSegment StartX=4.69e-14 StartY=0.8 StartZ=0 EndX=-3.04e-14 EndY=3.1 EndZ=0
    g1: LineSegment StartX=0.8 StartY=3.9 StartZ=0 EndX=3.1 EndY=3.9 EndZ=0
    g2: LineSegment StartX=3.9 StartY=3.1 StartZ=0 EndX=3.9 EndY=0.8 EndZ=0
    g3: LineSegment StartX=3.1 StartY=0 StartZ=0 EndX=0.8 EndY=0 EndZ=0
    g4: ArcOfCircle [constr] CenterX=0.8 CenterY=3.1 CenterZ=0 NormalX=0 NormalY=0 NormalZ=1 AngleXU=0 Radius=0.8 StartAngle=1.5708 EndAngle=3.14159
    g5: GeomPoint [constr] X=0 Y=3.9 Z=0
    g6: LineSegment StartX=0.8 StartY=3.9 StartZ=0 EndX=-3.04e-14 EndY=3.1 EndZ=0
    g7: ArcOfCircle [constr] CenterX=3.1 CenterY=3.1 CenterZ=0 NormalX=0 NormalY=0 NormalZ=1 AngleXU=0 Radius=0.8 StartAngle=-2.4e-14 EndAngle=1.5708
    g8: GeomPoint [constr] X=3.9 Y=3.9 Z=0
    g9: LineSegment StartX=3.9 StartY=3.1 StartZ=0 EndX=3.1 EndY=3.9 EndZ=0
    g10: ArcOfCircle [constr] CenterX=3.1 CenterY=0.8 CenterZ=0 NormalX=0 NormalY=0 NormalZ=1 AngleXU=0 Radius=0.8 StartAngle=4.71239 EndAngle=6.28319
    g11: GeomPoint [constr] X=3.9 Y=0 Z=0
    g12: LineSegment StartX=3.1 StartY=0 StartZ=0 EndX=3.9 EndY=0.8 EndZ=0
    g13: ArcOfCircle [constr] CenterX=0.8 CenterY=0.8 CenterZ=0 NormalX=0 NormalY=0 NormalZ=1 AngleXU=0 Radius=0.8 StartAngle=3.14159 EndAngle=4.71239
    g14: GeomPoint [constr] X=0 Y=0 Z=0
    g15: LineSegment StartX=4.69e-14 StartY=0.8 StartZ=0 EndX=0.8 EndY=0 EndZ=0
  constraints (35):
    c: Coincident(g14,g-1)
    c: PointOnObject(g5,g-2)
    c: Horizontal(g1)
    c: Vertical(g2)
    c: Horizontal(g3)
    c: DistanceX(g5,g8) = 3.9
    c: DistanceY(g11,g8) = 3.9
    c: PointOnObject(g5,g0)
    c: PointOnObject(g5,g1)
    c: Tangent(g0,g4) = 1.5708
    c: Tangent(g1,g4) = 1.5708
    c: Coincident(g6,g0)
    c: Coincident(g6,g1)
    c: PointOnObject(g8,g2)
    c: PointOnObject(g8,g1)
    c: Tangent(g2,g7) = 1.5708
    c: Tangent(g1,g7) = 1.5708
    c: Coincident(g9,g2)
    c: Coincident(g9,g1)
    c: PointOnObject(g11,g2)
    c: PointOnObject(g11,g3)
    c: Tangent(g2,g10) = 1.5708
    c: Tangent(g3,g10) = 1.5708
    c: Coincident(g12,g2)
    c: Coincident(g12,g3)
    c: PointOnObject(g14,g0)
    c: PointOnObject(g14,g3)
    c: Tangent(g0,g13) = 1.5708
    c: Tangent(g3,g13) = 1.5708
    c: Coincident(g15,g0)
    c: Coincident(g15,g3)
    c: Equal(g6,g9)
    c: Equal(g9,g12)
    c: Equal(g12,g15)
    c: DistanceX(g14,g3) = 0.8
FEATURE [PartDesign::Pad] Pad030
  Direction = (0,-1,2e-16)
  Length = 25.2
  Length2 = 10
  Midplane = true
  Placement = pos=(0,0,0) rot=(1,0,0;1.5708rad)
  Profile = -> Sketch135
  ReferenceAxis = -> Sketch135 [N_Axis]
  Refine = true
  Suppressed = false
  Type = 0
FEATURE [PartDesign::Body] Body009  label="perno fermo switch - caricabatterie - grilletto"
  AllowCompound = false
  Group = -> [Sketch135,Pad030]
  Origin = -> Origin009
  Tip = -> Pad030
FEATURE [Sketcher::SketchObject] Sketch136  label="scavo_rele"
  ArcFitTolerance = 1e-06
  AttachmentSupport = -> [XZ_Plane]
  ExternalGeometry = -> [Sketch]
  FullyConstrained = true
  MakeInternals = false
  MapMode = 5
  Placement = pos=(0,0,0) rot=(1,0,0;1.5708rad)
  sketch-geometry (7):
    g0: LineSegment [constr] StartX=-172.456 StartY=-60.9321 StartZ=0 EndX=-176.597 EndY=-73.6763 EndZ=0
    g1: LineSegment [constr] StartX=-172.456 StartY=-60.9321 StartZ=0 EndX=-170.364 EndY=-61.612 EndZ=0
    g2: LineSegment [constr] StartX=-172.456 StartY=-60.9321 StartZ=0 EndX=-176.07 EndY=-59.7579 EndZ=0
    g3: LineSegment StartX=-176.07 StartY=-59.7579 StartZ=0 EndX=-170.364 EndY=-61.612 EndZ=0
    g4: LineSegment StartX=-176.07 StartY=-59.7579 StartZ=0 EndX=-180.211 EndY=-72.502 EndZ=0
    g5: LineSegment StartX=-170.364 StartY=-61.612 StartZ=0 EndX=-174.505 EndY=-74.3561 EndZ=0
    g6: LineSegment StartX=-180.211 StartY=-72.502 StartZ=0 EndX=-174.505 EndY=-74.3561 EndZ=0
  constraints (19):
    c: Tangent(g0,g-3)
    c: Distance(g0,g-3) = 87.2
    c: Distance(g0,g0) = 13.4
    c: Coincident(g1,g0)
    c: Coincident(g2,g0)
    c: Distance(g2) = 3.8
    c: Distance(g1) = 2.2
    c: Perpendicular(g0,g1)
    c: Perpendicular(g0,g2)
    c: Coincident(g3,g2)
    c: Coincident(g3,g1)
    c: Equal(g4,g0)
    c: Equal(g5,g0)
    c: Parallel(g4,g0)
    c: Parallel(g5,g0)
    c: Coincident(g4,g2)
    c: Coincident(g5,g1)
    c: Coincident(g6,g4)
    c: Coincident(g6,g5)
FEATURE [Part::Extrusion] Extrude076  label="Extrude076 - scavo_rele"
  Base = -> Sketch136
  Dir = (0,-1,2e-16)
  DirMode = 2
  FaceMakerClass = Part::FaceMakerBullseye
  FaceMakerMode = 3
  LengthFwd = 18.2
  LengthRev = 0
  Solid = true
  Symmetric = true
FEATURE [Sketcher::SketchObject] Sketch137  label="scavo_nuovo_driver"
  ArcFitTolerance = 1e-06
  AttachmentSupport = -> [XZ_Plane]
  ExternalGeometry = -> [Sketch]
  FullyConstrained = true
  MakeInternals = false
  MapMode = 5
  Placement = pos=(0,0,0) rot=(1,0,0;1.5708rad)
  sketch-geometry (7):
    g0: LineSegment [constr] StartX=-160.034 StartY=-22.6997 StartZ=0 EndX=-164.854 EndY=-37.5361 EndZ=0
    g1: LineSegment [constr] StartX=-160.034 StartY=-22.6997 StartZ=0 EndX=-156.99 EndY=-23.6885 EndZ=0
    g2: LineSegment [constr] StartX=-160.034 StartY=-22.6997 StartZ=0 EndX=-163.648 EndY=-21.5254 EndZ=0
    g3: LineSegment StartX=-163.648 StartY=-21.5254 StartZ=0 EndX=-156.99 EndY=-23.6885 EndZ=0
    g4: LineSegment StartX=-163.648 StartY=-21.5254 StartZ=0 EndX=-168.468 EndY=-36.3619 EndZ=0
    g5: LineSegment StartX=-156.99 StartY=-23.6885 StartZ=0 EndX=-161.811 EndY=-38.525 EndZ=0
    g6: LineSegment StartX=-168.468 StartY=-36.3619 StartZ=0 EndX=-161.811 EndY=-38.525 EndZ=0
  constraints (19):
    c: Distance(g0,g-3) = 47
    c: Distance(g0) = 15.6
    c: Tangent(g0,g-3)
    c: Coincident(g1,g0)
    c: Coincident(g2,g0)
    c: Distance(g1) = 3.2
    c: Distance(g2) = 3.8
    c: Perpendicular(g0,g1)
    c: Perpendicular(g0,g2)
    c: Coincident(g3,g2)
    c: Coincident(g3,g1)
    c: Equal(g4,g0)
    c: Equal(g5,g0)
    c: Parallel(g4,g0)
    c: Parallel(g5,g0)
    c: Coincident(g4,g2)
    c: Coincident(g5,g1)
    c: Coincident(g6,g4)
    c: Coincident(g6,g5)
FEATURE [Part::Extrusion] Extrude077  label="Extrude077 - scavo_nuovo_driver"
  Base = -> Sketch137
  Dir = (0,-1,2e-16)
  DirMode = 2
  FaceMakerClass = Part::FaceMakerBullseye
  FaceMakerMode = 3
  LengthFwd = 20.8
  LengthRev = 0
  Solid = true
  Symmetric = true
FEATURE [Sketcher::SketchObject] Sketch138  label="scavo_nuovo_driver_alto"
  ArcFitTolerance = 1e-06
  AttachmentSupport = -> [XZ_Plane]
  ExternalGeometry = -> [Sketch]
  FullyConstrained = true
  MakeInternals = false
  MapMode = 5
  Placement = pos=(0,0,0) rot=(1,0,0;1.5708rad)
  sketch-geometry (7):
    g0: LineSegment [constr] StartX=-188.917 StartY=18.1185 StartZ=0 EndX=-187.75 EndY=4.97025 EndZ=0
    g1: LineSegment StartX=-187.75 StartY=4.97025 StartZ=0 EndX=-189.742 EndY=4.79337 EndZ=0
    g2: LineSegment StartX=-187.75 StartY=4.97025 StartZ=0 EndX=-182.769 EndY=5.41245 EndZ=0
    g3: LineSegment StartX=-190.909 StartY=17.9416 StartZ=0 EndX=-189.742 EndY=4.79337 EndZ=0
    g4: LineSegment StartX=-183.937 StartY=18.5607 StartZ=0 EndX=-182.769 EndY=5.41245 EndZ=0
    g5: LineSegment StartX=-190.909 StartY=17.9416 StartZ=0 EndX=-188.917 EndY=18.1185 EndZ=0
    g6: LineSegment StartX=-188.917 StartY=18.1185 StartZ=0 EndX=-183.937 EndY=18.5607 EndZ=0
  constraints (20):
    c: Distance(g0) = 13.2
    c: DistanceY(g-3,g0) = 9
    c: PointOnObject(g0,g-4)
    c: PointOnObject(g0,g-4)
    c: Coincident(g1,g0)
    c: Coincident(g2,g0)
    c: Distance(g1) = 2
    c: Distance(g2) = 5
    c: Perpendicular(g0,g1)
    c: Perpendicular(g0,g2)
    c: Equal(g3,g0)
    c: Parallel(g3,g0)
    c: Coincident(g3,g1)
    c: Equal(g4,g0)
    c: Parallel(g4,g0)
    c: Coincident(g4,g2)
    c: Coincident(g5,g3)
    c: Coincident(g5,g0)
    c: Coincident(g6,g0)
    c: Coincident(g6,g4)
FEATURE [Part::Extrusion] Extrude078  label="Extrude078 - scavo_nuovo_driver_alto"
  Base = -> Sketch138
  Dir = (0,-1,2e-16)
  DirMode = 2
  FaceMakerClass = Part::FaceMakerBullseye
  FaceMakerMode = 3
  LengthFwd = 17.2
  LengthRev = 0
  Solid = true
  Symmetric = true
FEATURE [Sketcher::SketchObject] Sketch139  label="fermi_nuovo_driver_alto"
  ArcFitTolerance = 1e-06
  AttachmentSupport = -> [XZ_Plane]
  ExternalGeometry = -> [Sketch138,Sketch]
  FullyConstrained = true
  MakeInternals = false
  MapMode = 5
  Placement = pos=(0,0,0) rot=(1,0,0;1.5708rad)
  sketch-geometry (17):
    g0: LineSegment [constr] StartX=-188.41 StartY=16.8018 StartZ=0 EndX=-187.948 EndY=14.1416 EndZ=0
    g1: LineSegment [constr] StartX=-187.948 StartY=14.1416 StartZ=0 EndX=-187.486 EndY=11.4815 EndZ=0
    g2: LineSegment StartX=-187.948 StartY=14.1416 StartZ=0 EndX=-187.76 EndY=13.0579 EndZ=0
    g3: LineSegment StartX=-187.948 StartY=14.1416 StartZ=0 EndX=-188.136 EndY=15.2254 EndZ=0
    g4: LineSegment StartX=-187.76 StartY=13.0579 StartZ=0 EndX=-185.592 EndY=13.4346 EndZ=0
    g5: LineSegment StartX=-188.136 StartY=15.2254 StartZ=0 EndX=-185.969 EndY=15.6021 EndZ=0
    g6: LineSegment StartX=-185.969 StartY=15.6021 StartZ=0 EndX=-185.592 EndY=13.4346 EndZ=0
    g7: LineSegment StartX=-187.486 StartY=11.4815 StartZ=0 EndX=-189.062 EndY=11.2075 EndZ=0
    g8: LineSegment StartX=-188.41 StartY=16.8018 StartZ=0 EndX=-189.987 EndY=16.5278 EndZ=0
    g9: LineSegment StartX=-189.987 StartY=16.5278 StartZ=0 EndX=-189.062 EndY=11.2075 EndZ=0
    g10: LineSegment StartX=-187.486 StartY=11.4815 StartZ=0 EndX=-185.318 EndY=11.8582 EndZ=0
    g11: LineSegment StartX=-188.41 StartY=16.8018 StartZ=0 EndX=-186.243 EndY=17.1785 EndZ=0
    g12: LineSegment StartX=-184.393 StartY=15.8761 StartZ=0 EndX=-184.016 EndY=13.7086 EndZ=0
    g13: ArcOfCircle CenterX=-185.969 CenterY=15.6021 CenterZ=0 NormalX=0 NormalY=0 NormalZ=1 AngleXU=0 Radius=1.6 StartAngle=0.172085 EndAngle=1.74288
    g14: GeomPoint [constr] X=-184.667 Y=17.4525 Z=0
    g15: ArcOfCircle CenterX=-185.592 CenterY=13.4346 CenterZ=0 NormalX=0 NormalY=0 NormalZ=1 AngleXU=0 Radius=1.6 StartAngle=4.88447 EndAngle=6.45527
    g16: GeomPoint [constr] X=-183.742 Y=12.1322 Z=0
  constraints (43):
    c: Tangent(g1,g0) = -1.5708
    c: Distance(g0) = 2.7
    c: Equal(g1,g0)
    c: Tangent(g1,g-5)
    c: Coincident(g2,g0)
    c: Coincident(g3,g0)
    c: Distance(g2) = 1.1
    c: Equal(g3,g2)
    c: PointOnObject(g3,g2)
    c: Coincident(g4,g2)
    c: Coincident(g5,g3)
    c: Distance(g4) = 2.2
    c: Equal(g4,g5)
    c: Perpendicular(g1,g4)
    c: Perpendicular(g0,g5)
    c: Coincident(g6,g5)
    c: Coincident(g6,g4)
    c: Coincident(g7,g1)
    c: Coincident(g8,g0)
    c: Distance(g7) = 1.6
    c: Equal(g7,g8)
    c: Perpendicular(g1,g7)
    c: Perpendicular(g8,g0)
    c: Coincident(g9,g8)
    c: Coincident(g9,g7)
    c: Coincident(g10,g1)
    c: Coincident(g11,g0)
    c: Distance(g10,g16) = 3.8
    c: Perpendicular(g1,g10)
    c: Perpendicular(g1,g11)
    c: DistanceY(g0,g-4) = 3.8
    c: PointOnObject(g14,g12)
    c: PointOnObject(g14,g11)
    c: Tangent(g12,g13) = 1.5708
    c: Tangent(g11,g13) = 1.5708
    c: PointOnObject(g16,g12)
    c: PointOnObject(g16,g10)
    c: Tangent(g12,g15) = 1.5708
    c: Tangent(g10,g15) = -1.5708
    c: Equal(g13,g15)
    c: Coincident(g13,g5)
    c: Parallel(g2,g0)
    c: PointOnObject(g0,g-5)
FEATURE [Part::Extrusion] Extrude079  label="Extrude079 - fermi_nuovo_driver_alto"
  Base = -> Sketch139
  Dir = (0,-1,2e-16)
  DirMode = 2
  FaceMakerClass = Part::FaceMakerBullseye
  FaceMakerMode = 3
  LengthFwd = 25.2
  LengthRev = 0
  Solid = true
  Symmetric = true
FEATURE [Sketcher::SketchObject] Sketch140  label="scavo_diodo_nuovo_driver_alto"
  ArcFitTolerance = 1e-06
  AttachmentSupport = -> [XZ_Plane]
  ExternalGeometry = -> [Sketch138]
  FullyConstrained = true
  MakeInternals = false
  MapMode = 5
  Placement = pos=(0,0,0) rot=(1,0,0;1.5708rad)
  sketch-geometry (4):
    g0: LineSegment StartX=-190.909 StartY=17.9416 StartZ=0 EndX=-189.742 EndY=4.79337 EndZ=0
    g1: LineSegment StartX=-193.898 StartY=17.6763 StartZ=0 EndX=-192.73 EndY=4.52805 EndZ=0
    g2: LineSegment StartX=-190.909 StartY=17.9416 StartZ=0 EndX=-193.898 EndY=17.6763 EndZ=0
    g3: LineSegment StartX=-192.73 StartY=4.52805 StartZ=0 EndX=-189.742 EndY=4.79337 EndZ=0
  constraints (11):
    c: Equal(g0,g-3)
    c: Parallel(g0,g-3)
    c: Equal(g1,g-3)
    c: Parallel(g1,g-3)
    c: Coincident(g2,g0)
    c: Distance(g2) = 3
    c: Perpendicular(g0,g2)
    c: Coincident(g1,g2)
    c: Coincident(g3,g1)
    c: Coincident(g3,g0)
    c: Coincident(g0,g-3)
FEATURE [Part::Extrusion] Extrude080  label="Extrude080 - scavo_diodo_nuovo_driver_alto"
  Base = -> Sketch140
  Dir = (0,-1,2e-16)
  DirMode = 2
  FaceMakerClass = Part::FaceMakerBullseye
  FaceMakerMode = 3
  LengthFwd = 4
  LengthRev = 0
  Placement = pos=(0,7.8,0) rot=(0,0,1;0rad)
  Solid = true
  Symmetric = false
FEATURE [Part::MultiFuse] Fusion001
  Refine = true
  Shapes = -> [Cut043,Extrude079]
FEATURE [Part::Cut] Cut044
  Base = -> Fusion001
  Refine = true
  Tool = -> Extrude078
FEATURE [Part::Cut] Cut045
  Base = -> Cut044
  Refine = true
  Tool = -> Extrude080
FEATURE [Sketcher::SketchObject] Sketch141  label="fermi_nuovo_driver"
  ArcFitTolerance = 1e-06
  AttachmentSupport = -> [XZ_Plane]
  ExternalGeometry = -> [Sketch,Sketch137]
  FullyConstrained = true
  MakeInternals = false
  MapMode = 5
  Placement = pos=(0,0,0) rot=(1,0,0;1.5708rad)
  sketch-geometry (17):
    g0: LineSegment [constr] StartX=-156.99 StartY=-23.6885 StartZ=0 EndX=-160.034 EndY=-22.6997 EndZ=0
    g1: LineSegment [constr] StartX=-160.034 StartY=-22.6997 StartZ=0 EndX=-162.815 EndY=-31.2592 EndZ=0
    g2: LineSegment [constr] StartX=-162.815 StartY=-31.2592 StartZ=0 EndX=-164.484 EndY=-36.3949 EndZ=0
    g3: LineSegment StartX=-164.484 StartY=-36.3949 StartZ=0 EndX=-166.576 EndY=-35.715 EndZ=0
    g4: LineSegment StartX=-167.603 StartY=-33.6989 StartZ=0 EndX=-166.923 EndY=-31.6066 EndZ=0
    g5: LineSegment StartX=-164.907 StartY=-30.5793 StartZ=0 EndX=-161.293 EndY=-31.7536 EndZ=0
    g6: LineSegment StartX=-161.293 StartY=-31.7536 StartZ=0 EndX=-162.962 EndY=-36.8893 EndZ=0
    g7: LineSegment StartX=-164.484 StartY=-36.3949 StartZ=0 EndX=-162.962 EndY=-36.8893 EndZ=0
    g8: LineSegment StartX=-165.402 StartY=-32.101 StartZ=0 EndX=-166.082 EndY=-34.1933 EndZ=0
    g9: LineSegment StartX=-166.082 StartY=-34.1933 StartZ=0 EndX=-163.989 EndY=-34.8732 EndZ=0
    g10: LineSegment StartX=-163.989 StartY=-34.8732 StartZ=0 EndX=-163.309 EndY=-32.7809 EndZ=0
    g11: LineSegment StartX=-163.309 StartY=-32.7809 StartZ=0 EndX=-165.402 EndY=-32.101 EndZ=0
    g12: ArcOfCircle CenterX=-165.402 CenterY=-32.101 CenterZ=0 NormalX=0 NormalY=0 NormalZ=1 AngleXU=0 Radius=1.6 StartAngle=1.25664 EndAngle=2.82743
    g13: GeomPoint [constr] X=-166.429 Y=-30.0849 Z=0
    g14: ArcOfCircle CenterX=-166.082 CenterY=-34.1933 CenterZ=0 NormalX=0 NormalY=0 NormalZ=1 AngleXU=0 Radius=1.6 StartAngle=2.82743 EndAngle=4.39823
    g15: GeomPoint [constr] X=-168.098 Y=-35.2206 Z=0
    g16: LineSegment [constr] StartX=-160.034 StartY=-22.6997 StartZ=0 EndX=-164.854 EndY=-37.5361 EndZ=0
  constraints (44):
    c: Coincident(g0,g-4)
    c: PointOnObject(g0,g-3)
    c: Parallel(g0,g-4)
    c: Coincident(g1,g0)
    c: Parallel(g1,g-3)
    c: Coincident(g2,g1)
    c: Distance(g2) = 5.4
    c: Coincident(g3,g2)
    c: Parallel(g2,g-3)
    c: Distance(g15,g13) = 5.4
    c: Perpendicular(g3,g2)
    c: Parallel(g4,g2)
    c: Distance(g5,g13) = 5.4
    c: Distance(g3,g15) = 3.8
    c: Perpendicular(g4,g5)
    c: Coincident(g6,g5)
    c: Distance(g6) = 5.4
    c: Parallel(g6,g4)
    c: Coincident(g7,g2)
    c: Coincident(g7,g6)
    c: Coincident(g8,g9)
    c: Coincident(g9,g10)
    c: Coincident(g10,g11)
    c: Coincident(g11,g8)
    c: Distance(g8,g10) = 2.2
    c: Distance(g9,g11) = 2.2
    c: Perpendicular(g11,g8)
    c: Equal(g8,g10)
    c: Equal(g11,g9)
    c: Tangent(g10,g2)
    c: Distance(g10,g1) = 1.6
    c: PointOnObject(g13,g4)
    c: PointOnObject(g13,g5)
    c: Tangent(g4,g12) = 1.5708
    c: Tangent(g5,g12) = 1.5708
    c: PointOnObject(g15,g4)
    c: Tangent(g4,g14) = 1.5708
    c: Tangent(g3,g14) = 1.5708
    c: Equal(g14,g12)
    c: Coincident(g12,g8)
    c: Coincident(g16,g0)
    c: PointOnObject(g16,g-5)
    c: Parallel(g16,g-3)
    c: Distance(g16,g2) = 1.2
FEATURE [Part::Extrusion] Extrude081  label="Extrude081 - fermi_nuovo_driver"
  Base = -> Sketch141
  Dir = (0,-1,2e-16)
  DirMode = 2
  FaceMakerClass = Part::FaceMakerBullseye
  FaceMakerMode = 3
  LengthFwd = 25.2
  LengthRev = 0
  Solid = true
  Symmetric = true
FEATURE [Part::MultiFuse] Fusion002
  Refine = true
  Shapes = -> [Cut045,Extrude081]
FEATURE [Part::Cut] Cut046
  Base = -> Fusion002
  Refine = true
  Tool = -> Extrude077
FEATURE [Sketcher::SketchObject] Sketch142  label="fermi_rele"
  ArcFitTolerance = 1e-06
  AttachmentSupport = -> [XZ_Plane]
  ExternalGeometry = -> [Sketch,Sketch136]
  FullyConstrained = true
  MakeInternals = false
  MapMode = 5
  Placement = pos=(0,0,0) rot=(1,0,0;1.5708rad)
  sketch-geometry (15):
    g0: LineSegment StartX=-176.936 StartY=-62.4208 StartZ=0 EndX=-177.615 EndY=-64.5131 EndZ=0
    g1: LineSegment StartX=-174.919 StartY=-61.3936 StartZ=0 EndX=-171.305 EndY=-62.5678 EndZ=0
    g2: LineSegment StartX=-171.305 StartY=-62.5678 StartZ=0 EndX=-172.974 EndY=-67.7035 EndZ=0
    g3: LineSegment StartX=-176.588 StartY=-66.5293 StartZ=0 EndX=-172.974 EndY=-67.7035 EndZ=0
    g4: LineSegment StartX=-175.414 StartY=-62.9152 StartZ=0 EndX=-173.322 EndY=-63.5951 EndZ=0
    g5: LineSegment StartX=-175.414 StartY=-62.9152 StartZ=0 EndX=-176.094 EndY=-65.0076 EndZ=0
    g6: LineSegment StartX=-173.322 StartY=-63.5951 StartZ=0 EndX=-174.001 EndY=-65.6874 EndZ=0
    g7: LineSegment StartX=-176.094 StartY=-65.0076 StartZ=0 EndX=-174.001 EndY=-65.6874 EndZ=0
    g8: LineSegment [constr] StartX=-173.322 StartY=-63.5951 StartZ=0 EndX=-172.827 EndY=-62.0734 EndZ=0
    g9: LineSegment [constr] StartX=-173.322 StartY=-63.5951 StartZ=0 EndX=-171.8 EndY=-64.0895 EndZ=0
    g10: LineSegment [constr] StartX=-170.364 StartY=-61.612 StartZ=0 EndX=-172.456 EndY=-60.9321 EndZ=0
    g11: ArcOfCircle CenterX=-175.414 CenterY=-62.9152 CenterZ=0 NormalX=0 NormalY=0 NormalZ=1 AngleXU=0 Radius=1.6 StartAngle=1.25664 EndAngle=2.82743
    g12: GeomPoint [constr] X=-176.441 Y=-60.8991 Z=0
    g13: ArcOfCircle CenterX=-176.094 CenterY=-65.0076 CenterZ=0 NormalX=0 NormalY=0 NormalZ=1 AngleXU=0 Radius=1.6 StartAngle=2.82743 EndAngle=4.39823
    g14: GeomPoint [constr] X=-178.11 Y=-66.0348 Z=0
  constraints (39):
    c: Distance(g14,g12) = 5.4
    c: Distance(g1,g12) = 5.4
    c: Perpendicular(g1,g0)
    c: Coincident(g2,g1)
    c: Parallel(g2,g0)
    c: Coincident(g3,g2)
    c: Parallel(g2,g-3)
    c: Coincident(g5,g4)
    c: Distance(g5) = 2.2
    c: Distance(g4) = 2.2
    c: Perpendicular(g4,g5)
    c: Coincident(g6,g4)
    c: Equal(g6,g5)
    c: Parallel(g6,g5)
    c: Coincident(g7,g5)
    c: Coincident(g7,g6)
    c: Coincident(g8,g4)
    c: Coincident(g9,g4)
    c: Distance(g8) = 1.6
    c: Distance(g9) = 1.6
    c: Parallel(g8,g6)
    c: Parallel(g9,g4)
    c: PointOnObject(g8,g1)
    c: PointOnObject(g9,g2)
    c: Coincident(g10,g-4)
    c: Parallel(g10,g-4)
    c: PointOnObject(g10,g-3)
    c: Tangent(g6,g-3) = 1.5708
    c: Distance(g4,g10) = 2.8
    c: PointOnObject(g12,g1)
    c: Tangent(g1,g11) = 1.5708
    c: Tangent(g0,g11) = -1.5708
    c: PointOnObject(g14,g3)
    c: PointOnObject(g14,g0)
    c: Tangent(g3,g13) = -1.5708
    c: Tangent(g0,g13) = -1.5708
    c: Equal(g11,g13)
    c: Coincident(g11,g4)
    c: Parallel(g3,g1)
FEATURE [Part::Extrusion] Extrude082  label="Extrude082 - fermi_rele"
  Base = -> Sketch142
  Dir = (0,-1,2e-16)
  DirMode = 2
  FaceMakerClass = Part::FaceMakerBullseye
  FaceMakerMode = 3
  LengthFwd = 25.2
  LengthRev = 0
  Solid = true
  Symmetric = true
FEATURE [Part::MultiFuse] Fusion003
  Refine = true
  Shapes = -> [Cut046,Extrude082]
FEATURE [Part::Cut] Cut047
  Base = -> Fusion003
  Refine = true
  Tool = -> Extrude076
FEATURE [Sketcher::SketchObject] Sketch143  label="foro_passaggio_cavi_led_batteria"
  ArcFitTolerance = 1e-06
  AttachmentSupport = -> [XZ_Plane]
  ExternalGeometry = -> [Sketch,Sketch042,Sketch036]
  FullyConstrained = true
  MakeInternals = false
  MapMode = 5
  Placement = pos=(0,0,0) rot=(1,0,0;1.5708rad)
  sketch-geometry (4):
    g0: LineSegment StartX=-207.775 StartY=-41.3701 StartZ=0 EndX=-213.607 EndY=-53.8767 EndZ=0
    g1: LineSegment StartX=-213.607 StartY=-53.8767 StartZ=0 EndX=-211.843 EndY=-59.5559 EndZ=0
    g2: LineSegment StartX=-207.775 StartY=-41.3701 StartZ=0 EndX=-207.775 EndY=-50.8316 EndZ=0
    g3: LineSegment StartX=-207.775 StartY=-50.8316 StartZ=0 EndX=-211.843 EndY=-59.5559 EndZ=0
  constraints (9):
    c: Coincident(g0,g-3)
    c: PointOnObject(g1,g-6)
    c: Coincident(g1,g0)
    c: Coincident(g2,g0)
    c: Coincident(g2,g-7)
    c: Coincident(g3,g2)
    c: Parallel(g3,g0)
    c: Coincident(g3,g1)
    c: Coincident(g0,g-5)
FEATURE [Part::Extrusion] Extrude083  label="Extrude083 - foro_passaggio_cavi_led_batteria"
  Base = -> Sketch143
  Dir = (0,-1,2e-16)
  DirMode = 2
  FaceMakerClass = Part::FaceMakerBullseye
  FaceMakerMode = 3
  LengthFwd = 6
  LengthRev = 0
  Placement = pos=(0,1.2,0) rot=(0,0,1;0rad)
  Solid = true
  Symmetric = true
FEATURE [Part::Cut] Cut048
  Base = -> Cut047
  Refine = true
  Tool = -> Extrude083
FEATURE [Sketcher::SketchObject] Sketch144  label="foro_areazione_alimentatore"
  ArcFitTolerance = 1e-06
  AttachmentSupport = -> [XZ_Plane]
  ExternalGeometry = -> [Sketch036]
  FullyConstrained = true
  MakeInternals = false
  MapMode = 5
  Placement = pos=(0,0,0) rot=(1,0,0;1.5708rad)
  sketch-geometry (4):
    g0: LineSegment StartX=-211.843 StartY=-60.3701 StartZ=0 EndX=-207.775 EndY=-60.3701 EndZ=0
    g1: LineSegment StartX=-207.775 StartY=-60.3701 StartZ=0 EndX=-207.775 EndY=-70.3701 EndZ=0
    g2: LineSegment StartX=-211.843 StartY=-60.3701 StartZ=0 EndX=-211.843 EndY=-70.3701 EndZ=0
    g3: LineSegment StartX=-207.775 StartY=-70.3701 StartZ=0 EndX=-211.843 EndY=-70.3701 EndZ=0
  constraints (11):
    c: Horizontal(g0)
    c: Distance(g1) = 10
    c: Coincident(g1,g0)
    c: Tangent(g1,g-3)
    c: PointOnObject(g0,g-4)
    c: Coincident(g2,g0)
    c: PointOnObject(g2,g-4)
    c: Coincident(g3,g1)
    c: Horizontal(g3)
    c: Coincident(g3,g2)
    c: DistanceY(g0,g-3) = 19
FEATURE [Part::Extrusion] Extrude084  label="Extrude084 - foro_areazione_alimentatore"
  Base = -> Sketch144
  Dir = (0,-1,2e-16)
  DirMode = 2
  FaceMakerClass = Part::FaceMakerBullseye
  FaceMakerMode = 3
  LengthFwd = 10
  LengthRev = 0
  Solid = true
  Symmetric = true
FEATURE [Part::Cut] Cut049
  Base = -> Cut048
  Refine = true
  Tool = -> Extrude084
FEATURE [Sketcher::SketchObject] Sketch145  label="foro_per_condesatore"
  ArcFitTolerance = 1e-06
  AttachmentSupport = -> [XZ_Plane]
  ExternalGeometry = -> [Sketch138]
  FullyConstrained = true
  MakeInternals = false
  MapMode = 5
  Placement = pos=(0,0,0) rot=(1,0,0;1.5708rad)
  sketch-geometry (1):
    g0: Circle CenterX=-179.742 CenterY=9.59337 CenterZ=0 NormalX=0 NormalY=0 NormalZ=1 AngleXU=0 Radius=5.4
  constraints (3):
    c: Diameter(g0) = 10.8
    c: DistanceX(g-3,g0) = 10
    c: DistanceY(g-3,g0) = 4.8
FEATURE [Part::Extrusion] Extrude085  label="Extrude085 - foro_per_condesatore"
  Base = -> Sketch145
  Dir = (0,-1,2e-16)
  DirMode = 2
  FaceMakerClass = Part::FaceMakerBullseye
  FaceMakerMode = 3
  LengthFwd = 25.2
  LengthRev = 0
  Solid = true
  Symmetric = true
FEATURE [Part::Cut] Cut050
  Base = -> Cut049
  Refine = true
  Tool = -> Extrude085
FEATURE [Sketcher::SketchObject] Sketch146  label="scavo_pulsante_6x6_per_led_batteria"
  ArcFitTolerance = 1e-06
  AttachmentSupport = -> [XZ_Plane]
  ExternalGeometry = -> [Sketch016]
  FullyConstrained = true
  MakeInternals = false
  MapMode = 5
  Placement = pos=(0,0,0) rot=(1,0,0;1.5708rad)
  sketch-geometry (5):
    g0: LineSegment StartX=-216.643 StartY=-65.8316 StartZ=0 EndX=-216.643 EndY=-72.8316 EndZ=0
    g1: LineSegment StartX=-216.643 StartY=-72.8316 StartZ=0 EndX=-210.243 EndY=-72.8316 EndZ=0
    g2: LineSegment StartX=-210.243 StartY=-72.8316 StartZ=0 EndX=-210.243 EndY=-65.8316 EndZ=0
    g3: LineSegment StartX=-210.243 StartY=-65.8316 StartZ=0 EndX=-216.643 EndY=-65.8316 EndZ=0
    g4: GeomPoint [constr] X=-213.443 Y=-69.3316 Z=0
  constraints (13):
    c: Coincident(g0,g1)
    c: Coincident(g1,g2)
    c: Coincident(g2,g3)
    c: Coincident(g3,g0)
    c: Vertical(g0)
    c: Vertical(g2)
    c: Horizontal(g1)
    c: Horizontal(g3)
    c: Distance(g0,g2) = 6.4
    c: Distance(g1,g3) = 7
    c: Tangent(g1,g-3)
    c: Symmetric(g0,g2,g4)
    c: Vertical(g-3,g4)
FEATURE [Part::Extrusion] Extrude086  label="Extrude086 - scavo_pulsante_6x6_per_led_batteria"
  Base = -> Sketch146
  Dir = (0,-1,2e-16)
  DirMode = 2
  FaceMakerClass = Part::FaceMakerBullseye
  FaceMakerMode = 3
  LengthFwd = 4
  LengthRev = 0
  Placement = pos=(0,12.6,0) rot=(0,0,1;0rad)
  Solid = true
  Symmetric = false
FEATURE [Sketcher::SketchObject] Sketch147  label="scavo_led_stato_batteria"
  ArcFitTolerance = 1e-06
  AttachmentSupport = -> [XZ_Plane]
  ExternalGeometry = -> [Sketch016]
  FullyConstrained = true
  MakeInternals = false
  MapMode = 5
  Placement = pos=(0,0,0) rot=(1,0,0;1.5708rad)
  sketch-geometry (5):
    g0: LineSegment StartX=-215.843 StartY=-56.2316 StartZ=0 EndX=-215.843 EndY=-65.4316 EndZ=0
    g1: LineSegment StartX=-215.843 StartY=-65.4316 StartZ=0 EndX=-211.043 EndY=-65.4316 EndZ=0
    g2: LineSegment StartX=-211.043 StartY=-65.4316 StartZ=0 EndX=-211.043 EndY=-56.2316 EndZ=0
    g3: LineSegment StartX=-211.043 StartY=-56.2316 StartZ=0 EndX=-215.843 EndY=-56.2316 EndZ=0
    g4: GeomPoint [constr] X=-213.443 Y=-60.8316 Z=0
  constraints (13):
    c: Coincident(g0,g1)
    c: Coincident(g1,g2)
    c: Coincident(g2,g3)
    c: Coincident(g3,g0)
    c: Distance(g0,g2) = 4.8
    c: Distance(g1,g3) = 9.2
    c: Equal(g0,g2)
    c: Equal(g1,g3)
    c: Perpendicular(g3,g0)
    c: DistanceY(g-3,g0) = 11.4
    c: Vertical(g2)
    c: Symmetric(g0,g2,g4)
    c: Vertical(g4,g-3)
FEATURE [Part::Extrusion] Extrude087  label="Extrude087 - scavo_led_stato_batteria"
  Base = -> Sketch147
  Dir = (0,-1,2e-16)
  DirMode = 2
  FaceMakerClass = Part::FaceMakerBullseye
  FaceMakerMode = 3
  LengthFwd = 2.2
  LengthRev = 0
  Placement = pos=(0,12.6,0) rot=(0,0,1;0rad)
  Solid = true
  Symmetric = false
FEATURE [Sketcher::SketchObject] Sketch148
  ArcFitTolerance = 1e-06
  AttachmentSupport = -> [Pad016]
  ExternalGeometry = -> [Pad016]
  FullyConstrained = true
  MakeInternals = false
  MapMode = 5
  Placement = pos=(0,0,-80.4316) rot=(1,0,0;3.14159rad)
  sketch-geometry (8):
    g0: LineSegment StartX=-176.685 StartY=3.6 StartZ=0 EndX=-186.685 EndY=3.6 EndZ=0
    g1: LineSegment StartX=-176.685 StartY=3.6 StartZ=0 EndX=-176.685 EndY=-9e-16 EndZ=0
    g2: LineSegment [constr] StartX=-186.685 StartY=3.6 StartZ=0 EndX=-186.685 EndY=-9e-16 EndZ=0
    g3: ArcOfEllipse CenterX=-186.685 CenterY=-9e-16 CenterZ=0 NormalX=0 NormalY=0 NormalZ=1 MajorRadius=10 MinorRadius=3.6 AngleXU=0 StartAngle=0 EndAngle=1.5708
    g4: LineSegment [constr] StartX=-176.685 StartY=-1e-15 StartZ=0 EndX=-196.685 EndY=-1e-15 EndZ=0
    g5: LineSegment [constr] StartX=-186.685 StartY=3.6 StartZ=0 EndX=-186.685 EndY=-3.6 EndZ=0
    g6: GeomPoint [constr] X=-177.356 Y=-1e-15 Z=0
    g7: GeomPoint [constr] X=-196.015 Y=-1e-15 Z=0
  constraints (13):
    c: Distance(g0) = 10
    c: Coincident(g0,g-5)
    c: PointOnObject(g0,g-3)
    c: Coincident(g1,g0)
    c: Coincident(g1,g-5)
    c: Coincident(g2,g0)
    c: Vertical(g2)
    c: PointOnObject(g2,g-4)
    c: InternalAlignment(g4-g7 -> g3) x4
    c: Coincident(g3,g2)
    c: Coincident(g3,g0)
    c: Coincident(g3,g1)
    c: Horizontal(g4)
FEATURE [PartDesign::SubtractivePipe] SubtractivePipe004
  AuxilleryCurvelinear = true
  AuxillerySpineTangent = false
  BaseFeature = -> Pad016
  Binormal = (0,0,0)
  Mode = 0
  Profile = -> Sketch148
  Refine = true
  Spine = -> Pad016 [Edge253]
  SpineTangent = false
  Suppressed = false
  Transformation = 0
  Transition = 0
FEATURE [Sketcher::SketchObject] Sketch149
  ArcFitTolerance = 1e-06
  AttachmentSupport = -> [Pad016]
  ExternalGeometry = -> [Pad016]
  FullyConstrained = true
  MakeInternals = false
  MapMode = 5
  Placement = pos=(0,0,-80.4316) rot=(1,0,0;3.14159rad)
  sketch-geometry (8):
    g0: LineSegment StartX=-215.932 StartY=3.6 StartZ=0 EndX=-205.932 EndY=3.6 EndZ=0
    g1: LineSegment StartX=-215.932 StartY=3.6 StartZ=0 EndX=-215.932 EndY=-4e-16 EndZ=0
    g2: LineSegment [constr] StartX=-205.932 StartY=3.6 StartZ=0 EndX=-205.932 EndY=-9e-16 EndZ=0
    g3: ArcOfEllipse CenterX=-205.932 CenterY=-1e-15 CenterZ=0 NormalX=0 NormalY=0 NormalZ=1 MajorRadius=10 MinorRadius=3.6 AngleXU=-3.14159 StartAngle=4.71239 EndAngle=6.28319
    g4: LineSegment [constr] StartX=-215.932 StartY=-1e-15 StartZ=0 EndX=-195.932 EndY=-1e-15 EndZ=0
    g5: LineSegment [constr] StartX=-205.932 StartY=-3.6 StartZ=0 EndX=-205.932 EndY=3.6 EndZ=0
    g6: GeomPoint [constr] X=-215.262 Y=-2.1e-15 Z=0
    g7: GeomPoint [constr] X=-196.602 Y=-9e-16 Z=0
  constraints (13):
    c: Distance(g0) = 10
    c: Coincident(g0,g-5)
    c: PointOnObject(g0,g-5)
    c: Coincident(g1,g0)
    c: Coincident(g1,g-4)
    c: Coincident(g2,g0)
    c: Vertical(g2)
    c: PointOnObject(g2,g-3)
    c: InternalAlignment(g4-g7 -> g3) x4
    c: Coincident(g3,g2)
    c: Coincident(g3,g0)
    c: Coincident(g3,g1)
    c: Horizontal(g4)
FEATURE [PartDesign::SubtractivePipe] SubtractivePipe005
  AuxilleryCurvelinear = true
  AuxillerySpineTangent = false
  BaseFeature = -> SubtractivePipe004
  Binormal = (0,0,0)
  Mode = 0
  Profile = -> Sketch149
  Refine = true
  Spine = -> Pad016 [Edge251,Edge256,Edge255]
  SpineTangent = false
  Suppressed = false
  Transformation = 0
  Transition = 0
FEATURE [PartDesign::SubtractiveLoft] SubtractiveLoft002
  BaseFeature = -> SubtractivePipe005
  Closed = false
  Profile = -> Sketch129
  Refine = true
  Ruled = false
  Sections = -> [Sketch130]
  Suppressed = false
FEATURE [PartDesign::SubtractiveLoft] SubtractiveLoft003
  BaseFeature = -> SubtractiveLoft002
  Closed = false
  Profile = -> Clone2D001
  Refine = true
  Ruled = false
  Sections = -> [Sketch131]
  Suppressed = false
FEATURE [PartDesign::Chamfer] Chamfer010
  Angle = 45
  Base = -> SubtractiveLoft003 [Edge203,Edge204,Edge202,Edge201,Edge195]
  BaseFeature = -> SubtractiveLoft003
  ChamferType = 0
  FlipDirection = false
  Refine = true
  Size = 1.5
  Size2 = 1
  SupportTransform = false
  Suppressed = false
  UseAllEdges = false
FEATURE [PartDesign::Chamfer] Chamfer011
  Angle = 45
  Base = -> Chamfer010 [Edge15]
  BaseFeature = -> Chamfer010
  ChamferType = 0
  FlipDirection = false
  Refine = true
  Size = 1.6
  Size2 = 1
  SupportTransform = false
  Suppressed = false
  UseAllEdges = false
FEATURE [PartDesign::Chamfer] Chamfer012
  Angle = 45
  Base = -> Chamfer011 [Edge10]
  BaseFeature = -> Chamfer011
  ChamferType = 0
  FlipDirection = false
  Refine = true
  Size = 3.5
  Size2 = 1
  SupportTransform = false
  Suppressed = false
  UseAllEdges = false
FEATURE [PartDesign::Chamfer] Chamfer013
  Angle = 45
  Base = -> Chamfer012 [Edge94]
  BaseFeature = -> Chamfer012
  ChamferType = 0
  FlipDirection = false
  Refine = true
  Size = 1.9
  Size2 = 1
  SupportTransform = false
  Suppressed = false
  UseAllEdges = false
FEATURE [PartDesign::Fillet] Fillet007
  Base = -> Chamfer013 [Edge83]
  BaseFeature = -> Chamfer013
  Radius = 1.1
  Refine = true
  SupportTransform = false
  Suppressed = false
  UseAllEdges = false
FEATURE [PartDesign::Fillet] Fillet008
  Base = -> Fillet007 [Edge75]
  BaseFeature = -> Fillet007
  Radius = 1.9
  Refine = true
  SupportTransform = false
  Suppressed = false
  UseAllEdges = false
FEATURE [PartDesign::Pocket] Pocket011
  BaseFeature = -> Fillet008
  Direction = (0,1,-2e-16)
  Length = 0.8
  Length2 = 5
  Profile = -> Sketch132
  ReferenceAxis = -> Sketch132 [N_Axis]
  Refine = true
  Suppressed = false
  Type = 0
FEATURE [PartDesign::Pocket] Pocket012
  BaseFeature = -> Pocket011
  Direction = (0,1,0)
  Length = 1
  Length2 = 5
  Profile = -> ShapeString
  ReferenceAxis = -> ShapeString [N_Axis]
  Refine = true
  Suppressed = false
  Type = 0
FEATURE [Sketcher::SketchObject] Sketch150
  ArcFitTolerance = 1e-06
  AttachmentSupport = -> [Pad008]
  ExternalGeometry = -> [Pad008]
  FullyConstrained = true
  MakeInternals = false
  MapMode = 5
  Placement = pos=(0,3.6,0) rot=(0,0.707107,0.707107;3.14159rad)
  sketch-geometry (7):
    g0: LineSegment [constr] StartX=210.343 StartY=-66.0316 StartZ=0 EndX=210.343 EndY=-72.8316 EndZ=0
    g1: LineSegment [constr] StartX=210.343 StartY=-72.8316 StartZ=0 EndX=216.543 EndY=-72.8316 EndZ=0
    g2: LineSegment [constr] StartX=216.543 StartY=-72.8316 StartZ=0 EndX=216.543 EndY=-66.0316 EndZ=0
    g3: LineSegment [constr] StartX=216.543 StartY=-66.0316 StartZ=0 EndX=210.343 EndY=-66.0316 EndZ=0
    g4: LineSegment [constr] StartX=210.343 StartY=-72.8316 StartZ=0 EndX=216.543 EndY=-66.0316 EndZ=0
    g5: LineSegment [constr] StartX=210.343 StartY=-66.0316 StartZ=0 EndX=213.443 EndY=-69.4316 EndZ=0
    g6: Circle CenterX=213.443 CenterY=-69.4316 CenterZ=0 NormalX=0 NormalY=0 NormalZ=1 AngleXU=0 Radius=2
  constraints (18):
    c: Coincident(g0,g1)
    c: Coincident(g1,g2)
    c: Coincident(g2,g3)
    c: Coincident(g3,g0)
    c: Vertical(g0)
    c: Vertical(g2)
    c: Horizontal(g1)
    c: Horizontal(g3)
    c: Distance(g0,g2) = 6.2
    c: Distance(g1,g3) = 6.8
    c: DistanceY(g-3,g1) = 4
    c: Coincident(g4,g0)
    c: Coincident(g4,g2)
    c: Coincident(g5,g0)
    c: Symmetric(g0,g2,g5)
    c: Diameter(g6) = 4
    c: Coincident(g6,g5)
    c: Vertical(g5,g-3)
FEATURE [Sketcher::SketchObject] Sketch151
  ArcFitTolerance = 1e-06
  AttachmentSupport = -> [Pad008]
  ExternalGeometry = -> [Pad008]
  FullyConstrained = true
  MakeInternals = false
  MapMode = 5
  Placement = pos=(0,3.6,0) rot=(0,0.707107,0.707107;3.14159rad)
  sketch-geometry (10):
    g0: LineSegment [constr] StartX=211.143 StartY=-56.2316 StartZ=0 EndX=211.143 EndY=-65.4316 EndZ=0
    g1: LineSegment [constr] StartX=211.143 StartY=-65.4316 StartZ=0 EndX=215.743 EndY=-65.4316 EndZ=0
    g2: LineSegment [constr] StartX=215.743 StartY=-65.4316 StartZ=0 EndX=215.743 EndY=-56.2316 EndZ=0
    g3: LineSegment [constr] StartX=215.743 StartY=-56.2316 StartZ=0 EndX=211.143 EndY=-56.2316 EndZ=0
    g4: LineSegment StartX=212.243 StartY=-63.8316 StartZ=0 EndX=214.643 EndY=-63.8316 EndZ=0
    g5: LineSegment StartX=214.643 StartY=-63.8316 StartZ=0 EndX=214.643 EndY=-57.0316 EndZ=0
    g6: LineSegment StartX=214.643 StartY=-57.0316 StartZ=0 EndX=212.243 EndY=-57.0316 EndZ=0
    g7: LineSegment StartX=212.243 StartY=-57.0316 StartZ=0 EndX=212.243 EndY=-63.8316 EndZ=0
    g8: GeomPoint [constr] X=213.443 Y=-60.4316 Z=0
    g9: GeomPoint [constr] X=213.443 Y=-60.8316 Z=0
  constraints (26):
    c: Coincident(g0,g1)
    c: Coincident(g1,g2)
    c: Coincident(g2,g3)
    c: Coincident(g3,g0)
    c: Vertical(g0)
    c: Vertical(g2)
    c: Horizontal(g1)
    c: Horizontal(g3)
    c: Distance(g0,g2) = 4.6
    c: Distance(g1,g3) = 9.2
    c: DistanceY(g-3,g1) = 11.4
    c: Coincident(g4,g5)
    c: Coincident(g5,g6)
    c: Coincident(g6,g7)
    c: Coincident(g7,g4)
    c: Horizontal(g4)
    c: Horizontal(g6)
    c: Vertical(g5)
    c: Vertical(g7)
    c: Symmetric(g6,g4,g8)
    c: Distance(g5,g7) = 2.4
    c: Distance(g4,g6) = 6.8
    c: Symmetric(g2,g0,g9)
    c: Vertical(g8,g9)
    c: DistanceY(g1,g4) = 1.6
    c: Vertical(g9,g-3)
FEATURE [PartDesign::Pocket] Pocket019
  BaseFeature = -> Pocket013
  Direction = (0,-1,2e-16)
  Length = 3.6
  Length2 = 5
  Profile = -> Sketch151
  ReferenceAxis = -> Sketch151 [N_Axis]
  Refine = true
  Suppressed = false
  Type = 0
FEATURE [PartDesign::Pocket] Pocket018
  BaseFeature = -> Pocket019
  Direction = (0,-1,2e-16)
  Length = 3.6
  Length2 = 5
  Profile = -> Sketch150
  ReferenceAxis = -> Sketch150 [N_Axis]
  Refine = true
  Suppressed = false
  Type = 0
FEATURE [PartDesign::Point] DatumPoint
  AttacherType = Attacher::AttachEnginePoint
  AttachmentSupport = -> [Sketch150]
  MapMode = 36
  Placement = pos=(-213.443,3.6,-69.4316) rot=(0,1,0;3.14159rad)
FEATURE [PartDesign::Plane] DatumPlane002
  AttachmentSupport = -> [DatumPoint]
  Length = 265.655
  MapMode = 1
  Placement = pos=(-213.443,3.6,-69.4316) rot=(0,0,1;0rad)
  ResizeMode = 0
  Width = 72.0719
FEATURE [Sketcher::SketchObject] Sketch152
  ArcFitTolerance = 1e-06
  AttachmentSupport = -> [DatumPlane002]
  ExternalGeometry = -> [Sketch150]
  FullyConstrained = true
  MakeInternals = false
  MapMode = 5
  Placement = pos=(-213.443,3.6,-69.4316) rot=(0,0,1;0rad)
  sketch-geometry (7):
    g0: LineSegment StartX=0 StartY=0 StartZ=0 EndX=-4 EndY=5.1e-15 EndZ=0
    g1: ArcOfEllipse CenterX=0 CenterY=0 CenterZ=0 NormalX=0 NormalY=0 NormalZ=1 MajorRadius=4 MinorRadius=3.6 AngleXU=3.14159 StartAngle=2e-16 EndAngle=1.5708
    g2: LineSegment [constr] StartX=-4 StartY=9e-16 StartZ=0 EndX=4 EndY=-9e-16 EndZ=0
    g3: LineSegment [constr] StartX=0 StartY=-3.6 StartZ=0 EndX=0 EndY=3.6 EndZ=0
    g4: GeomPoint [constr] X=-1.74356 Y=2.5e-15 Z=0
    g5: GeomPoint [constr] X=1.74356 Y=-2e-15 Z=0
    g6: LineSegment StartX=0 StartY=0 StartZ=0 EndX=-5.5e-15 EndY=-3.6 EndZ=0
  constraints (11):
    c: PointOnObject(g1,g-2)
    c: Distance(g0) = 4
    c: PointOnObject(g0,g-1)
    c: InternalAlignment(g2-g5 -> g1) x4
    c: Coincident(g1,g0)
    c: Vertical(g3)
    c: Coincident(g1,g-1)
    c: Distance(g6) = 3.6
    c: Coincident(g6,g1)
    c: Coincident(g1,g6)
    c: Coincident(g0,g1)
FEATURE [PartDesign::Groove] Groove
  Angle = 360
  Angle2 = 60
  Axis = (0,1,0)
  Base = (-213.443,3.6,-69.4316)
  BaseFeature = -> Pocket018
  Profile = -> Sketch152
  ReferenceAxis = -> Sketch152 [V_Axis]
  Refine = true
  Reversed = true
  Suppressed = false
  Type = 0
FEATURE [PartDesign::Body] Body006  label="lato SX"
  AllowCompound = false
  Group = -> [Binder,Pad019,Chamfer015,Pocket002,Sketch133,Sketch091,Pad005,Sketch092,Pocket001,Sketch093,Sketch094,Pad006,Sketch095,Pad007,Sketch096,Pad008,Sketch097,Pad009,Chamfer005,Pocket004,Sketch098,Pad010,Chamfer006,Pocket003,SubtractivePipe,SubtractivePipe001,Sketch099,Sketch106,Sketch107,Sketch108,Clone2D,Sketch109,SubtractiveLoft,SubtractiveLoft001,Sketch110,Sketch111,Sketch112,Chamfer016,Chamfer017,+15 more]
  Origin = -> Origin006
  Tip = -> Groove
FEATURE [Sketcher::SketchObject] Sketch153  label="ripieno_per_sostegno_led_batteria"
  ArcFitTolerance = 1e-06
  AttachmentSupport = -> [XZ_Plane]
  ExternalGeometry = -> [Sketch036]
  FullyConstrained = true
  MakeInternals = false
  MapMode = 5
  Placement = pos=(0,0,0) rot=(1,0,0;1.5708rad)
  sketch-geometry (4):
    g0: LineSegment StartX=-217.343 StartY=-54.5944 StartZ=0 EndX=-217.343 EndY=-63.1944 EndZ=0
    g1: LineSegment StartX=-217.343 StartY=-63.1944 StartZ=0 EndX=-211.843 EndY=-63.1944 EndZ=0
    g2: LineSegment StartX=-211.843 StartY=-63.1944 StartZ=0 EndX=-211.843 EndY=-54.5944 EndZ=0
    g3: LineSegment StartX=-211.843 StartY=-54.5944 StartZ=0 EndX=-217.343 EndY=-54.5944 EndZ=0
  constraints (11):
    c: Coincident(g0,g1)
    c: Coincident(g1,g2)
    c: Coincident(g2,g3)
    c: Coincident(g3,g0)
    c: Vertical(g0)
    c: Horizontal(g1)
    c: Horizontal(g3)
    c: Tangent(g2,g-3)
    c: DistanceY(g2,g-3) = 4.5
    c: DistanceX(g3,g3) = 5.5
    c: DistanceY(g0,g0) = 8.6
FEATURE [Part::Extrusion] Extrude088  label="Extrude088 - ripieno_per_sostegno_led_batteria"
  Base = -> Sketch153
  Dir = (0,-1,2e-16)
  DirMode = 2
  FaceMakerClass = Part::FaceMakerBullseye
  FaceMakerMode = 3
  LengthFwd = 4
  LengthRev = 0
  Placement = pos=(0,12.6,0) rot=(0,0,1;0rad)
  Solid = true
  Symmetric = false
FEATURE [Part::MultiFuse] Fusion004
  Refine = true
  Shapes = -> [Cut050,Extrude088]
FEATURE [Part::Cut] Cut051
  Base = -> Fusion004
  Refine = true
  Tool = -> Extrude087
FEATURE [Part::Cut] Cut052
  Base = -> Cut051
  Refine = true
  Tool = -> Extrude086
FEATURE [Sketcher::SketchObject] Sketch154
  ArcFitTolerance = 1e-06
  AttachmentSupport = -> [Pad016]
  ExternalGeometry = -> [Binder001]
  FullyConstrained = true
  MakeInternals = false
  MapMode = 5
  Placement = pos=(0,-3.6,0) rot=(1,0,0;1.5708rad)
  sketch-geometry (25):
    g0: LineSegment StartX=-214.643 StartY=-72.4316 StartZ=0 EndX=-212.243 EndY=-72.4316 EndZ=0
    g1: LineSegment StartX=-212.243 StartY=-72.4316 StartZ=0 EndX=-212.243 EndY=-71.2316 EndZ=0
    g2: LineSegment StartX=-212.243 StartY=-71.2316 StartZ=0 EndX=-214.643 EndY=-71.2316 EndZ=0
    g3: LineSegment StartX=-214.643 StartY=-71.2316 StartZ=0 EndX=-214.643 EndY=-72.4316 EndZ=0
    g4: GeomPoint [constr] X=-213.443 Y=-71.8316 Z=0
    g5: LineSegment StartX=-214.643 StartY=-69.6316 StartZ=0 EndX=-212.243 EndY=-69.6316 EndZ=0
    g6: LineSegment StartX=-212.243 StartY=-69.6316 StartZ=0 EndX=-212.243 EndY=-68.4316 EndZ=0
    g7: LineSegment StartX=-212.243 StartY=-68.4316 StartZ=0 EndX=-214.643 EndY=-68.4316 EndZ=0
    g8: LineSegment StartX=-214.643 StartY=-68.4316 StartZ=0 EndX=-214.643 EndY=-69.6316 EndZ=0
    g9: GeomPoint [constr] X=-213.443 Y=-69.0316 Z=0
    g10: LineSegment StartX=-214.643 StartY=-66.8316 StartZ=0 EndX=-212.243 EndY=-66.8316 EndZ=0
    g11: LineSegment StartX=-212.243 StartY=-66.8316 StartZ=0 EndX=-212.243 EndY=-65.6316 EndZ=0
    g12: LineSegment StartX=-212.243 StartY=-65.6316 StartZ=0 EndX=-214.643 EndY=-65.6316 EndZ=0
    g13: LineSegment StartX=-214.643 StartY=-65.6316 StartZ=0 EndX=-214.643 EndY=-66.8316 EndZ=0
    g14: GeomPoint [constr] X=-213.443 Y=-66.2316 Z=0
    g15: LineSegment StartX=-214.643 StartY=-64.0316 StartZ=0 EndX=-212.243 EndY=-64.0316 EndZ=0
    g16: LineSegment StartX=-212.243 StartY=-64.0316 StartZ=0 EndX=-212.243 EndY=-62.8316 EndZ=0
    g17: LineSegment StartX=-212.243 StartY=-62.8316 StartZ=0 EndX=-214.643 EndY=-62.8316 EndZ=0
    g18: LineSegment StartX=-214.643 StartY=-62.8316 StartZ=0 EndX=-214.643 EndY=-64.0316 EndZ=0
    g19: GeomPoint [constr] X=-213.443 Y=-63.4316 Z=0
    g20: LineSegment StartX=-214.643 StartY=-61.2316 StartZ=0 EndX=-212.243 EndY=-61.2316 EndZ=0
    g21: LineSegment StartX=-212.243 StartY=-61.2316 StartZ=0 EndX=-212.243 EndY=-60.0316 EndZ=0
    g22: LineSegment StartX=-212.243 StartY=-60.0316 StartZ=0 EndX=-214.643 EndY=-60.0316 EndZ=0
    g23: LineSegment StartX=-214.643 StartY=-60.0316 StartZ=0 EndX=-214.643 EndY=-61.2316 EndZ=0
    g24: GeomPoint [constr] X=-213.443 Y=-60.6316 Z=0
  constraints (65):
    c: Coincident(g0,g1)
    c: Coincident(g1,g2)
    c: Coincident(g2,g3)
    c: Coincident(g3,g0)
    c: Horizontal(g0)
    c: Horizontal(g2)
    c: Vertical(g1)
    c: Vertical(g3)
    c: Symmetric(g2,g0,g4)
    c: Distance(g1,g3) = 2.4
    c: Distance(g0,g2) = 1.2
    c: Coincident(g5,g6)
    c: Coincident(g6,g7)
    c: Coincident(g7,g8)
    c: Coincident(g8,g5)
    c: Horizontal(g5)
    c: Horizontal(g7)
    c: Vertical(g6)
    c: Vertical(g8)
    c: Symmetric(g7,g5,g9)
    c: Distance(g6,g8) = 2.4
    c: Distance(g5,g7) = 1.2
    c: Coincident(g10,g11)
    c: Coincident(g11,g12)
    c: Coincident(g12,g13)
    c: Coincident(g13,g10)
    c: Horizontal(g10)
    c: Horizontal(g12)
    c: Vertical(g11)
    c: Vertical(g13)
    c: Symmetric(g12,g10,g14)
    c: Distance(g11,g13) = 2.4
    c: Distance(g10,g12) = 1.2
    c: Coincident(g15,g16)
    c: Coincident(g16,g17)
    c: Coincident(g17,g18)
    c: Coincident(g18,g15)
    c: Horizontal(g15)
    c: Horizontal(g17)
    c: Vertical(g16)
    c: Vertical(g18)
    c: Symmetric(g17,g15,g19)
    c: Distance(g16,g18) = 2.4
    c: Distance(g15,g17) = 1.2
    c: Vertical(g4,g-3)
    c: Vertical(g9,g-3)
    c: Vertical(g14,g-3)
    c: Vertical(g19,g-3)
    c: DistanceY(g-3,g4) = 5
    c: DistanceY(g4,g9) = 2.8
    c: DistanceY(g9,g14) = 2.8
    c: DistanceY(g14,g19) = 2.8
    c: Coincident(g20,g21)
    c: Coincident(g21,g22)
    c: Coincident(g22,g23)
    c: Coincident(g23,g20)
    c: Horizontal(g20)
    c: Horizontal(g22)
    c: Vertical(g21)
    c: Vertical(g23)
    c: Symmetric(g22,g20,g24)
    c: Distance(g21,g23) = 2.4
    c: Distance(g20,g22) = 1.2
    c: DistanceY(g19,g24) = 2.8
    c: Vertical(g-3,g24)
FEATURE [PartDesign::Pocket] Pocket020
  BaseFeature = -> Pocket012
  Direction = (0,1,-2e-16)
  Length = 3.6
  Length2 = 5
  Profile = -> Sketch154
  ReferenceAxis = -> Sketch154 [N_Axis]
  Refine = true
  Suppressed = false
  Type = 0
FEATURE [PartDesign::Body] Body007  label="lato DX"
  AllowCompound = false
  Group = -> [Binder001,Sketch114,Pad011,Chamfer014,Sketch115,Pocket006,Sketch116,Pad012,Sketch117,Pocket007,Sketch118,Pad013,Sketch119,Pocket008,Pad017,Chamfer009,Pocket009,Sketch123,Sketch120,Pad014,Pad018,Chamfer008,Pocket010,Sketch121,Pad015,Sketch122,Pad016,SubtractivePipe004,SubtractivePipe005,Sketch149,Sketch148,Sketch124,Sketch125,Sketch126,Sketch129,Sketch130,Clone2D001,Sketch131,SubtractiveLoft002,+13 more]
  Origin = -> Origin007
  Tip = -> Pocket020
FEATURE [Sketcher::SketchObject] Sketch155  label="fermo per protezione batteria"
  ArcFitTolerance = 1e-06
  AttachmentSupport = -> [XZ_Plane]
  ExternalGeometry = -> [Sketch016,Sketch]
  FullyConstrained = true
  MakeInternals = false
  MapMode = 5
  Placement = pos=(0,0,0) rot=(1,0,0;1.5708rad)
  sketch-geometry (5):
    g0: LineSegment StartX=-183.305 StartY=-76.0316 StartZ=0 EndX=-179.305 EndY=-76.0316 EndZ=0
    g1: LineSegment StartX=-179.305 StartY=-76.0316 StartZ=0 EndX=-179.305 EndY=-74.4316 EndZ=0
    g2: LineSegment StartX=-179.305 StartY=-74.4316 StartZ=0 EndX=-183.305 EndY=-74.4316 EndZ=0
    g3: LineSegment [constr] StartX=-183.305 StartY=-76.0316 StartZ=0 EndX=-183.305 EndY=-78.4316 EndZ=0
    g4: LineSegment StartX=-183.305 StartY=-74.4316 StartZ=0 EndX=-183.305 EndY=-76.0316 EndZ=0
  constraints (16):
    c: Horizontal(g0)
    c: Distance(g1) = 1.6
    c: Coincident(g1,g0)
    c: Vertical(g1)
    c: Coincident(g2,g1)
    c: Horizontal(g2)
    c: Vertical(g3)
    c: PointOnObject(g3,g-4)
    c: Horizontal(g3,g0)
    c: Tangent(g3,g-3)
    c: Vertical(g0,g-3)
    c: Coincident(g4,g2)
    c: Coincident(g4,g0)
    c: Vertical(g4)
    c: Vertical(g0,g3)
    c: DistanceY(g3,g3) = 2.4
FEATURE [Part::Extrusion] Extrude089  label="Extrude089 - fermo per protezione batteria"
  Base = -> Sketch155
  Dir = (0,-1,2e-16)
  DirMode = 2
  FaceMakerClass = Part::FaceMakerBullseye
  FaceMakerMode = 3
  LengthFwd = 8
  LengthRev = 0
  Solid = true
  Symmetric = true
FEATURE [Sketcher::SketchObject] Sketch156  label="buco per protezione batteria"
  ArcFitTolerance = 1e-06
  AttachmentSupport = -> [XZ_Plane]
  ExternalGeometry = -> [Sketch,Sketch016]
  FullyConstrained = true
  MakeInternals = false
  MapMode = 5
  Placement = pos=(0,0,0) rot=(1,0,0;1.5708rad)
  sketch-geometry (5):
    g0: LineSegment [constr] StartX=-183.305 StartY=-76.8316 StartZ=0 EndX=-183.305 EndY=-78.4316 EndZ=0
    g1: LineSegment StartX=-200.305 StartY=-78.4316 StartZ=0 EndX=-200.305 EndY=-80.4316 EndZ=0
    g2: LineSegment StartX=-200.305 StartY=-80.4316 StartZ=0 EndX=-198.505 EndY=-80.4316 EndZ=0
    g3: LineSegment StartX=-198.505 StartY=-80.4316 StartZ=0 EndX=-198.505 EndY=-78.4316 EndZ=0
    g4: LineSegment StartX=-198.505 StartY=-78.4316 StartZ=0 EndX=-200.305 EndY=-78.4316 EndZ=0
  constraints (15):
    c: Vertical(g0)
    c: Tangent(g0,g-4)
    c: PointOnObject(g0,g-3)
    c: Horizontal(g0,g-4)
    c: Coincident(g1,g2)
    c: Coincident(g2,g3)
    c: Coincident(g3,g4)
    c: Coincident(g4,g1)
    c: Vertical(g1)
    c: Vertical(g3)
    c: Horizontal(g2)
    c: Distance(g1,g3) = 1.8
    c: Distance(g2,g4) = 2
    c: Tangent(g4,g-3)
    c: Distance(g3,g0) = 15.2
FEATURE [Part::Extrusion] Extrude090  label="Extrude090 - buco per protezione batteria"
  Base = -> Sketch156
  Dir = (0,-1,2e-16)
  DirMode = 2
  FaceMakerClass = Part::FaceMakerBullseye
  FaceMakerMode = 3
  LengthFwd = 4.8
  LengthRev = 0
  Solid = true
  Symmetric = true
FEATURE [Sketcher::SketchObject] Sketch157
  ArcFitTolerance = 1e-06
  AttachmentSupport = -> [XY_Plane010]
  FullyConstrained = true
  MakeInternals = false
  MapMode = 5
  sketch-geometry (9):
    g0: LineSegment [constr] StartX=1.8 StartY=8 StartZ=0 EndX=1.8 EndY=-8 EndZ=0
    g1: LineSegment StartX=1.8 StartY=8 StartZ=0 EndX=17 EndY=8 EndZ=0
    g2: LineSegment StartX=1.8 StartY=-8 StartZ=0 EndX=17 EndY=-8 EndZ=0
    g3: LineSegment StartX=0 StartY=8 StartZ=0 EndX=0 EndY=-8 EndZ=0
    g4: LineSegment StartX=1.8 StartY=8 StartZ=0 EndX=0 EndY=8 EndZ=0
    g5: LineSegment StartX=1.8 StartY=-8 StartZ=0 EndX=0 EndY=-8 EndZ=0
    g6: LineSegment StartX=17 StartY=8 StartZ=0 EndX=17 EndY=-8 EndZ=0
    g7: Circle CenterX=8.5 CenterY=0 CenterZ=0 NormalX=0 NormalY=0 NormalZ=1 AngleXU=0 Radius=5
    g8: LineSegment [constr] StartX=17 StartY=8 StartZ=0 EndX=17 EndY=0 EndZ=0
  constraints (23):
    c: DistanceY(g0,g0) = 16
    c: Distance(g1) = 15.2
    c: Coincident(g1,g0)
    c: Horizontal(g1)
    c: Coincident(g2,g0)
    c: Horizontal(g2)
    c: Equal(g1,g2)
    c: Symmetric(g0,g0,g-1)
    c: Equal(g3,g0)
    c: Coincident(g4,g0)
    c: Horizontal(g4)
    c: DistanceX(g4,g4) = 1.8
    c: Coincident(g5,g0)
    c: Horizontal(g5)
    c: Equal(g4,g5)
    c: Coincident(g3,g4)
    c: Tangent(g3,g-2)
    c: Coincident(g6,g1)
    c: Coincident(g6,g2)
    c: Coincident(g8,g1)
    c: Symmetric(g6,g6,g8)
    c: Symmetric(g8,g-1,g7)
    c: Diameter(g7) = 10
FEATURE [PartDesign::Pad] Pad031
  Direction = (0,0,1)
  Length = 1.4
  Length2 = 10
  Profile = -> Sketch157
  ReferenceAxis = -> Sketch157 [N_Axis]
  Refine = true
  Suppressed = false
  Type = 0
FEATURE [Sketcher::SketchObject] Sketch158
  ArcFitTolerance = 1e-06
  AttachmentSupport = -> [Pad031]
  ExternalGeometry = -> [Pad031]
  FullyConstrained = true
  MakeInternals = false
  MapMode = 5
  Placement = pos=(0,0,1.4) rot=(0,0,1;0rad)
  sketch-geometry (4):
    g0: LineSegment StartX=0 StartY=8 StartZ=0 EndX=0 EndY=-8 EndZ=0
    g1: LineSegment StartX=0 StartY=8 StartZ=0 EndX=1.8 EndY=8 EndZ=0
    g2: LineSegment StartX=1.8 StartY=8 StartZ=0 EndX=1.8 EndY=-8 EndZ=0
    g3: LineSegment StartX=0 StartY=-8 StartZ=0 EndX=1.8 EndY=-8 EndZ=0
  constraints (10):
    c: Coincident(g0,g-3)
    c: Coincident(g0,g-4)
    c: Distance(g1) = 1.8
    c: Coincident(g1,g0)
    c: PointOnObject(g1,g-3)
    c: Coincident(g2,g1)
    c: Vertical(g2)
    c: Coincident(g3,g0)
    c: PointOnObject(g3,g-4)
    c: Coincident(g3,g2)
FEATURE [PartDesign::Pad] Pad032
  BaseFeature = -> Pad031
  Direction = (0,0,1)
  Length = 6.4
  Length2 = 10
  Profile = -> Sketch158
  ReferenceAxis = -> Sketch158 [N_Axis]
  Refine = true
  Suppressed = false
  Type = 0
FEATURE [Sketcher::SketchObject] Sketch159
  ArcFitTolerance = 1e-06
  AttachmentSupport = -> [Pad032]
  ExternalGeometry = -> [Pad032,Pad031]
  FullyConstrained = true
  MakeInternals = false
  MapMode = 5
  Placement = pos=(0,0,7.8) rot=(0,0,1;0rad)
  sketch-geometry (7):
    g0: LineSegment StartX=0.1 StartY=2.2 StartZ=0 EndX=0.1 EndY=-2.2 EndZ=0
    g1: LineSegment StartX=0.1 StartY=-2.2 StartZ=0 EndX=1.7 EndY=-2.2 EndZ=0
    g2: LineSegment StartX=1.7 StartY=-2.2 StartZ=0 EndX=1.7 EndY=2.2 EndZ=0
    g3: LineSegment StartX=1.7 StartY=2.2 StartZ=0 EndX=0.1 EndY=2.2 EndZ=0
    g4: GeomPoint [constr] X=0.9 Y=8 Z=0
    g5: GeomPoint [constr] X=0.9 Y=-8 Z=0
    g6: LineSegment [constr] StartX=0.9 StartY=8 StartZ=0 EndX=0.9 EndY=-8 EndZ=0
  constraints (14):
    c: Coincident(g0,g1)
    c: Coincident(g1,g2)
    c: Coincident(g2,g3)
    c: Coincident(g3,g0)
    c: Vertical(g2)
    c: Horizontal(g1)
    c: Distance(g0,g2) = 1.6
    c: Distance(g1,g3) = 4.4
    c: Symmetric(g0,g0,g-1)
    c: Symmetric(g-4,g-4,g4)
    c: Symmetric(g-3,g-5,g5)
    c: Coincident(g6,g4)
    c: Coincident(g6,g5)
    c: Symmetric(g0,g2,g6)
FEATURE [PartDesign::Pad] Pad033
  BaseFeature = -> Pad032
  Direction = (0,0,1)
  Length = 1.4
  Length2 = 10
  Profile = -> Sketch159
  ReferenceAxis = -> Sketch159 [N_Axis]
  Refine = true
  Suppressed = false
  Type = 0
FEATURE [Part::Cut] Cut053
  Base = -> Cut052
  Refine = true
  Tool = -> Extrude089
FEATURE [Part::Cut] Cut054
  Base = -> Cut053
  Refine = true
  Tool = -> Extrude090
FEATURE [Sketcher::SketchObject] Sketch160
  ArcFitTolerance = 1e-06
  AttachmentSupport = -> [Pad033]
  ExternalGeometry = -> [Pad033]
  FullyConstrained = true
  MakeInternals = false
  MapMode = 5
  Placement = pos=(0,0,1.4) rot=(0,0,1;0rad)
  sketch-geometry (4):
    g0: LineSegment StartX=15.6 StartY=3.7 StartZ=0 EndX=15.6 EndY=-3.7 EndZ=0
    g1: LineSegment StartX=15.6 StartY=-3.7 StartZ=0 EndX=17 EndY=-3.7 EndZ=0
    g2: LineSegment StartX=17 StartY=-3.7 StartZ=0 EndX=17 EndY=3.7 EndZ=0
    g3: LineSegment StartX=17 StartY=3.7 StartZ=0 EndX=15.6 EndY=3.7 EndZ=0
  constraints (10):
    c: Coincident(g0,g1)
    c: Coincident(g1,g2)
    c: Coincident(g2,g3)
    c: Coincident(g3,g0)
    c: Horizontal(g1)
    c: Horizontal(g3)
    c: Distance(g0,g2) = 1.4
    c: Distance(g1,g3) = 7.4
    c: Symmetric(g0,g0,g-1)
    c: Tangent(g2,g-3)
FEATURE [PartDesign::Pad] Pad034
  BaseFeature = -> Pad033
  Direction = (0,0,1)
  Length = 2.4
  Length2 = 10
  Profile = -> Sketch160
  ReferenceAxis = -> Sketch160 [N_Axis]
  Refine = true
  Suppressed = false
  Type = 0
FEATURE [Sketcher::SketchObject] Sketch161
  ArcFitTolerance = 1e-06
  AttachmentSupport = -> [Pad034]
  ExternalGeometry = -> [Pad034]
  FullyConstrained = true
  MakeInternals = false
  MapMode = 5
  Placement = pos=(0,0,3.8) rot=(0,0,1;0rad)
  sketch-geometry (6):
    g0: LineSegment StartX=17 StartY=3.7 StartZ=0 EndX=21 EndY=3.7 EndZ=0
    g1: LineSegment StartX=17 StartY=3.7 StartZ=0 EndX=15.6 EndY=3.7 EndZ=0
    g2: LineSegment StartX=15.6 StartY=3.7 StartZ=0 EndX=15.6 EndY=-3.7 EndZ=0
    g3: LineSegment StartX=15.6 StartY=-3.7 StartZ=0 EndX=17 EndY=-3.7 EndZ=0
    g4: LineSegment StartX=17 StartY=-3.7 StartZ=0 EndX=21 EndY=-3.7 EndZ=0
    g5: LineSegment StartX=21 StartY=3.7 StartZ=0 EndX=21 EndY=-3.7 EndZ=0
  constraints (14):
    c: Distance(g0) = 4
    c: Coincident(g0,g-4)
    c: Horizontal(g0)
    c: Coincident(g1,g0)
    c: Coincident(g1,g-3)
    c: Coincident(g2,g1)
    c: Coincident(g2,g-5)
    c: Coincident(g3,g2)
    c: Coincident(g3,g-5)
    c: Coincident(g4,g3)
    c: Horizontal(g4)
    c: Equal(g4,g0)
    c: Coincident(g5,g0)
    c: Coincident(g5,g4)
FEATURE [PartDesign::Pad] Pad035
  BaseFeature = -> Pad034
  Direction = (0,0,1)
  Length = 1.4
  Length2 = 10
  Profile = -> Sketch161
  ReferenceAxis = -> Sketch161 [N_Axis]
  Refine = true
  Suppressed = false
  Type = 0
FEATURE [PartDesign::Body] Body010  label="Protezione_inferiore_batteria"
  AllowCompound = false
  Group = -> [Sketch157,Pad031,Sketch158,Pad032,Sketch159,Pad033,Sketch160,Pad034,Sketch161,Pad035]
  Origin = -> Origin010
  Tip = -> Pad035
FEATURE [Sketcher::SketchObject] Sketch162  label="scavo_saldature_nuovo_driver_alto"
  ArcFitTolerance = 1e-06
  AttachmentSupport = -> [XZ_Plane]
  ExternalGeometry = -> [Sketch138]
  FullyConstrained = true
  MakeInternals = false
  MapMode = 5
  Placement = pos=(0,0,0) rot=(1,0,0;1.5708rad)
  sketch-geometry (4):
    g0: LineSegment StartX=-192.503 StartY=17.8001 StartZ=0 EndX=-191.336 EndY=4.65187 EndZ=0
    g1: LineSegment StartX=-192.503 StartY=17.8001 StartZ=0 EndX=-190.909 EndY=17.9416 EndZ=0
    g2: LineSegment StartX=-190.909 StartY=17.9416 StartZ=0 EndX=-189.742 EndY=4.79337 EndZ=0
    g3: LineSegment StartX=-189.742 StartY=4.79337 StartZ=0 EndX=-191.336 EndY=4.65187 EndZ=0
  constraints (10):
    c: Parallel(g0,g-3)
    c: Equal(g0,g-3)
    c: Coincident(g1,g0)
    c: Perpendicular(g0,g1)
    c: Coincident(g1,g-3)
    c: Coincident(g2,g1)
    c: Coincident(g2,g-3)
    c: Coincident(g3,g2)
    c: Coincident(g3,g0)
    c: Distance(g1) = 1.6
FEATURE [PartDesign::Body] Body  label="Struttura pistola"
  AllowCompound = false
  Group = -> [Sketch,Sketch002,Sketch004,DatumPlane,Sketch005,DatumPlane001,CopyCut,Sketch008,Sketch009,Sketch010,Sketch011,Sketch012,Sketch013,Sketch014,Sketch015,Sketch016,Sketch017,Sketch018,Sketch019,Sketch020,Sketch022,Sketch023,Sketch024,Sketch025,Sketch026,Sketch027,Sketch029,Sketch030,Sketch031,Sketch032,Sketch033,Sketch034,Sketch035,Sketch036,Sketch037,Sketch038,Sketch039,Sketch040,Sketch041,Sketch042,+31 more]
  Origin = -> Origin
FEATURE [Part::Extrusion] Extrude091  label="Extrude091 - scavo_saldature_nuovo_driver_alto"
  Base = -> Sketch162
  Dir = (0,-1,2e-16)
  DirMode = 2
  FaceMakerClass = Part::FaceMakerBullseye
  FaceMakerMode = 3
  LengthFwd = 4
  LengthRev = 0
  Placement = pos=(0,-3.8,0) rot=(0,0,1;0rad)
  Solid = true
  Symmetric = false
FEATURE [Part::Cut] Cut055
  Base = -> Cut054
  Refine = true
  Tool = -> Extrude091
note: 2 file-system paths scrubbed to <path> (originals preserved in the JSON sidecar)
